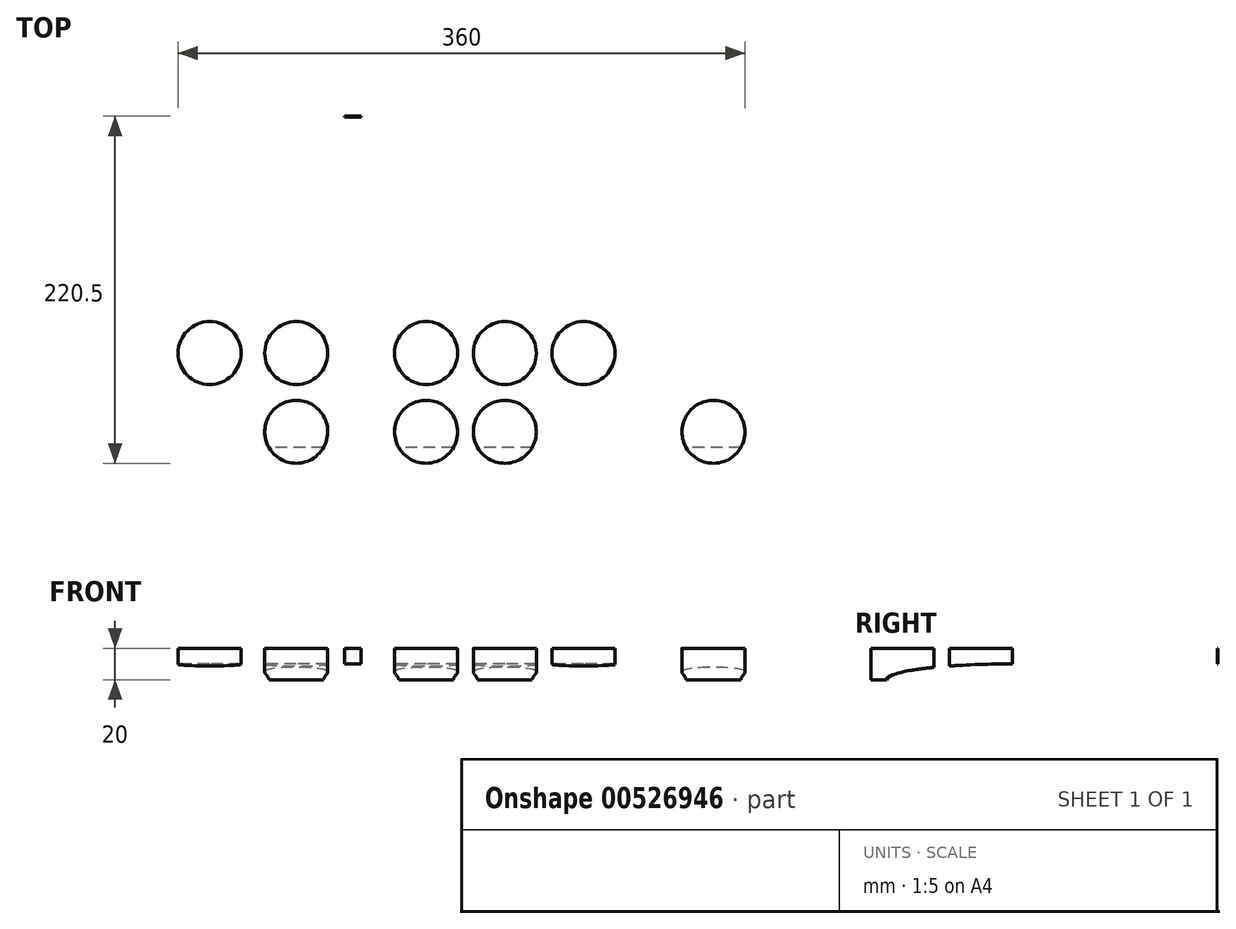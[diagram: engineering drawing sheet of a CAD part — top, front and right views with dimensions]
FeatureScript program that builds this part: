
annotation { "Feature Type Name" : "Feature", "Feature Type Description" : "" }
export const myFeature = defineFeature(function(context is Context, id is Id, definition is map)
    precondition{}
    {
        {
            var Q0;
            Q0=qCreatedBy(makeId("Top.planeOp"),FACE);
            var sketch = newSketch(context, id + "F0", { "sketchPlane" : qUnion([Q0])});
            skLineSegment(sketch, "E0.bottom", {"start": v(-365, 200) * mm, "end": v(365, 200) * mm});
            skLineSegment(sketch, "E0.top", {"start": v(-365, -200) * mm, "end": v(365, -200) * mm});
            skLineSegment(sketch, "E0.left", {"start": v(-365, 200) * mm, "end": v(-365, -200) * mm});
            skLineSegment(sketch, "E0.right", {"start": v(365, 200) * mm, "end": v(365, -200) * mm});
            skPoint(sketch, "E0.middle", {"position": v(0, 0) * mm});
            skEllipticalArc(sketch, "E1", {});
            skEllipticalArc(sketch, "E2.MirrorCS", {});
            skEllipticalArc(sketch, "E3.MirrorCS", {});
            skEllipticalArc(sketch, "E4.MirrorCS", {});
            skLineSegment(sketch, "E5", {"start": v(-365, 200) * mm, "end": v(-105, 200) * mm});
            skLineSegment(sketch, "E6", {"start": v(-365, 200) * mm, "end": v(-365, 50) * mm});
            skLineSegment(sketch, "E7", {"start": v(-365, -200) * mm, "end": v(-365, -50) * mm});
            skLineSegment(sketch, "E8", {"start": v(-365, -200) * mm, "end": v(-182.5, -200) * mm});
            skLineSegment(sketch, "E9", {"start": v(365, 200) * mm, "end": v(105, 200) * mm});
            skLineSegment(sketch, "E10", {"start": v(182.5, -200.11) * mm, "end": v(365, -200) * mm});
            skPoint(sketch, "E11", {"position": v(0, 200) * mm});
            skLineSegment(sketch, "E12", {"start": v(0, 200) * mm, "end": v(-130, 200) * mm});
            skLineSegment(sketch, "E13.MirrorCS", {"start": v(0, -200) * mm, "end": v(-130, -200) * mm});
            skLineSegment(sketch, "E14.MirrorCS", {"start": v(5, 200) * mm, "end": v(130, 200) * mm});
            skLineSegment(sketch, "E15.MirrorCS", {"start": v(-72.5, -200) * mm, "end": v(52.5, -200) * mm});
            skCircle(sketch, "E16", {"center": v(-278.75, 100) * mm, "radius": 20 * mm});
            skCircle(sketch, "E17", {"center": v(-223.75, 150) * mm, "radius": 20 * mm});
            skCircle(sketch, "E18", {"center": v(-223.75, 100) * mm, "radius": 20 * mm});
            skCircle(sketch, "E19", {"center": v(-141.25, 100) * mm, "radius": 20 * mm});
            skCircle(sketch, "E20", {"center": v(-141.25, 150) * mm, "radius": 20 * mm});
            skCircle(sketch, "E21", {"center": v(-91.25, 100) * mm, "radius": 20 * mm});
            skCircle(sketch, "E22", {"center": v(-91.25, 150) * mm, "radius": 20 * mm});
            skCircle(sketch, "E23", {"center": v(-41.25, 100) * mm, "radius": 20 * mm});
            skCircle(sketch, "E24.MirrorC", {"center": v(-41.25, 150) * mm, "radius": 20 * mm});
            skCircle(sketch, "E25.MirrorC", {"center": v(-278.75, -100) * mm, "radius": 20 * mm});
            skCircle(sketch, "E26.MirrorC", {"center": v(-223.75, -150) * mm, "radius": 20 * mm});
            skCircle(sketch, "E27.MirrorC", {"center": v(-223.75, -100) * mm, "radius": 20 * mm});
            skCircle(sketch, "E28.MirrorC", {"center": v(-141.25, -100) * mm, "radius": 20 * mm});
            skCircle(sketch, "E29.MirrorC", {"center": v(-141.25, -150) * mm, "radius": 20 * mm});
            skCircle(sketch, "E30.MirrorC", {"center": v(-91.25, -100) * mm, "radius": 20 * mm});
            skCircle(sketch, "E31.MirrorC", {"center": v(-41.25, -100) * mm, "radius": 20 * mm});
            skCircle(sketch, "E32.MirrorC", {"center": v(-91.25, -150) * mm, "radius": 20 * mm});
            skCircle(sketch, "E33.MirrorC", {"center": v(-41.25, -150) * mm, "radius": 20 * mm});
            skCircle(sketch, "E34.MirrorC", {"center": v(-222.5, -10) * mm, "radius": 20 * mm});
            skLineSegment(sketch, "E35.bottom", {"start": v(210, 15) * mm, "end": v(-210, 15) * mm});
            skLineSegment(sketch, "E35.top", {"start": v(210, -15) * mm, "end": v(-210, -15) * mm});
            skLineSegment(sketch, "E35.left", {"start": v(210, 15) * mm, "end": v(210, -15) * mm});
            skLineSegment(sketch, "E35.right", {"start": v(-210, 15) * mm, "end": v(-210, -15) * mm});
            skLineSegment(sketch, "E36", {"start": v(-365, -50) * mm, "end": v(365, -50) * mm});
            skLineSegment(sketch, "E37", {"start": v(-365, 50) * mm, "end": v(365, 50) * mm});
            skLineSegment(sketch, "E38", {"start": v(-182.5, -200) * mm, "end": v(-182.5, -40.61) * mm});
            skLineSegment(sketch, "E39", {"start": v(0, -200) * mm, "end": v(0, -50) * mm});
            skLineSegment(sketch, "E40", {"start": v(182.5, -200.11) * mm, "end": v(182.4, -40.7) * mm});
            skLineSegment(sketch, "E41.trimOffspring", {"start": v(-182.5, 40.61) * mm, "end": v(-182.5, 200) * mm});
            skLineSegment(sketch, "E42.trimOffspring", {"start": v(-182.5, -15) * mm, "end": v(-182.5, 15) * mm});
            skLineSegment(sketch, "E43.trimOffspring", {"start": v(182.39, -15) * mm, "end": v(182.37, 15) * mm});
            skLineSegment(sketch, "E44.trimOffspring", {"start": v(182.35, 40.73) * mm, "end": v(182.25, 200) * mm});
            skCircle(sketch, "E45", {"center": v(-272.5, 10) * mm, "radius": 20 * mm});
            skCircle(sketch, "E46.MirrorC", {"center": v(-322.5, -8.74) * mm, "radius": 20 * mm});
            skCircle(sketch, "E47.MirrorC", {"center": v(-142.5, -10) * mm, "radius": 20 * mm});
            skCircle(sketch, "E48.MirrorC", {"center": v(-92.5, 10) * mm, "radius": 20 * mm});
            skCircle(sketch, "E49.MirrorC", {"center": v(-42.5, -8.74) * mm, "radius": 20 * mm});
            skCircle(sketch, "E50.MirrorC", {"center": v(42.5, -8.74) * mm, "radius": 20 * mm});
            skCircle(sketch, "E51.MirrorC", {"center": v(142.5, -10) * mm, "radius": 20 * mm});
            skCircle(sketch, "E52.MirrorC", {"center": v(92.5, 10) * mm, "radius": 20 * mm});
            skCircle(sketch, "E53.MirrorC", {"center": v(222.5, -10) * mm, "radius": 20 * mm});
            skCircle(sketch, "E54.MirrorC", {"center": v(272.5, 10) * mm, "radius": 20 * mm});
            skCircle(sketch, "E55.MirrorC", {"center": v(322.5, -8.74) * mm, "radius": 20 * mm});
            skCircle(sketch, "E56.MirrorC", {"center": v(223.75, -100) * mm, "radius": 20 * mm});
            skCircle(sketch, "E57.MirrorC", {"center": v(223.75, -150) * mm, "radius": 20 * mm});
            skCircle(sketch, "E58.MirrorC", {"center": v(278.75, -100) * mm, "radius": 20 * mm});
            skCircle(sketch, "E59.MirrorC", {"center": v(141.25, -100) * mm, "radius": 20 * mm});
            skCircle(sketch, "E60.MirrorC", {"center": v(141.25, -150) * mm, "radius": 20 * mm});
            skCircle(sketch, "E61.MirrorC", {"center": v(91.25, -150) * mm, "radius": 20 * mm});
            skCircle(sketch, "E62.MirrorC", {"center": v(91.25, -100) * mm, "radius": 20 * mm});
            skCircle(sketch, "E63.MirrorC", {"center": v(41.25, -100) * mm, "radius": 20 * mm});
            skCircle(sketch, "E64.MirrorC", {"center": v(41.25, -150) * mm, "radius": 20 * mm});
            skCircle(sketch, "E65.MirrorC", {"center": v(41.25, 100) * mm, "radius": 20 * mm});
            skCircle(sketch, "E66.MirrorC", {"center": v(91.25, 100) * mm, "radius": 20 * mm});
            skCircle(sketch, "E67.MirrorC", {"center": v(141.25, 100) * mm, "radius": 20 * mm});
            skCircle(sketch, "E68.MirrorC", {"center": v(223.75, 100) * mm, "radius": 20 * mm});
            skCircle(sketch, "E69.MirrorC", {"center": v(278.75, 100) * mm, "radius": 20 * mm});
            skCircle(sketch, "E70.MirrorC", {"center": v(223.75, 150) * mm, "radius": 20 * mm});
            skCircle(sketch, "E71.MirrorC", {"center": v(141.25, 150) * mm, "radius": 20 * mm});
            skCircle(sketch, "E72.MirrorC", {"center": v(91.25, 150) * mm, "radius": 20 * mm});
            skCircle(sketch, "E73.MirrorC", {"center": v(41.25, 150) * mm, "radius": 20 * mm});
            const initialGuessF0  = {"E1": [0.215000023161019, -0.00011114199246731203, 0, -1, 0.20000000103052606, 0.15, 6.249845643425636, 1.5707963267948966], "E2.MirrorCS": [-0.215, -0.00011114199246737072, 0, -1, 0.2, 0.15, 4.711833270393751, 0.03333950926130193], "E3.MirrorCS": [-0.215, 0.00011114199246727815, 0, 1, 0.2, 0.15, 6.249845797918284, 1.5707963267948966], "E4.MirrorCS": [0.215, 0.00011114199246735796, 0, 1, 0.2, 0.15, 4.711277560231201, 0.03333950926130226]};
            skSetInitialGuess(sketch, initialGuessF0);
            skSolve(sketch);
        }
        {
            var Q0;
            Q0=qCreatedBy(makeId("Top.planeOp"),FACE);
            cPlane(context, id + "F1", {"entities" : qUnion([Q0]), "cplaneType" : CPlaneType.OFFSET, "offset" : 20 * mm, "width" : 150 * mm, "height" : 150 * mm});
        }
        {
            var Q0;
            Q0=qCreatedBy(id+"F1.planeOp",FACE);
            var sketch = newSketch(context, id + "F2", { "sketchPlane" : qUnion([Q0])});
            skLineSegment(sketch, "E74.bottom", {"start": v(0, 0) * mm, "end": v(365, 0) * mm});
            skLineSegment(sketch, "E74.top", {"start": v(0, -200) * mm, "end": v(210, -200) * mm});
            skLineSegment(sketch, "E74.left", {"start": v(0, 0) * mm, "end": v(0, -200) * mm});
            skLineSegment(sketch, "E75", {"start": v(0, -15) * mm, "end": v(364.58, -15) * mm});
            skLineSegment(sketch, "E76", {"start": v(0, -170) * mm, "end": v(294.02, -170) * mm});
            skLineSegment(sketch, "E77", {"start": v(330, 0) * mm, "end": v(330, -128.4) * mm});
            skLineSegment(sketch, "E78", {"start": v(215, 0) * mm, "end": v(215, -200) * mm});
            skPoint(sketch, "E79", {"position": v(215, -200) * mm});
            skPoint(sketch, "E80", {"position": v(365, 0) * mm});
            skLineSegment(sketch, "E81", {"start": v(275, 0) * mm, "end": v(275, -183.3) * mm});
            skLineSegment(sketch, "E82", {"start": v(275, -140) * mm, "end": v(322.12, -140) * mm});
            skPoint(sketch, "E83", {"position": v(215, -170) * mm});
            skPoint(sketch, "E84", {"position": v(330, 0) * mm});
            skPoint(sketch, "E85", {"position": v(275, -140) * mm});
            skPoint(sketch, "E86", {"position": v(330, -140) * mm});
            skPoint(sketch, "E87", {"position": v(275, -185) * mm});
            skLineSegment(sketch, "E88", {"start": v(315, -149.07) * mm, "end": v(315, 0) * mm});
            skLineSegment(sketch, "E89", {"start": v(210, 0) * mm, "end": v(210, -200) * mm});
            skEllipticalArc(sketch, "E90.trimOffspring", {});
            skEllipticalArc(sketch, "E91", {});
            skPoint(sketch, "E92.orphan", {"position": v(365, -170) * mm});
            skPoint(sketch, "E93.trimOffspring.end.orphan", {"position": v(330, -200) * mm});
            skPoint(sketch, "E94.orphan", {"position": v(365, -200) * mm});
            skPoint(sketch, "E95.orphan", {"position": v(365, -15) * mm});
            skLineSegment(sketch, "E96.MirrorCS", {"start": v(0, 0) * mm, "end": v(-365, 0) * mm});
            skLineSegment(sketch, "E97.MirrorCS", {"start": v(0, -15) * mm, "end": v(-364.58, -15) * mm});
            skLineSegment(sketch, "E98.MirrorCS", {"start": v(0, -170) * mm, "end": v(-294.02, -170) * mm});
            skLineSegment(sketch, "E99.MirrorCS", {"start": v(0, -200) * mm, "end": v(-210, -200) * mm});
            skLineSegment(sketch, "E100.MirrorCS", {"start": v(-210, 0) * mm, "end": v(-210, -200) * mm});
            skLineSegment(sketch, "E101.MirrorCS", {"start": v(-215, 0) * mm, "end": v(-215, -200) * mm});
            skEllipticalArc(sketch, "E102.MirrorCS", {});
            skEllipticalArc(sketch, "E103.MirrorCS", {});
            skLineSegment(sketch, "E104.MirrorCS", {"start": v(-275, 0) * mm, "end": v(-275, -183.3) * mm});
            skLineSegment(sketch, "E105.MirrorCS", {"start": v(-275, -140) * mm, "end": v(-322.12, -140) * mm});
            skLineSegment(sketch, "E106.MirrorCS", {"start": v(-315, -149.07) * mm, "end": v(-315, 0) * mm});
            skLineSegment(sketch, "E107.MirrorCS", {"start": v(-330, 0) * mm, "end": v(-330, -128.4) * mm});
            skLineSegment(sketch, "E108.MirrorCS", {"start": v(0, 15) * mm, "end": v(-364.58, 15) * mm});
            skLineSegment(sketch, "E109.MirrorCS", {"start": v(0, 15) * mm, "end": v(364.58, 15) * mm});
            skEllipticalArc(sketch, "E110.MirrorCS", {});
            skLineSegment(sketch, "E111.MirrorCS", {"start": v(-330, 0) * mm, "end": v(-330, 128.4) * mm});
            skLineSegment(sketch, "E112.MirrorCS", {"start": v(-315, 149.07) * mm, "end": v(-315, 0) * mm});
            skLineSegment(sketch, "E113.MirrorCS", {"start": v(-275, 0) * mm, "end": v(-275, 183.3) * mm});
            skLineSegment(sketch, "E114.MirrorCS", {"start": v(-215, 0) * mm, "end": v(-215, 200) * mm});
            skLineSegment(sketch, "E115.MirrorCS", {"start": v(-210, 0) * mm, "end": v(-210, 200) * mm});
            skLineSegment(sketch, "E116.MirrorCS", {"start": v(0, 0) * mm, "end": v(0, 200) * mm});
            skLineSegment(sketch, "E117.MirrorCS", {"start": v(210, 0) * mm, "end": v(210, 200) * mm});
            skLineSegment(sketch, "E118.MirrorCS", {"start": v(215, 0) * mm, "end": v(215, 200) * mm});
            skLineSegment(sketch, "E119.MirrorCS", {"start": v(275, 0) * mm, "end": v(275, 183.3) * mm});
            skLineSegment(sketch, "E120.MirrorCS", {"start": v(315, 149.07) * mm, "end": v(315, 0) * mm});
            skLineSegment(sketch, "E121.MirrorCS", {"start": v(330, 0) * mm, "end": v(330, 128.4) * mm});
            skEllipticalArc(sketch, "E122.MirrorCS", {});
            skEllipticalArc(sketch, "E123.MirrorCS", {});
            skEllipticalArc(sketch, "E124.MirrorCS", {});
            skLineSegment(sketch, "E125.MirrorCS", {"start": v(-275, 140) * mm, "end": v(-322.12, 140) * mm});
            skLineSegment(sketch, "E126.MirrorCS", {"start": v(0, 170) * mm, "end": v(-294.02, 170) * mm});
            skLineSegment(sketch, "E127.MirrorCS", {"start": v(0, 170) * mm, "end": v(294.02, 170) * mm});
            skLineSegment(sketch, "E128.MirrorCS", {"start": v(0, 200) * mm, "end": v(210, 200) * mm});
            skLineSegment(sketch, "E129.MirrorCS", {"start": v(0, 200) * mm, "end": v(-210, 200) * mm});
            skLineSegment(sketch, "E130.MirrorCS", {"start": v(275, 140) * mm, "end": v(322.12, 140) * mm});
            const initialGuessF2  = {"E90.trimOffspring": [0.215, 0, 1, 0, 0.115, 0.17, 4.71238898038469, 6.283185307179586], "E91": [0.215, 0, 0, -1, 0.2, 0.15, 6.249845797918284, 1.5707963267948966], "E102.MirrorCS": [-0.215, 0, -1, 0, 0.115, 0.17, 6.283185307179586, 1.5707963267948966], "E103.MirrorCS": [-0.215, 0, 0, -1, 0.2, 0.15, 4.71238898038469, 0.03333950926130225], "E110.MirrorCS": [-0.215, 0, 0, 1, 0.2, 0.15, 6.249845797918284, 1.5707963267948966], "E122.MirrorCS": [0.215, 0, 0, 1, 0.2, 0.15, 4.71238898038469, 0.03333950926130225], "E123.MirrorCS": [0.215, 0, 1, 0, 0.115, 0.17, 6.283185307179586, 1.5707963267948966], "E124.MirrorCS": [-0.215, 0, -1, 0, 0.115, 0.17, 4.71238898038469, 6.283185307179586]};
            skSetInitialGuess(sketch, initialGuessF2);
            skSolve(sketch);
        }
        {
            var Q0;
            Q0=qCreatedBy(makeId("Right.planeOp"),FACE);
            var sketch = newSketch(context, id + "F3", { "sketchPlane" : qUnion([Q0])});
            skPoint(sketch, "E131.middle", {"position": v(0, 20) * mm});
            skPoint(sketch, "E132", {"position": v(170, 0) * mm});
            skPoint(sketch, "E133", {"position": v(160, 0) * mm});
            skLineSegment(sketch, "E134.bottom", {"start": v(15, 10.07) * mm, "end": v(80, 10.07) * mm});
            skPoint(sketch, "E135", {"position": v(80, 10.07) * mm});
            skEllipticalArc(sketch, "E136", {});
            skEllipticalArc(sketch, "E137", {});
            skLineSegment(sketch, "E138", {"start": v(0, 20) * mm, "end": v(0, 10.04) * mm});
            skLineSegment(sketch, "E139", {"start": v(0, 20) * mm, "end": v(200, 20) * mm});
            skLineSegment(sketch, "E140", {"start": v(200, 20) * mm, "end": v(0, 20) * mm});
            skLineSegment(sketch, "E141", {"start": v(160, 0) * mm, "end": v(170, 0) * mm});
            skPoint(sketch, "E142.orphan", {"position": v(-200, 20) * mm});
            skLineSegment(sketch, "E143.MirrorCS", {"start": v(-200, 20) * mm, "end": v(0, 20) * mm});
            skLineSegment(sketch, "E144.MirrorCS", {"start": v(-15, 10.07) * mm, "end": v(-80, 10.07) * mm});
            skEllipticalArc(sketch, "E145.MirrorCS", {});
            skLineSegment(sketch, "E146.MirrorCS", {"start": v(-160, 0) * mm, "end": v(-170, 0) * mm});
            skEllipticalArc(sketch, "E147.MirrorCS", {});
            skLineSegment(sketch, "E148.top", {"start": v(-15, 12) * mm, "end": v(15, 12) * mm});
            skLineSegment(sketch, "E148.left", {"start": v(-15, 10.07) * mm, "end": v(-15, 12) * mm});
            skLineSegment(sketch, "E148.right", {"start": v(15, 10.07) * mm, "end": v(15, 12) * mm});
            skLineSegment(sketch, "E149.bottom", {"start": v(15, 18) * mm, "end": v(-15, 18) * mm});
            skLineSegment(sketch, "E149.top", {"start": v(15, 12) * mm, "end": v(-15, 12) * mm});
            skLineSegment(sketch, "E149.left", {"start": v(15, 18) * mm, "end": v(15, 12) * mm});
            skLineSegment(sketch, "E149.right", {"start": v(-15, 18) * mm, "end": v(-15, 12) * mm});
            skLineSegment(sketch, "E150", {"start": v(170, 0) * mm, "end": v(170.12, 20) * mm});
            skLineSegment(sketch, "E151", {"start": v(-170, 0) * mm, "end": v(-170.12, 20) * mm});
            skLineSegment(sketch, "E152", {"start": v(-15, 12) * mm, "end": v(-15, 10.07) * mm});
            skLineSegment(sketch, "E153.bottom", {"start": v(-200, 20) * mm, "end": v(-170, 20) * mm});
            skLineSegment(sketch, "E153.top", {"start": v(-200, 0) * mm, "end": v(-170, 0) * mm});
            skLineSegment(sketch, "E153.left", {"start": v(-200, 20) * mm, "end": v(-200, 0) * mm});
            skLineSegment(sketch, "E153.right", {"start": v(-170, 20) * mm, "end": v(-170, 0) * mm});
            skLineSegment(sketch, "E154.MirrorCS", {"start": v(200, 0) * mm, "end": v(170, 0) * mm});
            skLineSegment(sketch, "E155.MirrorCS", {"start": v(200, 20) * mm, "end": v(200, 0) * mm});
            skLineSegment(sketch, "E156", {"start": v(80, 10.07) * mm, "end": v(80, 20) * mm});
            skLineSegment(sketch, "E157", {"start": v(160, 0) * mm, "end": v(160, 20) * mm});
            skLineSegment(sketch, "E158", {"start": v(149.2, 20) * mm, "end": v(149.2, 5.05) * mm});
            skLineSegment(sketch, "E159", {"start": v(140.08, 20) * mm, "end": v(140.08, 6.65) * mm});
            skLineSegment(sketch, "E160", {"start": v(128.23, 20) * mm, "end": v(128.23, 8.04) * mm});
            skLineSegment(sketch, "E161", {"start": v(102.69, 20) * mm, "end": v(102.69, 9.66) * mm});
            skLineSegment(sketch, "E162.MirrorCS", {"start": v(-80, 10.07) * mm, "end": v(-80, 20) * mm});
            skLineSegment(sketch, "E163.MirrorCS", {"start": v(-102.69, 20) * mm, "end": v(-102.69, 9.66) * mm});
            skLineSegment(sketch, "E164.MirrorCS", {"start": v(-128.23, 20) * mm, "end": v(-128.23, 8.04) * mm});
            skLineSegment(sketch, "E165.MirrorCS", {"start": v(-140.08, 20) * mm, "end": v(-140.08, 6.65) * mm});
            skLineSegment(sketch, "E166.MirrorCS", {"start": v(-149.2, 20) * mm, "end": v(-149.2, 5.05) * mm});
            skLineSegment(sketch, "E167.MirrorCS", {"start": v(-160, 0) * mm, "end": v(-160, 20) * mm});
            skLineSegment(sketch, "E168", {"start": v(45, 20) * mm, "end": v(45, 10.07) * mm});
            skLineSegment(sketch, "E169.MirrorCS", {"start": v(-45, 20) * mm, "end": v(-45, 10.07) * mm});
            const initialGuessF3  = {"E136": [0.17012490332126617, 0.02, -0.006245044279577429, -0.9999804995208388, 0.020000390017188747, 0.02987581400604767, 6.283185307179586, 1.580124845260153], "E137": [0.08, 0, 0, 1, 0.01007139225942586, 0.08, 4.71238898038469, 6.283185307179586], "E145.MirrorCS": [-0.08, 0, 0, 1, 0.01007139225942586, 0.08, 6.283185307179586, 1.5707963267948966], "E147.MirrorCS": [-0.17012490332126617, 0.02, 0.006245044279579518, -0.9999804995208388, 0.020000390017188747, 0.02987581400604767, 4.703060461919433, 6.283185307179586]};
            skSetInitialGuess(sketch, initialGuessF3);
            skSolve(sketch);
        }
        {
            var Q0;
            Q0=qCreatedBy(makeId("Front.planeOp"),FACE);
            var sketch = newSketch(context, id + "F4", { "sketchPlane" : qUnion([Q0])});
            skLineSegment(sketch, "E170", {"start": v(0, 20) * mm, "end": v(365, 20) * mm});
            skPoint(sketch, "E171", {"position": v(210, 20) * mm});
            skLineSegment(sketch, "E172", {"start": v(210, 18) * mm, "end": v(210, 12) * mm});
            skPoint(sketch, "E173", {"position": v(315, 20) * mm});
            skLineSegment(sketch, "E174", {"start": v(315, 18) * mm, "end": v(315, 0) * mm});
            skLineSegment(sketch, "E175", {"start": v(0, 12) * mm, "end": v(0, 20) * mm});
            skLineSegment(sketch, "E176", {"start": v(210, 12) * mm, "end": v(0, 12) * mm});
            skPoint(sketch, "E177", {"position": v(365.07, 0) * mm});
            skPoint(sketch, "E178", {"position": v(365, 20) * mm});
            skEllipticalArc(sketch, "E179", {});
            skLineSegment(sketch, "E180", {"start": v(315, 18) * mm, "end": v(210, 18) * mm});
            skLineSegment(sketch, "E181.MirrorCS", {"start": v(0, 20) * mm, "end": v(-365, 20) * mm});
            skLineSegment(sketch, "E182.MirrorCS", {"start": v(-210, 12) * mm, "end": v(0, 12) * mm});
            skLineSegment(sketch, "E183.MirrorCS", {"start": v(-210, 18) * mm, "end": v(-210, 12) * mm});
            skLineSegment(sketch, "E184.MirrorCS", {"start": v(-315, 18) * mm, "end": v(-210, 18) * mm});
            skLineSegment(sketch, "E185.MirrorCS", {"start": v(-315, 18) * mm, "end": v(-315, 0) * mm});
            skEllipticalArc(sketch, "E186.MirrorCS", {});
            skPoint(sketch, "E187", {"position": v(245, 20) * mm});
            skPoint(sketch, "E188", {"position": v(245, 10.07) * mm});
            skPoint(sketch, "E189", {"position": v(325, 20) * mm});
            skPoint(sketch, "E190", {"position": v(335, 20) * mm});
            skLineSegment(sketch, "E191", {"start": v(335, 20) * mm, "end": v(335, 10.07) * mm});
            skLineSegment(sketch, "E192", {"start": v(335, 10.07) * mm, "end": v(0, 10.07) * mm});
            skLineSegment(sketch, "E193.MirrorCS", {"start": v(-335, 10.07) * mm, "end": v(0, 10.07) * mm});
            skLineSegment(sketch, "E194.MirrorCS", {"start": v(-335, 20) * mm, "end": v(-335, 10.07) * mm});
            skLineSegment(sketch, "E195", {"start": v(365, 20) * mm, "end": v(365.07, 0) * mm});
            skLineSegment(sketch, "E196", {"start": v(315, 0) * mm, "end": v(365.07, 0) * mm});
            skLineSegment(sketch, "E197.MirrorCS", {"start": v(-365, 20) * mm, "end": v(-365.07, 0) * mm});
            skLineSegment(sketch, "E198.MirrorCS", {"start": v(-315, 0) * mm, "end": v(-365.07, 0) * mm});
            skLineSegment(sketch, "E199", {"start": v(335, 10.07) * mm, "end": v(335, 1.67) * mm});
            skLineSegment(sketch, "E200.MirrorCS", {"start": v(-335, 10.07) * mm, "end": v(-335, 1.67) * mm});
            skLineSegment(sketch, "E201", {"start": v(-315, 18) * mm, "end": v(-315, 20) * mm});
            skLineSegment(sketch, "E202", {"start": v(-210, 18) * mm, "end": v(-210, 20) * mm});
            skLineSegment(sketch, "E203.MirrorCS", {"start": v(210, 18) * mm, "end": v(210, 20) * mm});
            skLineSegment(sketch, "E204.MirrorCS", {"start": v(315, 18) * mm, "end": v(315, 20) * mm});
            skPoint(sketch, "E205", {"position": v(275, 20) * mm});
            skPoint(sketch, "E206.MirrorP", {"position": v(-275, 20) * mm});
            skLineSegment(sketch, "E207", {"start": v(275, 20) * mm, "end": v(275, 18) * mm});
            skLineSegment(sketch, "E208.MirrorCS", {"start": v(-275, 20) * mm, "end": v(-275, 18) * mm});
            skPoint(sketch, "E209", {"position": v(-333.25, 14.9) * mm});
            skPoint(sketch, "E210", {"position": v(-218.12, 14.9) * mm});
            skPoint(sketch, "E211", {"position": v(-78.75, 14.9) * mm});
            const initialGuessF4  = {"E179": [0.315, 0.02, 1, 0, 0.05, 0.02, 4.71238898038469, 0], "E186.MirrorCS": [-0.315, 0.02, -1, 0, 0.05, 0.02, 0, 1.5707963267948966]};
            skSetInitialGuess(sketch, initialGuessF4);
            skSolve(sketch);
        }
        {
            var Q0;
            Q0=qSketchRegion(id+"F2",true);
            var Q1;
            {var subQ0=sQuery(id+"F2.wireOp",EDGE,"E125.MirrorCS");var subQ1=sQuery(id+"F2.wireOp",EDGE,"E112.MirrorCS");var subQ2=makeQuery(id+"F2.imprint","INTERSECT",VERTEX,{"derivedFrom":[subQ1,subQ0]});Q1=makeQuery(id+"F2.imprint","IMPRINT",FACE,{"disambiguationData":[TD([[makeQuery(id+"F2.imprint","IMPRINT",EDGE,{"disambiguationData":[TD([[subQ2,-1.0]])],"derivedFrom":subQ1}),1.0]])]});}
            var Q2;
            {var subQ0=sQuery(id+"F2.wireOp",EDGE,"E124.MirrorCS");var subQ1=sQuery(id+"F2.wireOp",EDGE,"E113.MirrorCS");var subQ2=makeQuery(id+"F2.imprint","INTERSECT",VERTEX,{"derivedFrom":[subQ1,subQ0]});Q2=makeQuery(id+"F2.imprint","IMPRINT",FACE,{"disambiguationData":[TD([[makeQuery(id+"F2.imprint","IMPRINT",EDGE,{"disambiguationData":[TD([[subQ2,-1.0]])],"derivedFrom":subQ1}),-1.0]])]});}
            var Q3;
            {var subQ0=sQuery(id+"F2.wireOp",EDGE,"E123.MirrorCS");var subQ1=sQuery(id+"F2.wireOp",EDGE,"E119.MirrorCS");var subQ2=makeQuery(id+"F2.imprint","INTERSECT",VERTEX,{"derivedFrom":[subQ1,subQ0]});Q3=makeQuery(id+"F2.imprint","IMPRINT",FACE,{"disambiguationData":[TD([[makeQuery(id+"F2.imprint","IMPRINT",EDGE,{"disambiguationData":[TD([[subQ2,-1.0]])],"derivedFrom":subQ1}),1.0]])]});}
            var Q4;
            {var subQ0=sQuery(id+"F2.wireOp",EDGE,"E130.MirrorCS");var subQ1=sQuery(id+"F2.wireOp",EDGE,"E120.MirrorCS");var subQ2=makeQuery(id+"F2.imprint","INTERSECT",VERTEX,{"derivedFrom":[subQ1,subQ0]});Q4=makeQuery(id+"F2.imprint","IMPRINT",FACE,{"disambiguationData":[TD([[makeQuery(id+"F2.imprint","IMPRINT",EDGE,{"disambiguationData":[TD([[subQ2,-1.0]])],"derivedFrom":subQ1}),-1.0]])]});}
            var Q5;
            {var subQ0=sQuery(id+"F2.wireOp",EDGE,"E90.trimOffspring");var subQ1=sQuery(id+"F2.wireOp",EDGE,"E82");var subQ2=makeQuery(id+"F2.imprint","INTERSECT",VERTEX,{"derivedFrom":[subQ1,subQ0]});Q5=makeQuery(id+"F2.imprint","IMPRINT",FACE,{"disambiguationData":[TD([[makeQuery(id+"F2.imprint","IMPRINT",EDGE,{"disambiguationData":[TD([[subQ2,-1.0]])],"derivedFrom":subQ1}),1.0]])]});}
            var Q6;
            {var subQ1=sQuery(id+"F2.wireOp",EDGE,"E76");var subQ3=sQuery(id+"F2.wireOp",EDGE,"E81");var subQ4=makeQuery(id+"F2.imprint","INTERSECT",VERTEX,{"derivedFrom":[subQ1,subQ3]});Q6=makeQuery(id+"F2.imprint","IMPRINT",FACE,{"disambiguationData":[TD([[makeQuery(id+"F2.imprint","IMPRINT",EDGE,{"disambiguationData":[TD([[subQ4,1.0]])],"derivedFrom":subQ3}),-1.0]])]});}
            var Q7;
            {var subQ1=sQuery(id+"F2.wireOp",EDGE,"E98.MirrorCS");var subQ3=sQuery(id+"F2.wireOp",EDGE,"E104.MirrorCS");var subQ4=makeQuery(id+"F2.imprint","INTERSECT",VERTEX,{"derivedFrom":[subQ1,subQ3]});Q7=makeQuery(id+"F2.imprint","IMPRINT",FACE,{"disambiguationData":[TD([[makeQuery(id+"F2.imprint","IMPRINT",EDGE,{"disambiguationData":[TD([[subQ4,1.0]])],"derivedFrom":subQ3}),1.0]])]});}
            var Q8;
            {var subQ0=sQuery(id+"F2.wireOp",EDGE,"E106.MirrorCS");var subQ1=sQuery(id+"F2.wireOp",EDGE,"E102.MirrorCS");var subQ2=makeQuery(id+"F2.imprint","INTERSECT",VERTEX,{"derivedFrom":[subQ1,subQ0]});Q8=makeQuery(id+"F2.imprint","IMPRINT",FACE,{"disambiguationData":[TD([[makeQuery(id+"F2.imprint","IMPRINT",EDGE,{"disambiguationData":[TD([[subQ2,-1.0]])],"derivedFrom":subQ1}),-1.0]])]});}
            extrude(context, id + "F5", {"entities" : qUnion([Q0, Q1, Q2, Q3, Q4, Q5, Q6, Q7, Q8]), "oppositeDirection" : true, "depth" : 20 * mm, "offsetDistance" : 25 * mm});
        }
        {
            var Q0;
            {var subQ0=sQuery(id+"F3.wireOp",EDGE,"E149.right");Q0=makeQuery(id+"F3.imprint","IMPRINT",FACE,{"disambiguationData":[TD([[makeQuery(id+"F3.imprint","IMPRINT",EDGE,{"derivedFrom":subQ0}),-1.0]])]});}
            var Q1;
            {var subQ0=sQuery(id+"F3.wireOp",EDGE,"E149.left");Q1=makeQuery(id+"F3.imprint","IMPRINT",FACE,{"disambiguationData":[TD([[makeQuery(id+"F3.imprint","IMPRINT",EDGE,{"derivedFrom":subQ0}),1.0]])]});}
            extrude(context, id + "F6", {"entities" : qUnion([Q0, Q1]), "operationType" : NewBodyOperationType.ADD, "depth" : 420 * mm, "offsetDistance" : 25 * mm, "symmetric" : true});
        }
        {
            var Q0;
            {var subQ0=sQuery(id+"F3.wireOp",EDGE,"E156");Q0=makeQuery(id+"F3.imprint","IMPRINT",FACE,{"disambiguationData":[TD([[makeQuery(id+"F3.imprint","IMPRINT",EDGE,{"derivedFrom":subQ0}),-1.0]])]});}
            var Q1;
            {var subQ0=sQuery(id+"F3.wireOp",EDGE,"E160");Q1=makeQuery(id+"F3.imprint","IMPRINT",FACE,{"disambiguationData":[TD([[makeQuery(id+"F3.imprint","IMPRINT",EDGE,{"derivedFrom":subQ0}),-1.0]])]});}
            var Q2;
            {var subQ0=sQuery(id+"F3.wireOp",EDGE,"E159");Q2=makeQuery(id+"F3.imprint","IMPRINT",FACE,{"disambiguationData":[TD([[makeQuery(id+"F3.imprint","IMPRINT",EDGE,{"derivedFrom":subQ0}),-1.0]])]});}
            var Q3;
            {var subQ0=sQuery(id+"F3.wireOp",EDGE,"E158");Q3=makeQuery(id+"F3.imprint","IMPRINT",FACE,{"disambiguationData":[TD([[makeQuery(id+"F3.imprint","IMPRINT",EDGE,{"derivedFrom":subQ0}),-1.0]])]});}
            var Q4;
            {var subQ0=sQuery(id+"F3.wireOp",EDGE,"E157");Q4=makeQuery(id+"F3.imprint","IMPRINT",FACE,{"disambiguationData":[TD([[makeQuery(id+"F3.imprint","IMPRINT",EDGE,{"derivedFrom":subQ0}),1.0]])]});}
            var Q5;
            Q5=makeQuery(id+"F3.imprint","IMPRINT",FACE,{"disambiguationData":[TD([[makeQuery(id+"F3.imprint","IMPRINT",EDGE,{"derivedFrom":sQuery(id+"F3.wireOp",EDGE,"E141")}),1.0]])]});
            var Q6;
            {var subQ0=sQuery(id+"F3.wireOp",EDGE,"E162.MirrorCS");Q6=makeQuery(id+"F3.imprint","IMPRINT",FACE,{"disambiguationData":[TD([[makeQuery(id+"F3.imprint","IMPRINT",EDGE,{"derivedFrom":subQ0}),1.0]])]});}
            var Q7;
            {var subQ0=sQuery(id+"F3.wireOp",EDGE,"E163.MirrorCS");Q7=makeQuery(id+"F3.imprint","IMPRINT",FACE,{"disambiguationData":[TD([[makeQuery(id+"F3.imprint","IMPRINT",EDGE,{"derivedFrom":subQ0}),-1.0]])]});}
            var Q8;
            {var subQ0=sQuery(id+"F3.wireOp",EDGE,"E164.MirrorCS");Q8=makeQuery(id+"F3.imprint","IMPRINT",FACE,{"disambiguationData":[TD([[makeQuery(id+"F3.imprint","IMPRINT",EDGE,{"derivedFrom":subQ0}),-1.0]])]});}
            var Q9;
            {var subQ0=sQuery(id+"F3.wireOp",EDGE,"E165.MirrorCS");Q9=makeQuery(id+"F3.imprint","IMPRINT",FACE,{"disambiguationData":[TD([[makeQuery(id+"F3.imprint","IMPRINT",EDGE,{"derivedFrom":subQ0}),-1.0]])]});}
            var Q10;
            {var subQ0=sQuery(id+"F3.wireOp",EDGE,"E166.MirrorCS");Q10=makeQuery(id+"F3.imprint","IMPRINT",FACE,{"disambiguationData":[TD([[makeQuery(id+"F3.imprint","IMPRINT",EDGE,{"derivedFrom":subQ0}),-1.0]])]});}
            var Q11;
            Q11=makeQuery(id+"F3.imprint","IMPRINT",FACE,{"disambiguationData":[TD([[makeQuery(id+"F3.imprint","IMPRINT",EDGE,{"derivedFrom":sQuery(id+"F3.wireOp",EDGE,"E146.MirrorCS")}),-1.0]])]});
            var Q12;
            {var subQ0=sQuery(id+"F3.wireOp",EDGE,"E156");Q12=makeQuery(id+"F3.imprint","IMPRINT",FACE,{"disambiguationData":[TD([[makeQuery(id+"F3.imprint","IMPRINT",EDGE,{"derivedFrom":subQ0}),1.0]])]});}
            var Q13;
            {var subQ0=sQuery(id+"F3.wireOp",EDGE,"E162.MirrorCS");Q13=makeQuery(id+"F3.imprint","IMPRINT",FACE,{"disambiguationData":[TD([[makeQuery(id+"F3.imprint","IMPRINT",EDGE,{"derivedFrom":subQ0}),-1.0]])]});}
            extrude(context, id + "F7", {"entities" : qUnion([Q0, Q1, Q2, Q3, Q4, Q5, Q6, Q7, Q8, Q9, Q10, Q11, Q12, Q13]), "operationType" : NewBodyOperationType.ADD, "depth" : 520 * mm, "offsetDistance" : 25 * mm, "symmetric" : true});
        }
        {
            var Q0;
            Q0=makeQuery(id+"F4.imprint","IMPRINT",FACE,{"disambiguationData":[TD([[makeQuery(id+"F4.imprint","IMPRINT",EDGE,{"derivedFrom":sQuery(id+"F4.wireOp",EDGE,"E172")}),-1.0]])]});
            var Q1;
            {var subQ1=sQuery(id+"F4.wireOp",EDGE,"E179");Q1=makeQuery(id+"F4.imprint","IMPRINT",FACE,{"disambiguationData":[TD([[makeQuery(id+"F4.imprint","IMPRINT",EDGE,{"derivedFrom":subQ1}),1.0]])]});}
            var Q2;
            {var subQ2=sQuery(id+"F4.wireOp",EDGE,"E175");Q2=makeQuery(id+"F4.imprint","IMPRINT",FACE,{"disambiguationData":[TD([[makeQuery(id+"F4.imprint","IMPRINT",EDGE,{"derivedFrom":subQ2}),1.0]])]});}
            var Q3;
            {var subQ0=sQuery(id+"F4.wireOp",EDGE,"E186.MirrorCS");Q3=makeQuery(id+"F4.imprint","IMPRINT",FACE,{"disambiguationData":[TD([[makeQuery(id+"F4.imprint","IMPRINT",EDGE,{"derivedFrom":subQ0}),1.0]])]});}
            extrude(context, id + "F8", {"entities" : qUnion([Q0, Q1, Q2, Q3]), "operationType" : NewBodyOperationType.ADD, "depth" : 30 * mm, "offsetDistance" : 25 * mm, "symmetric" : true});
        }
        {
            var Q0;
            {var subQ0=sQuery(id+"F3.wireOp",EDGE,"E153.left");var subQ1=sQuery(id+"F3.wireOp",EDGE,"E147.MirrorCS");var subQ2=makeQuery(id+"F3.imprint","INTERSECT",VERTEX,{"derivedFrom":[subQ1,subQ0]});Q0=makeQuery(id+"F3.imprint","IMPRINT",FACE,{"disambiguationData":[TD([[makeQuery(id+"F3.imprint","IMPRINT",EDGE,{"disambiguationData":[TD([[subQ2,-1.0]])],"derivedFrom":subQ1}),-1.0]])]});}
            var Q1;
            {var subQ0=sQuery(id+"F3.wireOp",EDGE,"E155.MirrorCS");var subQ1=sQuery(id+"F3.wireOp",EDGE,"E136");var subQ2=makeQuery(id+"F3.imprint","INTERSECT",VERTEX,{"derivedFrom":[subQ1,subQ0]});Q1=makeQuery(id+"F3.imprint","IMPRINT",FACE,{"disambiguationData":[TD([[makeQuery(id+"F3.imprint","IMPRINT",EDGE,{"disambiguationData":[TD([[subQ2,1.0]])],"derivedFrom":subQ1}),-1.0]])]});}
            var Q2;
            Q2=sQuery(id+"F3.wireOp",EDGE,"E153.left");
            var Q3;
            Q3=sQuery(id+"F3.wireOp",EDGE,"E153.top");
            var Q4;
            Q4=sQuery(id+"F3.wireOp",EDGE,"E147.MirrorCS");
            extrude(context, id + "F9", {"entities" : qUnion([Q0, Q1]), "operationType" : NewBodyOperationType.REMOVE, "surfaceEntities" : qUnion([Q2, Q3, Q4]), "oppositeDirection" : true, "depth" : 730 * mm, "offsetDistance" : 25 * mm, "symmetric" : true});
        }
        {
            var Q0;
            Q0=makeQuery(id+"F4.imprint","IMPRINT",FACE,{"disambiguationData":[TD([[makeQuery(id+"F4.imprint","IMPRINT",EDGE,{"derivedFrom":sQuery(id+"F4.wireOp",EDGE,"E186.MirrorCS")}),-1.0]])]});
            var Q1;
            Q1=makeQuery(id+"F4.imprint","IMPRINT",FACE,{"disambiguationData":[TD([[makeQuery(id+"F4.imprint","IMPRINT",EDGE,{"derivedFrom":sQuery(id+"F4.wireOp",EDGE,"E179")}),-1.0]])]});
            extrude(context, id + "F10", {"entities" : qUnion([Q0, Q1]), "operationType" : NewBodyOperationType.REMOVE, "oppositeDirection" : true, "depth" : 400 * mm, "offsetDistance" : 25 * mm, "symmetric" : true});
        }
        {
            var Q0;
            Q0=makeQuery(id+"F4.imprint","IMPRINT",FACE,{"disambiguationData":[TD([[makeQuery(id+"F4.imprint","IMPRINT",EDGE,{"derivedFrom":sQuery(id+"F4.wireOp",EDGE,"E172")}),-1.0]])]});
            var Q1;
            {var subQ5=sQuery(id+"F4.wireOp",EDGE,"E199");Q1=makeQuery(id+"F4.imprint","IMPRINT",FACE,{"disambiguationData":[TD([[makeQuery(id+"F4.imprint","IMPRINT",EDGE,{"derivedFrom":subQ5}),-1.0]])]});}
            var Q2;
            {var subQ5=sQuery(id+"F4.wireOp",EDGE,"E200.MirrorCS");Q2=makeQuery(id+"F4.imprint","IMPRINT",FACE,{"disambiguationData":[TD([[makeQuery(id+"F4.imprint","IMPRINT",EDGE,{"derivedFrom":subQ5}),1.0]])]});}
            var Q3;
            {var subQ2=sQuery(id+"F4.wireOp",EDGE,"E175");Q3=makeQuery(id+"F4.imprint","IMPRINT",FACE,{"disambiguationData":[TD([[makeQuery(id+"F4.imprint","IMPRINT",EDGE,{"derivedFrom":subQ2}),1.0]])]});}
            var Q4;
            {var subQ0=sQuery(id+"F4.wireOp",EDGE,"E194.MirrorCS");Q4=makeQuery(id+"F4.imprint","IMPRINT",FACE,{"disambiguationData":[TD([[makeQuery(id+"F4.imprint","IMPRINT",EDGE,{"derivedFrom":subQ0}),1.0]])]});}
            var Q5;
            {var subQ1=sQuery(id+"F4.wireOp",EDGE,"E191");Q5=makeQuery(id+"F4.imprint","IMPRINT",FACE,{"disambiguationData":[TD([[makeQuery(id+"F4.imprint","IMPRINT",EDGE,{"derivedFrom":subQ1}),-1.0]])]});}
            extrude(context, id + "F11", {"entities" : qUnion([Q0, Q1, Q2, Q3, Q4, Q5]), "operationType" : NewBodyOperationType.ADD, "depth" : 169 * mm, "offsetDistance" : 25 * mm, "symmetric" : true});
        }
        {
            var Q0;
            Q0=makeQuery(id+"F4.imprint","IMPRINT",FACE,{"disambiguationData":[TD([[makeQuery(id+"F4.imprint","IMPRINT",EDGE,{"derivedFrom":sQuery(id+"F4.wireOp",EDGE,"E180")}),-1.0]])]});
            var Q1;
            Q1=makeQuery(id+"F4.imprint","IMPRINT",FACE,{"disambiguationData":[TD([[makeQuery(id+"F4.imprint","IMPRINT",EDGE,{"derivedFrom":sQuery(id+"F4.wireOp",EDGE,"E184.MirrorCS")}),1.0]])]});
            extrude(context, id + "F12", {"entities" : qUnion([Q0, Q1]), "operationType" : NewBodyOperationType.ADD, "depth" : 295 * mm, "offsetDistance" : 25 * mm, "symmetric" : true});
        }
        {
            var Q0;
            {var subQ0=sQuery(id+"F4.wireOp",EDGE,"E203.MirrorCS");Q0=makeQuery(id+"F4.imprint","IMPRINT",FACE,{"disambiguationData":[TD([[makeQuery(id+"F4.imprint","IMPRINT",EDGE,{"derivedFrom":subQ0}),-1.0]])]});}
            var Q1;
            {var subQ0=sQuery(id+"F4.wireOp",EDGE,"E202");Q1=makeQuery(id+"F4.imprint","IMPRINT",FACE,{"disambiguationData":[TD([[makeQuery(id+"F4.imprint","IMPRINT",EDGE,{"derivedFrom":subQ0}),1.0]])]});}
            extrude(context, id + "F13", {"entities" : qUnion([Q0, Q1]), "operationType" : NewBodyOperationType.ADD, "depth" : 350 * mm, "offsetDistance" : 25 * mm, "symmetric" : true});
        }
        {
            var Q0;
            {var subQ0=sQuery(id+"F2.wireOp",EDGE,"E122.MirrorCS");var subQ1=sQuery(id+"F2.wireOp",EDGE,"E91");Q0=makeQuery(id+"F10.boolean.opBoolean","SPLIT",EDGE,{"disambiguationData":[TD([makeQuery(id+"F9.boolean.opBoolean","COPY",FACE,{"derivedFrom":makeQuery(id+"F9.opExtrude","SWEPT_FACE",FACE,{"disambiguationData":[OSD([sQuery(id+"F3.wireOp",EDGE,"E136")])]})})])],"derivedFrom":makeQuery(id+"F5.opExtrude","CAP_EDGE",EDGE,{"disambiguationData":[OSD([subQ1,subQ0])],"isStart":false})});}
            var Q1;
            {var subQ0=sQuery(id+"F2.wireOp",EDGE,"E122.MirrorCS");var subQ1=sQuery(id+"F2.wireOp",EDGE,"E91");Q1=makeQuery(id+"F10.boolean.opBoolean","SPLIT",EDGE,{"disambiguationData":[TD([makeQuery(id+"F9.boolean.opBoolean","COPY",FACE,{"derivedFrom":makeQuery(id+"F9.opExtrude","SWEPT_FACE",FACE,{"disambiguationData":[OSD([sQuery(id+"F3.wireOp",EDGE,"E147.MirrorCS")])]})})])],"derivedFrom":makeQuery(id+"F5.opExtrude","CAP_EDGE",EDGE,{"disambiguationData":[OSD([subQ1,subQ0])],"isStart":false})});}
            var Q2;
            {var subQ0=sQuery(id+"F2.wireOp",EDGE,"E110.MirrorCS");var subQ1=sQuery(id+"F2.wireOp",EDGE,"E103.MirrorCS");Q2=makeQuery(id+"F10.boolean.opBoolean","SPLIT",EDGE,{"disambiguationData":[TD([makeQuery(id+"F9.boolean.opBoolean","COPY",FACE,{"derivedFrom":makeQuery(id+"F9.opExtrude","SWEPT_FACE",FACE,{"disambiguationData":[OSD([sQuery(id+"F3.wireOp",EDGE,"E147.MirrorCS")])]})})])],"derivedFrom":makeQuery(id+"F5.opExtrude","CAP_EDGE",EDGE,{"disambiguationData":[OSD([subQ1,subQ0])],"isStart":false})});}
            var Q3;
            {var subQ0=sQuery(id+"F2.wireOp",EDGE,"E110.MirrorCS");var subQ1=sQuery(id+"F2.wireOp",EDGE,"E103.MirrorCS");Q3=makeQuery(id+"F10.boolean.opBoolean","SPLIT",EDGE,{"disambiguationData":[TD([makeQuery(id+"F9.boolean.opBoolean","COPY",FACE,{"derivedFrom":makeQuery(id+"F9.opExtrude","SWEPT_FACE",FACE,{"disambiguationData":[OSD([sQuery(id+"F3.wireOp",EDGE,"E136")])]})})])],"derivedFrom":makeQuery(id+"F5.opExtrude","CAP_EDGE",EDGE,{"disambiguationData":[OSD([subQ1,subQ0])],"isStart":false})});}
            fillet(context, id + "F14", {"entities" : qUnion([Q0, Q1, Q2, Q3]), "radius" : 18 * mm, "tangentPropagation" : true, "allowEdgeOverflow" : false});
        }
        {
            var Q0;
            {var subQ0=sQuery(id+"F3.wireOp",EDGE,"E162.MirrorCS");Q0=makeQuery(id+"F3.imprint","IMPRINT",FACE,{"disambiguationData":[TD([[makeQuery(id+"F3.imprint","IMPRINT",EDGE,{"derivedFrom":subQ0}),-1.0]])]});}
            var Q1;
            {var subQ0=sQuery(id+"F3.wireOp",EDGE,"E156");Q1=makeQuery(id+"F3.imprint","IMPRINT",FACE,{"disambiguationData":[TD([[makeQuery(id+"F3.imprint","IMPRINT",EDGE,{"derivedFrom":subQ0}),1.0]])]});}
            extrude(context, id + "F15", {"entities" : qUnion([Q0, Q1]), "operationType" : NewBodyOperationType.ADD, "depth" : 670 * mm, "offsetDistance" : 25 * mm, "symmetric" : true});
        }
        {
            var Q0;
            {var subQ0=sQuery(id+"F3.wireOp",EDGE,"E156");Q0=makeQuery(id+"F3.imprint","IMPRINT",FACE,{"disambiguationData":[TD([[makeQuery(id+"F3.imprint","IMPRINT",EDGE,{"derivedFrom":subQ0}),-1.0]])]});}
            var Q1;
            {var subQ0=sQuery(id+"F3.wireOp",EDGE,"E162.MirrorCS");Q1=makeQuery(id+"F3.imprint","IMPRINT",FACE,{"disambiguationData":[TD([[makeQuery(id+"F3.imprint","IMPRINT",EDGE,{"derivedFrom":subQ0}),1.0]])]});}
            extrude(context, id + "F16", {"entities" : qUnion([Q0, Q1]), "operationType" : NewBodyOperationType.ADD, "depth" : 630 * mm, "offsetDistance" : 25 * mm, "symmetric" : true});
        }
        {
            var Q0;
            {var subQ0=sQuery(id+"F3.wireOp",EDGE,"E166.MirrorCS");Q0=makeQuery(id+"F3.imprint","IMPRINT",FACE,{"disambiguationData":[TD([[makeQuery(id+"F3.imprint","IMPRINT",EDGE,{"derivedFrom":subQ0}),-1.0]])]});}
            var Q1;
            {var subQ0=sQuery(id+"F3.wireOp",EDGE,"E157");Q1=makeQuery(id+"F3.imprint","IMPRINT",FACE,{"disambiguationData":[TD([[makeQuery(id+"F3.imprint","IMPRINT",EDGE,{"derivedFrom":subQ0}),1.0]])]});}
            extrude(context, id + "F17", {"entities" : qUnion([Q0, Q1]), "operationType" : NewBodyOperationType.ADD, "depth" : 550 * mm, "offsetDistance" : 25 * mm, "symmetric" : true});
        }
        {
            var Q0;
            {var subQ0=sQuery(id+"F3.wireOp",EDGE,"E158");Q0=makeQuery(id+"F3.imprint","IMPRINT",FACE,{"disambiguationData":[TD([[makeQuery(id+"F3.imprint","IMPRINT",EDGE,{"derivedFrom":subQ0}),-1.0]])]});}
            var Q1;
            {var subQ0=sQuery(id+"F3.wireOp",EDGE,"E165.MirrorCS");Q1=makeQuery(id+"F3.imprint","IMPRINT",FACE,{"disambiguationData":[TD([[makeQuery(id+"F3.imprint","IMPRINT",EDGE,{"derivedFrom":subQ0}),-1.0]])]});}
            extrude(context, id + "F18", {"entities" : qUnion([Q0, Q1]), "operationType" : NewBodyOperationType.ADD, "depth" : 600 * mm, "offsetDistance" : 25 * mm, "symmetric" : true});
        }
        {
            var Q0;
            {var subQ0=sQuery(id+"F3.wireOp",EDGE,"E159");Q0=makeQuery(id+"F3.imprint","IMPRINT",FACE,{"disambiguationData":[TD([[makeQuery(id+"F3.imprint","IMPRINT",EDGE,{"derivedFrom":subQ0}),-1.0]])]});}
            var Q1;
            {var subQ0=sQuery(id+"F3.wireOp",EDGE,"E164.MirrorCS");Q1=makeQuery(id+"F3.imprint","IMPRINT",FACE,{"disambiguationData":[TD([[makeQuery(id+"F3.imprint","IMPRINT",EDGE,{"derivedFrom":subQ0}),-1.0]])]});}
            extrude(context, id + "F19", {"entities" : qUnion([Q0, Q1]), "operationType" : NewBodyOperationType.ADD, "depth" : 620 * mm, "offsetDistance" : 25 * mm, "symmetric" : true});
        }
        {
            var Q0;
            {var subQ0=sQuery(id+"F3.wireOp",EDGE,"E163.MirrorCS");Q0=makeQuery(id+"F3.imprint","IMPRINT",FACE,{"disambiguationData":[TD([[makeQuery(id+"F3.imprint","IMPRINT",EDGE,{"derivedFrom":subQ0}),-1.0]])]});}
            var Q1;
            {var subQ0=sQuery(id+"F3.wireOp",EDGE,"E160");Q1=makeQuery(id+"F3.imprint","IMPRINT",FACE,{"disambiguationData":[TD([[makeQuery(id+"F3.imprint","IMPRINT",EDGE,{"derivedFrom":subQ0}),-1.0]])]});}
            extrude(context, id + "F20", {"entities" : qUnion([Q0, Q1]), "operationType" : NewBodyOperationType.ADD, "depth" : 620 * mm, "offsetDistance" : 25 * mm, "symmetric" : true});
        }
        {
            var Q0;
            Q0=makeQuery(id+"F5.opExtrude","CAP_EDGE",EDGE,{"disambiguationData":[OSD([sQuery(id+"F2.wireOp",EDGE,"E124.MirrorCS")])],"isStart":false});
            var Q1;
            Q1=makeQuery(id+"F5.opExtrude","CAP_EDGE",EDGE,{"disambiguationData":[OSD([sQuery(id+"F2.wireOp",EDGE,"E123.MirrorCS")])],"isStart":false});
            var Q2;
            Q2=makeQuery(id+"F5.opExtrude","CAP_EDGE",EDGE,{"disambiguationData":[OSD([sQuery(id+"F2.wireOp",EDGE,"E90.trimOffspring")])],"isStart":false});
            var Q3;
            Q3=makeQuery(id+"F5.opExtrude","CAP_EDGE",EDGE,{"disambiguationData":[OSD([sQuery(id+"F2.wireOp",EDGE,"E102.MirrorCS")])],"isStart":false});
            chamfer(context, id + "F21", {"entities" : qUnion([Q0, Q1, Q2, Q3]), "chamferType" : ChamferType.OFFSET_ANGLE, "width" : 15 * mm, "oppositeDirection" : false, "angle" : 35 * degree, "tangentPropagation" : true});
        }
        {
            var Q0;
            {var subQ0=sQuery(id+"F4.wireOp",EDGE,"E198.MirrorCS");var subQ1=sQuery(id+"F4.wireOp",EDGE,"E186.MirrorCS");var subQ2=sQuery(id+"F4.wireOp",EDGE,"E185.MirrorCS");Q0=makeQuery(id+"F11.boolean.opBoolean","MERGE",EDGE,{"derivedFrom":[makeQuery(id+"F8.opExtrude","SWEPT_EDGE",EDGE,{"disambiguationData":[OSD([subQ2,subQ1,subQ0])]}),makeQuery(id+"F11.opExtrude","SWEPT_EDGE",EDGE,{"disambiguationData":[OSD([subQ2,subQ1,subQ0])]})]});}
            chamfer(context, id + "F22", {"entities" : qUnion([Q0]), "chamferType" : ChamferType.OFFSET_ANGLE, "width" : 10 * mm, "oppositeDirection" : false, "angle" : 42 * degree, "tangentPropagation" : true});
        }
        {
            var Q0;
            {var subQ0=sQuery(id+"F4.wireOp",EDGE,"E196");var subQ1=sQuery(id+"F4.wireOp",EDGE,"E179");var subQ2=sQuery(id+"F4.wireOp",EDGE,"E174");Q0=makeQuery(id+"F11.boolean.opBoolean","MERGE",EDGE,{"derivedFrom":[makeQuery(id+"F8.opExtrude","SWEPT_EDGE",EDGE,{"disambiguationData":[OSD([subQ2,subQ1,subQ0])]}),makeQuery(id+"F11.opExtrude","SWEPT_EDGE",EDGE,{"disambiguationData":[OSD([subQ2,subQ1,subQ0])]})]});}
            chamfer(context, id + "F23", {"entities" : qUnion([Q0]), "chamferType" : ChamferType.OFFSET_ANGLE, "width" : 10 * mm, "oppositeDirection" : false, "angle" : 42 * degree, "tangentPropagation" : true});
        }
        {
            var Q0;
            {var subQ0=sQuery(id+"F0.wireOp",EDGE,"E35.top");var subQ1=sQuery(id+"F0.wireOp",EDGE,"E34.MirrorC");var subQ2=makeQuery(id+"F0.imprint","INTERSECT",VERTEX,{"derivedFrom":[subQ1,subQ0]});Q0=makeQuery(id+"F0.imprint","IMPRINT",FACE,{"disambiguationData":[TD([[makeQuery(id+"F0.imprint","IMPRINT",EDGE,{"disambiguationData":[TD([[subQ2,1.0]])],"derivedFrom":subQ1}),1.0]])]});}
            var Q1;
            {var subQ0=sQuery(id+"F0.wireOp",EDGE,"E10");var subQ3=sQuery(id+"F0.wireOp",EDGE,"E1");var subQ5=makeQuery(id+"F0.imprint","INTERSECT",VERTEX,{"disambiguationData":[OD(0.0)],"derivedFrom":[subQ3,subQ0]});Q1=makeQuery(id+"F0.imprint","IMPRINT",FACE,{"disambiguationData":[TD([[makeQuery(id+"F0.imprint","IMPRINT",EDGE,{"disambiguationData":[TD([[subQ5,-1.0]])],"derivedFrom":subQ3}),-1.0]])]});}
            var Q2;
            {var subQ0=sQuery(id+"F0.wireOp",EDGE,"E36");var subQ1=sQuery(id+"F0.wireOp",EDGE,"E0.right");var subQ2=makeQuery(id+"F0.imprint","INTERSECT",VERTEX,{"derivedFrom":[subQ1,subQ0]});Q2=makeQuery(id+"F0.imprint","IMPRINT",FACE,{"disambiguationData":[TD([[makeQuery(id+"F0.imprint","IMPRINT",EDGE,{"disambiguationData":[TD([[subQ2,1.0]])],"derivedFrom":subQ1}),-1.0]])]});}
            var Q3;
            {var subQ1=sQuery(id+"F0.wireOp",EDGE,"E0.left");var subQ3=sQuery(id+"F0.wireOp",EDGE,"E2.MirrorCS");var subQ4=makeQuery(id+"F0.imprint","INTERSECT",VERTEX,{"disambiguationData":[OD(1.0)],"derivedFrom":[subQ1,subQ3]});Q3=makeQuery(id+"F0.imprint","IMPRINT",FACE,{"disambiguationData":[TD([[makeQuery(id+"F0.imprint","IMPRINT",EDGE,{"disambiguationData":[TD([[subQ4,-1.0]])],"derivedFrom":subQ3}),-1.0]])]});}
            var Q4;
            {var subQ1=sQuery(id+"F0.wireOp",EDGE,"E0.left");var subQ3=sQuery(id+"F0.wireOp",EDGE,"E3.MirrorCS");var subQ4=makeQuery(id+"F0.imprint","INTERSECT",VERTEX,{"derivedFrom":[subQ1,subQ3]});Q4=makeQuery(id+"F0.imprint","IMPRINT",FACE,{"disambiguationData":[TD([[makeQuery(id+"F0.imprint","IMPRINT",EDGE,{"disambiguationData":[TD([[subQ4,1.0]])],"derivedFrom":subQ3}),-1.0]])]});}
            var Q5;
            {var subQ0=sQuery(id+"F0.wireOp",EDGE,"E9");var subQ1=sQuery(id+"F0.wireOp",EDGE,"E0.right");var subQ2=makeQuery(id+"F0.imprint","INTERSECT",VERTEX,{"derivedFrom":[subQ1,subQ0]});Q5=makeQuery(id+"F0.imprint","IMPRINT",FACE,{"disambiguationData":[TD([[makeQuery(id+"F0.imprint","IMPRINT",EDGE,{"disambiguationData":[TD([[subQ2,-1.0]])],"derivedFrom":subQ1}),-1.0]])]});}
            var Q6;
            Q6=makeQuery(id+"F0.imprint","IMPRINT",FACE,{"disambiguationData":[TD([[makeQuery(id+"F0.imprint","IMPRINT",EDGE,{"derivedFrom":sQuery(id+"F0.wireOp",EDGE,"E23")}),1.0]])]});
            var Q7;
            Q7=makeQuery(id+"F0.imprint","IMPRINT",FACE,{"disambiguationData":[TD([[makeQuery(id+"F0.imprint","IMPRINT",EDGE,{"derivedFrom":sQuery(id+"F0.wireOp",EDGE,"E21")}),1.0]])]});
            var Q8;
            Q8=makeQuery(id+"F0.imprint","IMPRINT",FACE,{"disambiguationData":[TD([[makeQuery(id+"F0.imprint","IMPRINT",EDGE,{"derivedFrom":sQuery(id+"F0.wireOp",EDGE,"E22")}),1.0]])]});
            var Q9;
            Q9=makeQuery(id+"F0.imprint","IMPRINT",FACE,{"disambiguationData":[TD([[makeQuery(id+"F0.imprint","IMPRINT",EDGE,{"derivedFrom":sQuery(id+"F0.wireOp",EDGE,"E24.MirrorC")}),-1.0]])]});
            var Q10;
            Q10=makeQuery(id+"F0.imprint","IMPRINT",FACE,{"disambiguationData":[TD([[makeQuery(id+"F0.imprint","IMPRINT",EDGE,{"derivedFrom":sQuery(id+"F0.wireOp",EDGE,"E30.MirrorC")}),-1.0]])]});
            var Q11;
            Q11=makeQuery(id+"F0.imprint","IMPRINT",FACE,{"disambiguationData":[TD([[makeQuery(id+"F0.imprint","IMPRINT",EDGE,{"derivedFrom":sQuery(id+"F0.wireOp",EDGE,"E31.MirrorC")}),-1.0]])]});
            var Q12;
            Q12=makeQuery(id+"F0.imprint","IMPRINT",FACE,{"disambiguationData":[TD([[makeQuery(id+"F0.imprint","IMPRINT",EDGE,{"derivedFrom":sQuery(id+"F0.wireOp",EDGE,"E33.MirrorC")}),1.0]])]});
            var Q13;
            Q13=makeQuery(id+"F0.imprint","IMPRINT",FACE,{"disambiguationData":[TD([[makeQuery(id+"F0.imprint","IMPRINT",EDGE,{"derivedFrom":sQuery(id+"F0.wireOp",EDGE,"E32.MirrorC")}),-1.0]])]});
            var Q14;
            Q14=makeQuery(id+"F0.imprint","IMPRINT",FACE,{"disambiguationData":[TD([[makeQuery(id+"F0.imprint","IMPRINT",EDGE,{"derivedFrom":sQuery(id+"F0.wireOp",EDGE,"E19")}),1.0]])]});
            var Q15;
            Q15=makeQuery(id+"F0.imprint","IMPRINT",FACE,{"disambiguationData":[TD([[makeQuery(id+"F0.imprint","IMPRINT",EDGE,{"derivedFrom":sQuery(id+"F0.wireOp",EDGE,"E20")}),1.0]])]});
            var Q16;
            Q16=makeQuery(id+"F0.imprint","IMPRINT",FACE,{"disambiguationData":[TD([[makeQuery(id+"F0.imprint","IMPRINT",EDGE,{"derivedFrom":sQuery(id+"F0.wireOp",EDGE,"E17")}),1.0]])]});
            var Q17;
            Q17=makeQuery(id+"F0.imprint","IMPRINT",FACE,{"disambiguationData":[TD([[makeQuery(id+"F0.imprint","IMPRINT",EDGE,{"derivedFrom":sQuery(id+"F0.wireOp",EDGE,"E18")}),1.0]])]});
            var Q18;
            Q18=makeQuery(id+"F0.imprint","IMPRINT",FACE,{"disambiguationData":[TD([[makeQuery(id+"F0.imprint","IMPRINT",EDGE,{"derivedFrom":sQuery(id+"F0.wireOp",EDGE,"E16")}),1.0]])]});
            var Q19;
            Q19=makeQuery(id+"F0.imprint","IMPRINT",FACE,{"disambiguationData":[TD([[makeQuery(id+"F0.imprint","IMPRINT",EDGE,{"derivedFrom":sQuery(id+"F0.wireOp",EDGE,"E28.MirrorC")}),-1.0]])]});
            var Q20;
            Q20=makeQuery(id+"F0.imprint","IMPRINT",FACE,{"disambiguationData":[TD([[makeQuery(id+"F0.imprint","IMPRINT",EDGE,{"derivedFrom":sQuery(id+"F0.wireOp",EDGE,"E27.MirrorC")}),-1.0]])]});
            var Q21;
            Q21=makeQuery(id+"F0.imprint","IMPRINT",FACE,{"disambiguationData":[TD([[makeQuery(id+"F0.imprint","IMPRINT",EDGE,{"derivedFrom":sQuery(id+"F0.wireOp",EDGE,"E25.MirrorC")}),-1.0]])]});
            var Q22;
            Q22=makeQuery(id+"F0.imprint","IMPRINT",FACE,{"disambiguationData":[TD([[makeQuery(id+"F0.imprint","IMPRINT",EDGE,{"derivedFrom":sQuery(id+"F0.wireOp",EDGE,"E26.MirrorC")}),-1.0]])]});
            var Q23;
            Q23=makeQuery(id+"F0.imprint","IMPRINT",FACE,{"disambiguationData":[TD([[makeQuery(id+"F0.imprint","IMPRINT",EDGE,{"derivedFrom":sQuery(id+"F0.wireOp",EDGE,"E29.MirrorC")}),-1.0]])]});
            var Q24;
            {var subQ5=sQuery(id+"F0.wireOp",EDGE,"E7");Q24=makeQuery(id+"F0.imprint","IMPRINT",FACE,{"disambiguationData":[TD([[makeQuery(id+"F0.imprint","IMPRINT",EDGE,{"derivedFrom":subQ5}),-1.0]])]});}
            var Q25;
            {var subQ0=sQuery(id+"F0.wireOp",EDGE,"E37");var subQ1=sQuery(id+"F0.wireOp",EDGE,"E0.right");var subQ2=makeQuery(id+"F0.imprint","INTERSECT",VERTEX,{"derivedFrom":[subQ1,subQ0]});Q25=makeQuery(id+"F0.imprint","IMPRINT",FACE,{"disambiguationData":[TD([[makeQuery(id+"F0.imprint","IMPRINT",EDGE,{"disambiguationData":[TD([[subQ2,-1.0]])],"derivedFrom":subQ1}),-1.0]])]});}
            var Q26;
            {var subQ5=sQuery(id+"F0.wireOp",EDGE,"E6");Q26=makeQuery(id+"F0.imprint","IMPRINT",FACE,{"disambiguationData":[TD([[makeQuery(id+"F0.imprint","IMPRINT",EDGE,{"derivedFrom":subQ5}),1.0]])]});}
            var Q27;
            Q27=makeQuery(id+"F0.imprint","IMPRINT",FACE,{"disambiguationData":[TD([[makeQuery(id+"F0.imprint","IMPRINT",EDGE,{"derivedFrom":sQuery(id+"F0.wireOp",EDGE,"E46.MirrorC")}),-1.0]])]});
            var Q28;
            Q28=makeQuery(id+"F0.imprint","IMPRINT",FACE,{"disambiguationData":[TD([[makeQuery(id+"F0.imprint","IMPRINT",EDGE,{"derivedFrom":sQuery(id+"F0.wireOp",EDGE,"E45")}),1.0]])]});
            var Q29;
            {var subQ0=sQuery(id+"F0.wireOp",EDGE,"E47.MirrorC");var subQ1=sQuery(id+"F0.wireOp",EDGE,"E35.top");var subQ2=makeQuery(id+"F0.imprint","INTERSECT",VERTEX,{"disambiguationData":[OD(0.0)],"derivedFrom":[subQ1,subQ0]});Q29=makeQuery(id+"F0.imprint","IMPRINT",FACE,{"disambiguationData":[TD([[makeQuery(id+"F0.imprint","IMPRINT",EDGE,{"disambiguationData":[TD([[subQ2,-1.0]])],"derivedFrom":subQ1}),1.0]])]});}
            var Q30;
            {var subQ0=sQuery(id+"F0.wireOp",EDGE,"E48.MirrorC");var subQ1=sQuery(id+"F0.wireOp",EDGE,"E35.bottom");var subQ2=makeQuery(id+"F0.imprint","INTERSECT",VERTEX,{"disambiguationData":[OD(0.0)],"derivedFrom":[subQ1,subQ0]});Q30=makeQuery(id+"F0.imprint","IMPRINT",FACE,{"disambiguationData":[TD([[makeQuery(id+"F0.imprint","IMPRINT",EDGE,{"disambiguationData":[TD([[subQ2,-1.0]])],"derivedFrom":subQ1}),-1.0]])]});}
            var Q31;
            {var subQ0=sQuery(id+"F0.wireOp",EDGE,"E49.MirrorC");var subQ1=sQuery(id+"F0.wireOp",EDGE,"E35.top");var subQ2=makeQuery(id+"F0.imprint","INTERSECT",VERTEX,{"disambiguationData":[OD(0.0)],"derivedFrom":[subQ1,subQ0]});Q31=makeQuery(id+"F0.imprint","IMPRINT",FACE,{"disambiguationData":[TD([[makeQuery(id+"F0.imprint","IMPRINT",EDGE,{"disambiguationData":[TD([[subQ2,-1.0]])],"derivedFrom":subQ1}),1.0]])]});}
            var Q32;
            {var subQ0=sQuery(id+"F0.wireOp",EDGE,"E50.MirrorC");var subQ1=sQuery(id+"F0.wireOp",EDGE,"E35.top");var subQ2=makeQuery(id+"F0.imprint","INTERSECT",VERTEX,{"disambiguationData":[OD(0.0)],"derivedFrom":[subQ1,subQ0]});Q32=makeQuery(id+"F0.imprint","IMPRINT",FACE,{"disambiguationData":[TD([[makeQuery(id+"F0.imprint","IMPRINT",EDGE,{"disambiguationData":[TD([[subQ2,-1.0]])],"derivedFrom":subQ1}),1.0]])]});}
            var Q33;
            {var subQ0=sQuery(id+"F0.wireOp",EDGE,"E52.MirrorC");var subQ1=sQuery(id+"F0.wireOp",EDGE,"E35.bottom");var subQ2=makeQuery(id+"F0.imprint","INTERSECT",VERTEX,{"disambiguationData":[OD(0.0)],"derivedFrom":[subQ1,subQ0]});Q33=makeQuery(id+"F0.imprint","IMPRINT",FACE,{"disambiguationData":[TD([[makeQuery(id+"F0.imprint","IMPRINT",EDGE,{"disambiguationData":[TD([[subQ2,-1.0]])],"derivedFrom":subQ1}),-1.0]])]});}
            var Q34;
            {var subQ0=sQuery(id+"F0.wireOp",EDGE,"E51.MirrorC");var subQ1=sQuery(id+"F0.wireOp",EDGE,"E35.top");var subQ2=makeQuery(id+"F0.imprint","INTERSECT",VERTEX,{"disambiguationData":[OD(0.0)],"derivedFrom":[subQ1,subQ0]});Q34=makeQuery(id+"F0.imprint","IMPRINT",FACE,{"disambiguationData":[TD([[makeQuery(id+"F0.imprint","IMPRINT",EDGE,{"disambiguationData":[TD([[subQ2,-1.0]])],"derivedFrom":subQ1}),1.0]])]});}
            var Q35;
            {var subQ0=sQuery(id+"F0.wireOp",EDGE,"E35.left");var subQ1=sQuery(id+"F0.wireOp",EDGE,"E35.top");var subQ2=makeQuery(id+"F0.imprint","INTERSECT",VERTEX,{"derivedFrom":[subQ1,subQ0]});Q35=makeQuery(id+"F0.imprint","IMPRINT",FACE,{"disambiguationData":[TD([[makeQuery(id+"F0.imprint","IMPRINT",EDGE,{"disambiguationData":[TD([[subQ2,-1.0]])],"derivedFrom":subQ1}),1.0]])]});}
            var Q36;
            Q36=makeQuery(id+"F0.imprint","IMPRINT",FACE,{"disambiguationData":[TD([[makeQuery(id+"F0.imprint","IMPRINT",EDGE,{"derivedFrom":sQuery(id+"F0.wireOp",EDGE,"E54.MirrorC")}),-1.0]])]});
            var Q37;
            Q37=makeQuery(id+"F0.imprint","IMPRINT",FACE,{"disambiguationData":[TD([[makeQuery(id+"F0.imprint","IMPRINT",EDGE,{"derivedFrom":sQuery(id+"F0.wireOp",EDGE,"E55.MirrorC")}),1.0]])]});
            var Q38;
            Q38=makeQuery(id+"F0.imprint","IMPRINT",FACE,{"disambiguationData":[TD([[makeQuery(id+"F0.imprint","IMPRINT",EDGE,{"derivedFrom":sQuery(id+"F0.wireOp",EDGE,"E64.MirrorC")}),-1.0]])]});
            var Q39;
            Q39=makeQuery(id+"F0.imprint","IMPRINT",FACE,{"disambiguationData":[TD([[makeQuery(id+"F0.imprint","IMPRINT",EDGE,{"derivedFrom":sQuery(id+"F0.wireOp",EDGE,"E63.MirrorC")}),1.0]])]});
            var Q40;
            Q40=makeQuery(id+"F0.imprint","IMPRINT",FACE,{"disambiguationData":[TD([[makeQuery(id+"F0.imprint","IMPRINT",EDGE,{"derivedFrom":sQuery(id+"F0.wireOp",EDGE,"E62.MirrorC")}),1.0]])]});
            var Q41;
            Q41=makeQuery(id+"F0.imprint","IMPRINT",FACE,{"disambiguationData":[TD([[makeQuery(id+"F0.imprint","IMPRINT",EDGE,{"derivedFrom":sQuery(id+"F0.wireOp",EDGE,"E61.MirrorC")}),1.0]])]});
            var Q42;
            Q42=makeQuery(id+"F0.imprint","IMPRINT",FACE,{"disambiguationData":[TD([[makeQuery(id+"F0.imprint","IMPRINT",EDGE,{"derivedFrom":sQuery(id+"F0.wireOp",EDGE,"E60.MirrorC")}),1.0]])]});
            var Q43;
            Q43=makeQuery(id+"F0.imprint","IMPRINT",FACE,{"disambiguationData":[TD([[makeQuery(id+"F0.imprint","IMPRINT",EDGE,{"derivedFrom":sQuery(id+"F0.wireOp",EDGE,"E59.MirrorC")}),1.0]])]});
            var Q44;
            Q44=makeQuery(id+"F0.imprint","IMPRINT",FACE,{"disambiguationData":[TD([[makeQuery(id+"F0.imprint","IMPRINT",EDGE,{"derivedFrom":sQuery(id+"F0.wireOp",EDGE,"E57.MirrorC")}),1.0]])]});
            var Q45;
            Q45=makeQuery(id+"F0.imprint","IMPRINT",FACE,{"disambiguationData":[TD([[makeQuery(id+"F0.imprint","IMPRINT",EDGE,{"derivedFrom":sQuery(id+"F0.wireOp",EDGE,"E56.MirrorC")}),1.0]])]});
            var Q46;
            Q46=makeQuery(id+"F0.imprint","IMPRINT",FACE,{"disambiguationData":[TD([[makeQuery(id+"F0.imprint","IMPRINT",EDGE,{"derivedFrom":sQuery(id+"F0.wireOp",EDGE,"E58.MirrorC")}),1.0]])]});
            var Q47;
            Q47=makeQuery(id+"F0.imprint","IMPRINT",FACE,{"disambiguationData":[TD([[makeQuery(id+"F0.imprint","IMPRINT",EDGE,{"derivedFrom":sQuery(id+"F0.wireOp",EDGE,"E69.MirrorC")}),-1.0]])]});
            var Q48;
            Q48=makeQuery(id+"F0.imprint","IMPRINT",FACE,{"disambiguationData":[TD([[makeQuery(id+"F0.imprint","IMPRINT",EDGE,{"derivedFrom":sQuery(id+"F0.wireOp",EDGE,"E68.MirrorC")}),-1.0]])]});
            var Q49;
            Q49=makeQuery(id+"F0.imprint","IMPRINT",FACE,{"disambiguationData":[TD([[makeQuery(id+"F0.imprint","IMPRINT",EDGE,{"derivedFrom":sQuery(id+"F0.wireOp",EDGE,"E70.MirrorC")}),-1.0]])]});
            var Q50;
            Q50=makeQuery(id+"F0.imprint","IMPRINT",FACE,{"disambiguationData":[TD([[makeQuery(id+"F0.imprint","IMPRINT",EDGE,{"derivedFrom":sQuery(id+"F0.wireOp",EDGE,"E67.MirrorC")}),-1.0]])]});
            var Q51;
            Q51=makeQuery(id+"F0.imprint","IMPRINT",FACE,{"disambiguationData":[TD([[makeQuery(id+"F0.imprint","IMPRINT",EDGE,{"derivedFrom":sQuery(id+"F0.wireOp",EDGE,"E71.MirrorC")}),-1.0]])]});
            var Q52;
            Q52=makeQuery(id+"F0.imprint","IMPRINT",FACE,{"disambiguationData":[TD([[makeQuery(id+"F0.imprint","IMPRINT",EDGE,{"derivedFrom":sQuery(id+"F0.wireOp",EDGE,"E72.MirrorC")}),-1.0]])]});
            var Q53;
            Q53=makeQuery(id+"F0.imprint","IMPRINT",FACE,{"disambiguationData":[TD([[makeQuery(id+"F0.imprint","IMPRINT",EDGE,{"derivedFrom":sQuery(id+"F0.wireOp",EDGE,"E66.MirrorC")}),-1.0]])]});
            var Q54;
            Q54=makeQuery(id+"F0.imprint","IMPRINT",FACE,{"disambiguationData":[TD([[makeQuery(id+"F0.imprint","IMPRINT",EDGE,{"derivedFrom":sQuery(id+"F0.wireOp",EDGE,"E65.MirrorC")}),-1.0]])]});
            var Q55;
            Q55=makeQuery(id+"F0.imprint","IMPRINT",FACE,{"disambiguationData":[TD([[makeQuery(id+"F0.imprint","IMPRINT",EDGE,{"derivedFrom":sQuery(id+"F0.wireOp",EDGE,"E73.MirrorC")}),1.0]])]});
            extrude(context, id + "F24", {"entities" : qUnion([Q0, Q1, Q2, Q3, Q4, Q5, Q6, Q7, Q8, Q9, Q10, Q11, Q12, Q13, Q14, Q15, Q16, Q17, Q18, Q19, Q20, Q21, Q22, Q23, Q24, Q25, Q26, Q27, Q28, Q29, Q30, Q31, Q32, Q33, Q34, Q35, Q36, Q37, Q38, Q39, Q40, Q41, Q42, Q43, Q44, Q45, Q46, Q47, Q48, Q49, Q50, Q51, Q52, Q53, Q54, Q55]), "operationType" : NewBodyOperationType.REMOVE, "depth" : 25 * mm, "offsetDistance" : 25 * mm});
        }
        {
            var Q0;
            Q0=qCreatedBy(makeId("Top.planeOp"),FACE);
            var sketch = newSketch(context, id + "F25", { "sketchPlane" : qUnion([Q0])});
            skLineSegment(sketch, "E212.bottom", {"start": v(-365, -200) * mm, "end": v(365, -200) * mm});
            skLineSegment(sketch, "E212.top", {"start": v(-365, 200) * mm, "end": v(365, 200) * mm});
            skLineSegment(sketch, "E212.left", {"start": v(-365, -200) * mm, "end": v(-365, 200) * mm});
            skLineSegment(sketch, "E212.right", {"start": v(365, -200) * mm, "end": v(365, 200) * mm});
            skPoint(sketch, "E213", {"position": v(0, -200) * mm});
            skPoint(sketch, "E214", {"position": v(-182.5, -200) * mm});
            skPoint(sketch, "E215", {"position": v(182.5, -200) * mm});
            skPoint(sketch, "E216", {"position": v(-365, -50) * mm});
            skPoint(sketch, "E217", {"position": v(-365, 50) * mm});
            skPoint(sketch, "E218", {"position": v(-365, 0) * mm});
            skPoint(sketch, "E219", {"position": v(-365, -125) * mm});
            skPoint(sketch, "E220", {"position": v(-365, -162.5) * mm});
            skPoint(sketch, "E221", {"position": v(-365, -87.5) * mm});
            skLineSegment(sketch, "E222.bottom", {"start": v(-193, 0) * mm, "end": v(-172, 0) * mm});
            skLineSegment(sketch, "E222.right", {"start": v(0, 0) * mm, "end": v(0, -0.5) * mm});
            skLineSegment(sketch, "E223.right", {"start": v(0, -20) * mm, "end": v(0, -20.5) * mm});
            skLineSegment(sketch, "E224.right", {"start": v(0, -20) * mm, "end": v(0, -19.5) * mm});
            skPoint(sketch, "E225", {"position": v(-192.5, -200) * mm});
            skPoint(sketch, "E226", {"position": v(-172.5, -200) * mm});
            skPoint(sketch, "E227", {"position": v(-10, -200) * mm});
            skPoint(sketch, "E228", {"position": v(-365, -60) * mm});
            skPoint(sketch, "E229", {"position": v(-365, -40) * mm});
            skPoint(sketch, "E230", {"position": v(-365, 40) * mm});
            skPoint(sketch, "E231", {"position": v(-365, 60) * mm});
            skLineSegment(sketch, "E232.bottom", {"start": v(-365, -40) * mm, "end": v(-274.25, -40) * mm});
            skLineSegment(sketch, "E232.top", {"start": v(-365, -39.5) * mm, "end": v(-318.88, -39.5) * mm});
            skLineSegment(sketch, "E232.left", {"start": v(-365, -40) * mm, "end": v(-365, -39.5) * mm});
            skLineSegment(sketch, "E232.right", {"start": v(0, -40) * mm, "end": v(0, -39.5) * mm});
            skLineSegment(sketch, "E233.bottom", {"start": v(-193, 0) * mm, "end": v(0, 0) * mm});
            skLineSegment(sketch, "E233.right", {"start": v(0, 0) * mm, "end": v(0, 0.5) * mm});
            skLineSegment(sketch, "E234.bottom", {"start": v(-365, -40) * mm, "end": v(-318.88, -40) * mm});
            skLineSegment(sketch, "E234.top", {"start": v(-365, -40.5) * mm, "end": v(-318.88, -40.5) * mm});
            skLineSegment(sketch, "E234.left", {"start": v(-365, -40) * mm, "end": v(-365, -40.5) * mm});
            skLineSegment(sketch, "E234.right", {"start": v(0, -40) * mm, "end": v(0, -40.5) * mm});
            skLineSegment(sketch, "E235.bottom", {"start": v(-319.87, -60) * mm, "end": v(-273.25, -60) * mm});
            skLineSegment(sketch, "E235.top", {"start": v(-319.87, -59.5) * mm, "end": v(-228.62, -59.5) * mm});
            skLineSegment(sketch, "E235.left", {"start": v(-365, -60) * mm, "end": v(-365, -59.5) * mm});
            skLineSegment(sketch, "E235.right", {"start": v(0, -60) * mm, "end": v(0, -59.5) * mm});
            skLineSegment(sketch, "E236.bottom", {"start": v(-319.87, -60) * mm, "end": v(-228.62, -60) * mm});
            skLineSegment(sketch, "E236.top", {"start": v(-319.87, -60.5) * mm, "end": v(-228.62, -60.5) * mm});
            skLineSegment(sketch, "E236.left", {"start": v(-365, -60) * mm, "end": v(-365, -60.5) * mm});
            skLineSegment(sketch, "E236.right", {"start": v(0, -60) * mm, "end": v(0, -60.5) * mm});
            skLineSegment(sketch, "E237.left", {"start": v(-365, -87.5) * mm, "end": v(-365, -87) * mm});
            skLineSegment(sketch, "E237.right", {"start": v(0, -87.5) * mm, "end": v(0, -87) * mm});
            skLineSegment(sketch, "E238.left", {"start": v(-365, -87.5) * mm, "end": v(-365, -88) * mm});
            skLineSegment(sketch, "E238.right", {"start": v(0, -87.5) * mm, "end": v(0, -88) * mm});
            skLineSegment(sketch, "E239.left", {"start": v(-365, -125) * mm, "end": v(-365, -124.5) * mm});
            skLineSegment(sketch, "E239.right", {"start": v(0, -125) * mm, "end": v(0, -124.5) * mm});
            skLineSegment(sketch, "E240.left", {"start": v(-365, -125) * mm, "end": v(-365, -125.5) * mm});
            skLineSegment(sketch, "E240.right", {"start": v(0, -125) * mm, "end": v(0, -125.5) * mm});
            skLineSegment(sketch, "E241.left", {"start": v(-365, -162.5) * mm, "end": v(-365, -162) * mm});
            skLineSegment(sketch, "E241.right", {"start": v(0, -162.5) * mm, "end": v(0, -162) * mm});
            skLineSegment(sketch, "E242.left", {"start": v(-365, -162.5) * mm, "end": v(-365, -163) * mm});
            skLineSegment(sketch, "E242.right", {"start": v(0, -162.5) * mm, "end": v(0, -163) * mm});
            skLineSegment(sketch, "E243.bottom", {"start": v(-192.5, -200) * mm, "end": v(-193, -200) * mm});
            skLineSegment(sketch, "E243.top", {"start": v(-192.5, 0) * mm, "end": v(-193, 0) * mm});
            skLineSegment(sketch, "E243.left", {"start": v(-192.5, -200) * mm, "end": v(-192.5, -87) * mm});
            skLineSegment(sketch, "E243.right", {"start": v(-193, -200) * mm, "end": v(-193, -87) * mm});
            skLineSegment(sketch, "E244.bottom", {"start": v(-192.5, -200) * mm, "end": v(-192, -200) * mm});
            skLineSegment(sketch, "E244.top", {"start": v(-192.5, 0) * mm, "end": v(-192, 0) * mm});
            skLineSegment(sketch, "E244.right", {"start": v(-192, -200) * mm, "end": v(-192, -87) * mm});
            skLineSegment(sketch, "E245.bottom", {"start": v(-182.5, -200) * mm, "end": v(-183, -200) * mm});
            skLineSegment(sketch, "E245.top", {"start": v(-182.5, 0) * mm, "end": v(-183, 0) * mm});
            skLineSegment(sketch, "E245.left", {"start": v(-182.5, -200) * mm, "end": v(-182.5, -87) * mm});
            skLineSegment(sketch, "E245.right", {"start": v(-183, -200) * mm, "end": v(-183, -87.5) * mm});
            skLineSegment(sketch, "E246.bottom", {"start": v(-182.5, -200) * mm, "end": v(-182, -200) * mm});
            skLineSegment(sketch, "E246.top", {"start": v(-182.5, 0) * mm, "end": v(-182, 0) * mm});
            skLineSegment(sketch, "E246.right", {"start": v(-182, -200) * mm, "end": v(-182, -87) * mm});
            skLineSegment(sketch, "E247.bottom", {"start": v(-172.5, -200) * mm, "end": v(-173, -200) * mm});
            skLineSegment(sketch, "E247.top", {"start": v(-172.5, 0) * mm, "end": v(-173, 0) * mm});
            skLineSegment(sketch, "E247.left", {"start": v(-172.5, -200) * mm, "end": v(-172.5, -59.5) * mm});
            skLineSegment(sketch, "E248.bottom", {"start": v(-172.5, -200) * mm, "end": v(-172, -200) * mm});
            skLineSegment(sketch, "E248.top", {"start": v(-172.5, 0) * mm, "end": v(-172, 0) * mm});
            skLineSegment(sketch, "E248.left", {"start": v(-172.5, -163.05) * mm, "end": v(-172.5, -60) * mm});
            skLineSegment(sketch, "E248.right", {"start": v(-172, -200) * mm, "end": v(-172, -59.5) * mm});
            skLineSegment(sketch, "E249.bottom", {"start": v(0, -200) * mm, "end": v(-0.5, -200) * mm});
            skLineSegment(sketch, "E249.top", {"start": v(0, 0) * mm, "end": v(-0.5, 0) * mm});
            skLineSegment(sketch, "E249.left", {"start": v(0, -200) * mm, "end": v(0, 0) * mm});
            skLineSegment(sketch, "E249.right", {"start": v(-0.5, -200) * mm, "end": v(-0.5, 0) * mm});
            skLineSegment(sketch, "E250.bottom", {"start": v(-10, -200) * mm, "end": v(-9.5, -200) * mm});
            skLineSegment(sketch, "E250.top", {"start": v(-10, 0) * mm, "end": v(-9.5, 0) * mm});
            skLineSegment(sketch, "E250.left", {"start": v(-10, -200) * mm, "end": v(-10, 0) * mm});
            skLineSegment(sketch, "E250.right", {"start": v(-9.5, -200) * mm, "end": v(-9.5, 0) * mm});
            skLineSegment(sketch, "E251.bottom", {"start": v(-10, -200) * mm, "end": v(-10.5, -200) * mm});
            skLineSegment(sketch, "E251.top", {"start": v(-10, 0) * mm, "end": v(-10.5, 0) * mm});
            skLineSegment(sketch, "E251.right", {"start": v(-10.5, -200) * mm, "end": v(-10.5, 0) * mm});
            skLineSegment(sketch, "E252.top", {"start": v(-319.87, -50.5) * mm, "end": v(-318.87, -50.5) * mm});
            skLineSegment(sketch, "E252.left", {"start": v(-365, -50) * mm, "end": v(-365, -50.5) * mm});
            skLineSegment(sketch, "E252.right", {"start": v(0, -50) * mm, "end": v(0, -50.5) * mm});
            skLineSegment(sketch, "E253.bottom", {"start": v(-319.87, -50) * mm, "end": v(-318.87, -50) * mm});
            skLineSegment(sketch, "E253.top", {"start": v(-319.87, -49.5) * mm, "end": v(-318.87, -49.5) * mm});
            skLineSegment(sketch, "E253.left", {"start": v(-365, -50) * mm, "end": v(-365, -49.5) * mm});
            skLineSegment(sketch, "E253.right", {"start": v(0, -50) * mm, "end": v(0, -49.5) * mm});
            skLineSegment(sketch, "E254.trimOffspring", {"start": v(-318.87, -60.5) * mm, "end": v(-318.88, -39.5) * mm});
            skLineSegment(sketch, "E255.trimOffspring", {"start": v(-319.87, -60.5) * mm, "end": v(-319.88, -39.5) * mm});
            skLineSegment(sketch, "E256.trimOffspring", {"start": v(-319.37, -60.5) * mm, "end": v(-319.37, -39.5) * mm});
            skLineSegment(sketch, "E257.trimOffspring", {"start": v(-274.25, -60.5) * mm, "end": v(-274.25, -39.5) * mm});
            skLineSegment(sketch, "E258.trimOffspring", {"start": v(-273.25, -60.5) * mm, "end": v(-273.25, -39.5) * mm});
            skLineSegment(sketch, "E259.trimOffspring", {"start": v(-273.75, -60.5) * mm, "end": v(-273.75, -39.5) * mm});
            skLineSegment(sketch, "E260.trimOffspring", {"start": v(-227.62, -60.5) * mm, "end": v(-227.62, -39.5) * mm});
            skLineSegment(sketch, "E261.trimOffspring", {"start": v(-228.12, -60.5) * mm, "end": v(-228.12, -39.5) * mm});
            skLineSegment(sketch, "E262.trimOffspring", {"start": v(-228.62, -60.5) * mm, "end": v(-228.62, -39.5) * mm});
            skLineSegment(sketch, "E263.trimOffspring", {"start": v(-193, -20.5) * mm, "end": v(-172.5, -20.5) * mm});
            skLineSegment(sketch, "E264.trimOffspring", {"start": v(-193, -19.5) * mm, "end": v(-172, -19.5) * mm});
            skLineSegment(sketch, "E265.trimOffspring", {"start": v(-193, -0.5) * mm, "end": v(-172, -0.5) * mm});
            skLineSegment(sketch, "E266.trimOffspring", {"start": v(-193, -20) * mm, "end": v(-172, -20) * mm});
            skLineSegment(sketch, "E267.trimOffspring", {"start": v(-193, -163) * mm, "end": v(-172, -163) * mm});
            skLineSegment(sketch, "E268.trimOffspring", {"start": v(-193, -162.5) * mm, "end": v(-172, -162.5) * mm});
            skLineSegment(sketch, "E269.trimOffspring", {"start": v(-193, -162) * mm, "end": v(-172, -162) * mm});
            skLineSegment(sketch, "E270.trimOffspring", {"start": v(-193, -125) * mm, "end": v(-172, -125) * mm});
            skLineSegment(sketch, "E271.trimOffspring", {"start": v(-193, -124.5) * mm, "end": v(-172, -124.5) * mm});
            skLineSegment(sketch, "E272.trimOffspring", {"start": v(-193, -88) * mm, "end": v(-172, -88) * mm});
            skLineSegment(sketch, "E273.trimOffspring", {"start": v(-193, -87.5) * mm, "end": v(-172, -87.5) * mm});
            skLineSegment(sketch, "E274.trimOffspring", {"start": v(-193, -125.5) * mm, "end": v(-172, -125.5) * mm});
            skLineSegment(sketch, "E275.trimOffspring", {"start": v(-193, -87) * mm, "end": v(-172, -87) * mm});
            skLineSegment(sketch, "E276.trimOffspring", {"start": v(-137.37, -60.5) * mm, "end": v(-137.37, -39.5) * mm});
            skLineSegment(sketch, "E277.trimOffspring", {"start": v(-136.87, -60.5) * mm, "end": v(-136.87, -39.5) * mm});
            skLineSegment(sketch, "E278.trimOffspring", {"start": v(-91.25, -60.5) * mm, "end": v(-91.25, -40) * mm});
            skLineSegment(sketch, "E279.trimOffspring", {"start": v(-90.75, -60.5) * mm, "end": v(-90.75, -39.5) * mm});
            skLineSegment(sketch, "E280.trimOffspring", {"start": v(-91.75, -60.5) * mm, "end": v(-91.75, -39.5) * mm});
            skLineSegment(sketch, "E281.trimOffspring", {"start": v(-136.38, -60.5) * mm, "end": v(-136.38, -39.5) * mm});
            skLineSegment(sketch, "E282.trimOffspring", {"start": v(-91.25, -60.5) * mm, "end": v(-91.25, -39.5) * mm});
            skLineSegment(sketch, "E283.trimOffspring", {"start": v(-10.5, -19.5) * mm, "end": v(0, -19.5) * mm});
            skLineSegment(sketch, "E284.trimOffspring", {"start": v(-10.5, -0.5) * mm, "end": v(0, -0.5) * mm});
            skLineSegment(sketch, "E285.trimOffspring", {"start": v(-10.5, -20.5) * mm, "end": v(0, -20.5) * mm});
            skLineSegment(sketch, "E286.trimOffspring", {"start": v(-10.5, -20) * mm, "end": v(0, -20) * mm});
            skLineSegment(sketch, "E287.trimOffspring", {"start": v(-46.12, -60.5) * mm, "end": v(-46.12, -39.5) * mm});
            skLineSegment(sketch, "E288.trimOffspring", {"start": v(-10.5, -163) * mm, "end": v(0, -163) * mm});
            skLineSegment(sketch, "E289.trimOffspring", {"start": v(-10.5, -162) * mm, "end": v(0, -162) * mm});
            skLineSegment(sketch, "E290.trimOffspring", {"start": v(-45.62, -60.5) * mm, "end": v(-45.62, -39.5) * mm});
            skLineSegment(sketch, "E291.trimOffspring", {"start": v(-45.13, -60.5) * mm, "end": v(-45.13, -39.5) * mm});
            skLineSegment(sketch, "E292.trimOffspring", {"start": v(-10.5, -162.5) * mm, "end": v(0, -162.5) * mm});
            skLineSegment(sketch, "E293.trimOffspring", {"start": v(-10.5, -125.5) * mm, "end": v(0, -125.5) * mm});
            skLineSegment(sketch, "E294.trimOffspring", {"start": v(-10.5, -124.5) * mm, "end": v(0, -124.5) * mm});
            skLineSegment(sketch, "E295.trimOffspring", {"start": v(-10.5, -88) * mm, "end": v(0, -88) * mm});
            skLineSegment(sketch, "E296.trimOffspring", {"start": v(-10.5, -87.5) * mm, "end": v(0, -87.5) * mm});
            skLineSegment(sketch, "E297.trimOffspring", {"start": v(-10.5, -125) * mm, "end": v(0, -125) * mm});
            skLineSegment(sketch, "E298.trimOffspring", {"start": v(-10.5, -87) * mm, "end": v(0, -87) * mm});
            skLineSegment(sketch, "E299.MirrorCS", {"start": v(172.5, -200) * mm, "end": v(173, -200) * mm});
            skLineSegment(sketch, "E300.MirrorCS", {"start": v(182.5, -200) * mm, "end": v(183, -200) * mm});
            skLineSegment(sketch, "E301.MirrorCS", {"start": v(365, -40) * mm, "end": v(365, -39.5) * mm});
            skLineSegment(sketch, "E302.MirrorCS", {"start": v(182.5, -200) * mm, "end": v(182, -200) * mm});
            skLineSegment(sketch, "E303.MirrorCS", {"start": v(192.5, -200) * mm, "end": v(192, -200) * mm});
            skLineSegment(sketch, "E304.MirrorCS", {"start": v(172.5, -200) * mm, "end": v(172, -200) * mm});
            skLineSegment(sketch, "E305.MirrorCS", {"start": v(192.5, -200) * mm, "end": v(193, -200) * mm});
            skLineSegment(sketch, "E306.MirrorCS", {"start": v(365, -40) * mm, "end": v(365, -40.5) * mm});
            skLineSegment(sketch, "E307.MirrorCS", {"start": v(365, -50) * mm, "end": v(365, -49.5) * mm});
            skLineSegment(sketch, "E308.MirrorCS", {"start": v(365, -50) * mm, "end": v(365, -50.5) * mm});
            skLineSegment(sketch, "E309.MirrorCS", {"start": v(10, -200) * mm, "end": v(10.5, -200) * mm});
            skLineSegment(sketch, "E310.MirrorCS", {"start": v(365, -60) * mm, "end": v(365, -60.5) * mm});
            skLineSegment(sketch, "E311.MirrorCS", {"start": v(0, 0) * mm, "end": v(0.5, 0) * mm});
            skLineSegment(sketch, "E312.MirrorCS", {"start": v(10, -200) * mm, "end": v(9.5, -200) * mm});
            skLineSegment(sketch, "E313.MirrorCS", {"start": v(365, -60) * mm, "end": v(365, -59.5) * mm});
            skLineSegment(sketch, "E314.MirrorCS", {"start": v(10.5, -0.5) * mm, "end": v(0, -0.5) * mm});
            skLineSegment(sketch, "E315.MirrorCS", {"start": v(10, 0) * mm, "end": v(9.5, 0) * mm});
            skLineSegment(sketch, "E316.MirrorCS", {"start": v(10, 0) * mm, "end": v(10.5, 0) * mm});
            skLineSegment(sketch, "E317.MirrorCS", {"start": v(365, -125) * mm, "end": v(365, -125.5) * mm});
            skLineSegment(sketch, "E318.MirrorCS", {"start": v(0, -200) * mm, "end": v(0.5, -200) * mm});
            skLineSegment(sketch, "E319.MirrorCS", {"start": v(365, -87.5) * mm, "end": v(365, -87) * mm});
            skLineSegment(sketch, "E320.MirrorCS", {"start": v(365, -162.5) * mm, "end": v(365, -162) * mm});
            skLineSegment(sketch, "E321.MirrorCS", {"start": v(365, -87.5) * mm, "end": v(365, -88) * mm});
            skLineSegment(sketch, "E322.MirrorCS", {"start": v(365, -125) * mm, "end": v(365, -124.5) * mm});
            skLineSegment(sketch, "E323.MirrorCS", {"start": v(365, -162.5) * mm, "end": v(365, -163) * mm});
            skLineSegment(sketch, "E324.MirrorCS", {"start": v(10.5, -19.5) * mm, "end": v(0, -19.5) * mm});
            skLineSegment(sketch, "E325.MirrorCS", {"start": v(365, -40) * mm, "end": v(0, -40) * mm});
            skLineSegment(sketch, "E326.MirrorCS", {"start": v(318.87, -60.5) * mm, "end": v(318.87, -39.5) * mm});
            skLineSegment(sketch, "E327.MirrorCS", {"start": v(172, -200) * mm, "end": v(172, -39.5) * mm});
            skLineSegment(sketch, "E328.MirrorCS", {"start": v(192, -200) * mm, "end": v(192, -39.5) * mm});
            skLineSegment(sketch, "E329.MirrorCS", {"start": v(193, -88) * mm, "end": v(172, -88) * mm});
            skLineSegment(sketch, "E330.MirrorCS", {"start": v(45.62, -60.5) * mm, "end": v(45.62, -39.5) * mm});
            skLineSegment(sketch, "E331.MirrorCS", {"start": v(193, -125) * mm, "end": v(172, -125) * mm});
            skLineSegment(sketch, "E332.MirrorCS", {"start": v(193, -163) * mm, "end": v(172, -163) * mm});
            skLineSegment(sketch, "E333.MirrorCS", {"start": v(182.5, -200) * mm, "end": v(182.5, -40.5) * mm});
            skLineSegment(sketch, "E334.MirrorCS", {"start": v(10, -200) * mm, "end": v(10, 0) * mm});
            skLineSegment(sketch, "E335.MirrorCS", {"start": v(365, -40.5) * mm, "end": v(0, -40.5) * mm});
            skLineSegment(sketch, "E336.MirrorCS", {"start": v(273.25, -60.5) * mm, "end": v(273.25, -39.5) * mm});
            skLineSegment(sketch, "E337.MirrorCS", {"start": v(192.5, -200) * mm, "end": v(192.5, -40) * mm});
            skLineSegment(sketch, "E338.MirrorCS", {"start": v(172.5, -200) * mm, "end": v(172.5, -40.5) * mm});
            skLineSegment(sketch, "E339.MirrorCS", {"start": v(10.5, -125.5) * mm, "end": v(0, -125.5) * mm});
            skLineSegment(sketch, "E340.MirrorCS", {"start": v(193, -162.5) * mm, "end": v(172, -162.5) * mm});
            skLineSegment(sketch, "E341.MirrorCS", {"start": v(10.5, -163) * mm, "end": v(0, -163) * mm});
            skLineSegment(sketch, "E342.MirrorCS", {"start": v(183, -200) * mm, "end": v(183, -39.5) * mm});
            skLineSegment(sketch, "E343.MirrorCS", {"start": v(136.87, -60.5) * mm, "end": v(136.87, -39.5) * mm});
            skLineSegment(sketch, "E344.MirrorCS", {"start": v(365, -60) * mm, "end": v(0, -60) * mm});
            skLineSegment(sketch, "E345.MirrorCS", {"start": v(193, -87.5) * mm, "end": v(172, -87.5) * mm});
            skLineSegment(sketch, "E346.MirrorCS", {"start": v(45.12, -60.5) * mm, "end": v(45.12, -39.5) * mm});
            skLineSegment(sketch, "E347.MirrorCS", {"start": v(10.5, -88) * mm, "end": v(0, -88) * mm});
            skLineSegment(sketch, "E348.MirrorCS", {"start": v(365, -50) * mm, "end": v(0, -50) * mm});
            skLineSegment(sketch, "E349.MirrorCS", {"start": v(10.5, -20.5) * mm, "end": v(0, -20.5) * mm});
            skLineSegment(sketch, "E350.MirrorCS", {"start": v(228.12, -60.5) * mm, "end": v(228.12, -39.5) * mm});
            skLineSegment(sketch, "E351.MirrorCS", {"start": v(319.87, -60.5) * mm, "end": v(319.87, -39.5) * mm});
            skLineSegment(sketch, "E352.MirrorCS", {"start": v(91.25, -60.5) * mm, "end": v(91.25, -40) * mm});
            skLineSegment(sketch, "E353.MirrorCS", {"start": v(91.75, -60.5) * mm, "end": v(91.75, -39.5) * mm});
            skLineSegment(sketch, "E354.MirrorCS", {"start": v(193, -87) * mm, "end": v(172, -87) * mm});
            skLineSegment(sketch, "E355.MirrorCS", {"start": v(193, -124.5) * mm, "end": v(172, -124.5) * mm});
            skLineSegment(sketch, "E356.MirrorCS", {"start": v(10.5, -162.5) * mm, "end": v(0, -162.5) * mm});
            skLineSegment(sketch, "E357.MirrorCS", {"start": v(319.37, -60.5) * mm, "end": v(319.37, -39.5) * mm});
            skLineSegment(sketch, "E358.MirrorCS", {"start": v(193, -200) * mm, "end": v(193, -39.5) * mm});
            skLineSegment(sketch, "E359.MirrorCS", {"start": v(182.5, -200) * mm, "end": v(182.5, -39.5) * mm});
            skLineSegment(sketch, "E360.MirrorCS", {"start": v(273.75, -60.5) * mm, "end": v(273.75, -39.5) * mm});
            skLineSegment(sketch, "E361.MirrorCS", {"start": v(10.5, -125) * mm, "end": v(0, -125) * mm});
            skLineSegment(sketch, "E362.MirrorCS", {"start": v(10.5, -20) * mm, "end": v(0, -20) * mm});
            skLineSegment(sketch, "E363.MirrorCS", {"start": v(193, -125.5) * mm, "end": v(172, -125.5) * mm});
            skLineSegment(sketch, "E364.MirrorCS", {"start": v(173, -200) * mm, "end": v(173, -39.5) * mm});
            skLineSegment(sketch, "E365.MirrorCS", {"start": v(9.5, -200) * mm, "end": v(9.5, 0) * mm});
            skLineSegment(sketch, "E366.MirrorCS", {"start": v(10.5, -87.5) * mm, "end": v(0, -87.5) * mm});
            skLineSegment(sketch, "E367.MirrorCS", {"start": v(193, -162) * mm, "end": v(172, -162) * mm});
            skLineSegment(sketch, "E368.MirrorCS", {"start": v(365, -39.5) * mm, "end": v(0, -39.5) * mm});
            skLineSegment(sketch, "E369.MirrorCS", {"start": v(365, -49.5) * mm, "end": v(0, -49.5) * mm});
            skLineSegment(sketch, "E370.MirrorCS", {"start": v(90.75, -60.5) * mm, "end": v(90.75, -39.5) * mm});
            skPoint(sketch, "E371.MirrorP", {"position": v(365, 0) * mm});
            skLineSegment(sketch, "E372.MirrorCS", {"start": v(10.5, -124.5) * mm, "end": v(0, -124.5) * mm});
            skLineSegment(sketch, "E373.MirrorCS", {"start": v(365, -59.5) * mm, "end": v(0, -59.5) * mm});
            skLineSegment(sketch, "E374.MirrorCS", {"start": v(10.5, -162) * mm, "end": v(0, -162) * mm});
            skPoint(sketch, "E375.MirrorP", {"position": v(365, -60) * mm});
            skPoint(sketch, "E376.MirrorP", {"position": v(172.5, -200) * mm});
            skPoint(sketch, "E377.MirrorP", {"position": v(365, -50) * mm});
            skLineSegment(sketch, "E378.MirrorCS", {"start": v(365, -50.5) * mm, "end": v(0, -50.5) * mm});
            skPoint(sketch, "E379.MirrorP", {"position": v(365, -40) * mm});
            skLineSegment(sketch, "E380.MirrorCS", {"start": v(137.37, -60.5) * mm, "end": v(137.37, -39.5) * mm});
            skPoint(sketch, "E381.MirrorP", {"position": v(192.5, -200) * mm});
            skPoint(sketch, "E382.MirrorP", {"position": v(365, -87.5) * mm});
            skLineSegment(sketch, "E383.MirrorCS", {"start": v(228.62, -60.5) * mm, "end": v(228.62, -39.5) * mm});
            skLineSegment(sketch, "E384.MirrorCS", {"start": v(365, -60.5) * mm, "end": v(0, -60.5) * mm});
            skLineSegment(sketch, "E385.MirrorCS", {"start": v(46.12, -60.5) * mm, "end": v(46.12, -39.5) * mm});
            skLineSegment(sketch, "E386.MirrorCS", {"start": v(10.5, -200) * mm, "end": v(10.5, 0) * mm});
            skLineSegment(sketch, "E387.MirrorCS", {"start": v(0.5, -200) * mm, "end": v(0.5, 0) * mm});
            skLineSegment(sketch, "E388.MirrorCS", {"start": v(182, -200) * mm, "end": v(182, -39.5) * mm});
            skLineSegment(sketch, "E389.MirrorCS", {"start": v(91.25, -60.5) * mm, "end": v(91.25, -39.5) * mm});
            skLineSegment(sketch, "E390.MirrorCS", {"start": v(136.38, -60.5) * mm, "end": v(136.38, -39.5) * mm});
            skLineSegment(sketch, "E391.MirrorCS", {"start": v(192.5, -200) * mm, "end": v(192.5, -39.5) * mm});
            skLineSegment(sketch, "E392.MirrorCS", {"start": v(172.5, -200) * mm, "end": v(172.5, -39.5) * mm});
            skLineSegment(sketch, "E393.MirrorCS", {"start": v(227.62, -60.5) * mm, "end": v(227.62, -39.5) * mm});
            skLineSegment(sketch, "E394.MirrorCS", {"start": v(274.25, -60.5) * mm, "end": v(274.25, -39.5) * mm});
            skPoint(sketch, "E395.MirrorP", {"position": v(365, -162.5) * mm});
            skPoint(sketch, "E396.MirrorP", {"position": v(365, -125) * mm});
            skPoint(sketch, "E397.MirrorP", {"position": v(10, -200) * mm});
            skLineSegment(sketch, "E398.MirrorCS", {"start": v(10.5, -87) * mm, "end": v(0, -87) * mm});
            skLineSegment(sketch, "E399.MirrorCS", {"start": v(0, 50) * mm, "end": v(0, 50.5) * mm});
            skLineSegment(sketch, "E400.MirrorCS", {"start": v(0, 50) * mm, "end": v(0, 49.5) * mm});
            skLineSegment(sketch, "E401.MirrorCS", {"start": v(0, 40) * mm, "end": v(0, 40.5) * mm});
            skLineSegment(sketch, "E402.MirrorCS", {"start": v(0, 60) * mm, "end": v(0, 59.5) * mm});
            skLineSegment(sketch, "E403.MirrorCS", {"start": v(0, 20) * mm, "end": v(0, 20.5) * mm});
            skLineSegment(sketch, "E404.MirrorCS", {"start": v(0, 20) * mm, "end": v(0, 19.5) * mm});
            skLineSegment(sketch, "E405.MirrorCS", {"start": v(0, 40) * mm, "end": v(0, 39.5) * mm});
            skLineSegment(sketch, "E406.MirrorCS", {"start": v(0, 60) * mm, "end": v(0, 60.5) * mm});
            skLineSegment(sketch, "E407.MirrorCS", {"start": v(-365, 40) * mm, "end": v(-365, 40.5) * mm});
            skLineSegment(sketch, "E408.MirrorCS", {"start": v(-365, 50) * mm, "end": v(-365, 49.5) * mm});
            skLineSegment(sketch, "E409.MirrorCS", {"start": v(10.5, 0.5) * mm, "end": v(0, 0.5) * mm});
            skLineSegment(sketch, "E410.MirrorCS", {"start": v(-365, 60) * mm, "end": v(-365, 59.5) * mm});
            skLineSegment(sketch, "E411.MirrorCS", {"start": v(-365, 50) * mm, "end": v(-365, 50.5) * mm});
            skLineSegment(sketch, "E412.MirrorCS", {"start": v(-365, 60) * mm, "end": v(-365, 60.5) * mm});
            skLineSegment(sketch, "E413.MirrorCS", {"start": v(-365, 40) * mm, "end": v(-365, 39.5) * mm});
            skLineSegment(sketch, "E414.MirrorCS", {"start": v(-193, 0.5) * mm, "end": v(-172, 0.5) * mm});
            skLineSegment(sketch, "E415.MirrorCS", {"start": v(-10.5, 0.5) * mm, "end": v(0, 0.5) * mm});
            skLineSegment(sketch, "E416.MirrorCS", {"start": v(-10.5, 20.5) * mm, "end": v(0, 20.5) * mm});
            skLineSegment(sketch, "E417.MirrorCS", {"start": v(10.5, 20) * mm, "end": v(0, 20) * mm});
            skLineSegment(sketch, "E418.MirrorCS", {"start": v(-10.5, 20) * mm, "end": v(0, 20) * mm});
            skLineSegment(sketch, "E419.MirrorCS", {"start": v(10.5, 20.5) * mm, "end": v(0, 20.5) * mm});
            skLineSegment(sketch, "E420.MirrorCS", {"start": v(10.5, 19.5) * mm, "end": v(0, 19.5) * mm});
            skLineSegment(sketch, "E421.MirrorCS", {"start": v(-10.5, 19.5) * mm, "end": v(0, 19.5) * mm});
            skLineSegment(sketch, "E422.MirrorCS", {"start": v(-91.25, 60.5) * mm, "end": v(-91.25, 40) * mm});
            skLineSegment(sketch, "E423.MirrorCS", {"start": v(-137.37, 60.5) * mm, "end": v(-137.37, 39.5) * mm});
            skLineSegment(sketch, "E424.MirrorCS", {"start": v(-274.25, 60.5) * mm, "end": v(-274.25, 39.5) * mm});
            skLineSegment(sketch, "E425.MirrorCS", {"start": v(-318.87, 60.5) * mm, "end": v(-318.88, 39.5) * mm});
            skLineSegment(sketch, "E426.MirrorCS", {"start": v(-319.88, 40) * mm, "end": v(-228.62, 40) * mm});
            skLineSegment(sketch, "E427.MirrorCS", {"start": v(-136.87, 60.5) * mm, "end": v(-136.87, 39.5) * mm});
            skLineSegment(sketch, "E428.MirrorCS", {"start": v(-319.87, 60.5) * mm, "end": v(-319.88, 39.5) * mm});
            skLineSegment(sketch, "E429.MirrorCS", {"start": v(-273.25, 60.5) * mm, "end": v(-273.25, 39.5) * mm});
            skLineSegment(sketch, "E430.MirrorCS", {"start": v(-319.87, 50) * mm, "end": v(-318.87, 50) * mm});
            skLineSegment(sketch, "E431.MirrorCS", {"start": v(-90.75, 60.5) * mm, "end": v(-90.75, 39.5) * mm});
            skLineSegment(sketch, "E432.MirrorCS", {"start": v(-365, 60) * mm, "end": v(-318.87, 60) * mm});
            skLineSegment(sketch, "E433.MirrorCS", {"start": v(-193, 20.5) * mm, "end": v(-172, 20.5) * mm});
            skLineSegment(sketch, "E434.MirrorCS", {"start": v(-228.12, 60.5) * mm, "end": v(-228.12, 39.5) * mm});
            skLineSegment(sketch, "E435.MirrorCS", {"start": v(-45.62, 60.5) * mm, "end": v(-45.62, 39.5) * mm});
            skLineSegment(sketch, "E436.MirrorCS", {"start": v(-319.37, 40.5) * mm, "end": v(-228.62, 40.5) * mm});
            skLineSegment(sketch, "E437.MirrorCS", {"start": v(-319.37, 60.5) * mm, "end": v(-319.37, 39.5) * mm});
            skLineSegment(sketch, "E438.MirrorCS", {"start": v(-365, 59.5) * mm, "end": v(-318.87, 59.5) * mm});
            skLineSegment(sketch, "E439.MirrorCS", {"start": v(-273.75, 60.5) * mm, "end": v(-273.75, 39.5) * mm});
            skLineSegment(sketch, "E440.MirrorCS", {"start": v(-91.75, 60.5) * mm, "end": v(-91.75, 39.5) * mm});
            skLineSegment(sketch, "E441.MirrorCS", {"start": v(-193, 20) * mm, "end": v(-172, 20) * mm});
            skLineSegment(sketch, "E442.MirrorCS", {"start": v(-319.87, 49.5) * mm, "end": v(-318.87, 49.5) * mm});
            skLineSegment(sketch, "E443.MirrorCS", {"start": v(-227.62, 60.5) * mm, "end": v(-227.62, 39.5) * mm});
            skLineSegment(sketch, "E444.MirrorCS", {"start": v(-45.13, 60.5) * mm, "end": v(-45.13, 39.5) * mm});
            skLineSegment(sketch, "E445.MirrorCS", {"start": v(-228.62, 60.5) * mm, "end": v(-228.62, 39.5) * mm});
            skLineSegment(sketch, "E446.MirrorCS", {"start": v(-46.12, 60.5) * mm, "end": v(-46.12, 39.5) * mm});
            skLineSegment(sketch, "E447.MirrorCS", {"start": v(-365, 60.5) * mm, "end": v(-318.87, 60.5) * mm});
            skLineSegment(sketch, "E448.MirrorCS", {"start": v(-91.25, 60.5) * mm, "end": v(-91.25, 39.5) * mm});
            skLineSegment(sketch, "E449.MirrorCS", {"start": v(-319.88, 39.5) * mm, "end": v(-273.25, 39.5) * mm});
            skLineSegment(sketch, "E450.MirrorCS", {"start": v(-319.37, 40) * mm, "end": v(-273.25, 40) * mm});
            skLineSegment(sketch, "E451.MirrorCS", {"start": v(-136.38, 60.5) * mm, "end": v(-136.38, 39.5) * mm});
            skLineSegment(sketch, "E452.MirrorCS", {"start": v(-319.87, 50.5) * mm, "end": v(-318.87, 50.5) * mm});
            skLineSegment(sketch, "E453.MirrorCS", {"start": v(-365, 60) * mm, "end": v(-274.25, 60) * mm});
            skLineSegment(sketch, "E454.MirrorCS", {"start": v(-193, 19.5) * mm, "end": v(-172, 19.5) * mm});
            skLineSegment(sketch, "E455.MirrorCS", {"start": v(0, 60.5) * mm, "end": v(0, 0) * mm});
            skLineSegment(sketch, "E456.MirrorCS", {"start": v(-193, 20.5) * mm, "end": v(-172.5, 20.5) * mm});
            skLineSegment(sketch, "E457.MirrorCS", {"start": v(-319.88, 40) * mm, "end": v(-273.25, 40) * mm});
            skLineSegment(sketch, "E458.MirrorCS", {"start": v(10.5, 40) * mm, "end": v(0, 40) * mm});
            skLineSegment(sketch, "E459.MirrorCS", {"start": v(10.5, 60) * mm, "end": v(0, 60) * mm});
            skLineSegment(sketch, "E460.MirrorCS", {"start": v(-319.88, 40.5) * mm, "end": v(-273.25, 40.5) * mm});
            skLineSegment(sketch, "E461.MirrorCS", {"start": v(10.5, 50) * mm, "end": v(0, 50) * mm});
            skLineSegment(sketch, "E462.MirrorCS", {"start": v(-365, 59.5) * mm, "end": v(-274.25, 59.5) * mm});
            skLineSegment(sketch, "E463.MirrorCS", {"start": v(-365, 60.5) * mm, "end": v(-274.25, 60.5) * mm});
            skLineSegment(sketch, "E464.MirrorCS", {"start": v(-319.88, 39.5) * mm, "end": v(-228.62, 39.5) * mm});
            skLineSegment(sketch, "E465.MirrorCS", {"start": v(10.5, 49.5) * mm, "end": v(0, 49.5) * mm});
            skLineSegment(sketch, "E466.MirrorCS", {"start": v(10.5, 50.5) * mm, "end": v(0, 50.5) * mm});
            skLineSegment(sketch, "E467.MirrorCS", {"start": v(10.5, 59.5) * mm, "end": v(0, 59.5) * mm});
            skLineSegment(sketch, "E468.MirrorCS", {"start": v(10.5, 39.5) * mm, "end": v(0, 39.5) * mm});
            skLineSegment(sketch, "E469.MirrorCS", {"start": v(10.5, 60.5) * mm, "end": v(0, 60.5) * mm});
            skLineSegment(sketch, "E470.MirrorCS", {"start": v(-365, 60) * mm, "end": v(-319.37, 60) * mm});
            skLineSegment(sketch, "E471.MirrorCS", {"start": v(-319.87, 50) * mm, "end": v(-319.37, 50) * mm});
            skLineSegment(sketch, "E472.MirrorCS", {"start": v(10.5, 40.5) * mm, "end": v(0, 40.5) * mm});
            skLineSegment(sketch, "E473.trimOffspring", {"start": v(-10.5, 60.5) * mm, "end": v(-10.5, 0) * mm});
            skLineSegment(sketch, "E474.trimOffspring", {"start": v(-10, 60.5) * mm, "end": v(-10, 0) * mm});
            skLineSegment(sketch, "E475.trimOffspring", {"start": v(-0.5, 60.5) * mm, "end": v(-0.5, 0) * mm});
            skLineSegment(sketch, "E476.trimOffspring", {"start": v(-9.5, 60.5) * mm, "end": v(-9.5, 0) * mm});
            skLineSegment(sketch, "E477.trimOffspring", {"start": v(0.5, 60.5) * mm, "end": v(0.5, 0) * mm});
            skLineSegment(sketch, "E478.trimOffspring", {"start": v(10.5, 60.5) * mm, "end": v(10.5, 49.5) * mm});
            skLineSegment(sketch, "E479.trimOffspring", {"start": v(10, 60.5) * mm, "end": v(10, 49.5) * mm});
            skLineSegment(sketch, "E480.trimOffspring", {"start": v(9.5, 60.5) * mm, "end": v(9.5, 49.5) * mm});
            skLineSegment(sketch, "E481.trimOffspring", {"start": v(-173, 60.5) * mm, "end": v(-173, 49.5) * mm});
            skLineSegment(sketch, "E482.trimOffspring", {"start": v(-172.5, 60.5) * mm, "end": v(-172.5, 50) * mm});
            skLineSegment(sketch, "E483.trimOffspring", {"start": v(-172, 60.5) * mm, "end": v(-172, 49.5) * mm});
            skLineSegment(sketch, "E484.trimOffspring", {"start": v(-172.5, 60.5) * mm, "end": v(-172.5, 49.5) * mm});
            skPoint(sketch, "E485.orphan", {"position": v(365, 60.5) * mm});
            skPoint(sketch, "E486.orphan", {"position": v(365, 59.5) * mm});
            skPoint(sketch, "E487.orphan", {"position": v(365, 60) * mm});
            skPoint(sketch, "E488.orphan", {"position": v(365, 40) * mm});
            skPoint(sketch, "E489.orphan", {"position": v(365, 39.5) * mm});
            skPoint(sketch, "E490.orphan", {"position": v(365, 49.5) * mm});
            skPoint(sketch, "E491.orphan", {"position": v(365, 50) * mm});
            skPoint(sketch, "E492.orphan", {"position": v(365, 50.5) * mm});
            skPoint(sketch, "E493.orphan", {"position": v(365, 40.5) * mm});
            skPoint(sketch, "E494.orphan", {"position": v(0, 200) * mm});
            skLineSegment(sketch, "E495.trimOffspring", {"start": v(-10.5, 0) * mm, "end": v(0, 0) * mm});
            skLineSegment(sketch, "E496.trimOffspring", {"start": v(-318.88, -39.5) * mm, "end": v(-227.62, -39.5) * mm});
            skLineSegment(sketch, "E497.trimOffspring", {"start": v(-318.88, -40.5) * mm, "end": v(-227.62, -40.5) * mm});
            skLineSegment(sketch, "E498.trimOffspring", {"start": v(-274.25, -40) * mm, "end": v(-227.62, -40) * mm});
            skLineSegment(sketch, "E499.trimOffspring", {"start": v(-274.25, -49.5) * mm, "end": v(-273.25, -49.5) * mm});
            skLineSegment(sketch, "E500.trimOffspring", {"start": v(-274.25, -50) * mm, "end": v(-273.25, -50) * mm});
            skLineSegment(sketch, "E501.trimOffspring", {"start": v(-228.62, -60.5) * mm, "end": v(-192, -60.5) * mm});
            skLineSegment(sketch, "E502.trimOffspring", {"start": v(-228.62, -60) * mm, "end": v(-192, -60) * mm});
            skLineSegment(sketch, "E503.trimOffspring", {"start": v(-228.62, -59.5) * mm, "end": v(-192, -59.5) * mm});
            skLineSegment(sketch, "E504.trimOffspring", {"start": v(-228.62, -60) * mm, "end": v(-192.5, -60) * mm});
            skLineSegment(sketch, "E505.trimOffspring", {"start": v(-228.62, -50.5) * mm, "end": v(-227.62, -50.5) * mm});
            skLineSegment(sketch, "E506.trimOffspring", {"start": v(-228.62, -50) * mm, "end": v(-227.62, -50) * mm});
            skLineSegment(sketch, "E507.trimOffspring", {"start": v(-193, -50.5) * mm, "end": v(0, -50.5) * mm});
            skLineSegment(sketch, "E508.trimOffspring", {"start": v(-193, -39.5) * mm, "end": v(-182, -39.5) * mm});
            skLineSegment(sketch, "E509.trimOffspring", {"start": v(-193, -40) * mm, "end": v(-182, -40) * mm});
            skLineSegment(sketch, "E510.trimOffspring", {"start": v(-193, -49.5) * mm, "end": v(0, -49.5) * mm});
            skLineSegment(sketch, "E511.trimOffspring", {"start": v(-228.62, -49.5) * mm, "end": v(-227.62, -49.5) * mm});
            skLineSegment(sketch, "E512.trimOffspring", {"start": v(-193, -50) * mm, "end": v(0, -50) * mm});
            skLineSegment(sketch, "E513.trimOffspring", {"start": v(-193, -40.5) * mm, "end": v(-182, -40.5) * mm});
            skLineSegment(sketch, "E514.trimOffspring", {"start": v(-193, -40.5) * mm, "end": v(-193, 0) * mm});
            skLineSegment(sketch, "E515.trimOffspring", {"start": v(-192.5, -40.5) * mm, "end": v(-192.5, 0) * mm});
            skLineSegment(sketch, "E516.trimOffspring", {"start": v(-192, -40.5) * mm, "end": v(-192, 0) * mm});
            skLineSegment(sketch, "E517.trimOffspring", {"start": v(-183, -60.5) * mm, "end": v(0, -60.5) * mm});
            skLineSegment(sketch, "E518.trimOffspring", {"start": v(-183, -59.5) * mm, "end": v(0, -59.5) * mm});
            skLineSegment(sketch, "E519.trimOffspring", {"start": v(-183, -60) * mm, "end": v(0, -60) * mm});
            skLineSegment(sketch, "E520.trimOffspring", {"start": v(-172.5, -50.5) * mm, "end": v(-172.5, -39.5) * mm});
            skLineSegment(sketch, "E521.trimOffspring", {"start": v(-172.5, -40) * mm, "end": v(0, -40) * mm});
            skLineSegment(sketch, "E522.trimOffspring", {"start": v(-173, -40.5) * mm, "end": v(0, -40.5) * mm});
            skLineSegment(sketch, "E523.trimOffspring", {"start": v(-172, -50.5) * mm, "end": v(-172, -39.5) * mm});
            skLineSegment(sketch, "E524.trimOffspring", {"start": v(-173, -40) * mm, "end": v(0, -40) * mm});
            skLineSegment(sketch, "E525.trimOffspring", {"start": v(-172.5, -39.5) * mm, "end": v(0, -39.5) * mm});
            skLineSegment(sketch, "E526.trimOffspring", {"start": v(-192.5, -60.5) * mm, "end": v(-192.5, -50) * mm});
            skLineSegment(sketch, "E527.trimOffspring", {"start": v(-182.5, -60.5) * mm, "end": v(-182.5, 0) * mm});
            skLineSegment(sketch, "E528.trimOffspring", {"start": v(-172.5, -20.5) * mm, "end": v(-172.5, 0) * mm});
            skLineSegment(sketch, "E529.trimOffspring", {"start": v(-193, -60.5) * mm, "end": v(-193, -49.5) * mm});
            skLineSegment(sketch, "E530.trimOffspring", {"start": v(-192.5, -60.5) * mm, "end": v(-192.5, -49.5) * mm});
            skLineSegment(sketch, "E531.trimOffspring", {"start": v(-192, -60.5) * mm, "end": v(-192, -49.5) * mm});
            skLineSegment(sketch, "E532.trimOffspring", {"start": v(-183, -60.5) * mm, "end": v(-183, 0) * mm});
            skLineSegment(sketch, "E533.trimOffspring", {"start": v(-182, -60.5) * mm, "end": v(-182, 0) * mm});
            skLineSegment(sketch, "E534.MirrorCS", {"start": v(-173, -200) * mm, "end": v(-173, -59.5) * mm});
            skLineSegment(sketch, "E535.trimOffspring", {"start": v(-173, -50.5) * mm, "end": v(-173, -39.5) * mm});
            skLineSegment(sketch, "E536.trimOffspring", {"start": v(-172, -20) * mm, "end": v(-172, 0) * mm});
            skLineSegment(sketch, "E537.MirrorCS", {"start": v(-172, -39.5) * mm, "end": v(-173, -39.5) * mm});
            skLineSegment(sketch, "E538.trimOffspring", {"start": v(-173, -20.5) * mm, "end": v(-173, 0) * mm});
            skLineSegment(sketch, "E539.MirrorCS", {"start": v(-172, -40.5) * mm, "end": v(-172, -39.5) * mm});
            skLineSegment(sketch, "E540.MirrorCS", {"start": v(-172, -20.5) * mm, "end": v(-192.5, -20.5) * mm});
            skLineSegment(sketch, "E541.trimOffspring", {"start": v(-182, -39.5) * mm, "end": v(-183, -39.5) * mm});
            skLineSegment(sketch, "E542.trimOffspring", {"start": v(-172, -20.5) * mm, "end": v(-172, 0) * mm});
            skPoint(sketch, "E543.orphan", {"position": v(-365, 39.5) * mm});
            skLineSegment(sketch, "E544.trimOffspring", {"start": v(-274.25, 60) * mm, "end": v(-228.12, 60) * mm});
            skLineSegment(sketch, "E545.trimOffspring", {"start": v(-274.25, 50) * mm, "end": v(-273.25, 50) * mm});
            skPoint(sketch, "E546.orphan", {"position": v(-365, 40.5) * mm});
            skLineSegment(sketch, "E547.trimOffspring", {"start": v(-228.62, 50) * mm, "end": v(-227.62, 50) * mm});
            skLineSegment(sketch, "E548.trimOffspring", {"start": v(-228.62, 40) * mm, "end": v(-193, 40) * mm});
            skLineSegment(sketch, "E549.trimOffspring", {"start": v(-228.62, 50) * mm, "end": v(-228.12, 50) * mm});
            skPoint(sketch, "E550.orphan", {"position": v(-365, 49.5) * mm});
            skPoint(sketch, "E551.orphan", {"position": v(-365, 50.5) * mm});
            skLineSegment(sketch, "E552.trimOffspring", {"start": v(-274.25, 59.5) * mm, "end": v(-227.62, 59.5) * mm});
            skLineSegment(sketch, "E553.trimOffspring", {"start": v(-274.25, 49.5) * mm, "end": v(-273.25, 49.5) * mm});
            skLineSegment(sketch, "E554.trimOffspring", {"start": v(-274.25, 50.5) * mm, "end": v(-273.25, 50.5) * mm});
            skLineSegment(sketch, "E555.trimOffspring", {"start": v(-274.25, 60) * mm, "end": v(-227.62, 60) * mm});
            skLineSegment(sketch, "E556.trimOffspring", {"start": v(-274.25, 60.5) * mm, "end": v(-228.12, 60.5) * mm});
            skLineSegment(sketch, "E557.trimOffspring", {"start": v(-228.62, 49.5) * mm, "end": v(-227.62, 49.5) * mm});
            skLineSegment(sketch, "E558.trimOffspring", {"start": v(-228.62, 40) * mm, "end": v(-192, 40) * mm});
            skLineSegment(sketch, "E559.trimOffspring", {"start": v(-228.62, 39.5) * mm, "end": v(-192, 39.5) * mm});
            skLineSegment(sketch, "E560.trimOffspring", {"start": v(-228.62, 40.5) * mm, "end": v(-192, 40.5) * mm});
            skLineSegment(sketch, "E561.trimOffspring", {"start": v(-228.62, 50.5) * mm, "end": v(-228.12, 50.5) * mm});
            skLineSegment(sketch, "E562.trimOffspring", {"start": v(-274.25, 60.5) * mm, "end": v(-227.62, 60.5) * mm});
            skLineSegment(sketch, "E563.trimOffspring", {"start": v(-228.62, 49.5) * mm, "end": v(-228.12, 49.5) * mm});
            skLineSegment(sketch, "E564.trimOffspring", {"start": v(-228.62, 50.5) * mm, "end": v(-227.62, 50.5) * mm});
            skLineSegment(sketch, "E565.trimOffspring", {"start": v(-193, 49.5) * mm, "end": v(0, 49.5) * mm});
            skLineSegment(sketch, "E566.trimOffspring", {"start": v(-193, 50.5) * mm, "end": v(0, 50.5) * mm});
            skLineSegment(sketch, "E567.trimOffspring", {"start": v(-193, 50) * mm, "end": v(0, 50) * mm});
            skLineSegment(sketch, "E568.trimOffspring", {"start": v(-193, 49.5) * mm, "end": v(-173, 49.5) * mm});
            skLineSegment(sketch, "E569.trimOffspring", {"start": v(-193, 50) * mm, "end": v(-172, 50) * mm});
            skLineSegment(sketch, "E570.trimOffspring", {"start": v(-193, 50.5) * mm, "end": v(-172, 50.5) * mm});
            skLineSegment(sketch, "E571.trimOffspring", {"start": v(-193, 50.5) * mm, "end": v(-193, 39.5) * mm});
            skLineSegment(sketch, "E572.trimOffspring", {"start": v(-192.5, 50.5) * mm, "end": v(-192.5, 39.5) * mm});
            skLineSegment(sketch, "E573.trimOffspring", {"start": v(-183, 39.5) * mm, "end": v(-172.5, 39.5) * mm});
            skLineSegment(sketch, "E574.trimOffspring", {"start": v(-192, 20.5) * mm, "end": v(-192, 0) * mm});
            skLineSegment(sketch, "E575.trimOffspring", {"start": v(-183, 40) * mm, "end": v(-172, 40) * mm});
            skLineSegment(sketch, "E576.trimOffspring", {"start": v(-183, 39.5) * mm, "end": v(-172, 39.5) * mm});
            skLineSegment(sketch, "E577.trimOffspring", {"start": v(-193, 20.5) * mm, "end": v(-193, 0) * mm});
            skLineSegment(sketch, "E578.trimOffspring", {"start": v(-192.5, 20.5) * mm, "end": v(-192.5, 0) * mm});
            skLineSegment(sketch, "E579.trimOffspring", {"start": v(-182.5, 20.5) * mm, "end": v(-182.5, 0) * mm});
            skLineSegment(sketch, "E580.trimOffspring", {"start": v(-183, 20.5) * mm, "end": v(-183, 0) * mm});
            skLineSegment(sketch, "E581.trimOffspring", {"start": v(-182, 20.5) * mm, "end": v(-182, 0) * mm});
            skLineSegment(sketch, "E582.trimOffspring", {"start": v(-183, 40.5) * mm, "end": v(-172, 40.5) * mm});
            skLineSegment(sketch, "E583.trimOffspring", {"start": v(-192, 50.5) * mm, "end": v(-192, 39.5) * mm});
            skLineSegment(sketch, "E584.trimOffspring", {"start": v(-173, 59.5) * mm, "end": v(-9.5, 59.5) * mm});
            skLineSegment(sketch, "E585.trimOffspring", {"start": v(-173, 40.5) * mm, "end": v(-173, 0) * mm});
            skLineSegment(sketch, "E586.trimOffspring", {"start": v(-172.5, 40.5) * mm, "end": v(-172.5, 0) * mm});
            skLineSegment(sketch, "E587.trimOffspring", {"start": v(-173, 60) * mm, "end": v(-10, 60) * mm});
            skLineSegment(sketch, "E588.trimOffspring", {"start": v(-183, 40) * mm, "end": v(0, 40) * mm});
            skLineSegment(sketch, "E589.trimOffspring", {"start": v(-172, 40.5) * mm, "end": v(-172, 0.5) * mm});
            skLineSegment(sketch, "E590.trimOffspring", {"start": v(-137.37, 49.5) * mm, "end": v(0, 49.5) * mm});
            skLineSegment(sketch, "E591.trimOffspring", {"start": v(-137.37, 39.5) * mm, "end": v(0, 39.5) * mm});
            skLineSegment(sketch, "E592.trimOffspring", {"start": v(-183, 40) * mm, "end": v(-172.5, 40) * mm});
            skLineSegment(sketch, "E593.trimOffspring", {"start": v(-137.37, 40.5) * mm, "end": v(0, 40.5) * mm});
            skLineSegment(sketch, "E594.trimOffspring", {"start": v(-137.37, 50.5) * mm, "end": v(-136.38, 50.5) * mm});
            skLineSegment(sketch, "E595.trimOffspring", {"start": v(-137.37, 40) * mm, "end": v(0, 40) * mm});
            skLineSegment(sketch, "E596.trimOffspring", {"start": v(-183, 50.5) * mm, "end": v(-183, 39.5) * mm});
            skLineSegment(sketch, "E597.trimOffspring", {"start": v(-182, 50.5) * mm, "end": v(-182, 39.5) * mm});
            skLineSegment(sketch, "E598.trimOffspring", {"start": v(-182.5, 50.5) * mm, "end": v(-182.5, 39.5) * mm});
            skLineSegment(sketch, "E599.trimOffspring", {"start": v(-173, 59.5) * mm, "end": v(-136.38, 59.5) * mm});
            skLineSegment(sketch, "E600.trimOffspring", {"start": v(-173, 60.5) * mm, "end": v(-9.5, 60.5) * mm});
            skLineSegment(sketch, "E601.trimOffspring", {"start": v(-91.75, 50) * mm, "end": v(0, 50) * mm});
            skLineSegment(sketch, "E602.trimOffspring", {"start": v(-91.75, 50.5) * mm, "end": v(0, 50.5) * mm});
            skLineSegment(sketch, "E603.trimOffspring", {"start": v(-91.75, 59.5) * mm, "end": v(-9.5, 59.5) * mm});
            skLineSegment(sketch, "E604.trimOffspring", {"start": v(-91.75, 60) * mm, "end": v(-9.5, 60) * mm});
            skLineSegment(sketch, "E605.trimOffspring", {"start": v(-91.75, 60.5) * mm, "end": v(-9.5, 60.5) * mm});
            skLineSegment(sketch, "E606.trimOffspring", {"start": v(-173, 60) * mm, "end": v(-136.38, 60) * mm});
            skLineSegment(sketch, "E607.trimOffspring", {"start": v(-173, 60.5) * mm, "end": v(-136.38, 60.5) * mm});
            skLineSegment(sketch, "E608.trimOffspring", {"start": v(-173, 60) * mm, "end": v(-9.5, 60) * mm});
            skPoint(sketch, "E609.orphan", {"position": v(-172.5, -163) * mm});
            skPoint(sketch, "E610.orphan", {"position": v(-172.5, -125.5) * mm});
            skPoint(sketch, "E611.orphan", {"position": v(-172.5, -124.5) * mm});
            skPoint(sketch, "E612.orphan", {"position": v(-172.5, 20.5) * mm});
            skPoint(sketch, "E613.orphan", {"position": v(172.5, -125.5) * mm});
            skPoint(sketch, "E614.orphan", {"position": v(172.5, -124.5) * mm});
            skPoint(sketch, "E615.orphan", {"position": v(172.5, -163) * mm});
            skLineSegment(sketch, "E616.trimOffspring", {"start": v(9.5, 40.5) * mm, "end": v(9.5, 0) * mm});
            skLineSegment(sketch, "E617.trimOffspring", {"start": v(10, 40.5) * mm, "end": v(10, 0) * mm});
            skLineSegment(sketch, "E618.trimOffspring", {"start": v(10.5, 40.5) * mm, "end": v(10.5, 0) * mm});
            skLineSegment(sketch, "E619.trimOffspring", {"start": v(-0.5, 59.5) * mm, "end": v(0, 59.5) * mm});
            skLineSegment(sketch, "E620.trimOffspring", {"start": v(-0.5, 60) * mm, "end": v(0, 60) * mm});
            skLineSegment(sketch, "E621.trimOffspring", {"start": v(-0.5, 60.5) * mm, "end": v(0, 60.5) * mm});
            skLineSegment(sketch, "E622", {"start": v(-172, 0.5) * mm, "end": v(-172, 0) * mm});
            skSolve(sketch);
        }
        {
            var Q0;
            Q0=qCreatedBy(makeId("Right.planeOp"),FACE);
            cPlane(context, id + "F26", {"entities" : qUnion([Q0]), "cplaneType" : CPlaneType.OFFSET, "offset" : 182.5 * mm, "width" : 150 * mm, "height" : 150 * mm});
        }
        {
            var Q0;
            Q0=qCreatedBy(makeId("Front.planeOp"),FACE);
            cPlane(context, id + "F27", {"entities" : qUnion([Q0]), "cplaneType" : CPlaneType.OFFSET, "offset" : 50 * mm, "width" : 150 * mm, "height" : 150 * mm});
        }
        {
            var Q0;
            Q0=qCreatedBy(makeId("Right.planeOp"),FACE);
            cPlane(context, id + "F28", {"entities" : qUnion([Q0]), "cplaneType" : CPlaneType.OFFSET, "offset" : 172.5 * mm, "oppositeDirection" : true, "width" : 150 * mm, "height" : 150 * mm});
        }
        {
            var Q0;
            Q0=qCreatedBy(makeId("Front.planeOp"),FACE);
            cPlane(context, id + "F29", {"entities" : qUnion([Q0]), "cplaneType" : CPlaneType.OFFSET, "offset" : 50 * mm, "oppositeDirection" : true, "width" : 150 * mm, "height" : 150 * mm});
        }
        {
            var Q0;
            Q0=qCreatedBy(makeId("Right.planeOp"),FACE);
            var sketch = newSketch(context, id + "F30", { "sketchPlane" : qUnion([Q0])});
            skLineSegment(sketch, "E623", {"start": v(0, 20) * mm, "end": v(-200, 20) * mm});
            skPoint(sketch, "E624", {"position": v(-20, 20) * mm});
            skPoint(sketch, "E625", {"position": v(-40, 20) * mm});
            skPoint(sketch, "E626", {"position": v(-165, 20) * mm});
            skPoint(sketch, "E627", {"position": v(-60, 20) * mm});
            skPoint(sketch, "E628", {"position": v(-95, 20) * mm});
            skPoint(sketch, "E629", {"position": v(-130, 20) * mm});
            skPoint(sketch, "E630", {"position": v(-100, 20) * mm});
            skPoint(sketch, "E631.MirrorP", {"position": v(20, 20) * mm});
            skPoint(sketch, "E632.MirrorP", {"position": v(40, 20) * mm});
            skLineSegment(sketch, "E633", {"start": v(40, 20) * mm, "end": v(0, 20) * mm});
            skLineSegment(sketch, "E634.bottom", {"start": v(40, 20) * mm, "end": v(-200, 20) * mm});
            skLineSegment(sketch, "E634.top", {"start": v(40, 10) * mm, "end": v(-200, 10) * mm});
            skLineSegment(sketch, "E634.left", {"start": v(40, 20) * mm, "end": v(40, 10) * mm});
            skLineSegment(sketch, "E634.right", {"start": v(-200, 20) * mm, "end": v(-200, 10) * mm});
            skLineSegment(sketch, "E635", {"start": v(20, 20) * mm, "end": v(20, 10) * mm});
            skLineSegment(sketch, "E636", {"start": v(40, 15) * mm, "end": v(-200, 15) * mm});
            skLineSegment(sketch, "E637", {"start": v(-20, 20) * mm, "end": v(-20, 10) * mm});
            skLineSegment(sketch, "E638", {"start": v(0, 20) * mm, "end": v(0, 10) * mm});
            skLineSegment(sketch, "E639", {"start": v(-40, 20) * mm, "end": v(-40, 10) * mm});
            skLineSegment(sketch, "E640", {"start": v(-60, 20) * mm, "end": v(-60, 10) * mm});
            skLineSegment(sketch, "E641", {"start": v(-95, 20) * mm, "end": v(-95, 10) * mm});
            skLineSegment(sketch, "E642", {"start": v(-130, 20) * mm, "end": v(-130, 10) * mm});
            skLineSegment(sketch, "E643", {"start": v(-165, 20) * mm, "end": v(-165, 10) * mm});
            skLineSegment(sketch, "E644.bottom", {"start": v(-200, 10) * mm, "end": v(40, 10) * mm});
            skLineSegment(sketch, "E644.top", {"start": v(-200, 0) * mm, "end": v(40, 0) * mm});
            skLineSegment(sketch, "E644.left", {"start": v(-200, 10) * mm, "end": v(-200, 0) * mm});
            skLineSegment(sketch, "E644.right", {"start": v(40, 10) * mm, "end": v(40, 0) * mm});
            skLineSegment(sketch, "E645.bottom", {"start": v(200, 10.5) * mm, "end": v(-200, 10.5) * mm});
            skLineSegment(sketch, "E645.top", {"start": v(200, 9.5) * mm, "end": v(-200, 9.5) * mm});
            skLineSegment(sketch, "E645.left", {"start": v(200, 10.5) * mm, "end": v(200, 9.5) * mm});
            skLineSegment(sketch, "E645.right", {"start": v(-200, 10.5) * mm, "end": v(-200, 9.5) * mm});
            skPoint(sketch, "E645.middle", {"position": v(0, 10) * mm});
            skLineSegment(sketch, "E646.bottom", {"start": v(200, 14.5) * mm, "end": v(-200, 14.5) * mm});
            skLineSegment(sketch, "E646.top", {"start": v(200, 15.5) * mm, "end": v(-200, 15.5) * mm});
            skLineSegment(sketch, "E646.left", {"start": v(200, 14.5) * mm, "end": v(200, 15.5) * mm});
            skLineSegment(sketch, "E646.right", {"start": v(-200, 14.5) * mm, "end": v(-200, 15.5) * mm});
            skPoint(sketch, "E646.middle", {"position": v(0, 15) * mm});
            skLineSegment(sketch, "E647.bottom", {"start": v(-200, 19.5) * mm, "end": v(200, 19.5) * mm});
            skLineSegment(sketch, "E647.top", {"start": v(-200, 20.5) * mm, "end": v(200, 20.5) * mm});
            skLineSegment(sketch, "E647.left", {"start": v(-200, 19.5) * mm, "end": v(-200, 20.5) * mm});
            skLineSegment(sketch, "E647.right", {"start": v(200, 19.5) * mm, "end": v(200, 20.5) * mm});
            skPoint(sketch, "E647.middle", {"position": v(0, 20) * mm});
            skLineSegment(sketch, "E648.bottom", {"start": v(40.5, 20) * mm, "end": v(39.5, 20) * mm});
            skLineSegment(sketch, "E648.top", {"start": v(40.5, 10) * mm, "end": v(39.5, 10) * mm});
            skLineSegment(sketch, "E648.left", {"start": v(40.5, 20) * mm, "end": v(40.5, 10) * mm});
            skLineSegment(sketch, "E648.right", {"start": v(39.5, 20) * mm, "end": v(39.5, 10) * mm});
            skPoint(sketch, "E648.middle", {"position": v(40, 15) * mm});
            skLineSegment(sketch, "E649.bottom", {"start": v(20.5, 20) * mm, "end": v(19.5, 20) * mm});
            skLineSegment(sketch, "E649.top", {"start": v(20.5, 10) * mm, "end": v(19.5, 10) * mm});
            skLineSegment(sketch, "E649.left", {"start": v(20.5, 20) * mm, "end": v(20.5, 10) * mm});
            skLineSegment(sketch, "E649.right", {"start": v(19.5, 20) * mm, "end": v(19.5, 10) * mm});
            skPoint(sketch, "E649.middle", {"position": v(20, 15) * mm});
            skLineSegment(sketch, "E650.bottom", {"start": v(0.5, 20) * mm, "end": v(-0.5, 20) * mm});
            skLineSegment(sketch, "E650.top", {"start": v(0.5, 10) * mm, "end": v(-0.5, 10) * mm});
            skLineSegment(sketch, "E650.left", {"start": v(0.5, 20) * mm, "end": v(0.5, 10) * mm});
            skLineSegment(sketch, "E650.right", {"start": v(-0.5, 20) * mm, "end": v(-0.5, 10) * mm});
            skLineSegment(sketch, "E651.bottom", {"start": v(-19.5, 20) * mm, "end": v(-20.5, 20) * mm});
            skLineSegment(sketch, "E651.top", {"start": v(-19.5, 10) * mm, "end": v(-20.5, 10) * mm});
            skLineSegment(sketch, "E651.left", {"start": v(-19.5, 20) * mm, "end": v(-19.5, 10) * mm});
            skLineSegment(sketch, "E651.right", {"start": v(-20.5, 20) * mm, "end": v(-20.5, 10) * mm});
            skPoint(sketch, "E651.middle", {"position": v(-20, 15) * mm});
            skLineSegment(sketch, "E652.bottom", {"start": v(-39.5, 20) * mm, "end": v(-40.5, 20) * mm});
            skLineSegment(sketch, "E652.top", {"start": v(-39.5, 10) * mm, "end": v(-40.5, 10) * mm});
            skLineSegment(sketch, "E652.left", {"start": v(-39.5, 20) * mm, "end": v(-39.5, 10) * mm});
            skLineSegment(sketch, "E652.right", {"start": v(-40.5, 20) * mm, "end": v(-40.5, 10) * mm});
            skPoint(sketch, "E652.middle", {"position": v(-40, 15) * mm});
            skLineSegment(sketch, "E653.bottom", {"start": v(-59.5, 20) * mm, "end": v(-60.5, 20) * mm});
            skLineSegment(sketch, "E653.top", {"start": v(-59.5, 10) * mm, "end": v(-60.5, 10) * mm});
            skLineSegment(sketch, "E653.left", {"start": v(-59.5, 20) * mm, "end": v(-59.5, 10) * mm});
            skLineSegment(sketch, "E653.right", {"start": v(-60.5, 20) * mm, "end": v(-60.5, 10) * mm});
            skPoint(sketch, "E653.middle", {"position": v(-60, 15) * mm});
            skLineSegment(sketch, "E654.bottom", {"start": v(-95.5, 20) * mm, "end": v(-94.5, 20) * mm});
            skLineSegment(sketch, "E654.top", {"start": v(-95.5, 10) * mm, "end": v(-94.5, 10) * mm});
            skLineSegment(sketch, "E654.left", {"start": v(-95.5, 20) * mm, "end": v(-95.5, 10) * mm});
            skLineSegment(sketch, "E654.right", {"start": v(-94.5, 20) * mm, "end": v(-94.5, 10) * mm});
            skPoint(sketch, "E654.middle", {"position": v(-95, 15) * mm});
            skLineSegment(sketch, "E655.bottom", {"start": v(-129.5, 20) * mm, "end": v(-130.5, 20) * mm});
            skLineSegment(sketch, "E655.top", {"start": v(-129.5, 10) * mm, "end": v(-130.5, 10) * mm});
            skLineSegment(sketch, "E655.left", {"start": v(-129.5, 20) * mm, "end": v(-129.5, 10) * mm});
            skLineSegment(sketch, "E655.right", {"start": v(-130.5, 20) * mm, "end": v(-130.5, 10) * mm});
            skPoint(sketch, "E655.middle", {"position": v(-130, 15) * mm});
            skLineSegment(sketch, "E656.bottom", {"start": v(-164.5, 20) * mm, "end": v(-165.5, 20) * mm});
            skLineSegment(sketch, "E656.top", {"start": v(-164.5, 10) * mm, "end": v(-165.5, 10) * mm});
            skLineSegment(sketch, "E656.left", {"start": v(-164.5, 20) * mm, "end": v(-164.5, 10) * mm});
            skLineSegment(sketch, "E656.right", {"start": v(-165.5, 20) * mm, "end": v(-165.5, 10) * mm});
            skPoint(sketch, "E656.middle", {"position": v(-165, 15) * mm});
            skSolve(sketch);
        }
        {
            var Q0;
            Q0=qCreatedBy(id+"F27.planeOp",FACE);
            var sketch = newSketch(context, id + "F31", { "sketchPlane" : qUnion([Q0])});
            skLineSegment(sketch, "E657.bottom", {"start": v(-365, 20) * mm, "end": v(365, 20) * mm});
            skLineSegment(sketch, "E657.top", {"start": v(-365, 0) * mm, "end": v(365, 0) * mm});
            skLineSegment(sketch, "E657.left", {"start": v(-365, 20) * mm, "end": v(-365, 0) * mm});
            skLineSegment(sketch, "E657.right", {"start": v(365, 20) * mm, "end": v(365, 0) * mm});
            skLineSegment(sketch, "E658", {"start": v(-365, 10) * mm, "end": v(365, 10) * mm});
            skLineSegment(sketch, "E659", {"start": v(-365, 15) * mm, "end": v(365, 15) * mm});
            skPoint(sketch, "E660", {"position": v(10, 20) * mm});
            skPoint(sketch, "E661", {"position": v(50.63, 20) * mm});
            skPoint(sketch, "E662", {"position": v(91.25, 20) * mm});
            skPoint(sketch, "E663", {"position": v(131.88, 20) * mm});
            skPoint(sketch, "E664", {"position": v(172.5, 20) * mm});
            skPoint(sketch, "E665", {"position": v(321.88, 20) * mm});
            skPoint(sketch, "E666", {"position": v(192.5, 20) * mm});
            skPoint(sketch, "E667", {"position": v(235.63, 20) * mm});
            skPoint(sketch, "E668", {"position": v(278.75, 20) * mm});
            skLineSegment(sketch, "E669", {"start": v(10, 20) * mm, "end": v(10, 10) * mm});
            skLineSegment(sketch, "E670", {"start": v(50.63, 20) * mm, "end": v(50.63, 10) * mm});
            skLineSegment(sketch, "E671", {"start": v(91.25, 20) * mm, "end": v(91.25, 10) * mm});
            skLineSegment(sketch, "E672", {"start": v(131.88, 20) * mm, "end": v(131.88, 10) * mm});
            skLineSegment(sketch, "E673", {"start": v(172.5, 20) * mm, "end": v(172.5, 10) * mm});
            skLineSegment(sketch, "E674", {"start": v(192.5, 20) * mm, "end": v(192.5, 10) * mm});
            skLineSegment(sketch, "E675", {"start": v(235.63, 20) * mm, "end": v(235.63, 10) * mm});
            skLineSegment(sketch, "E676", {"start": v(278.75, 20) * mm, "end": v(278.75, 10) * mm});
            skLineSegment(sketch, "E677", {"start": v(321.88, 20) * mm, "end": v(321.88, 10) * mm});
            skLineSegment(sketch, "E678.MirrorCS", {"start": v(-10, 20) * mm, "end": v(-10, 10) * mm});
            skLineSegment(sketch, "E679.MirrorCS", {"start": v(-50.63, 20) * mm, "end": v(-50.63, 10) * mm});
            skLineSegment(sketch, "E680.MirrorCS", {"start": v(-91.25, 20) * mm, "end": v(-91.25, 10) * mm});
            skLineSegment(sketch, "E681.MirrorCS", {"start": v(-131.88, 20) * mm, "end": v(-131.88, 10) * mm});
            skLineSegment(sketch, "E682.MirrorCS", {"start": v(-172.5, 20) * mm, "end": v(-172.5, 10) * mm});
            skLineSegment(sketch, "E683.MirrorCS", {"start": v(-192.5, 20) * mm, "end": v(-192.5, 10) * mm});
            skLineSegment(sketch, "E684.MirrorCS", {"start": v(-235.63, 20) * mm, "end": v(-235.63, 10) * mm});
            skLineSegment(sketch, "E685.MirrorCS", {"start": v(-278.75, 20) * mm, "end": v(-278.75, 10) * mm});
            skLineSegment(sketch, "E686.MirrorCS", {"start": v(-321.88, 20) * mm, "end": v(-321.88, 10) * mm});
            skLineSegment(sketch, "E687.bottom", {"start": v(-365, 10.5) * mm, "end": v(365, 10.5) * mm});
            skLineSegment(sketch, "E687.top", {"start": v(-365, 9.5) * mm, "end": v(365, 9.5) * mm});
            skLineSegment(sketch, "E687.left", {"start": v(-365, 10.5) * mm, "end": v(-365, 9.5) * mm});
            skLineSegment(sketch, "E687.right", {"start": v(365, 10.5) * mm, "end": v(365, 9.5) * mm});
            skPoint(sketch, "E687.middle", {"position": v(0, 10) * mm});
            skLineSegment(sketch, "E688.bottom", {"start": v(-365, 15.5) * mm, "end": v(365, 15.5) * mm});
            skLineSegment(sketch, "E688.top", {"start": v(-365, 14.5) * mm, "end": v(365, 14.5) * mm});
            skLineSegment(sketch, "E688.left", {"start": v(-365, 15.5) * mm, "end": v(-365, 14.5) * mm});
            skLineSegment(sketch, "E688.right", {"start": v(365, 15.5) * mm, "end": v(365, 14.5) * mm});
            skPoint(sketch, "E688.middle", {"position": v(0, 15) * mm});
            skLineSegment(sketch, "E689.bottom", {"start": v(-365, 20.5) * mm, "end": v(365, 20.5) * mm});
            skLineSegment(sketch, "E689.top", {"start": v(-365, 19.5) * mm, "end": v(365, 19.5) * mm});
            skLineSegment(sketch, "E689.left", {"start": v(-365, 20.5) * mm, "end": v(-365, 19.5) * mm});
            skLineSegment(sketch, "E689.right", {"start": v(365, 20.5) * mm, "end": v(365, 19.5) * mm});
            skPoint(sketch, "E689.middle", {"position": v(0, 20) * mm});
            skLineSegment(sketch, "E690.bottom", {"start": v(-10.5, 20) * mm, "end": v(-9.5, 20) * mm});
            skLineSegment(sketch, "E690.top", {"start": v(-10.5, 10) * mm, "end": v(-9.5, 10) * mm});
            skLineSegment(sketch, "E690.left", {"start": v(-10.5, 20) * mm, "end": v(-10.5, 10) * mm});
            skLineSegment(sketch, "E690.right", {"start": v(-9.5, 20) * mm, "end": v(-9.5, 10) * mm});
            skPoint(sketch, "E690.middle", {"position": v(-10, 15) * mm});
            skLineSegment(sketch, "E691.bottom", {"start": v(-0.5, 20) * mm, "end": v(0.5, 20) * mm});
            skLineSegment(sketch, "E691.top", {"start": v(-0.5, 10) * mm, "end": v(0.5, 10) * mm});
            skLineSegment(sketch, "E691.left", {"start": v(-0.5, 20) * mm, "end": v(-0.5, 10) * mm});
            skLineSegment(sketch, "E691.right", {"start": v(0.5, 20) * mm, "end": v(0.5, 10) * mm});
            skLineSegment(sketch, "E692.bottom", {"start": v(-51.13, 20) * mm, "end": v(-50.13, 20) * mm});
            skLineSegment(sketch, "E692.top", {"start": v(-51.13, 10) * mm, "end": v(-50.13, 10) * mm});
            skLineSegment(sketch, "E692.left", {"start": v(-51.13, 20) * mm, "end": v(-51.13, 10) * mm});
            skLineSegment(sketch, "E692.right", {"start": v(-50.13, 20) * mm, "end": v(-50.13, 10) * mm});
            skPoint(sketch, "E692.middle", {"position": v(-50.63, 15) * mm});
            skLineSegment(sketch, "E693.bottom", {"start": v(-91.75, 20) * mm, "end": v(-90.75, 20) * mm});
            skLineSegment(sketch, "E693.top", {"start": v(-91.75, 10) * mm, "end": v(-90.75, 10) * mm});
            skLineSegment(sketch, "E693.left", {"start": v(-91.75, 20) * mm, "end": v(-91.75, 10) * mm});
            skLineSegment(sketch, "E693.right", {"start": v(-90.75, 20) * mm, "end": v(-90.75, 10) * mm});
            skPoint(sketch, "E693.middle", {"position": v(-91.25, 15) * mm});
            skLineSegment(sketch, "E694.bottom", {"start": v(-131.38, 20) * mm, "end": v(-132.38, 20) * mm});
            skLineSegment(sketch, "E694.top", {"start": v(-131.38, 10) * mm, "end": v(-132.38, 10) * mm});
            skLineSegment(sketch, "E694.left", {"start": v(-131.38, 20) * mm, "end": v(-131.38, 10) * mm});
            skLineSegment(sketch, "E694.right", {"start": v(-132.38, 20) * mm, "end": v(-132.38, 10) * mm});
            skPoint(sketch, "E694.middle", {"position": v(-131.88, 15) * mm});
            skLineSegment(sketch, "E695.bottom", {"start": v(-173, 20) * mm, "end": v(-172, 20) * mm});
            skLineSegment(sketch, "E695.top", {"start": v(-173, 10) * mm, "end": v(-172, 10) * mm});
            skLineSegment(sketch, "E695.left", {"start": v(-173, 20) * mm, "end": v(-173, 10) * mm});
            skLineSegment(sketch, "E695.right", {"start": v(-172, 20) * mm, "end": v(-172, 10) * mm});
            skPoint(sketch, "E695.middle", {"position": v(-172.5, 15) * mm});
            skLineSegment(sketch, "E696.bottom", {"start": v(-192, 20) * mm, "end": v(-193, 20) * mm});
            skLineSegment(sketch, "E696.top", {"start": v(-192, 10) * mm, "end": v(-193, 10) * mm});
            skLineSegment(sketch, "E696.left", {"start": v(-192, 20) * mm, "end": v(-192, 10) * mm});
            skLineSegment(sketch, "E696.right", {"start": v(-193, 20) * mm, "end": v(-193, 10) * mm});
            skPoint(sketch, "E696.middle", {"position": v(-192.5, 15) * mm});
            skLineSegment(sketch, "E697.bottom", {"start": v(-235.13, 20) * mm, "end": v(-236.13, 20) * mm});
            skLineSegment(sketch, "E697.top", {"start": v(-235.13, 10) * mm, "end": v(-236.13, 10) * mm});
            skLineSegment(sketch, "E697.left", {"start": v(-235.13, 20) * mm, "end": v(-235.13, 10) * mm});
            skLineSegment(sketch, "E697.right", {"start": v(-236.13, 20) * mm, "end": v(-236.13, 10) * mm});
            skPoint(sketch, "E697.middle", {"position": v(-235.63, 15) * mm});
            skLineSegment(sketch, "E698.bottom", {"start": v(-278.25, 20) * mm, "end": v(-279.25, 20) * mm});
            skLineSegment(sketch, "E698.top", {"start": v(-278.25, 10) * mm, "end": v(-279.25, 10) * mm});
            skLineSegment(sketch, "E698.left", {"start": v(-278.25, 20) * mm, "end": v(-278.25, 10) * mm});
            skLineSegment(sketch, "E698.right", {"start": v(-279.25, 20) * mm, "end": v(-279.25, 10) * mm});
            skPoint(sketch, "E698.middle", {"position": v(-278.75, 15) * mm});
            skLineSegment(sketch, "E699.bottom", {"start": v(-321.38, 20) * mm, "end": v(-322.38, 20) * mm});
            skLineSegment(sketch, "E699.top", {"start": v(-321.38, 10) * mm, "end": v(-322.38, 10) * mm});
            skLineSegment(sketch, "E699.left", {"start": v(-321.38, 20) * mm, "end": v(-321.38, 10) * mm});
            skLineSegment(sketch, "E699.right", {"start": v(-322.38, 20) * mm, "end": v(-322.38, 10) * mm});
            skPoint(sketch, "E699.middle", {"position": v(-321.88, 15) * mm});
            skLineSegment(sketch, "E700.MirrorCS", {"start": v(9.5, 20) * mm, "end": v(9.5, 10) * mm});
            skLineSegment(sketch, "E701.MirrorCS", {"start": v(10.5, 20) * mm, "end": v(10.5, 10) * mm});
            skLineSegment(sketch, "E702.MirrorCS", {"start": v(50.13, 20) * mm, "end": v(50.13, 10) * mm});
            skLineSegment(sketch, "E703.MirrorCS", {"start": v(51.13, 20) * mm, "end": v(51.13, 10) * mm});
            skLineSegment(sketch, "E704.MirrorCS", {"start": v(90.75, 20) * mm, "end": v(90.75, 10) * mm});
            skLineSegment(sketch, "E705.MirrorCS", {"start": v(91.75, 20) * mm, "end": v(91.75, 10) * mm});
            skLineSegment(sketch, "E706.MirrorCS", {"start": v(132.38, 20) * mm, "end": v(132.38, 10) * mm});
            skLineSegment(sketch, "E707.MirrorCS", {"start": v(131.38, 20) * mm, "end": v(131.38, 10) * mm});
            skLineSegment(sketch, "E708.MirrorCS", {"start": v(172, 20) * mm, "end": v(172, 10) * mm});
            skLineSegment(sketch, "E709.MirrorCS", {"start": v(173, 20) * mm, "end": v(173, 10) * mm});
            skLineSegment(sketch, "E710.MirrorCS", {"start": v(192, 20) * mm, "end": v(192, 10) * mm});
            skLineSegment(sketch, "E711.MirrorCS", {"start": v(193, 20) * mm, "end": v(193, 10) * mm});
            skLineSegment(sketch, "E712.MirrorCS", {"start": v(235.13, 20) * mm, "end": v(235.13, 10) * mm});
            skLineSegment(sketch, "E713.MirrorCS", {"start": v(236.13, 20) * mm, "end": v(236.13, 10) * mm});
            skLineSegment(sketch, "E714.MirrorCS", {"start": v(321.38, 20) * mm, "end": v(321.38, 10) * mm});
            skLineSegment(sketch, "E715.MirrorCS", {"start": v(322.38, 20) * mm, "end": v(322.38, 10) * mm});
            skSolve(sketch);
        }
        {
            var Q0;
            {var subQ76=sQuery(id+"F25.wireOp",EDGE,"E212.top");Q0=makeQuery(id+"F25.imprint","IMPRINT",FACE,{"disambiguationData":[TD([[makeQuery(id+"F25.imprint","IMPRINT",EDGE,{"derivedFrom":subQ76}),-1.0]])]});}
            extrude(context, id + "F32", {"entities" : qUnion([Q0]), "operationType" : NewBodyOperationType.REMOVE, "depth" : 25 * mm, "offsetDistance" : 25 * mm});
        }
        {
            var Q0;
            {var subQ0=sQuery(id+"F25.wireOp",EDGE,"E533.trimOffspring");var subQ1=sQuery(id+"F25.wireOp",EDGE,"E517.trimOffspring");var subQ2=makeQuery(id+"F25.imprint","INTERSECT",VERTEX,{"derivedFrom":[subQ1,subQ0]});Q0=makeQuery(id+"F25.imprint","IMPRINT",FACE,{"disambiguationData":[TD([[makeQuery(id+"F25.imprint","IMPRINT",EDGE,{"disambiguationData":[TD([[subQ2,-1.0]])],"derivedFrom":subQ1}),1.0]])]});}
            var Q1;
            {var subQ1=sQuery(id+"F25.wireOp",EDGE,"E248.left");var subQ3=sQuery(id+"F25.wireOp",EDGE,"E517.trimOffspring");var subQ4=makeQuery(id+"F25.imprint","INTERSECT",VERTEX,{"derivedFrom":[subQ1,subQ3]});Q1=makeQuery(id+"F25.imprint","IMPRINT",FACE,{"disambiguationData":[TD([[makeQuery(id+"F25.imprint","IMPRINT",EDGE,{"disambiguationData":[TD([[subQ4,1.0]])],"derivedFrom":subQ3}),1.0]])]});}
            var Q2;
            {var subQ0=sQuery(id+"F25.wireOp",EDGE,"E275.trimOffspring");var subQ1=sQuery(id+"F25.wireOp",EDGE,"E248.left");var subQ2=makeQuery(id+"F25.imprint","INTERSECT",VERTEX,{"derivedFrom":[subQ1,subQ0]});Q2=makeQuery(id+"F25.imprint","IMPRINT",FACE,{"disambiguationData":[TD([[makeQuery(id+"F25.imprint","IMPRINT",EDGE,{"disambiguationData":[TD([[subQ2,-1.0]])],"derivedFrom":subQ1}),1.0]])]});}
            var Q3;
            {var subQ0=sQuery(id+"F25.wireOp",EDGE,"E273.trimOffspring");var subQ1=sQuery(id+"F25.wireOp",EDGE,"E248.left");var subQ2=makeQuery(id+"F25.imprint","INTERSECT",VERTEX,{"derivedFrom":[subQ1,subQ0]});Q3=makeQuery(id+"F25.imprint","IMPRINT",FACE,{"disambiguationData":[TD([[makeQuery(id+"F25.imprint","IMPRINT",EDGE,{"disambiguationData":[TD([[subQ2,-1.0]])],"derivedFrom":subQ1}),1.0]])]});}
            var Q4;
            {var subQ0=sQuery(id+"F25.wireOp",EDGE,"E272.trimOffspring");var subQ1=sQuery(id+"F25.wireOp",EDGE,"E248.left");var subQ2=makeQuery(id+"F25.imprint","INTERSECT",VERTEX,{"derivedFrom":[subQ1,subQ0]});Q4=makeQuery(id+"F25.imprint","IMPRINT",FACE,{"disambiguationData":[TD([[makeQuery(id+"F25.imprint","IMPRINT",EDGE,{"disambiguationData":[TD([[subQ2,-1.0]])],"derivedFrom":subQ1}),1.0]])]});}
            var Q5;
            {var subQ0=sQuery(id+"F25.wireOp",EDGE,"E274.trimOffspring");var subQ1=sQuery(id+"F25.wireOp",EDGE,"E248.left");var subQ2=makeQuery(id+"F25.imprint","INTERSECT",VERTEX,{"derivedFrom":[subQ1,subQ0]});Q5=makeQuery(id+"F25.imprint","IMPRINT",FACE,{"disambiguationData":[TD([[makeQuery(id+"F25.imprint","IMPRINT",EDGE,{"disambiguationData":[TD([[subQ2,-1.0]])],"derivedFrom":subQ1}),1.0]])]});}
            var Q6;
            {var subQ0=sQuery(id+"F25.wireOp",EDGE,"E270.trimOffspring");var subQ1=sQuery(id+"F25.wireOp",EDGE,"E248.left");var subQ2=makeQuery(id+"F25.imprint","INTERSECT",VERTEX,{"derivedFrom":[subQ1,subQ0]});Q6=makeQuery(id+"F25.imprint","IMPRINT",FACE,{"disambiguationData":[TD([[makeQuery(id+"F25.imprint","IMPRINT",EDGE,{"disambiguationData":[TD([[subQ2,-1.0]])],"derivedFrom":subQ1}),1.0]])]});}
            var Q7;
            {var subQ0=sQuery(id+"F25.wireOp",EDGE,"E268.trimOffspring");var subQ1=sQuery(id+"F25.wireOp",EDGE,"E248.left");var subQ2=makeQuery(id+"F25.imprint","INTERSECT",VERTEX,{"derivedFrom":[subQ1,subQ0]});Q7=makeQuery(id+"F25.imprint","IMPRINT",FACE,{"disambiguationData":[TD([[makeQuery(id+"F25.imprint","IMPRINT",EDGE,{"disambiguationData":[TD([[subQ2,-1.0]])],"derivedFrom":subQ1}),1.0]])]});}
            var Q8;
            {var subQ0=sQuery(id+"F25.wireOp",EDGE,"E268.trimOffspring");var subQ1=sQuery(id+"F25.wireOp",EDGE,"E246.right");var subQ2=makeQuery(id+"F25.imprint","INTERSECT",VERTEX,{"derivedFrom":[subQ1,subQ0]});Q8=makeQuery(id+"F25.imprint","IMPRINT",FACE,{"disambiguationData":[TD([[makeQuery(id+"F25.imprint","IMPRINT",EDGE,{"disambiguationData":[TD([[subQ2,-1.0]])],"derivedFrom":subQ1}),-1.0]])]});}
            var Q9;
            {var subQ0=sQuery(id+"F25.wireOp",EDGE,"E268.trimOffspring");var subQ1=sQuery(id+"F25.wireOp",EDGE,"E245.right");var subQ2=makeQuery(id+"F25.imprint","INTERSECT",VERTEX,{"derivedFrom":[subQ1,subQ0]});Q9=makeQuery(id+"F25.imprint","IMPRINT",FACE,{"disambiguationData":[TD([[makeQuery(id+"F25.imprint","IMPRINT",EDGE,{"disambiguationData":[TD([[subQ2,-1.0]])],"derivedFrom":subQ1}),-1.0]])]});}
            var Q10;
            {var subQ0=sQuery(id+"F25.wireOp",EDGE,"E268.trimOffspring");var subQ1=sQuery(id+"F25.wireOp",EDGE,"E245.left");var subQ2=makeQuery(id+"F25.imprint","INTERSECT",VERTEX,{"derivedFrom":[subQ1,subQ0]});Q10=makeQuery(id+"F25.imprint","IMPRINT",FACE,{"disambiguationData":[TD([[makeQuery(id+"F25.imprint","IMPRINT",EDGE,{"disambiguationData":[TD([[subQ2,-1.0]])],"derivedFrom":subQ1}),-1.0]])]});}
            var Q11;
            {var subQ0=sQuery(id+"F25.wireOp",EDGE,"E268.trimOffspring");var subQ1=sQuery(id+"F25.wireOp",EDGE,"E244.right");var subQ2=makeQuery(id+"F25.imprint","INTERSECT",VERTEX,{"derivedFrom":[subQ1,subQ0]});Q11=makeQuery(id+"F25.imprint","IMPRINT",FACE,{"disambiguationData":[TD([[makeQuery(id+"F25.imprint","IMPRINT",EDGE,{"disambiguationData":[TD([[subQ2,-1.0]])],"derivedFrom":subQ1}),-1.0]])]});}
            var Q12;
            {var subQ0=sQuery(id+"F25.wireOp",EDGE,"E268.trimOffspring");var subQ1=sQuery(id+"F25.wireOp",EDGE,"E243.left");var subQ2=makeQuery(id+"F25.imprint","INTERSECT",VERTEX,{"derivedFrom":[subQ1,subQ0]});Q12=makeQuery(id+"F25.imprint","IMPRINT",FACE,{"disambiguationData":[TD([[makeQuery(id+"F25.imprint","IMPRINT",EDGE,{"disambiguationData":[TD([[subQ2,-1.0]])],"derivedFrom":subQ1}),-1.0]])]});}
            var Q13;
            {var subQ0=sQuery(id+"F25.wireOp",EDGE,"E269.trimOffspring");var subQ1=sQuery(id+"F25.wireOp",EDGE,"E243.right");var subQ2=makeQuery(id+"F25.imprint","INTERSECT",VERTEX,{"derivedFrom":[subQ1,subQ0]});Q13=makeQuery(id+"F25.imprint","IMPRINT",FACE,{"disambiguationData":[TD([[makeQuery(id+"F25.imprint","IMPRINT",EDGE,{"disambiguationData":[TD([[subQ2,1.0]])],"derivedFrom":subQ1}),-1.0]])]});}
            var Q14;
            {var subQ0=sQuery(id+"F25.wireOp",EDGE,"E267.trimOffspring");var subQ1=sQuery(id+"F25.wireOp",EDGE,"E243.right");var subQ2=makeQuery(id+"F25.imprint","INTERSECT",VERTEX,{"derivedFrom":[subQ1,subQ0]});Q14=makeQuery(id+"F25.imprint","IMPRINT",FACE,{"disambiguationData":[TD([[makeQuery(id+"F25.imprint","IMPRINT",EDGE,{"disambiguationData":[TD([[subQ2,-1.0]])],"derivedFrom":subQ1}),-1.0]])]});}
            var Q15;
            {var subQ0=sQuery(id+"F25.wireOp",EDGE,"E243.bottom");Q15=makeQuery(id+"F25.imprint","IMPRINT",FACE,{"disambiguationData":[TD([[makeQuery(id+"F25.imprint","IMPRINT",EDGE,{"derivedFrom":subQ0}),-1.0]])]});}
            var Q16;
            {var subQ0=sQuery(id+"F25.wireOp",EDGE,"E533.trimOffspring");var subQ1=sQuery(id+"F25.wireOp",EDGE,"E517.trimOffspring");var subQ2=makeQuery(id+"F25.imprint","INTERSECT",VERTEX,{"derivedFrom":[subQ1,subQ0]});Q16=makeQuery(id+"F25.imprint","IMPRINT",FACE,{"disambiguationData":[TD([[makeQuery(id+"F25.imprint","IMPRINT",EDGE,{"disambiguationData":[TD([[subQ2,1.0]])],"derivedFrom":subQ1}),1.0]])]});}
            var Q17;
            {var subQ0=sQuery(id+"F25.wireOp",EDGE,"E532.trimOffspring");var subQ1=sQuery(id+"F25.wireOp",EDGE,"E517.trimOffspring");var subQ2=makeQuery(id+"F25.imprint","INTERSECT",VERTEX,{"derivedFrom":[subQ1,subQ0]});Q17=makeQuery(id+"F25.imprint","IMPRINT",FACE,{"disambiguationData":[TD([[makeQuery(id+"F25.imprint","IMPRINT",EDGE,{"disambiguationData":[TD([[subQ2,-1.0]])],"derivedFrom":subQ1}),1.0]])]});}
            var Q18;
            {var subQ0=sQuery(id+"F25.wireOp",EDGE,"E532.trimOffspring");var subQ1=sQuery(id+"F25.wireOp",EDGE,"E518.trimOffspring");var subQ2=makeQuery(id+"F25.imprint","INTERSECT",VERTEX,{"derivedFrom":[subQ1,subQ0]});Q18=makeQuery(id+"F25.imprint","IMPRINT",FACE,{"disambiguationData":[TD([[makeQuery(id+"F25.imprint","IMPRINT",EDGE,{"disambiguationData":[TD([[subQ2,-1.0]])],"derivedFrom":subQ1}),-1.0]])]});}
            var Q19;
            {var subQ0=sQuery(id+"F25.wireOp",EDGE,"E532.trimOffspring");var subQ1=sQuery(id+"F25.wireOp",EDGE,"E507.trimOffspring");var subQ2=makeQuery(id+"F25.imprint","INTERSECT",VERTEX,{"derivedFrom":[subQ1,subQ0]});Q19=makeQuery(id+"F25.imprint","IMPRINT",FACE,{"disambiguationData":[TD([[makeQuery(id+"F25.imprint","IMPRINT",EDGE,{"disambiguationData":[TD([[subQ2,-1.0]])],"derivedFrom":subQ1}),-1.0]])]});}
            var Q20;
            {var subQ0=sQuery(id+"F25.wireOp",EDGE,"E532.trimOffspring");var subQ1=sQuery(id+"F25.wireOp",EDGE,"E517.trimOffspring");var subQ2=makeQuery(id+"F25.imprint","INTERSECT",VERTEX,{"derivedFrom":[subQ1,subQ0]});Q20=makeQuery(id+"F25.imprint","IMPRINT",FACE,{"disambiguationData":[TD([[makeQuery(id+"F25.imprint","IMPRINT",EDGE,{"disambiguationData":[TD([[subQ2,-1.0]])],"derivedFrom":subQ1}),1.0]])]});}
            var Q21;
            {var subQ0=sQuery(id+"F25.wireOp",EDGE,"E518.trimOffspring");var subQ1=sQuery(id+"F25.wireOp",EDGE,"E247.left");var subQ2=makeQuery(id+"F25.imprint","INTERSECT",VERTEX,{"derivedFrom":[subQ1,subQ0]});Q21=makeQuery(id+"F25.imprint","IMPRINT",FACE,{"disambiguationData":[TD([[makeQuery(id+"F25.imprint","IMPRINT",EDGE,{"disambiguationData":[TD([[subQ2,1.0]])],"derivedFrom":subQ0}),-1.0]])]});}
            var Q22;
            {var subQ0=sQuery(id+"F25.wireOp",EDGE,"E534.MirrorCS");var subQ1=sQuery(id+"F25.wireOp",EDGE,"E518.trimOffspring");var subQ2=makeQuery(id+"F25.imprint","INTERSECT",VERTEX,{"derivedFrom":[subQ1,subQ0]});Q22=makeQuery(id+"F25.imprint","IMPRINT",FACE,{"disambiguationData":[TD([[makeQuery(id+"F25.imprint","IMPRINT",EDGE,{"disambiguationData":[TD([[subQ2,1.0]])],"derivedFrom":subQ1}),-1.0]])]});}
            var Q23;
            {var subQ0=sQuery(id+"F25.wireOp",EDGE,"E527.trimOffspring");var subQ1=sQuery(id+"F25.wireOp",EDGE,"E518.trimOffspring");var subQ2=makeQuery(id+"F25.imprint","INTERSECT",VERTEX,{"derivedFrom":[subQ1,subQ0]});Q23=makeQuery(id+"F25.imprint","IMPRINT",FACE,{"disambiguationData":[TD([[makeQuery(id+"F25.imprint","IMPRINT",EDGE,{"disambiguationData":[TD([[subQ2,-1.0]])],"derivedFrom":subQ1}),-1.0]])]});}
            var Q24;
            {var subQ0=sQuery(id+"F25.wireOp",EDGE,"E532.trimOffspring");var subQ1=sQuery(id+"F25.wireOp",EDGE,"E507.trimOffspring");var subQ2=makeQuery(id+"F25.imprint","INTERSECT",VERTEX,{"derivedFrom":[subQ1,subQ0]});Q24=makeQuery(id+"F25.imprint","IMPRINT",FACE,{"disambiguationData":[TD([[makeQuery(id+"F25.imprint","IMPRINT",EDGE,{"disambiguationData":[TD([[subQ2,-1.0]])],"derivedFrom":subQ1}),1.0]])]});}
            var Q25;
            {var subQ0=sQuery(id+"F25.wireOp",EDGE,"E527.trimOffspring");var subQ1=sQuery(id+"F25.wireOp",EDGE,"E507.trimOffspring");var subQ2=makeQuery(id+"F25.imprint","INTERSECT",VERTEX,{"derivedFrom":[subQ1,subQ0]});Q25=makeQuery(id+"F25.imprint","IMPRINT",FACE,{"disambiguationData":[TD([[makeQuery(id+"F25.imprint","IMPRINT",EDGE,{"disambiguationData":[TD([[subQ2,-1.0]])],"derivedFrom":subQ1}),1.0]])]});}
            var Q26;
            {var subQ0=sQuery(id+"F25.wireOp",EDGE,"E535.trimOffspring");var subQ1=sQuery(id+"F25.wireOp",EDGE,"E507.trimOffspring");var subQ2=makeQuery(id+"F25.imprint","INTERSECT",VERTEX,{"derivedFrom":[subQ1,subQ0]});Q26=makeQuery(id+"F25.imprint","IMPRINT",FACE,{"disambiguationData":[TD([[makeQuery(id+"F25.imprint","IMPRINT",EDGE,{"disambiguationData":[TD([[subQ2,1.0]])],"derivedFrom":subQ1}),1.0]])]});}
            var Q27;
            {var subQ0=sQuery(id+"F25.wireOp",EDGE,"E527.trimOffspring");var subQ1=sQuery(id+"F25.wireOp",EDGE,"E507.trimOffspring");var subQ2=makeQuery(id+"F25.imprint","INTERSECT",VERTEX,{"derivedFrom":[subQ1,subQ0]});Q27=makeQuery(id+"F25.imprint","IMPRINT",FACE,{"disambiguationData":[TD([[makeQuery(id+"F25.imprint","IMPRINT",EDGE,{"disambiguationData":[TD([[subQ2,-1.0]])],"derivedFrom":subQ1}),-1.0]])]});}
            var Q28;
            {var subQ0=sQuery(id+"F25.wireOp",EDGE,"E520.trimOffspring");var subQ1=sQuery(id+"F25.wireOp",EDGE,"E507.trimOffspring");var subQ2=makeQuery(id+"F25.imprint","INTERSECT",VERTEX,{"derivedFrom":[subQ1,subQ0]});Q28=makeQuery(id+"F25.imprint","IMPRINT",FACE,{"disambiguationData":[TD([[makeQuery(id+"F25.imprint","IMPRINT",EDGE,{"disambiguationData":[TD([[subQ2,1.0]])],"derivedFrom":subQ1}),1.0]])]});}
            var Q29;
            {var subQ0=sQuery(id+"F25.wireOp",EDGE,"E523.trimOffspring");var subQ1=sQuery(id+"F25.wireOp",EDGE,"E507.trimOffspring");var subQ2=makeQuery(id+"F25.imprint","INTERSECT",VERTEX,{"derivedFrom":[subQ1,subQ0]});Q29=makeQuery(id+"F25.imprint","IMPRINT",FACE,{"disambiguationData":[TD([[makeQuery(id+"F25.imprint","IMPRINT",EDGE,{"disambiguationData":[TD([[subQ2,1.0]])],"derivedFrom":subQ1}),1.0]])]});}
            var Q30;
            {var subQ0=sQuery(id+"F25.wireOp",EDGE,"E532.trimOffspring");var subQ1=sQuery(id+"F25.wireOp",EDGE,"E510.trimOffspring");var subQ2=makeQuery(id+"F25.imprint","INTERSECT",VERTEX,{"derivedFrom":[subQ1,subQ0]});Q30=makeQuery(id+"F25.imprint","IMPRINT",FACE,{"disambiguationData":[TD([[makeQuery(id+"F25.imprint","IMPRINT",EDGE,{"disambiguationData":[TD([[subQ2,-1.0]])],"derivedFrom":subQ1}),-1.0]])]});}
            var Q31;
            {var subQ0=sQuery(id+"F25.wireOp",EDGE,"E527.trimOffspring");var subQ1=sQuery(id+"F25.wireOp",EDGE,"E510.trimOffspring");var subQ2=makeQuery(id+"F25.imprint","INTERSECT",VERTEX,{"derivedFrom":[subQ1,subQ0]});Q31=makeQuery(id+"F25.imprint","IMPRINT",FACE,{"disambiguationData":[TD([[makeQuery(id+"F25.imprint","IMPRINT",EDGE,{"disambiguationData":[TD([[subQ2,-1.0]])],"derivedFrom":subQ1}),-1.0]])]});}
            var Q32;
            {var subQ0=sQuery(id+"F25.wireOp",EDGE,"E533.trimOffspring");var subQ1=sQuery(id+"F25.wireOp",EDGE,"E510.trimOffspring");var subQ2=makeQuery(id+"F25.imprint","INTERSECT",VERTEX,{"derivedFrom":[subQ1,subQ0]});Q32=makeQuery(id+"F25.imprint","IMPRINT",FACE,{"disambiguationData":[TD([[makeQuery(id+"F25.imprint","IMPRINT",EDGE,{"disambiguationData":[TD([[subQ2,-1.0]])],"derivedFrom":subQ1}),-1.0]])]});}
            var Q33;
            {var subQ0=sQuery(id+"F25.wireOp",EDGE,"E532.trimOffspring");var subQ1=sQuery(id+"F25.wireOp",EDGE,"E510.trimOffspring");var subQ2=makeQuery(id+"F25.imprint","INTERSECT",VERTEX,{"derivedFrom":[subQ1,subQ0]});Q33=makeQuery(id+"F25.imprint","IMPRINT",FACE,{"disambiguationData":[TD([[makeQuery(id+"F25.imprint","IMPRINT",EDGE,{"disambiguationData":[TD([[subQ2,-1.0]])],"derivedFrom":subQ1}),-1.0]])]});}
            var Q34;
            {var subQ0=sQuery(id+"F25.wireOp",EDGE,"E535.trimOffspring");var subQ1=sQuery(id+"F25.wireOp",EDGE,"E510.trimOffspring");var subQ2=makeQuery(id+"F25.imprint","INTERSECT",VERTEX,{"derivedFrom":[subQ1,subQ0]});Q34=makeQuery(id+"F25.imprint","IMPRINT",FACE,{"disambiguationData":[TD([[makeQuery(id+"F25.imprint","IMPRINT",EDGE,{"disambiguationData":[TD([[subQ2,-1.0]])],"derivedFrom":subQ1}),-1.0]])]});}
            var Q35;
            {var subQ0=sQuery(id+"F25.wireOp",EDGE,"E520.trimOffspring");var subQ1=sQuery(id+"F25.wireOp",EDGE,"E510.trimOffspring");var subQ2=makeQuery(id+"F25.imprint","INTERSECT",VERTEX,{"derivedFrom":[subQ1,subQ0]});Q35=makeQuery(id+"F25.imprint","IMPRINT",FACE,{"disambiguationData":[TD([[makeQuery(id+"F25.imprint","IMPRINT",EDGE,{"disambiguationData":[TD([[subQ2,-1.0]])],"derivedFrom":subQ1}),-1.0]])]});}
            var Q36;
            {var subQ0=sQuery(id+"F25.wireOp",EDGE,"E518.trimOffspring");var subQ5=sQuery(id+"F25.wireOp",EDGE,"E248.right");var subQ7=makeQuery(id+"F25.imprint","INTERSECT",VERTEX,{"derivedFrom":[subQ5,subQ0]});Q36=makeQuery(id+"F25.imprint","IMPRINT",FACE,{"disambiguationData":[TD([[makeQuery(id+"F25.imprint","IMPRINT",EDGE,{"disambiguationData":[TD([[subQ7,1.0]])],"derivedFrom":subQ5}),1.0]])]});}
            var Q37;
            {var subQ3=sQuery(id+"F25.wireOp",EDGE,"E517.trimOffspring");var subQ5=sQuery(id+"F25.wireOp",EDGE,"E248.right");var subQ6=makeQuery(id+"F25.imprint","INTERSECT",VERTEX,{"derivedFrom":[subQ5,subQ3]});Q37=makeQuery(id+"F25.imprint","IMPRINT",FACE,{"disambiguationData":[TD([[makeQuery(id+"F25.imprint","IMPRINT",EDGE,{"disambiguationData":[TD([[subQ6,-1.0]])],"derivedFrom":subQ5}),1.0]])]});}
            var Q38;
            {var subQ0=sQuery(id+"F25.wireOp",EDGE,"E275.trimOffspring");var subQ1=sQuery(id+"F25.wireOp",EDGE,"E248.left");var subQ2=makeQuery(id+"F25.imprint","INTERSECT",VERTEX,{"derivedFrom":[subQ1,subQ0]});Q38=makeQuery(id+"F25.imprint","IMPRINT",FACE,{"disambiguationData":[TD([[makeQuery(id+"F25.imprint","IMPRINT",EDGE,{"disambiguationData":[TD([[subQ2,-1.0]])],"derivedFrom":subQ1}),-1.0]])]});}
            var Q39;
            {var subQ0=sQuery(id+"F25.wireOp",EDGE,"E273.trimOffspring");var subQ1=sQuery(id+"F25.wireOp",EDGE,"E248.left");var subQ2=makeQuery(id+"F25.imprint","INTERSECT",VERTEX,{"derivedFrom":[subQ1,subQ0]});Q39=makeQuery(id+"F25.imprint","IMPRINT",FACE,{"disambiguationData":[TD([[makeQuery(id+"F25.imprint","IMPRINT",EDGE,{"disambiguationData":[TD([[subQ2,-1.0]])],"derivedFrom":subQ1}),-1.0]])]});}
            var Q40;
            {var subQ0=sQuery(id+"F25.wireOp",EDGE,"E272.trimOffspring");var subQ1=sQuery(id+"F25.wireOp",EDGE,"E248.left");var subQ2=makeQuery(id+"F25.imprint","INTERSECT",VERTEX,{"derivedFrom":[subQ1,subQ0]});Q40=makeQuery(id+"F25.imprint","IMPRINT",FACE,{"disambiguationData":[TD([[makeQuery(id+"F25.imprint","IMPRINT",EDGE,{"disambiguationData":[TD([[subQ2,-1.0]])],"derivedFrom":subQ1}),-1.0]])]});}
            var Q41;
            {var subQ0=sQuery(id+"F25.wireOp",EDGE,"E272.trimOffspring");var subQ1=sQuery(id+"F25.wireOp",EDGE,"E246.right");var subQ2=makeQuery(id+"F25.imprint","INTERSECT",VERTEX,{"derivedFrom":[subQ1,subQ0]});Q41=makeQuery(id+"F25.imprint","IMPRINT",FACE,{"disambiguationData":[TD([[makeQuery(id+"F25.imprint","IMPRINT",EDGE,{"disambiguationData":[TD([[subQ2,-1.0]])],"derivedFrom":subQ1}),-1.0]])]});}
            var Q42;
            {var subQ0=sQuery(id+"F25.wireOp",EDGE,"E272.trimOffspring");var subQ1=sQuery(id+"F25.wireOp",EDGE,"E245.left");var subQ2=makeQuery(id+"F25.imprint","INTERSECT",VERTEX,{"derivedFrom":[subQ1,subQ0]});Q42=makeQuery(id+"F25.imprint","IMPRINT",FACE,{"disambiguationData":[TD([[makeQuery(id+"F25.imprint","IMPRINT",EDGE,{"disambiguationData":[TD([[subQ2,-1.0]])],"derivedFrom":subQ1}),-1.0]])]});}
            var Q43;
            {var subQ0=sQuery(id+"F25.wireOp",EDGE,"E273.trimOffspring");var subQ1=sQuery(id+"F25.wireOp",EDGE,"E245.right");var subQ2=makeQuery(id+"F25.imprint","INTERSECT",VERTEX,{"derivedFrom":[subQ1,subQ0]});Q43=makeQuery(id+"F25.imprint","IMPRINT",FACE,{"disambiguationData":[TD([[makeQuery(id+"F25.imprint","IMPRINT",EDGE,{"disambiguationData":[TD([[subQ2,1.0]])],"derivedFrom":subQ1}),-1.0]])]});}
            var Q44;
            {var subQ0=sQuery(id+"F25.wireOp",EDGE,"E272.trimOffspring");var subQ1=sQuery(id+"F25.wireOp",EDGE,"E244.right");var subQ2=makeQuery(id+"F25.imprint","INTERSECT",VERTEX,{"derivedFrom":[subQ1,subQ0]});Q44=makeQuery(id+"F25.imprint","IMPRINT",FACE,{"disambiguationData":[TD([[makeQuery(id+"F25.imprint","IMPRINT",EDGE,{"disambiguationData":[TD([[subQ2,-1.0]])],"derivedFrom":subQ1}),-1.0]])]});}
            var Q45;
            {var subQ0=sQuery(id+"F25.wireOp",EDGE,"E272.trimOffspring");var subQ1=sQuery(id+"F25.wireOp",EDGE,"E243.left");var subQ2=makeQuery(id+"F25.imprint","INTERSECT",VERTEX,{"derivedFrom":[subQ1,subQ0]});Q45=makeQuery(id+"F25.imprint","IMPRINT",FACE,{"disambiguationData":[TD([[makeQuery(id+"F25.imprint","IMPRINT",EDGE,{"disambiguationData":[TD([[subQ2,-1.0]])],"derivedFrom":subQ1}),-1.0]])]});}
            var Q46;
            {var subQ0=sQuery(id+"F25.wireOp",EDGE,"E271.trimOffspring");var subQ1=sQuery(id+"F25.wireOp",EDGE,"E243.left");var subQ2=makeQuery(id+"F25.imprint","INTERSECT",VERTEX,{"derivedFrom":[subQ1,subQ0]});Q46=makeQuery(id+"F25.imprint","IMPRINT",FACE,{"disambiguationData":[TD([[makeQuery(id+"F25.imprint","IMPRINT",EDGE,{"disambiguationData":[TD([[subQ2,-1.0]])],"derivedFrom":subQ1}),-1.0]])]});}
            var Q47;
            {var subQ0=sQuery(id+"F25.wireOp",EDGE,"E270.trimOffspring");var subQ1=sQuery(id+"F25.wireOp",EDGE,"E243.left");var subQ2=makeQuery(id+"F25.imprint","INTERSECT",VERTEX,{"derivedFrom":[subQ1,subQ0]});Q47=makeQuery(id+"F25.imprint","IMPRINT",FACE,{"disambiguationData":[TD([[makeQuery(id+"F25.imprint","IMPRINT",EDGE,{"disambiguationData":[TD([[subQ2,-1.0]])],"derivedFrom":subQ1}),-1.0]])]});}
            var Q48;
            {var subQ0=sQuery(id+"F25.wireOp",EDGE,"E274.trimOffspring");var subQ1=sQuery(id+"F25.wireOp",EDGE,"E243.left");var subQ2=makeQuery(id+"F25.imprint","INTERSECT",VERTEX,{"derivedFrom":[subQ1,subQ0]});Q48=makeQuery(id+"F25.imprint","IMPRINT",FACE,{"disambiguationData":[TD([[makeQuery(id+"F25.imprint","IMPRINT",EDGE,{"disambiguationData":[TD([[subQ2,-1.0]])],"derivedFrom":subQ1}),-1.0]])]});}
            var Q49;
            {var subQ0=sQuery(id+"F25.wireOp",EDGE,"E269.trimOffspring");var subQ1=sQuery(id+"F25.wireOp",EDGE,"E243.left");var subQ2=makeQuery(id+"F25.imprint","INTERSECT",VERTEX,{"derivedFrom":[subQ1,subQ0]});Q49=makeQuery(id+"F25.imprint","IMPRINT",FACE,{"disambiguationData":[TD([[makeQuery(id+"F25.imprint","IMPRINT",EDGE,{"disambiguationData":[TD([[subQ2,-1.0]])],"derivedFrom":subQ1}),-1.0]])]});}
            var Q50;
            {var subQ0=sQuery(id+"F25.wireOp",EDGE,"E274.trimOffspring");var subQ1=sQuery(id+"F25.wireOp",EDGE,"E244.right");var subQ2=makeQuery(id+"F25.imprint","INTERSECT",VERTEX,{"derivedFrom":[subQ1,subQ0]});Q50=makeQuery(id+"F25.imprint","IMPRINT",FACE,{"disambiguationData":[TD([[makeQuery(id+"F25.imprint","IMPRINT",EDGE,{"disambiguationData":[TD([[subQ2,-1.0]])],"derivedFrom":subQ1}),-1.0]])]});}
            var Q51;
            {var subQ0=sQuery(id+"F25.wireOp",EDGE,"E270.trimOffspring");var subQ1=sQuery(id+"F25.wireOp",EDGE,"E244.right");var subQ2=makeQuery(id+"F25.imprint","INTERSECT",VERTEX,{"derivedFrom":[subQ1,subQ0]});Q51=makeQuery(id+"F25.imprint","IMPRINT",FACE,{"disambiguationData":[TD([[makeQuery(id+"F25.imprint","IMPRINT",EDGE,{"disambiguationData":[TD([[subQ2,-1.0]])],"derivedFrom":subQ1}),-1.0]])]});}
            var Q52;
            {var subQ0=sQuery(id+"F25.wireOp",EDGE,"E274.trimOffspring");var subQ1=sQuery(id+"F25.wireOp",EDGE,"E245.right");var subQ2=makeQuery(id+"F25.imprint","INTERSECT",VERTEX,{"derivedFrom":[subQ1,subQ0]});Q52=makeQuery(id+"F25.imprint","IMPRINT",FACE,{"disambiguationData":[TD([[makeQuery(id+"F25.imprint","IMPRINT",EDGE,{"disambiguationData":[TD([[subQ2,-1.0]])],"derivedFrom":subQ1}),-1.0]])]});}
            var Q53;
            {var subQ0=sQuery(id+"F25.wireOp",EDGE,"E270.trimOffspring");var subQ1=sQuery(id+"F25.wireOp",EDGE,"E245.right");var subQ2=makeQuery(id+"F25.imprint","INTERSECT",VERTEX,{"derivedFrom":[subQ1,subQ0]});Q53=makeQuery(id+"F25.imprint","IMPRINT",FACE,{"disambiguationData":[TD([[makeQuery(id+"F25.imprint","IMPRINT",EDGE,{"disambiguationData":[TD([[subQ2,-1.0]])],"derivedFrom":subQ1}),-1.0]])]});}
            var Q54;
            {var subQ0=sQuery(id+"F25.wireOp",EDGE,"E274.trimOffspring");var subQ1=sQuery(id+"F25.wireOp",EDGE,"E245.left");var subQ2=makeQuery(id+"F25.imprint","INTERSECT",VERTEX,{"derivedFrom":[subQ1,subQ0]});Q54=makeQuery(id+"F25.imprint","IMPRINT",FACE,{"disambiguationData":[TD([[makeQuery(id+"F25.imprint","IMPRINT",EDGE,{"disambiguationData":[TD([[subQ2,-1.0]])],"derivedFrom":subQ1}),-1.0]])]});}
            var Q55;
            {var subQ0=sQuery(id+"F25.wireOp",EDGE,"E270.trimOffspring");var subQ1=sQuery(id+"F25.wireOp",EDGE,"E245.left");var subQ2=makeQuery(id+"F25.imprint","INTERSECT",VERTEX,{"derivedFrom":[subQ1,subQ0]});Q55=makeQuery(id+"F25.imprint","IMPRINT",FACE,{"disambiguationData":[TD([[makeQuery(id+"F25.imprint","IMPRINT",EDGE,{"disambiguationData":[TD([[subQ2,-1.0]])],"derivedFrom":subQ1}),-1.0]])]});}
            var Q56;
            {var subQ0=sQuery(id+"F25.wireOp",EDGE,"E274.trimOffspring");var subQ1=sQuery(id+"F25.wireOp",EDGE,"E246.right");var subQ2=makeQuery(id+"F25.imprint","INTERSECT",VERTEX,{"derivedFrom":[subQ1,subQ0]});Q56=makeQuery(id+"F25.imprint","IMPRINT",FACE,{"disambiguationData":[TD([[makeQuery(id+"F25.imprint","IMPRINT",EDGE,{"disambiguationData":[TD([[subQ2,-1.0]])],"derivedFrom":subQ1}),-1.0]])]});}
            var Q57;
            {var subQ0=sQuery(id+"F25.wireOp",EDGE,"E270.trimOffspring");var subQ1=sQuery(id+"F25.wireOp",EDGE,"E246.right");var subQ2=makeQuery(id+"F25.imprint","INTERSECT",VERTEX,{"derivedFrom":[subQ1,subQ0]});Q57=makeQuery(id+"F25.imprint","IMPRINT",FACE,{"disambiguationData":[TD([[makeQuery(id+"F25.imprint","IMPRINT",EDGE,{"disambiguationData":[TD([[subQ2,-1.0]])],"derivedFrom":subQ1}),-1.0]])]});}
            var Q58;
            {var subQ0=sQuery(id+"F25.wireOp",EDGE,"E270.trimOffspring");var subQ1=sQuery(id+"F25.wireOp",EDGE,"E248.left");var subQ2=makeQuery(id+"F25.imprint","INTERSECT",VERTEX,{"derivedFrom":[subQ1,subQ0]});Q58=makeQuery(id+"F25.imprint","IMPRINT",FACE,{"disambiguationData":[TD([[makeQuery(id+"F25.imprint","IMPRINT",EDGE,{"disambiguationData":[TD([[subQ2,-1.0]])],"derivedFrom":subQ1}),-1.0]])]});}
            var Q59;
            {var subQ0=sQuery(id+"F25.wireOp",EDGE,"E274.trimOffspring");var subQ1=sQuery(id+"F25.wireOp",EDGE,"E248.left");var subQ2=makeQuery(id+"F25.imprint","INTERSECT",VERTEX,{"derivedFrom":[subQ1,subQ0]});Q59=makeQuery(id+"F25.imprint","IMPRINT",FACE,{"disambiguationData":[TD([[makeQuery(id+"F25.imprint","IMPRINT",EDGE,{"disambiguationData":[TD([[subQ2,-1.0]])],"derivedFrom":subQ1}),-1.0]])]});}
            var Q60;
            {var subQ0=sQuery(id+"F25.wireOp",EDGE,"E244.bottom");Q60=makeQuery(id+"F25.imprint","IMPRINT",FACE,{"disambiguationData":[TD([[makeQuery(id+"F25.imprint","IMPRINT",EDGE,{"derivedFrom":subQ0}),1.0]])]});}
            var Q61;
            {var subQ0=sQuery(id+"F25.wireOp",EDGE,"E267.trimOffspring");var subQ1=sQuery(id+"F25.wireOp",EDGE,"E243.left");var subQ2=makeQuery(id+"F25.imprint","INTERSECT",VERTEX,{"derivedFrom":[subQ1,subQ0]});Q61=makeQuery(id+"F25.imprint","IMPRINT",FACE,{"disambiguationData":[TD([[makeQuery(id+"F25.imprint","IMPRINT",EDGE,{"disambiguationData":[TD([[subQ2,-1.0]])],"derivedFrom":subQ1}),-1.0]])]});}
            var Q62;
            {var subQ0=sQuery(id+"F25.wireOp",EDGE,"E267.trimOffspring");var subQ1=sQuery(id+"F25.wireOp",EDGE,"E244.right");var subQ2=makeQuery(id+"F25.imprint","INTERSECT",VERTEX,{"derivedFrom":[subQ1,subQ0]});Q62=makeQuery(id+"F25.imprint","IMPRINT",FACE,{"disambiguationData":[TD([[makeQuery(id+"F25.imprint","IMPRINT",EDGE,{"disambiguationData":[TD([[subQ2,-1.0]])],"derivedFrom":subQ1}),-1.0]])]});}
            var Q63;
            {var subQ0=sQuery(id+"F25.wireOp",EDGE,"E267.trimOffspring");var subQ1=sQuery(id+"F25.wireOp",EDGE,"E245.right");var subQ2=makeQuery(id+"F25.imprint","INTERSECT",VERTEX,{"derivedFrom":[subQ1,subQ0]});Q63=makeQuery(id+"F25.imprint","IMPRINT",FACE,{"disambiguationData":[TD([[makeQuery(id+"F25.imprint","IMPRINT",EDGE,{"disambiguationData":[TD([[subQ2,-1.0]])],"derivedFrom":subQ1}),-1.0]])]});}
            var Q64;
            {var subQ0=sQuery(id+"F25.wireOp",EDGE,"E267.trimOffspring");var subQ1=sQuery(id+"F25.wireOp",EDGE,"E245.left");var subQ2=makeQuery(id+"F25.imprint","INTERSECT",VERTEX,{"derivedFrom":[subQ1,subQ0]});Q64=makeQuery(id+"F25.imprint","IMPRINT",FACE,{"disambiguationData":[TD([[makeQuery(id+"F25.imprint","IMPRINT",EDGE,{"disambiguationData":[TD([[subQ2,-1.0]])],"derivedFrom":subQ1}),-1.0]])]});}
            var Q65;
            {var subQ0=sQuery(id+"F25.wireOp",EDGE,"E267.trimOffspring");var subQ1=sQuery(id+"F25.wireOp",EDGE,"E246.right");var subQ2=makeQuery(id+"F25.imprint","INTERSECT",VERTEX,{"derivedFrom":[subQ1,subQ0]});Q65=makeQuery(id+"F25.imprint","IMPRINT",FACE,{"disambiguationData":[TD([[makeQuery(id+"F25.imprint","IMPRINT",EDGE,{"disambiguationData":[TD([[subQ2,-1.0]])],"derivedFrom":subQ1}),-1.0]])]});}
            var Q66;
            {var subQ0=sQuery(id+"F25.wireOp",EDGE,"E267.trimOffspring");var subQ1=sQuery(id+"F25.wireOp",EDGE,"E248.left");var subQ2=makeQuery(id+"F25.imprint","INTERSECT",VERTEX,{"derivedFrom":[subQ1,subQ0]});Q66=makeQuery(id+"F25.imprint","IMPRINT",FACE,{"disambiguationData":[TD([[makeQuery(id+"F25.imprint","IMPRINT",EDGE,{"disambiguationData":[TD([[subQ2,-1.0]])],"derivedFrom":subQ1}),1.0]])]});}
            var Q67;
            {var subQ0=sQuery(id+"F25.wireOp",EDGE,"E267.trimOffspring");var subQ1=sQuery(id+"F25.wireOp",EDGE,"E248.left");var subQ2=makeQuery(id+"F25.imprint","INTERSECT",VERTEX,{"derivedFrom":[subQ1,subQ0]});Q67=makeQuery(id+"F25.imprint","IMPRINT",FACE,{"disambiguationData":[TD([[makeQuery(id+"F25.imprint","IMPRINT",EDGE,{"disambiguationData":[TD([[subQ2,-1.0]])],"derivedFrom":subQ1}),-1.0]])]});}
            var Q68;
            {var subQ0=sQuery(id+"F25.wireOp",EDGE,"E268.trimOffspring");var subQ1=sQuery(id+"F25.wireOp",EDGE,"E248.left");var subQ2=makeQuery(id+"F25.imprint","INTERSECT",VERTEX,{"derivedFrom":[subQ1,subQ0]});Q68=makeQuery(id+"F25.imprint","IMPRINT",FACE,{"disambiguationData":[TD([[makeQuery(id+"F25.imprint","IMPRINT",EDGE,{"disambiguationData":[TD([[subQ2,-1.0]])],"derivedFrom":subQ1}),-1.0]])]});}
            var Q69;
            {var subQ0=sQuery(id+"F25.wireOp",EDGE,"E535.trimOffspring");var subQ1=sQuery(id+"F25.wireOp",EDGE,"E510.trimOffspring");var subQ2=makeQuery(id+"F25.imprint","INTERSECT",VERTEX,{"derivedFrom":[subQ1,subQ0]});Q69=makeQuery(id+"F25.imprint","IMPRINT",FACE,{"disambiguationData":[TD([[makeQuery(id+"F25.imprint","IMPRINT",EDGE,{"disambiguationData":[TD([[subQ2,-1.0]])],"derivedFrom":subQ1}),1.0]])]});}
            var Q70;
            {var subQ0=sQuery(id+"F25.wireOp",EDGE,"E520.trimOffspring");var subQ1=sQuery(id+"F25.wireOp",EDGE,"E510.trimOffspring");var subQ2=makeQuery(id+"F25.imprint","INTERSECT",VERTEX,{"derivedFrom":[subQ1,subQ0]});Q70=makeQuery(id+"F25.imprint","IMPRINT",FACE,{"disambiguationData":[TD([[makeQuery(id+"F25.imprint","IMPRINT",EDGE,{"disambiguationData":[TD([[subQ2,-1.0]])],"derivedFrom":subQ1}),1.0]])]});}
            var Q71;
            {var subQ0=sQuery(id+"F25.wireOp",EDGE,"E535.trimOffspring");var subQ1=sQuery(id+"F25.wireOp",EDGE,"E522.trimOffspring");var subQ2=makeQuery(id+"F25.imprint","INTERSECT",VERTEX,{"derivedFrom":[subQ1,subQ0]});Q71=makeQuery(id+"F25.imprint","IMPRINT",FACE,{"disambiguationData":[TD([[makeQuery(id+"F25.imprint","IMPRINT",EDGE,{"disambiguationData":[TD([[subQ2,-1.0]])],"derivedFrom":subQ1}),1.0]])]});}
            var Q72;
            {var subQ1=sQuery(id+"F25.wireOp",EDGE,"E522.trimOffspring");var subQ3=sQuery(id+"F25.wireOp",EDGE,"E520.trimOffspring");var subQ4=makeQuery(id+"F25.imprint","INTERSECT",VERTEX,{"derivedFrom":[subQ1,subQ3]});Q72=makeQuery(id+"F25.imprint","IMPRINT",FACE,{"disambiguationData":[TD([[makeQuery(id+"F25.imprint","IMPRINT",EDGE,{"disambiguationData":[TD([[subQ4,-1.0]])],"derivedFrom":subQ3}),-1.0]])]});}
            var Q73;
            {var subQ0=sQuery(id+"F25.wireOp",EDGE,"E537.MirrorCS");var subQ1=sQuery(id+"F25.wireOp",EDGE,"E520.trimOffspring");var subQ2=makeQuery(id+"F25.imprint","INTERSECT",VERTEX,{"derivedFrom":[subQ1,subQ0]});Q73=makeQuery(id+"F25.imprint","IMPRINT",FACE,{"disambiguationData":[TD([[makeQuery(id+"F25.imprint","IMPRINT",EDGE,{"disambiguationData":[TD([[subQ2,1.0]])],"derivedFrom":subQ1}),1.0]])]});}
            var Q74;
            {var subQ0=sQuery(id+"F25.wireOp",EDGE,"E537.MirrorCS");var subQ1=sQuery(id+"F25.wireOp",EDGE,"E520.trimOffspring");var subQ2=makeQuery(id+"F25.imprint","INTERSECT",VERTEX,{"derivedFrom":[subQ1,subQ0]});Q74=makeQuery(id+"F25.imprint","IMPRINT",FACE,{"disambiguationData":[TD([[makeQuery(id+"F25.imprint","IMPRINT",EDGE,{"disambiguationData":[TD([[subQ2,1.0]])],"derivedFrom":subQ1}),-1.0]])]});}
            var Q75;
            {var subQ0=sQuery(id+"F25.wireOp",EDGE,"E522.trimOffspring");var subQ1=sQuery(id+"F25.wireOp",EDGE,"E276.trimOffspring");var subQ2=makeQuery(id+"F25.imprint","INTERSECT",VERTEX,{"derivedFrom":[subQ1,subQ0]});Q75=makeQuery(id+"F25.imprint","IMPRINT",FACE,{"disambiguationData":[TD([[makeQuery(id+"F25.imprint","IMPRINT",EDGE,{"disambiguationData":[TD([[subQ2,-1.0]])],"derivedFrom":subQ1}),1.0]])]});}
            var Q76;
            {var subQ0=sQuery(id+"F25.wireOp",EDGE,"E525.trimOffspring");var subQ1=sQuery(id+"F25.wireOp",EDGE,"E276.trimOffspring");var subQ2=makeQuery(id+"F25.imprint","INTERSECT",VERTEX,{"derivedFrom":[subQ1,subQ0]});Q76=makeQuery(id+"F25.imprint","IMPRINT",FACE,{"disambiguationData":[TD([[makeQuery(id+"F25.imprint","IMPRINT",EDGE,{"disambiguationData":[TD([[subQ2,1.0]])],"derivedFrom":subQ1}),1.0]])]});}
            var Q77;
            {var subQ0=sQuery(id+"F25.wireOp",EDGE,"E517.trimOffspring");var subQ1=sQuery(id+"F25.wireOp",EDGE,"E276.trimOffspring");var subQ2=makeQuery(id+"F25.imprint","INTERSECT",VERTEX,{"derivedFrom":[subQ1,subQ0]});Q77=makeQuery(id+"F25.imprint","IMPRINT",FACE,{"disambiguationData":[TD([[makeQuery(id+"F25.imprint","IMPRINT",EDGE,{"disambiguationData":[TD([[subQ2,-1.0]])],"derivedFrom":subQ1}),-1.0]])]});}
            var Q78;
            {var subQ0=sQuery(id+"F25.wireOp",EDGE,"E517.trimOffspring");var subQ1=sQuery(id+"F25.wireOp",EDGE,"E277.trimOffspring");var subQ2=makeQuery(id+"F25.imprint","INTERSECT",VERTEX,{"derivedFrom":[subQ1,subQ0]});Q78=makeQuery(id+"F25.imprint","IMPRINT",FACE,{"disambiguationData":[TD([[makeQuery(id+"F25.imprint","IMPRINT",EDGE,{"disambiguationData":[TD([[subQ2,-1.0]])],"derivedFrom":subQ1}),-1.0]])]});}
            var Q79;
            {var subQ0=sQuery(id+"F25.wireOp",EDGE,"E519.trimOffspring");var subQ1=sQuery(id+"F25.wireOp",EDGE,"E277.trimOffspring");var subQ2=makeQuery(id+"F25.imprint","INTERSECT",VERTEX,{"derivedFrom":[subQ1,subQ0]});Q79=makeQuery(id+"F25.imprint","IMPRINT",FACE,{"disambiguationData":[TD([[makeQuery(id+"F25.imprint","IMPRINT",EDGE,{"disambiguationData":[TD([[subQ2,-1.0]])],"derivedFrom":subQ1}),-1.0]])]});}
            var Q80;
            {var subQ0=sQuery(id+"F25.wireOp",EDGE,"E519.trimOffspring");var subQ1=sQuery(id+"F25.wireOp",EDGE,"E276.trimOffspring");var subQ2=makeQuery(id+"F25.imprint","INTERSECT",VERTEX,{"derivedFrom":[subQ1,subQ0]});Q80=makeQuery(id+"F25.imprint","IMPRINT",FACE,{"disambiguationData":[TD([[makeQuery(id+"F25.imprint","IMPRINT",EDGE,{"disambiguationData":[TD([[subQ2,-1.0]])],"derivedFrom":subQ1}),-1.0]])]});}
            var Q81;
            {var subQ0=sQuery(id+"F25.wireOp",EDGE,"E518.trimOffspring");var subQ1=sQuery(id+"F25.wireOp",EDGE,"E276.trimOffspring");var subQ2=makeQuery(id+"F25.imprint","INTERSECT",VERTEX,{"derivedFrom":[subQ1,subQ0]});Q81=makeQuery(id+"F25.imprint","IMPRINT",FACE,{"disambiguationData":[TD([[makeQuery(id+"F25.imprint","IMPRINT",EDGE,{"disambiguationData":[TD([[subQ2,-1.0]])],"derivedFrom":subQ1}),-1.0]])]});}
            var Q82;
            {var subQ0=sQuery(id+"F25.wireOp",EDGE,"E518.trimOffspring");var subQ1=sQuery(id+"F25.wireOp",EDGE,"E277.trimOffspring");var subQ2=makeQuery(id+"F25.imprint","INTERSECT",VERTEX,{"derivedFrom":[subQ1,subQ0]});Q82=makeQuery(id+"F25.imprint","IMPRINT",FACE,{"disambiguationData":[TD([[makeQuery(id+"F25.imprint","IMPRINT",EDGE,{"disambiguationData":[TD([[subQ2,-1.0]])],"derivedFrom":subQ1}),-1.0]])]});}
            var Q83;
            {var subQ0=sQuery(id+"F25.wireOp",EDGE,"E507.trimOffspring");var subQ1=sQuery(id+"F25.wireOp",EDGE,"E276.trimOffspring");var subQ2=makeQuery(id+"F25.imprint","INTERSECT",VERTEX,{"derivedFrom":[subQ1,subQ0]});Q83=makeQuery(id+"F25.imprint","IMPRINT",FACE,{"disambiguationData":[TD([[makeQuery(id+"F25.imprint","IMPRINT",EDGE,{"disambiguationData":[TD([[subQ2,-1.0]])],"derivedFrom":subQ1}),-1.0]])]});}
            var Q84;
            {var subQ0=sQuery(id+"F25.wireOp",EDGE,"E507.trimOffspring");var subQ1=sQuery(id+"F25.wireOp",EDGE,"E277.trimOffspring");var subQ2=makeQuery(id+"F25.imprint","INTERSECT",VERTEX,{"derivedFrom":[subQ1,subQ0]});Q84=makeQuery(id+"F25.imprint","IMPRINT",FACE,{"disambiguationData":[TD([[makeQuery(id+"F25.imprint","IMPRINT",EDGE,{"disambiguationData":[TD([[subQ2,-1.0]])],"derivedFrom":subQ1}),-1.0]])]});}
            var Q85;
            {var subQ0=sQuery(id+"F25.wireOp",EDGE,"E512.trimOffspring");var subQ1=sQuery(id+"F25.wireOp",EDGE,"E276.trimOffspring");var subQ2=makeQuery(id+"F25.imprint","INTERSECT",VERTEX,{"derivedFrom":[subQ1,subQ0]});Q85=makeQuery(id+"F25.imprint","IMPRINT",FACE,{"disambiguationData":[TD([[makeQuery(id+"F25.imprint","IMPRINT",EDGE,{"disambiguationData":[TD([[subQ2,-1.0]])],"derivedFrom":subQ1}),-1.0]])]});}
            var Q86;
            {var subQ0=sQuery(id+"F25.wireOp",EDGE,"E512.trimOffspring");var subQ1=sQuery(id+"F25.wireOp",EDGE,"E277.trimOffspring");var subQ2=makeQuery(id+"F25.imprint","INTERSECT",VERTEX,{"derivedFrom":[subQ1,subQ0]});Q86=makeQuery(id+"F25.imprint","IMPRINT",FACE,{"disambiguationData":[TD([[makeQuery(id+"F25.imprint","IMPRINT",EDGE,{"disambiguationData":[TD([[subQ2,-1.0]])],"derivedFrom":subQ1}),-1.0]])]});}
            var Q87;
            {var subQ0=sQuery(id+"F25.wireOp",EDGE,"E510.trimOffspring");var subQ1=sQuery(id+"F25.wireOp",EDGE,"E277.trimOffspring");var subQ2=makeQuery(id+"F25.imprint","INTERSECT",VERTEX,{"derivedFrom":[subQ1,subQ0]});Q87=makeQuery(id+"F25.imprint","IMPRINT",FACE,{"disambiguationData":[TD([[makeQuery(id+"F25.imprint","IMPRINT",EDGE,{"disambiguationData":[TD([[subQ2,-1.0]])],"derivedFrom":subQ1}),-1.0]])]});}
            var Q88;
            {var subQ0=sQuery(id+"F25.wireOp",EDGE,"E510.trimOffspring");var subQ1=sQuery(id+"F25.wireOp",EDGE,"E276.trimOffspring");var subQ2=makeQuery(id+"F25.imprint","INTERSECT",VERTEX,{"derivedFrom":[subQ1,subQ0]});Q88=makeQuery(id+"F25.imprint","IMPRINT",FACE,{"disambiguationData":[TD([[makeQuery(id+"F25.imprint","IMPRINT",EDGE,{"disambiguationData":[TD([[subQ2,-1.0]])],"derivedFrom":subQ1}),-1.0]])]});}
            var Q89;
            {var subQ0=sQuery(id+"F25.wireOp",EDGE,"E522.trimOffspring");var subQ1=sQuery(id+"F25.wireOp",EDGE,"E276.trimOffspring");var subQ2=makeQuery(id+"F25.imprint","INTERSECT",VERTEX,{"derivedFrom":[subQ1,subQ0]});Q89=makeQuery(id+"F25.imprint","IMPRINT",FACE,{"disambiguationData":[TD([[makeQuery(id+"F25.imprint","IMPRINT",EDGE,{"disambiguationData":[TD([[subQ2,-1.0]])],"derivedFrom":subQ1}),-1.0]])]});}
            var Q90;
            {var subQ0=sQuery(id+"F25.wireOp",EDGE,"E522.trimOffspring");var subQ1=sQuery(id+"F25.wireOp",EDGE,"E277.trimOffspring");var subQ2=makeQuery(id+"F25.imprint","INTERSECT",VERTEX,{"derivedFrom":[subQ1,subQ0]});Q90=makeQuery(id+"F25.imprint","IMPRINT",FACE,{"disambiguationData":[TD([[makeQuery(id+"F25.imprint","IMPRINT",EDGE,{"disambiguationData":[TD([[subQ2,-1.0]])],"derivedFrom":subQ1}),-1.0]])]});}
            var Q91;
            {var subQ0=sQuery(id+"F25.wireOp",EDGE,"E525.trimOffspring");var subQ1=sQuery(id+"F25.wireOp",EDGE,"E277.trimOffspring");var subQ2=makeQuery(id+"F25.imprint","INTERSECT",VERTEX,{"derivedFrom":[subQ1,subQ0]});Q91=makeQuery(id+"F25.imprint","IMPRINT",FACE,{"disambiguationData":[TD([[makeQuery(id+"F25.imprint","IMPRINT",EDGE,{"disambiguationData":[TD([[subQ2,1.0]])],"derivedFrom":subQ1}),-1.0]])]});}
            var Q92;
            {var subQ0=sQuery(id+"F25.wireOp",EDGE,"E525.trimOffspring");var subQ1=sQuery(id+"F25.wireOp",EDGE,"E276.trimOffspring");var subQ2=makeQuery(id+"F25.imprint","INTERSECT",VERTEX,{"derivedFrom":[subQ1,subQ0]});Q92=makeQuery(id+"F25.imprint","IMPRINT",FACE,{"disambiguationData":[TD([[makeQuery(id+"F25.imprint","IMPRINT",EDGE,{"disambiguationData":[TD([[subQ2,1.0]])],"derivedFrom":subQ1}),-1.0]])]});}
            var Q93;
            {var subQ0=sQuery(id+"F25.wireOp",EDGE,"E522.trimOffspring");var subQ1=sQuery(id+"F25.wireOp",EDGE,"E280.trimOffspring");var subQ2=makeQuery(id+"F25.imprint","INTERSECT",VERTEX,{"derivedFrom":[subQ1,subQ0]});Q93=makeQuery(id+"F25.imprint","IMPRINT",FACE,{"disambiguationData":[TD([[makeQuery(id+"F25.imprint","IMPRINT",EDGE,{"disambiguationData":[TD([[subQ2,-1.0]])],"derivedFrom":subQ1}),1.0]])]});}
            var Q94;
            {var subQ0=sQuery(id+"F25.wireOp",EDGE,"E525.trimOffspring");var subQ1=sQuery(id+"F25.wireOp",EDGE,"E280.trimOffspring");var subQ2=makeQuery(id+"F25.imprint","INTERSECT",VERTEX,{"derivedFrom":[subQ1,subQ0]});Q94=makeQuery(id+"F25.imprint","IMPRINT",FACE,{"disambiguationData":[TD([[makeQuery(id+"F25.imprint","IMPRINT",EDGE,{"disambiguationData":[TD([[subQ2,1.0]])],"derivedFrom":subQ1}),1.0]])]});}
            var Q95;
            {var subQ0=sQuery(id+"F25.wireOp",EDGE,"E525.trimOffspring");var subQ1=sQuery(id+"F25.wireOp",EDGE,"E280.trimOffspring");var subQ2=makeQuery(id+"F25.imprint","INTERSECT",VERTEX,{"derivedFrom":[subQ1,subQ0]});Q95=makeQuery(id+"F25.imprint","IMPRINT",FACE,{"disambiguationData":[TD([[makeQuery(id+"F25.imprint","IMPRINT",EDGE,{"disambiguationData":[TD([[subQ2,1.0]])],"derivedFrom":subQ1}),-1.0]])]});}
            var Q96;
            {var subQ0=sQuery(id+"F25.wireOp",EDGE,"E525.trimOffspring");var subQ1=sQuery(id+"F25.wireOp",EDGE,"E279.trimOffspring");var subQ2=makeQuery(id+"F25.imprint","INTERSECT",VERTEX,{"derivedFrom":[subQ1,subQ0]});Q96=makeQuery(id+"F25.imprint","IMPRINT",FACE,{"disambiguationData":[TD([[makeQuery(id+"F25.imprint","IMPRINT",EDGE,{"disambiguationData":[TD([[subQ2,1.0]])],"derivedFrom":subQ1}),1.0]])]});}
            var Q97;
            {var subQ0=sQuery(id+"F25.wireOp",EDGE,"E522.trimOffspring");var subQ1=sQuery(id+"F25.wireOp",EDGE,"E280.trimOffspring");var subQ2=makeQuery(id+"F25.imprint","INTERSECT",VERTEX,{"derivedFrom":[subQ1,subQ0]});Q97=makeQuery(id+"F25.imprint","IMPRINT",FACE,{"disambiguationData":[TD([[makeQuery(id+"F25.imprint","IMPRINT",EDGE,{"disambiguationData":[TD([[subQ2,-1.0]])],"derivedFrom":subQ1}),-1.0]])]});}
            var Q98;
            {var subQ0=sQuery(id+"F25.wireOp",EDGE,"E510.trimOffspring");var subQ1=sQuery(id+"F25.wireOp",EDGE,"E280.trimOffspring");var subQ2=makeQuery(id+"F25.imprint","INTERSECT",VERTEX,{"derivedFrom":[subQ1,subQ0]});Q98=makeQuery(id+"F25.imprint","IMPRINT",FACE,{"disambiguationData":[TD([[makeQuery(id+"F25.imprint","IMPRINT",EDGE,{"disambiguationData":[TD([[subQ2,-1.0]])],"derivedFrom":subQ1}),-1.0]])]});}
            var Q99;
            {var subQ0=sQuery(id+"F25.wireOp",EDGE,"E510.trimOffspring");var subQ1=sQuery(id+"F25.wireOp",EDGE,"E279.trimOffspring");var subQ2=makeQuery(id+"F25.imprint","INTERSECT",VERTEX,{"derivedFrom":[subQ1,subQ0]});Q99=makeQuery(id+"F25.imprint","IMPRINT",FACE,{"disambiguationData":[TD([[makeQuery(id+"F25.imprint","IMPRINT",EDGE,{"disambiguationData":[TD([[subQ2,-1.0]])],"derivedFrom":subQ1}),1.0]])]});}
            var Q100;
            {var subQ0=sQuery(id+"F25.wireOp",EDGE,"E517.trimOffspring");var subQ1=sQuery(id+"F25.wireOp",EDGE,"E280.trimOffspring");var subQ2=makeQuery(id+"F25.imprint","INTERSECT",VERTEX,{"derivedFrom":[subQ1,subQ0]});Q100=makeQuery(id+"F25.imprint","IMPRINT",FACE,{"disambiguationData":[TD([[makeQuery(id+"F25.imprint","IMPRINT",EDGE,{"disambiguationData":[TD([[subQ2,-1.0]])],"derivedFrom":subQ1}),-1.0]])]});}
            var Q101;
            {var subQ0=sQuery(id+"F25.wireOp",EDGE,"E517.trimOffspring");var subQ1=sQuery(id+"F25.wireOp",EDGE,"E279.trimOffspring");var subQ2=makeQuery(id+"F25.imprint","INTERSECT",VERTEX,{"derivedFrom":[subQ1,subQ0]});Q101=makeQuery(id+"F25.imprint","IMPRINT",FACE,{"disambiguationData":[TD([[makeQuery(id+"F25.imprint","IMPRINT",EDGE,{"disambiguationData":[TD([[subQ2,-1.0]])],"derivedFrom":subQ1}),1.0]])]});}
            var Q102;
            {var subQ0=sQuery(id+"F25.wireOp",EDGE,"E519.trimOffspring");var subQ1=sQuery(id+"F25.wireOp",EDGE,"E279.trimOffspring");var subQ2=makeQuery(id+"F25.imprint","INTERSECT",VERTEX,{"derivedFrom":[subQ1,subQ0]});Q102=makeQuery(id+"F25.imprint","IMPRINT",FACE,{"disambiguationData":[TD([[makeQuery(id+"F25.imprint","IMPRINT",EDGE,{"disambiguationData":[TD([[subQ2,-1.0]])],"derivedFrom":subQ1}),1.0]])]});}
            var Q103;
            {var subQ0=sQuery(id+"F25.wireOp",EDGE,"E519.trimOffspring");var subQ1=sQuery(id+"F25.wireOp",EDGE,"E280.trimOffspring");var subQ2=makeQuery(id+"F25.imprint","INTERSECT",VERTEX,{"derivedFrom":[subQ1,subQ0]});Q103=makeQuery(id+"F25.imprint","IMPRINT",FACE,{"disambiguationData":[TD([[makeQuery(id+"F25.imprint","IMPRINT",EDGE,{"disambiguationData":[TD([[subQ2,-1.0]])],"derivedFrom":subQ1}),-1.0]])]});}
            var Q104;
            {var subQ0=sQuery(id+"F25.wireOp",EDGE,"E518.trimOffspring");var subQ1=sQuery(id+"F25.wireOp",EDGE,"E280.trimOffspring");var subQ2=makeQuery(id+"F25.imprint","INTERSECT",VERTEX,{"derivedFrom":[subQ1,subQ0]});Q104=makeQuery(id+"F25.imprint","IMPRINT",FACE,{"disambiguationData":[TD([[makeQuery(id+"F25.imprint","IMPRINT",EDGE,{"disambiguationData":[TD([[subQ2,-1.0]])],"derivedFrom":subQ1}),-1.0]])]});}
            var Q105;
            {var subQ0=sQuery(id+"F25.wireOp",EDGE,"E518.trimOffspring");var subQ1=sQuery(id+"F25.wireOp",EDGE,"E279.trimOffspring");var subQ2=makeQuery(id+"F25.imprint","INTERSECT",VERTEX,{"derivedFrom":[subQ1,subQ0]});Q105=makeQuery(id+"F25.imprint","IMPRINT",FACE,{"disambiguationData":[TD([[makeQuery(id+"F25.imprint","IMPRINT",EDGE,{"disambiguationData":[TD([[subQ2,-1.0]])],"derivedFrom":subQ1}),1.0]])]});}
            var Q106;
            {var subQ0=sQuery(id+"F25.wireOp",EDGE,"E507.trimOffspring");var subQ1=sQuery(id+"F25.wireOp",EDGE,"E280.trimOffspring");var subQ2=makeQuery(id+"F25.imprint","INTERSECT",VERTEX,{"derivedFrom":[subQ1,subQ0]});Q106=makeQuery(id+"F25.imprint","IMPRINT",FACE,{"disambiguationData":[TD([[makeQuery(id+"F25.imprint","IMPRINT",EDGE,{"disambiguationData":[TD([[subQ2,-1.0]])],"derivedFrom":subQ1}),-1.0]])]});}
            var Q107;
            {var subQ0=sQuery(id+"F25.wireOp",EDGE,"E507.trimOffspring");var subQ1=sQuery(id+"F25.wireOp",EDGE,"E279.trimOffspring");var subQ2=makeQuery(id+"F25.imprint","INTERSECT",VERTEX,{"derivedFrom":[subQ1,subQ0]});Q107=makeQuery(id+"F25.imprint","IMPRINT",FACE,{"disambiguationData":[TD([[makeQuery(id+"F25.imprint","IMPRINT",EDGE,{"disambiguationData":[TD([[subQ2,-1.0]])],"derivedFrom":subQ1}),1.0]])]});}
            var Q108;
            {var subQ0=sQuery(id+"F25.wireOp",EDGE,"E512.trimOffspring");var subQ1=sQuery(id+"F25.wireOp",EDGE,"E280.trimOffspring");var subQ2=makeQuery(id+"F25.imprint","INTERSECT",VERTEX,{"derivedFrom":[subQ1,subQ0]});Q108=makeQuery(id+"F25.imprint","IMPRINT",FACE,{"disambiguationData":[TD([[makeQuery(id+"F25.imprint","IMPRINT",EDGE,{"disambiguationData":[TD([[subQ2,-1.0]])],"derivedFrom":subQ1}),-1.0]])]});}
            var Q109;
            {var subQ0=sQuery(id+"F25.wireOp",EDGE,"E512.trimOffspring");var subQ1=sQuery(id+"F25.wireOp",EDGE,"E279.trimOffspring");var subQ2=makeQuery(id+"F25.imprint","INTERSECT",VERTEX,{"derivedFrom":[subQ1,subQ0]});Q109=makeQuery(id+"F25.imprint","IMPRINT",FACE,{"disambiguationData":[TD([[makeQuery(id+"F25.imprint","IMPRINT",EDGE,{"disambiguationData":[TD([[subQ2,-1.0]])],"derivedFrom":subQ1}),1.0]])]});}
            var Q110;
            {var subQ0=sQuery(id+"F25.wireOp",EDGE,"E522.trimOffspring");var subQ1=sQuery(id+"F25.wireOp",EDGE,"E279.trimOffspring");var subQ2=makeQuery(id+"F25.imprint","INTERSECT",VERTEX,{"derivedFrom":[subQ1,subQ0]});Q110=makeQuery(id+"F25.imprint","IMPRINT",FACE,{"disambiguationData":[TD([[makeQuery(id+"F25.imprint","IMPRINT",EDGE,{"disambiguationData":[TD([[subQ2,-1.0]])],"derivedFrom":subQ1}),1.0]])]});}
            var Q111;
            {var subQ0=sQuery(id+"F25.wireOp",EDGE,"E522.trimOffspring");var subQ1=sQuery(id+"F25.wireOp",EDGE,"E279.trimOffspring");var subQ2=makeQuery(id+"F25.imprint","INTERSECT",VERTEX,{"derivedFrom":[subQ1,subQ0]});Q111=makeQuery(id+"F25.imprint","IMPRINT",FACE,{"disambiguationData":[TD([[makeQuery(id+"F25.imprint","IMPRINT",EDGE,{"disambiguationData":[TD([[subQ2,-1.0]])],"derivedFrom":subQ1}),-1.0]])]});}
            var Q112;
            {var subQ0=sQuery(id+"F25.wireOp",EDGE,"E525.trimOffspring");var subQ1=sQuery(id+"F25.wireOp",EDGE,"E279.trimOffspring");var subQ2=makeQuery(id+"F25.imprint","INTERSECT",VERTEX,{"derivedFrom":[subQ1,subQ0]});Q112=makeQuery(id+"F25.imprint","IMPRINT",FACE,{"disambiguationData":[TD([[makeQuery(id+"F25.imprint","IMPRINT",EDGE,{"disambiguationData":[TD([[subQ2,1.0]])],"derivedFrom":subQ1}),-1.0]])]});}
            var Q113;
            {var subQ0=sQuery(id+"F25.wireOp",EDGE,"E525.trimOffspring");var subQ1=sQuery(id+"F25.wireOp",EDGE,"E287.trimOffspring");var subQ2=makeQuery(id+"F25.imprint","INTERSECT",VERTEX,{"derivedFrom":[subQ1,subQ0]});Q113=makeQuery(id+"F25.imprint","IMPRINT",FACE,{"disambiguationData":[TD([[makeQuery(id+"F25.imprint","IMPRINT",EDGE,{"disambiguationData":[TD([[subQ2,1.0]])],"derivedFrom":subQ1}),-1.0]])]});}
            var Q114;
            {var subQ0=sQuery(id+"F25.wireOp",EDGE,"E525.trimOffspring");var subQ1=sQuery(id+"F25.wireOp",EDGE,"E291.trimOffspring");var subQ2=makeQuery(id+"F25.imprint","INTERSECT",VERTEX,{"derivedFrom":[subQ1,subQ0]});Q114=makeQuery(id+"F25.imprint","IMPRINT",FACE,{"disambiguationData":[TD([[makeQuery(id+"F25.imprint","IMPRINT",EDGE,{"disambiguationData":[TD([[subQ2,1.0]])],"derivedFrom":subQ1}),1.0]])]});}
            var Q115;
            {var subQ0=sQuery(id+"F25.wireOp",EDGE,"E522.trimOffspring");var subQ1=sQuery(id+"F25.wireOp",EDGE,"E287.trimOffspring");var subQ2=makeQuery(id+"F25.imprint","INTERSECT",VERTEX,{"derivedFrom":[subQ1,subQ0]});Q115=makeQuery(id+"F25.imprint","IMPRINT",FACE,{"disambiguationData":[TD([[makeQuery(id+"F25.imprint","IMPRINT",EDGE,{"disambiguationData":[TD([[subQ2,-1.0]])],"derivedFrom":subQ1}),-1.0]])]});}
            var Q116;
            {var subQ0=sQuery(id+"F25.wireOp",EDGE,"E522.trimOffspring");var subQ1=sQuery(id+"F25.wireOp",EDGE,"E291.trimOffspring");var subQ2=makeQuery(id+"F25.imprint","INTERSECT",VERTEX,{"derivedFrom":[subQ1,subQ0]});Q116=makeQuery(id+"F25.imprint","IMPRINT",FACE,{"disambiguationData":[TD([[makeQuery(id+"F25.imprint","IMPRINT",EDGE,{"disambiguationData":[TD([[subQ2,-1.0]])],"derivedFrom":subQ1}),1.0]])]});}
            var Q117;
            {var subQ0=sQuery(id+"F25.wireOp",EDGE,"E510.trimOffspring");var subQ1=sQuery(id+"F25.wireOp",EDGE,"E287.trimOffspring");var subQ2=makeQuery(id+"F25.imprint","INTERSECT",VERTEX,{"derivedFrom":[subQ1,subQ0]});Q117=makeQuery(id+"F25.imprint","IMPRINT",FACE,{"disambiguationData":[TD([[makeQuery(id+"F25.imprint","IMPRINT",EDGE,{"disambiguationData":[TD([[subQ2,-1.0]])],"derivedFrom":subQ1}),-1.0]])]});}
            var Q118;
            {var subQ0=sQuery(id+"F25.wireOp",EDGE,"E510.trimOffspring");var subQ1=sQuery(id+"F25.wireOp",EDGE,"E291.trimOffspring");var subQ2=makeQuery(id+"F25.imprint","INTERSECT",VERTEX,{"derivedFrom":[subQ1,subQ0]});Q118=makeQuery(id+"F25.imprint","IMPRINT",FACE,{"disambiguationData":[TD([[makeQuery(id+"F25.imprint","IMPRINT",EDGE,{"disambiguationData":[TD([[subQ2,-1.0]])],"derivedFrom":subQ1}),1.0]])]});}
            var Q119;
            {var subQ0=sQuery(id+"F25.wireOp",EDGE,"E512.trimOffspring");var subQ1=sQuery(id+"F25.wireOp",EDGE,"E287.trimOffspring");var subQ2=makeQuery(id+"F25.imprint","INTERSECT",VERTEX,{"derivedFrom":[subQ1,subQ0]});Q119=makeQuery(id+"F25.imprint","IMPRINT",FACE,{"disambiguationData":[TD([[makeQuery(id+"F25.imprint","IMPRINT",EDGE,{"disambiguationData":[TD([[subQ2,-1.0]])],"derivedFrom":subQ1}),-1.0]])]});}
            var Q120;
            {var subQ0=sQuery(id+"F25.wireOp",EDGE,"E512.trimOffspring");var subQ1=sQuery(id+"F25.wireOp",EDGE,"E291.trimOffspring");var subQ2=makeQuery(id+"F25.imprint","INTERSECT",VERTEX,{"derivedFrom":[subQ1,subQ0]});Q120=makeQuery(id+"F25.imprint","IMPRINT",FACE,{"disambiguationData":[TD([[makeQuery(id+"F25.imprint","IMPRINT",EDGE,{"disambiguationData":[TD([[subQ2,-1.0]])],"derivedFrom":subQ1}),1.0]])]});}
            var Q121;
            {var subQ0=sQuery(id+"F25.wireOp",EDGE,"E507.trimOffspring");var subQ1=sQuery(id+"F25.wireOp",EDGE,"E291.trimOffspring");var subQ2=makeQuery(id+"F25.imprint","INTERSECT",VERTEX,{"derivedFrom":[subQ1,subQ0]});Q121=makeQuery(id+"F25.imprint","IMPRINT",FACE,{"disambiguationData":[TD([[makeQuery(id+"F25.imprint","IMPRINT",EDGE,{"disambiguationData":[TD([[subQ2,-1.0]])],"derivedFrom":subQ1}),1.0]])]});}
            var Q122;
            {var subQ0=sQuery(id+"F25.wireOp",EDGE,"E507.trimOffspring");var subQ1=sQuery(id+"F25.wireOp",EDGE,"E287.trimOffspring");var subQ2=makeQuery(id+"F25.imprint","INTERSECT",VERTEX,{"derivedFrom":[subQ1,subQ0]});Q122=makeQuery(id+"F25.imprint","IMPRINT",FACE,{"disambiguationData":[TD([[makeQuery(id+"F25.imprint","IMPRINT",EDGE,{"disambiguationData":[TD([[subQ2,-1.0]])],"derivedFrom":subQ1}),-1.0]])]});}
            var Q123;
            {var subQ0=sQuery(id+"F25.wireOp",EDGE,"E518.trimOffspring");var subQ1=sQuery(id+"F25.wireOp",EDGE,"E287.trimOffspring");var subQ2=makeQuery(id+"F25.imprint","INTERSECT",VERTEX,{"derivedFrom":[subQ1,subQ0]});Q123=makeQuery(id+"F25.imprint","IMPRINT",FACE,{"disambiguationData":[TD([[makeQuery(id+"F25.imprint","IMPRINT",EDGE,{"disambiguationData":[TD([[subQ2,-1.0]])],"derivedFrom":subQ1}),-1.0]])]});}
            var Q124;
            {var subQ0=sQuery(id+"F25.wireOp",EDGE,"E518.trimOffspring");var subQ1=sQuery(id+"F25.wireOp",EDGE,"E291.trimOffspring");var subQ2=makeQuery(id+"F25.imprint","INTERSECT",VERTEX,{"derivedFrom":[subQ1,subQ0]});Q124=makeQuery(id+"F25.imprint","IMPRINT",FACE,{"disambiguationData":[TD([[makeQuery(id+"F25.imprint","IMPRINT",EDGE,{"disambiguationData":[TD([[subQ2,-1.0]])],"derivedFrom":subQ1}),1.0]])]});}
            var Q125;
            {var subQ0=sQuery(id+"F25.wireOp",EDGE,"E519.trimOffspring");var subQ1=sQuery(id+"F25.wireOp",EDGE,"E287.trimOffspring");var subQ2=makeQuery(id+"F25.imprint","INTERSECT",VERTEX,{"derivedFrom":[subQ1,subQ0]});Q125=makeQuery(id+"F25.imprint","IMPRINT",FACE,{"disambiguationData":[TD([[makeQuery(id+"F25.imprint","IMPRINT",EDGE,{"disambiguationData":[TD([[subQ2,-1.0]])],"derivedFrom":subQ1}),-1.0]])]});}
            var Q126;
            {var subQ0=sQuery(id+"F25.wireOp",EDGE,"E517.trimOffspring");var subQ1=sQuery(id+"F25.wireOp",EDGE,"E287.trimOffspring");var subQ2=makeQuery(id+"F25.imprint","INTERSECT",VERTEX,{"derivedFrom":[subQ1,subQ0]});Q126=makeQuery(id+"F25.imprint","IMPRINT",FACE,{"disambiguationData":[TD([[makeQuery(id+"F25.imprint","IMPRINT",EDGE,{"disambiguationData":[TD([[subQ2,-1.0]])],"derivedFrom":subQ1}),-1.0]])]});}
            var Q127;
            {var subQ0=sQuery(id+"F25.wireOp",EDGE,"E517.trimOffspring");var subQ1=sQuery(id+"F25.wireOp",EDGE,"E291.trimOffspring");var subQ2=makeQuery(id+"F25.imprint","INTERSECT",VERTEX,{"derivedFrom":[subQ1,subQ0]});Q127=makeQuery(id+"F25.imprint","IMPRINT",FACE,{"disambiguationData":[TD([[makeQuery(id+"F25.imprint","IMPRINT",EDGE,{"disambiguationData":[TD([[subQ2,-1.0]])],"derivedFrom":subQ1}),1.0]])]});}
            var Q128;
            {var subQ0=sQuery(id+"F25.wireOp",EDGE,"E519.trimOffspring");var subQ1=sQuery(id+"F25.wireOp",EDGE,"E291.trimOffspring");var subQ2=makeQuery(id+"F25.imprint","INTERSECT",VERTEX,{"derivedFrom":[subQ1,subQ0]});Q128=makeQuery(id+"F25.imprint","IMPRINT",FACE,{"disambiguationData":[TD([[makeQuery(id+"F25.imprint","IMPRINT",EDGE,{"disambiguationData":[TD([[subQ2,-1.0]])],"derivedFrom":subQ1}),1.0]])]});}
            var Q129;
            {var subQ0=sQuery(id+"F25.wireOp",EDGE,"E517.trimOffspring");var subQ1=sQuery(id+"F25.wireOp",EDGE,"E251.right");var subQ2=makeQuery(id+"F25.imprint","INTERSECT",VERTEX,{"derivedFrom":[subQ1,subQ0]});Q129=makeQuery(id+"F25.imprint","IMPRINT",FACE,{"disambiguationData":[TD([[makeQuery(id+"F25.imprint","IMPRINT",EDGE,{"disambiguationData":[TD([[subQ2,-1.0]])],"derivedFrom":subQ1}),1.0]])]});}
            var Q130;
            {var subQ0=sQuery(id+"F25.wireOp",EDGE,"E519.trimOffspring");var subQ1=sQuery(id+"F25.wireOp",EDGE,"E251.right");var subQ2=makeQuery(id+"F25.imprint","INTERSECT",VERTEX,{"derivedFrom":[subQ1,subQ0]});Q130=makeQuery(id+"F25.imprint","IMPRINT",FACE,{"disambiguationData":[TD([[makeQuery(id+"F25.imprint","IMPRINT",EDGE,{"disambiguationData":[TD([[subQ2,-1.0]])],"derivedFrom":subQ1}),1.0]])]});}
            var Q131;
            {var subQ0=sQuery(id+"F25.wireOp",EDGE,"E519.trimOffspring");var subQ1=sQuery(id+"F25.wireOp",EDGE,"E250.left");var subQ2=makeQuery(id+"F25.imprint","INTERSECT",VERTEX,{"derivedFrom":[subQ1,subQ0]});Q131=makeQuery(id+"F25.imprint","IMPRINT",FACE,{"disambiguationData":[TD([[makeQuery(id+"F25.imprint","IMPRINT",EDGE,{"disambiguationData":[TD([[subQ2,-1.0]])],"derivedFrom":subQ1}),1.0]])]});}
            var Q132;
            {var subQ0=sQuery(id+"F25.wireOp",EDGE,"E517.trimOffspring");var subQ1=sQuery(id+"F25.wireOp",EDGE,"E250.left");var subQ2=makeQuery(id+"F25.imprint","INTERSECT",VERTEX,{"derivedFrom":[subQ1,subQ0]});Q132=makeQuery(id+"F25.imprint","IMPRINT",FACE,{"disambiguationData":[TD([[makeQuery(id+"F25.imprint","IMPRINT",EDGE,{"disambiguationData":[TD([[subQ2,-1.0]])],"derivedFrom":subQ1}),1.0]])]});}
            var Q133;
            {var subQ0=sQuery(id+"F25.wireOp",EDGE,"E517.trimOffspring");var subQ1=sQuery(id+"F25.wireOp",EDGE,"E250.right");var subQ2=makeQuery(id+"F25.imprint","INTERSECT",VERTEX,{"derivedFrom":[subQ1,subQ0]});Q133=makeQuery(id+"F25.imprint","IMPRINT",FACE,{"disambiguationData":[TD([[makeQuery(id+"F25.imprint","IMPRINT",EDGE,{"disambiguationData":[TD([[subQ2,-1.0]])],"derivedFrom":subQ1}),1.0]])]});}
            var Q134;
            {var subQ0=sQuery(id+"F25.wireOp",EDGE,"E519.trimOffspring");var subQ1=sQuery(id+"F25.wireOp",EDGE,"E250.right");var subQ2=makeQuery(id+"F25.imprint","INTERSECT",VERTEX,{"derivedFrom":[subQ1,subQ0]});Q134=makeQuery(id+"F25.imprint","IMPRINT",FACE,{"disambiguationData":[TD([[makeQuery(id+"F25.imprint","IMPRINT",EDGE,{"disambiguationData":[TD([[subQ2,-1.0]])],"derivedFrom":subQ1}),1.0]])]});}
            var Q135;
            {var subQ0=sQuery(id+"F25.wireOp",EDGE,"E518.trimOffspring");var subQ1=sQuery(id+"F25.wireOp",EDGE,"E250.right");var subQ2=makeQuery(id+"F25.imprint","INTERSECT",VERTEX,{"derivedFrom":[subQ1,subQ0]});Q135=makeQuery(id+"F25.imprint","IMPRINT",FACE,{"disambiguationData":[TD([[makeQuery(id+"F25.imprint","IMPRINT",EDGE,{"disambiguationData":[TD([[subQ2,-1.0]])],"derivedFrom":subQ1}),1.0]])]});}
            var Q136;
            {var subQ0=sQuery(id+"F25.wireOp",EDGE,"E518.trimOffspring");var subQ1=sQuery(id+"F25.wireOp",EDGE,"E250.left");var subQ2=makeQuery(id+"F25.imprint","INTERSECT",VERTEX,{"derivedFrom":[subQ1,subQ0]});Q136=makeQuery(id+"F25.imprint","IMPRINT",FACE,{"disambiguationData":[TD([[makeQuery(id+"F25.imprint","IMPRINT",EDGE,{"disambiguationData":[TD([[subQ2,-1.0]])],"derivedFrom":subQ1}),1.0]])]});}
            var Q137;
            {var subQ0=sQuery(id+"F25.wireOp",EDGE,"E507.trimOffspring");var subQ1=sQuery(id+"F25.wireOp",EDGE,"E250.left");var subQ2=makeQuery(id+"F25.imprint","INTERSECT",VERTEX,{"derivedFrom":[subQ1,subQ0]});Q137=makeQuery(id+"F25.imprint","IMPRINT",FACE,{"disambiguationData":[TD([[makeQuery(id+"F25.imprint","IMPRINT",EDGE,{"disambiguationData":[TD([[subQ2,-1.0]])],"derivedFrom":subQ1}),1.0]])]});}
            var Q138;
            {var subQ0=sQuery(id+"F25.wireOp",EDGE,"E507.trimOffspring");var subQ1=sQuery(id+"F25.wireOp",EDGE,"E250.right");var subQ2=makeQuery(id+"F25.imprint","INTERSECT",VERTEX,{"derivedFrom":[subQ1,subQ0]});Q138=makeQuery(id+"F25.imprint","IMPRINT",FACE,{"disambiguationData":[TD([[makeQuery(id+"F25.imprint","IMPRINT",EDGE,{"disambiguationData":[TD([[subQ2,-1.0]])],"derivedFrom":subQ1}),1.0]])]});}
            var Q139;
            {var subQ0=sQuery(id+"F25.wireOp",EDGE,"E512.trimOffspring");var subQ1=sQuery(id+"F25.wireOp",EDGE,"E250.left");var subQ2=makeQuery(id+"F25.imprint","INTERSECT",VERTEX,{"derivedFrom":[subQ1,subQ0]});Q139=makeQuery(id+"F25.imprint","IMPRINT",FACE,{"disambiguationData":[TD([[makeQuery(id+"F25.imprint","IMPRINT",EDGE,{"disambiguationData":[TD([[subQ2,-1.0]])],"derivedFrom":subQ1}),1.0]])]});}
            var Q140;
            {var subQ0=sQuery(id+"F25.wireOp",EDGE,"E512.trimOffspring");var subQ1=sQuery(id+"F25.wireOp",EDGE,"E250.right");var subQ2=makeQuery(id+"F25.imprint","INTERSECT",VERTEX,{"derivedFrom":[subQ1,subQ0]});Q140=makeQuery(id+"F25.imprint","IMPRINT",FACE,{"disambiguationData":[TD([[makeQuery(id+"F25.imprint","IMPRINT",EDGE,{"disambiguationData":[TD([[subQ2,-1.0]])],"derivedFrom":subQ1}),1.0]])]});}
            var Q141;
            {var subQ0=sQuery(id+"F25.wireOp",EDGE,"E512.trimOffspring");var subQ1=sQuery(id+"F25.wireOp",EDGE,"E249.right");var subQ2=makeQuery(id+"F25.imprint","INTERSECT",VERTEX,{"derivedFrom":[subQ1,subQ0]});Q141=makeQuery(id+"F25.imprint","IMPRINT",FACE,{"disambiguationData":[TD([[makeQuery(id+"F25.imprint","IMPRINT",EDGE,{"disambiguationData":[TD([[subQ2,-1.0]])],"derivedFrom":subQ1}),1.0]])]});}
            var Q142;
            {var subQ0=sQuery(id+"F25.wireOp",EDGE,"E507.trimOffspring");var subQ1=sQuery(id+"F25.wireOp",EDGE,"E249.right");var subQ2=makeQuery(id+"F25.imprint","INTERSECT",VERTEX,{"derivedFrom":[subQ1,subQ0]});Q142=makeQuery(id+"F25.imprint","IMPRINT",FACE,{"disambiguationData":[TD([[makeQuery(id+"F25.imprint","IMPRINT",EDGE,{"disambiguationData":[TD([[subQ2,-1.0]])],"derivedFrom":subQ1}),1.0]])]});}
            var Q143;
            {var subQ5=sQuery(id+"F25.wireOp",EDGE,"E253.right");Q143=makeQuery(id+"F25.imprint","IMPRINT",FACE,{"disambiguationData":[TD([[makeQuery(id+"F25.imprint","IMPRINT",EDGE,{"derivedFrom":subQ5}),1.0]])]});}
            var Q144;
            {var subQ5=sQuery(id+"F25.wireOp",EDGE,"E252.right");Q144=makeQuery(id+"F25.imprint","IMPRINT",FACE,{"disambiguationData":[TD([[makeQuery(id+"F25.imprint","IMPRINT",EDGE,{"derivedFrom":subQ5}),-1.0]])]});}
            var Q145;
            {var subQ0=sQuery(id+"F25.wireOp",EDGE,"E253.right");Q145=makeQuery(id+"F25.imprint","IMPRINT",FACE,{"disambiguationData":[TD([[makeQuery(id+"F25.imprint","IMPRINT",EDGE,{"derivedFrom":subQ0}),-1.0]])]});}
            var Q146;
            {var subQ0=sQuery(id+"F25.wireOp",EDGE,"E252.right");Q146=makeQuery(id+"F25.imprint","IMPRINT",FACE,{"disambiguationData":[TD([[makeQuery(id+"F25.imprint","IMPRINT",EDGE,{"derivedFrom":subQ0}),1.0]])]});}
            var Q147;
            {var subQ0=sQuery(id+"F25.wireOp",EDGE,"E518.trimOffspring");var subQ5=sQuery(id+"F25.wireOp",EDGE,"E249.right");var subQ7=makeQuery(id+"F25.imprint","INTERSECT",VERTEX,{"derivedFrom":[subQ5,subQ0]});Q147=makeQuery(id+"F25.imprint","IMPRINT",FACE,{"disambiguationData":[TD([[makeQuery(id+"F25.imprint","IMPRINT",EDGE,{"disambiguationData":[TD([[subQ7,-1.0]])],"derivedFrom":subQ5}),-1.0]])]});}
            var Q148;
            {var subQ0=sQuery(id+"F25.wireOp",EDGE,"E373.MirrorCS");var subQ5=sQuery(id+"F25.wireOp",EDGE,"E387.MirrorCS");var subQ6=makeQuery(id+"F25.imprint","INTERSECT",VERTEX,{"derivedFrom":[subQ0,subQ5]});Q148=makeQuery(id+"F25.imprint","IMPRINT",FACE,{"disambiguationData":[TD([[makeQuery(id+"F25.imprint","IMPRINT",EDGE,{"disambiguationData":[TD([[subQ6,-1.0]])],"derivedFrom":subQ5}),1.0]])]});}
            var Q149;
            {var subQ5=sQuery(id+"F25.wireOp",EDGE,"E236.right");Q149=makeQuery(id+"F25.imprint","IMPRINT",FACE,{"disambiguationData":[TD([[makeQuery(id+"F25.imprint","IMPRINT",EDGE,{"derivedFrom":subQ5}),-1.0]])]});}
            var Q150;
            {var subQ5=sQuery(id+"F25.wireOp",EDGE,"E235.right");Q150=makeQuery(id+"F25.imprint","IMPRINT",FACE,{"disambiguationData":[TD([[makeQuery(id+"F25.imprint","IMPRINT",EDGE,{"derivedFrom":subQ5}),1.0]])]});}
            var Q151;
            {var subQ0=sQuery(id+"F25.wireOp",EDGE,"E365.MirrorCS");var subQ1=sQuery(id+"F25.wireOp",EDGE,"E344.MirrorCS");var subQ2=makeQuery(id+"F25.imprint","INTERSECT",VERTEX,{"derivedFrom":[subQ1,subQ0]});Q151=makeQuery(id+"F25.imprint","IMPRINT",FACE,{"disambiguationData":[TD([[makeQuery(id+"F25.imprint","IMPRINT",EDGE,{"disambiguationData":[TD([[subQ2,-1.0]])],"derivedFrom":subQ1}),-1.0]])]});}
            var Q152;
            {var subQ0=sQuery(id+"F25.wireOp",EDGE,"E334.MirrorCS");var subQ1=sQuery(id+"F25.wireOp",EDGE,"E344.MirrorCS");var subQ2=makeQuery(id+"F25.imprint","INTERSECT",VERTEX,{"derivedFrom":[subQ1,subQ0]});Q152=makeQuery(id+"F25.imprint","IMPRINT",FACE,{"disambiguationData":[TD([[makeQuery(id+"F25.imprint","IMPRINT",EDGE,{"disambiguationData":[TD([[subQ2,-1.0]])],"derivedFrom":subQ1}),1.0]])]});}
            var Q153;
            {var subQ0=sQuery(id+"F25.wireOp",EDGE,"E334.MirrorCS");var subQ1=sQuery(id+"F25.wireOp",EDGE,"E344.MirrorCS");var subQ2=makeQuery(id+"F25.imprint","INTERSECT",VERTEX,{"derivedFrom":[subQ1,subQ0]});Q153=makeQuery(id+"F25.imprint","IMPRINT",FACE,{"disambiguationData":[TD([[makeQuery(id+"F25.imprint","IMPRINT",EDGE,{"disambiguationData":[TD([[subQ2,-1.0]])],"derivedFrom":subQ1}),-1.0]])]});}
            var Q154;
            {var subQ0=sQuery(id+"F25.wireOp",EDGE,"E386.MirrorCS");var subQ1=sQuery(id+"F25.wireOp",EDGE,"E344.MirrorCS");var subQ2=makeQuery(id+"F25.imprint","INTERSECT",VERTEX,{"derivedFrom":[subQ1,subQ0]});Q154=makeQuery(id+"F25.imprint","IMPRINT",FACE,{"disambiguationData":[TD([[makeQuery(id+"F25.imprint","IMPRINT",EDGE,{"disambiguationData":[TD([[subQ2,-1.0]])],"derivedFrom":subQ1}),-1.0]])]});}
            var Q155;
            {var subQ0=sQuery(id+"F25.wireOp",EDGE,"E386.MirrorCS");var subQ1=sQuery(id+"F25.wireOp",EDGE,"E344.MirrorCS");var subQ2=makeQuery(id+"F25.imprint","INTERSECT",VERTEX,{"derivedFrom":[subQ1,subQ0]});Q155=makeQuery(id+"F25.imprint","IMPRINT",FACE,{"disambiguationData":[TD([[makeQuery(id+"F25.imprint","IMPRINT",EDGE,{"disambiguationData":[TD([[subQ2,-1.0]])],"derivedFrom":subQ1}),1.0]])]});}
            var Q156;
            {var subQ0=sQuery(id+"F25.wireOp",EDGE,"E398.MirrorCS");var subQ1=sQuery(id+"F25.wireOp",EDGE,"E334.MirrorCS");var subQ2=makeQuery(id+"F25.imprint","INTERSECT",VERTEX,{"derivedFrom":[subQ1,subQ0]});Q156=makeQuery(id+"F25.imprint","IMPRINT",FACE,{"disambiguationData":[TD([[makeQuery(id+"F25.imprint","IMPRINT",EDGE,{"disambiguationData":[TD([[subQ2,-1.0]])],"derivedFrom":subQ1}),-1.0]])]});}
            var Q157;
            {var subQ0=sQuery(id+"F25.wireOp",EDGE,"E398.MirrorCS");var subQ1=sQuery(id+"F25.wireOp",EDGE,"E365.MirrorCS");var subQ2=makeQuery(id+"F25.imprint","INTERSECT",VERTEX,{"derivedFrom":[subQ1,subQ0]});Q157=makeQuery(id+"F25.imprint","IMPRINT",FACE,{"disambiguationData":[TD([[makeQuery(id+"F25.imprint","IMPRINT",EDGE,{"disambiguationData":[TD([[subQ2,-1.0]])],"derivedFrom":subQ1}),-1.0]])]});}
            var Q158;
            {var subQ0=sQuery(id+"F25.wireOp",EDGE,"E366.MirrorCS");var subQ1=sQuery(id+"F25.wireOp",EDGE,"E334.MirrorCS");var subQ2=makeQuery(id+"F25.imprint","INTERSECT",VERTEX,{"derivedFrom":[subQ1,subQ0]});Q158=makeQuery(id+"F25.imprint","IMPRINT",FACE,{"disambiguationData":[TD([[makeQuery(id+"F25.imprint","IMPRINT",EDGE,{"disambiguationData":[TD([[subQ2,-1.0]])],"derivedFrom":subQ1}),-1.0]])]});}
            var Q159;
            {var subQ0=sQuery(id+"F25.wireOp",EDGE,"E366.MirrorCS");var subQ1=sQuery(id+"F25.wireOp",EDGE,"E365.MirrorCS");var subQ2=makeQuery(id+"F25.imprint","INTERSECT",VERTEX,{"derivedFrom":[subQ1,subQ0]});Q159=makeQuery(id+"F25.imprint","IMPRINT",FACE,{"disambiguationData":[TD([[makeQuery(id+"F25.imprint","IMPRINT",EDGE,{"disambiguationData":[TD([[subQ2,-1.0]])],"derivedFrom":subQ1}),-1.0]])]});}
            var Q160;
            {var subQ0=sQuery(id+"F25.wireOp",EDGE,"E366.MirrorCS");var subQ1=sQuery(id+"F25.wireOp",EDGE,"E365.MirrorCS");var subQ2=makeQuery(id+"F25.imprint","INTERSECT",VERTEX,{"derivedFrom":[subQ1,subQ0]});Q160=makeQuery(id+"F25.imprint","IMPRINT",FACE,{"disambiguationData":[TD([[makeQuery(id+"F25.imprint","IMPRINT",EDGE,{"disambiguationData":[TD([[subQ2,-1.0]])],"derivedFrom":subQ1}),1.0]])]});}
            var Q161;
            {var subQ0=sQuery(id+"F25.wireOp",EDGE,"E365.MirrorCS");var subQ1=sQuery(id+"F25.wireOp",EDGE,"E347.MirrorCS");var subQ2=makeQuery(id+"F25.imprint","INTERSECT",VERTEX,{"derivedFrom":[subQ1,subQ0]});Q161=makeQuery(id+"F25.imprint","IMPRINT",FACE,{"disambiguationData":[TD([[makeQuery(id+"F25.imprint","IMPRINT",EDGE,{"disambiguationData":[TD([[subQ2,-1.0]])],"derivedFrom":subQ1}),-1.0]])]});}
            var Q162;
            {var subQ0=sQuery(id+"F25.wireOp",EDGE,"E334.MirrorCS");var subQ1=sQuery(id+"F25.wireOp",EDGE,"E347.MirrorCS");var subQ2=makeQuery(id+"F25.imprint","INTERSECT",VERTEX,{"derivedFrom":[subQ1,subQ0]});Q162=makeQuery(id+"F25.imprint","IMPRINT",FACE,{"disambiguationData":[TD([[makeQuery(id+"F25.imprint","IMPRINT",EDGE,{"disambiguationData":[TD([[subQ2,-1.0]])],"derivedFrom":subQ1}),-1.0]])]});}
            var Q163;
            {var subQ0=sQuery(id+"F25.wireOp",EDGE,"E386.MirrorCS");var subQ1=sQuery(id+"F25.wireOp",EDGE,"E347.MirrorCS");var subQ2=makeQuery(id+"F25.imprint","INTERSECT",VERTEX,{"derivedFrom":[subQ1,subQ0]});Q163=makeQuery(id+"F25.imprint","IMPRINT",FACE,{"disambiguationData":[TD([[makeQuery(id+"F25.imprint","IMPRINT",EDGE,{"disambiguationData":[TD([[subQ2,-1.0]])],"derivedFrom":subQ1}),-1.0]])]});}
            var Q164;
            {var subQ0=sQuery(id+"F25.wireOp",EDGE,"E386.MirrorCS");var subQ1=sQuery(id+"F25.wireOp",EDGE,"E347.MirrorCS");var subQ2=makeQuery(id+"F25.imprint","INTERSECT",VERTEX,{"derivedFrom":[subQ1,subQ0]});Q164=makeQuery(id+"F25.imprint","IMPRINT",FACE,{"disambiguationData":[TD([[makeQuery(id+"F25.imprint","IMPRINT",EDGE,{"disambiguationData":[TD([[subQ2,-1.0]])],"derivedFrom":subQ1}),1.0]])]});}
            var Q165;
            {var subQ0=sQuery(id+"F25.wireOp",EDGE,"E334.MirrorCS");var subQ1=sQuery(id+"F25.wireOp",EDGE,"E347.MirrorCS");var subQ2=makeQuery(id+"F25.imprint","INTERSECT",VERTEX,{"derivedFrom":[subQ1,subQ0]});Q165=makeQuery(id+"F25.imprint","IMPRINT",FACE,{"disambiguationData":[TD([[makeQuery(id+"F25.imprint","IMPRINT",EDGE,{"disambiguationData":[TD([[subQ2,-1.0]])],"derivedFrom":subQ1}),1.0]])]});}
            var Q166;
            {var subQ0=sQuery(id+"F25.wireOp",EDGE,"E237.right");Q166=makeQuery(id+"F25.imprint","IMPRINT",FACE,{"disambiguationData":[TD([[makeQuery(id+"F25.imprint","IMPRINT",EDGE,{"derivedFrom":subQ0}),-1.0]])]});}
            var Q167;
            {var subQ0=sQuery(id+"F25.wireOp",EDGE,"E238.right");Q167=makeQuery(id+"F25.imprint","IMPRINT",FACE,{"disambiguationData":[TD([[makeQuery(id+"F25.imprint","IMPRINT",EDGE,{"derivedFrom":subQ0}),1.0]])]});}
            var Q168;
            {var subQ0=sQuery(id+"F25.wireOp",EDGE,"E236.right");Q168=makeQuery(id+"F25.imprint","IMPRINT",FACE,{"disambiguationData":[TD([[makeQuery(id+"F25.imprint","IMPRINT",EDGE,{"derivedFrom":subQ0}),1.0]])]});}
            var Q169;
            {var subQ0=sQuery(id+"F25.wireOp",EDGE,"E365.MirrorCS");var subQ1=sQuery(id+"F25.wireOp",EDGE,"E344.MirrorCS");var subQ2=makeQuery(id+"F25.imprint","INTERSECT",VERTEX,{"derivedFrom":[subQ1,subQ0]});Q169=makeQuery(id+"F25.imprint","IMPRINT",FACE,{"disambiguationData":[TD([[makeQuery(id+"F25.imprint","IMPRINT",EDGE,{"disambiguationData":[TD([[subQ2,-1.0]])],"derivedFrom":subQ1}),1.0]])]});}
            var Q170;
            {var subQ5=sQuery(id+"F25.wireOp",EDGE,"E237.right");Q170=makeQuery(id+"F25.imprint","IMPRINT",FACE,{"disambiguationData":[TD([[makeQuery(id+"F25.imprint","IMPRINT",EDGE,{"derivedFrom":subQ5}),1.0]])]});}
            var Q171;
            {var subQ5=sQuery(id+"F25.wireOp",EDGE,"E238.right");Q171=makeQuery(id+"F25.imprint","IMPRINT",FACE,{"disambiguationData":[TD([[makeQuery(id+"F25.imprint","IMPRINT",EDGE,{"derivedFrom":subQ5}),-1.0]])]});}
            var Q172;
            {var subQ0=sQuery(id+"F25.wireOp",EDGE,"E295.trimOffspring");var subQ1=sQuery(id+"F25.wireOp",EDGE,"E249.right");var subQ2=makeQuery(id+"F25.imprint","INTERSECT",VERTEX,{"derivedFrom":[subQ1,subQ0]});Q172=makeQuery(id+"F25.imprint","IMPRINT",FACE,{"disambiguationData":[TD([[makeQuery(id+"F25.imprint","IMPRINT",EDGE,{"disambiguationData":[TD([[subQ2,-1.0]])],"derivedFrom":subQ1}),1.0]])]});}
            var Q173;
            {var subQ0=sQuery(id+"F25.wireOp",EDGE,"E296.trimOffspring");var subQ1=sQuery(id+"F25.wireOp",EDGE,"E249.right");var subQ2=makeQuery(id+"F25.imprint","INTERSECT",VERTEX,{"derivedFrom":[subQ1,subQ0]});Q173=makeQuery(id+"F25.imprint","IMPRINT",FACE,{"disambiguationData":[TD([[makeQuery(id+"F25.imprint","IMPRINT",EDGE,{"disambiguationData":[TD([[subQ2,-1.0]])],"derivedFrom":subQ1}),1.0]])]});}
            var Q174;
            {var subQ0=sQuery(id+"F25.wireOp",EDGE,"E296.trimOffspring");var subQ1=sQuery(id+"F25.wireOp",EDGE,"E250.right");var subQ2=makeQuery(id+"F25.imprint","INTERSECT",VERTEX,{"derivedFrom":[subQ1,subQ0]});Q174=makeQuery(id+"F25.imprint","IMPRINT",FACE,{"disambiguationData":[TD([[makeQuery(id+"F25.imprint","IMPRINT",EDGE,{"disambiguationData":[TD([[subQ2,-1.0]])],"derivedFrom":subQ1}),1.0]])]});}
            var Q175;
            {var subQ0=sQuery(id+"F25.wireOp",EDGE,"E296.trimOffspring");var subQ1=sQuery(id+"F25.wireOp",EDGE,"E250.left");var subQ2=makeQuery(id+"F25.imprint","INTERSECT",VERTEX,{"derivedFrom":[subQ1,subQ0]});Q175=makeQuery(id+"F25.imprint","IMPRINT",FACE,{"disambiguationData":[TD([[makeQuery(id+"F25.imprint","IMPRINT",EDGE,{"disambiguationData":[TD([[subQ2,-1.0]])],"derivedFrom":subQ1}),1.0]])]});}
            var Q176;
            {var subQ0=sQuery(id+"F25.wireOp",EDGE,"E295.trimOffspring");var subQ1=sQuery(id+"F25.wireOp",EDGE,"E250.left");var subQ2=makeQuery(id+"F25.imprint","INTERSECT",VERTEX,{"derivedFrom":[subQ1,subQ0]});Q176=makeQuery(id+"F25.imprint","IMPRINT",FACE,{"disambiguationData":[TD([[makeQuery(id+"F25.imprint","IMPRINT",EDGE,{"disambiguationData":[TD([[subQ2,-1.0]])],"derivedFrom":subQ1}),1.0]])]});}
            var Q177;
            {var subQ0=sQuery(id+"F25.wireOp",EDGE,"E295.trimOffspring");var subQ1=sQuery(id+"F25.wireOp",EDGE,"E250.right");var subQ2=makeQuery(id+"F25.imprint","INTERSECT",VERTEX,{"derivedFrom":[subQ1,subQ0]});Q177=makeQuery(id+"F25.imprint","IMPRINT",FACE,{"disambiguationData":[TD([[makeQuery(id+"F25.imprint","IMPRINT",EDGE,{"disambiguationData":[TD([[subQ2,-1.0]])],"derivedFrom":subQ1}),1.0]])]});}
            var Q178;
            {var subQ0=sQuery(id+"F25.wireOp",EDGE,"E251.bottom");Q178=makeQuery(id+"F25.imprint","IMPRINT",FACE,{"disambiguationData":[TD([[makeQuery(id+"F25.imprint","IMPRINT",EDGE,{"derivedFrom":subQ0}),-1.0]])]});}
            var Q179;
            {var subQ0=sQuery(id+"F25.wireOp",EDGE,"E250.bottom");Q179=makeQuery(id+"F25.imprint","IMPRINT",FACE,{"disambiguationData":[TD([[makeQuery(id+"F25.imprint","IMPRINT",EDGE,{"derivedFrom":subQ0}),1.0]])]});}
            var Q180;
            {var subQ0=sQuery(id+"F25.wireOp",EDGE,"E288.trimOffspring");var subQ1=sQuery(id+"F25.wireOp",EDGE,"E250.left");var subQ2=makeQuery(id+"F25.imprint","INTERSECT",VERTEX,{"derivedFrom":[subQ1,subQ0]});Q180=makeQuery(id+"F25.imprint","IMPRINT",FACE,{"disambiguationData":[TD([[makeQuery(id+"F25.imprint","IMPRINT",EDGE,{"disambiguationData":[TD([[subQ2,-1.0]])],"derivedFrom":subQ1}),1.0]])]});}
            var Q181;
            {var subQ0=sQuery(id+"F25.wireOp",EDGE,"E292.trimOffspring");var subQ1=sQuery(id+"F25.wireOp",EDGE,"E250.left");var subQ2=makeQuery(id+"F25.imprint","INTERSECT",VERTEX,{"derivedFrom":[subQ1,subQ0]});Q181=makeQuery(id+"F25.imprint","IMPRINT",FACE,{"disambiguationData":[TD([[makeQuery(id+"F25.imprint","IMPRINT",EDGE,{"disambiguationData":[TD([[subQ2,-1.0]])],"derivedFrom":subQ1}),1.0]])]});}
            var Q182;
            {var subQ0=sQuery(id+"F25.wireOp",EDGE,"E288.trimOffspring");var subQ1=sQuery(id+"F25.wireOp",EDGE,"E250.right");var subQ2=makeQuery(id+"F25.imprint","INTERSECT",VERTEX,{"derivedFrom":[subQ1,subQ0]});Q182=makeQuery(id+"F25.imprint","IMPRINT",FACE,{"disambiguationData":[TD([[makeQuery(id+"F25.imprint","IMPRINT",EDGE,{"disambiguationData":[TD([[subQ2,-1.0]])],"derivedFrom":subQ1}),1.0]])]});}
            var Q183;
            {var subQ0=sQuery(id+"F25.wireOp",EDGE,"E292.trimOffspring");var subQ1=sQuery(id+"F25.wireOp",EDGE,"E250.right");var subQ2=makeQuery(id+"F25.imprint","INTERSECT",VERTEX,{"derivedFrom":[subQ1,subQ0]});Q183=makeQuery(id+"F25.imprint","IMPRINT",FACE,{"disambiguationData":[TD([[makeQuery(id+"F25.imprint","IMPRINT",EDGE,{"disambiguationData":[TD([[subQ2,-1.0]])],"derivedFrom":subQ1}),1.0]])]});}
            var Q184;
            {var subQ0=sQuery(id+"F25.wireOp",EDGE,"E288.trimOffspring");var subQ1=sQuery(id+"F25.wireOp",EDGE,"E249.right");var subQ2=makeQuery(id+"F25.imprint","INTERSECT",VERTEX,{"derivedFrom":[subQ1,subQ0]});Q184=makeQuery(id+"F25.imprint","IMPRINT",FACE,{"disambiguationData":[TD([[makeQuery(id+"F25.imprint","IMPRINT",EDGE,{"disambiguationData":[TD([[subQ2,-1.0]])],"derivedFrom":subQ1}),1.0]])]});}
            var Q185;
            {var subQ0=sQuery(id+"F25.wireOp",EDGE,"E292.trimOffspring");var subQ1=sQuery(id+"F25.wireOp",EDGE,"E249.right");var subQ2=makeQuery(id+"F25.imprint","INTERSECT",VERTEX,{"derivedFrom":[subQ1,subQ0]});Q185=makeQuery(id+"F25.imprint","IMPRINT",FACE,{"disambiguationData":[TD([[makeQuery(id+"F25.imprint","IMPRINT",EDGE,{"disambiguationData":[TD([[subQ2,-1.0]])],"derivedFrom":subQ1}),1.0]])]});}
            var Q186;
            {var subQ5=sQuery(id+"F25.wireOp",EDGE,"E242.right");Q186=makeQuery(id+"F25.imprint","IMPRINT",FACE,{"disambiguationData":[TD([[makeQuery(id+"F25.imprint","IMPRINT",EDGE,{"derivedFrom":subQ5}),-1.0]])]});}
            var Q187;
            {var subQ0=sQuery(id+"F25.wireOp",EDGE,"E242.right");Q187=makeQuery(id+"F25.imprint","IMPRINT",FACE,{"disambiguationData":[TD([[makeQuery(id+"F25.imprint","IMPRINT",EDGE,{"derivedFrom":subQ0}),1.0]])]});}
            var Q188;
            {var subQ5=sQuery(id+"F25.wireOp",EDGE,"E241.right");Q188=makeQuery(id+"F25.imprint","IMPRINT",FACE,{"disambiguationData":[TD([[makeQuery(id+"F25.imprint","IMPRINT",EDGE,{"derivedFrom":subQ5}),1.0]])]});}
            var Q189;
            {var subQ0=sQuery(id+"F25.wireOp",EDGE,"E241.right");Q189=makeQuery(id+"F25.imprint","IMPRINT",FACE,{"disambiguationData":[TD([[makeQuery(id+"F25.imprint","IMPRINT",EDGE,{"derivedFrom":subQ0}),-1.0]])]});}
            var Q190;
            {var subQ0=sQuery(id+"F25.wireOp",EDGE,"E365.MirrorCS");var subQ1=sQuery(id+"F25.wireOp",EDGE,"E341.MirrorCS");var subQ2=makeQuery(id+"F25.imprint","INTERSECT",VERTEX,{"derivedFrom":[subQ1,subQ0]});Q190=makeQuery(id+"F25.imprint","IMPRINT",FACE,{"disambiguationData":[TD([[makeQuery(id+"F25.imprint","IMPRINT",EDGE,{"disambiguationData":[TD([[subQ2,-1.0]])],"derivedFrom":subQ1}),-1.0]])]});}
            var Q191;
            {var subQ0=sQuery(id+"F25.wireOp",EDGE,"E356.MirrorCS");var subQ1=sQuery(id+"F25.wireOp",EDGE,"E365.MirrorCS");var subQ2=makeQuery(id+"F25.imprint","INTERSECT",VERTEX,{"derivedFrom":[subQ1,subQ0]});Q191=makeQuery(id+"F25.imprint","IMPRINT",FACE,{"disambiguationData":[TD([[makeQuery(id+"F25.imprint","IMPRINT",EDGE,{"disambiguationData":[TD([[subQ2,-1.0]])],"derivedFrom":subQ1}),1.0]])]});}
            var Q192;
            {var subQ0=sQuery(id+"F25.wireOp",EDGE,"E334.MirrorCS");var subQ1=sQuery(id+"F25.wireOp",EDGE,"E341.MirrorCS");var subQ2=makeQuery(id+"F25.imprint","INTERSECT",VERTEX,{"derivedFrom":[subQ1,subQ0]});Q192=makeQuery(id+"F25.imprint","IMPRINT",FACE,{"disambiguationData":[TD([[makeQuery(id+"F25.imprint","IMPRINT",EDGE,{"disambiguationData":[TD([[subQ2,-1.0]])],"derivedFrom":subQ1}),-1.0]])]});}
            var Q193;
            {var subQ0=sQuery(id+"F25.wireOp",EDGE,"E356.MirrorCS");var subQ1=sQuery(id+"F25.wireOp",EDGE,"E365.MirrorCS");var subQ2=makeQuery(id+"F25.imprint","INTERSECT",VERTEX,{"derivedFrom":[subQ1,subQ0]});Q193=makeQuery(id+"F25.imprint","IMPRINT",FACE,{"disambiguationData":[TD([[makeQuery(id+"F25.imprint","IMPRINT",EDGE,{"disambiguationData":[TD([[subQ2,-1.0]])],"derivedFrom":subQ1}),-1.0]])]});}
            var Q194;
            {var subQ0=sQuery(id+"F25.wireOp",EDGE,"E386.MirrorCS");var subQ1=sQuery(id+"F25.wireOp",EDGE,"E341.MirrorCS");var subQ2=makeQuery(id+"F25.imprint","INTERSECT",VERTEX,{"derivedFrom":[subQ1,subQ0]});Q194=makeQuery(id+"F25.imprint","IMPRINT",FACE,{"disambiguationData":[TD([[makeQuery(id+"F25.imprint","IMPRINT",EDGE,{"disambiguationData":[TD([[subQ2,-1.0]])],"derivedFrom":subQ1}),-1.0]])]});}
            var Q195;
            {var subQ0=sQuery(id+"F25.wireOp",EDGE,"E356.MirrorCS");var subQ1=sQuery(id+"F25.wireOp",EDGE,"E334.MirrorCS");var subQ2=makeQuery(id+"F25.imprint","INTERSECT",VERTEX,{"derivedFrom":[subQ1,subQ0]});Q195=makeQuery(id+"F25.imprint","IMPRINT",FACE,{"disambiguationData":[TD([[makeQuery(id+"F25.imprint","IMPRINT",EDGE,{"disambiguationData":[TD([[subQ2,-1.0]])],"derivedFrom":subQ1}),-1.0]])]});}
            var Q196;
            {var subQ0=sQuery(id+"F25.wireOp",EDGE,"E386.MirrorCS");var subQ1=sQuery(id+"F25.wireOp",EDGE,"E339.MirrorCS");var subQ2=makeQuery(id+"F25.imprint","INTERSECT",VERTEX,{"derivedFrom":[subQ1,subQ0]});Q196=makeQuery(id+"F25.imprint","IMPRINT",FACE,{"disambiguationData":[TD([[makeQuery(id+"F25.imprint","IMPRINT",EDGE,{"disambiguationData":[TD([[subQ2,-1.0]])],"derivedFrom":subQ1}),1.0]])]});}
            var Q197;
            {var subQ0=sQuery(id+"F25.wireOp",EDGE,"E334.MirrorCS");var subQ1=sQuery(id+"F25.wireOp",EDGE,"E339.MirrorCS");var subQ2=makeQuery(id+"F25.imprint","INTERSECT",VERTEX,{"derivedFrom":[subQ1,subQ0]});Q197=makeQuery(id+"F25.imprint","IMPRINT",FACE,{"disambiguationData":[TD([[makeQuery(id+"F25.imprint","IMPRINT",EDGE,{"disambiguationData":[TD([[subQ2,-1.0]])],"derivedFrom":subQ1}),1.0]])]});}
            var Q198;
            {var subQ0=sQuery(id+"F25.wireOp",EDGE,"E334.MirrorCS");var subQ1=sQuery(id+"F25.wireOp",EDGE,"E339.MirrorCS");var subQ2=makeQuery(id+"F25.imprint","INTERSECT",VERTEX,{"derivedFrom":[subQ1,subQ0]});Q198=makeQuery(id+"F25.imprint","IMPRINT",FACE,{"disambiguationData":[TD([[makeQuery(id+"F25.imprint","IMPRINT",EDGE,{"disambiguationData":[TD([[subQ2,-1.0]])],"derivedFrom":subQ1}),-1.0]])]});}
            var Q199;
            {var subQ0=sQuery(id+"F25.wireOp",EDGE,"E361.MirrorCS");var subQ1=sQuery(id+"F25.wireOp",EDGE,"E365.MirrorCS");var subQ2=makeQuery(id+"F25.imprint","INTERSECT",VERTEX,{"derivedFrom":[subQ1,subQ0]});Q199=makeQuery(id+"F25.imprint","IMPRINT",FACE,{"disambiguationData":[TD([[makeQuery(id+"F25.imprint","IMPRINT",EDGE,{"disambiguationData":[TD([[subQ2,-1.0]])],"derivedFrom":subQ1}),-1.0]])]});}
            var Q200;
            {var subQ0=sQuery(id+"F25.wireOp",EDGE,"E361.MirrorCS");var subQ1=sQuery(id+"F25.wireOp",EDGE,"E334.MirrorCS");var subQ2=makeQuery(id+"F25.imprint","INTERSECT",VERTEX,{"derivedFrom":[subQ1,subQ0]});Q200=makeQuery(id+"F25.imprint","IMPRINT",FACE,{"disambiguationData":[TD([[makeQuery(id+"F25.imprint","IMPRINT",EDGE,{"disambiguationData":[TD([[subQ2,-1.0]])],"derivedFrom":subQ1}),-1.0]])]});}
            var Q201;
            {var subQ0=sQuery(id+"F25.wireOp",EDGE,"E386.MirrorCS");var subQ1=sQuery(id+"F25.wireOp",EDGE,"E339.MirrorCS");var subQ2=makeQuery(id+"F25.imprint","INTERSECT",VERTEX,{"derivedFrom":[subQ1,subQ0]});Q201=makeQuery(id+"F25.imprint","IMPRINT",FACE,{"disambiguationData":[TD([[makeQuery(id+"F25.imprint","IMPRINT",EDGE,{"disambiguationData":[TD([[subQ2,-1.0]])],"derivedFrom":subQ1}),-1.0]])]});}
            var Q202;
            {var subQ0=sQuery(id+"F25.wireOp",EDGE,"E361.MirrorCS");var subQ1=sQuery(id+"F25.wireOp",EDGE,"E365.MirrorCS");var subQ2=makeQuery(id+"F25.imprint","INTERSECT",VERTEX,{"derivedFrom":[subQ1,subQ0]});Q202=makeQuery(id+"F25.imprint","IMPRINT",FACE,{"disambiguationData":[TD([[makeQuery(id+"F25.imprint","IMPRINT",EDGE,{"disambiguationData":[TD([[subQ2,-1.0]])],"derivedFrom":subQ1}),1.0]])]});}
            var Q203;
            {var subQ0=sQuery(id+"F25.wireOp",EDGE,"E365.MirrorCS");var subQ1=sQuery(id+"F25.wireOp",EDGE,"E339.MirrorCS");var subQ2=makeQuery(id+"F25.imprint","INTERSECT",VERTEX,{"derivedFrom":[subQ1,subQ0]});Q203=makeQuery(id+"F25.imprint","IMPRINT",FACE,{"disambiguationData":[TD([[makeQuery(id+"F25.imprint","IMPRINT",EDGE,{"disambiguationData":[TD([[subQ2,-1.0]])],"derivedFrom":subQ1}),-1.0]])]});}
            var Q204;
            {var subQ0=sQuery(id+"F25.wireOp",EDGE,"E386.MirrorCS");var subQ1=sQuery(id+"F25.wireOp",EDGE,"E339.MirrorCS");var subQ2=makeQuery(id+"F25.imprint","INTERSECT",VERTEX,{"derivedFrom":[subQ1,subQ0]});Q204=makeQuery(id+"F25.imprint","IMPRINT",FACE,{"disambiguationData":[TD([[makeQuery(id+"F25.imprint","IMPRINT",EDGE,{"disambiguationData":[TD([[subQ2,-1.0]])],"derivedFrom":subQ1}),-1.0]])]});}
            var Q205;
            {var subQ0=sQuery(id+"F25.wireOp",EDGE,"E240.right");Q205=makeQuery(id+"F25.imprint","IMPRINT",FACE,{"disambiguationData":[TD([[makeQuery(id+"F25.imprint","IMPRINT",EDGE,{"derivedFrom":subQ0}),1.0]])]});}
            var Q206;
            {var subQ0=sQuery(id+"F25.wireOp",EDGE,"E239.right");Q206=makeQuery(id+"F25.imprint","IMPRINT",FACE,{"disambiguationData":[TD([[makeQuery(id+"F25.imprint","IMPRINT",EDGE,{"derivedFrom":subQ0}),-1.0]])]});}
            var Q207;
            {var subQ5=sQuery(id+"F25.wireOp",EDGE,"E239.right");Q207=makeQuery(id+"F25.imprint","IMPRINT",FACE,{"disambiguationData":[TD([[makeQuery(id+"F25.imprint","IMPRINT",EDGE,{"derivedFrom":subQ5}),1.0]])]});}
            var Q208;
            {var subQ5=sQuery(id+"F25.wireOp",EDGE,"E240.right");Q208=makeQuery(id+"F25.imprint","IMPRINT",FACE,{"disambiguationData":[TD([[makeQuery(id+"F25.imprint","IMPRINT",EDGE,{"derivedFrom":subQ5}),-1.0]])]});}
            var Q209;
            {var subQ0=sQuery(id+"F25.wireOp",EDGE,"E293.trimOffspring");var subQ1=sQuery(id+"F25.wireOp",EDGE,"E249.right");var subQ2=makeQuery(id+"F25.imprint","INTERSECT",VERTEX,{"derivedFrom":[subQ1,subQ0]});Q209=makeQuery(id+"F25.imprint","IMPRINT",FACE,{"disambiguationData":[TD([[makeQuery(id+"F25.imprint","IMPRINT",EDGE,{"disambiguationData":[TD([[subQ2,-1.0]])],"derivedFrom":subQ1}),1.0]])]});}
            var Q210;
            {var subQ0=sQuery(id+"F25.wireOp",EDGE,"E297.trimOffspring");var subQ1=sQuery(id+"F25.wireOp",EDGE,"E249.right");var subQ2=makeQuery(id+"F25.imprint","INTERSECT",VERTEX,{"derivedFrom":[subQ1,subQ0]});Q210=makeQuery(id+"F25.imprint","IMPRINT",FACE,{"disambiguationData":[TD([[makeQuery(id+"F25.imprint","IMPRINT",EDGE,{"disambiguationData":[TD([[subQ2,-1.0]])],"derivedFrom":subQ1}),1.0]])]});}
            var Q211;
            {var subQ0=sQuery(id+"F25.wireOp",EDGE,"E297.trimOffspring");var subQ1=sQuery(id+"F25.wireOp",EDGE,"E250.right");var subQ2=makeQuery(id+"F25.imprint","INTERSECT",VERTEX,{"derivedFrom":[subQ1,subQ0]});Q211=makeQuery(id+"F25.imprint","IMPRINT",FACE,{"disambiguationData":[TD([[makeQuery(id+"F25.imprint","IMPRINT",EDGE,{"disambiguationData":[TD([[subQ2,-1.0]])],"derivedFrom":subQ1}),1.0]])]});}
            var Q212;
            {var subQ0=sQuery(id+"F25.wireOp",EDGE,"E297.trimOffspring");var subQ1=sQuery(id+"F25.wireOp",EDGE,"E250.left");var subQ2=makeQuery(id+"F25.imprint","INTERSECT",VERTEX,{"derivedFrom":[subQ1,subQ0]});Q212=makeQuery(id+"F25.imprint","IMPRINT",FACE,{"disambiguationData":[TD([[makeQuery(id+"F25.imprint","IMPRINT",EDGE,{"disambiguationData":[TD([[subQ2,-1.0]])],"derivedFrom":subQ1}),1.0]])]});}
            var Q213;
            {var subQ0=sQuery(id+"F25.wireOp",EDGE,"E293.trimOffspring");var subQ1=sQuery(id+"F25.wireOp",EDGE,"E250.left");var subQ2=makeQuery(id+"F25.imprint","INTERSECT",VERTEX,{"derivedFrom":[subQ1,subQ0]});Q213=makeQuery(id+"F25.imprint","IMPRINT",FACE,{"disambiguationData":[TD([[makeQuery(id+"F25.imprint","IMPRINT",EDGE,{"disambiguationData":[TD([[subQ2,-1.0]])],"derivedFrom":subQ1}),1.0]])]});}
            var Q214;
            {var subQ0=sQuery(id+"F25.wireOp",EDGE,"E293.trimOffspring");var subQ1=sQuery(id+"F25.wireOp",EDGE,"E250.right");var subQ2=makeQuery(id+"F25.imprint","INTERSECT",VERTEX,{"derivedFrom":[subQ1,subQ0]});Q214=makeQuery(id+"F25.imprint","IMPRINT",FACE,{"disambiguationData":[TD([[makeQuery(id+"F25.imprint","IMPRINT",EDGE,{"disambiguationData":[TD([[subQ2,-1.0]])],"derivedFrom":subQ1}),1.0]])]});}
            var Q215;
            {var subQ0=sQuery(id+"F25.wireOp",EDGE,"E232.left");Q215=makeQuery(id+"F25.imprint","IMPRINT",FACE,{"disambiguationData":[TD([[makeQuery(id+"F25.imprint","IMPRINT",EDGE,{"derivedFrom":subQ0}),-1.0]])]});}
            var Q216;
            {var subQ0=sQuery(id+"F25.wireOp",EDGE,"E255.trimOffspring");var subQ1=sQuery(id+"F25.wireOp",EDGE,"E232.top");var subQ2=makeQuery(id+"F25.imprint","INTERSECT",VERTEX,{"derivedFrom":[subQ1,subQ0]});Q216=makeQuery(id+"F25.imprint","IMPRINT",FACE,{"disambiguationData":[TD([[makeQuery(id+"F25.imprint","IMPRINT",EDGE,{"disambiguationData":[TD([[subQ2,-1.0]])],"derivedFrom":subQ1}),-1.0]])]});}
            var Q217;
            {var subQ1=sQuery(id+"F25.wireOp",EDGE,"E232.top");var subQ3=sQuery(id+"F25.wireOp",EDGE,"E256.trimOffspring");var subQ4=makeQuery(id+"F25.imprint","INTERSECT",VERTEX,{"derivedFrom":[subQ1,subQ3]});Q217=makeQuery(id+"F25.imprint","IMPRINT",FACE,{"disambiguationData":[TD([[makeQuery(id+"F25.imprint","IMPRINT",EDGE,{"disambiguationData":[TD([[subQ4,1.0]])],"derivedFrom":subQ3}),-1.0]])]});}
            var Q218;
            {var subQ1=sQuery(id+"F25.wireOp",EDGE,"E234.bottom");var subQ3=sQuery(id+"F25.wireOp",EDGE,"E256.trimOffspring");var subQ4=makeQuery(id+"F25.imprint","INTERSECT",VERTEX,{"derivedFrom":[subQ1,subQ3]});Q218=makeQuery(id+"F25.imprint","IMPRINT",FACE,{"disambiguationData":[TD([[makeQuery(id+"F25.imprint","IMPRINT",EDGE,{"disambiguationData":[TD([[subQ4,1.0]])],"derivedFrom":subQ3}),-1.0]])]});}
            var Q219;
            {var subQ0=sQuery(id+"F25.wireOp",EDGE,"E254.trimOffspring");var subQ5=sQuery(id+"F25.wireOp",EDGE,"E253.top");var subQ6=makeQuery(id+"F25.imprint","INTERSECT",VERTEX,{"derivedFrom":[subQ5,subQ0]});Q219=makeQuery(id+"F25.imprint","IMPRINT",FACE,{"disambiguationData":[TD([[makeQuery(id+"F25.imprint","IMPRINT",EDGE,{"disambiguationData":[TD([[subQ6,1.0]])],"derivedFrom":subQ5}),1.0]])]});}
            var Q220;
            {var subQ0=sQuery(id+"F25.wireOp",EDGE,"E254.trimOffspring");var subQ1=sQuery(id+"F25.wireOp",EDGE,"E253.bottom");var subQ2=makeQuery(id+"F25.imprint","INTERSECT",VERTEX,{"derivedFrom":[subQ1,subQ0]});Q220=makeQuery(id+"F25.imprint","IMPRINT",FACE,{"disambiguationData":[TD([[makeQuery(id+"F25.imprint","IMPRINT",EDGE,{"disambiguationData":[TD([[subQ2,1.0]])],"derivedFrom":subQ1}),1.0]])]});}
            var Q221;
            {var subQ0=sQuery(id+"F25.wireOp",EDGE,"E254.trimOffspring");var subQ1=sQuery(id+"F25.wireOp",EDGE,"E252.top");var subQ2=makeQuery(id+"F25.imprint","INTERSECT",VERTEX,{"derivedFrom":[subQ1,subQ0]});Q221=makeQuery(id+"F25.imprint","IMPRINT",FACE,{"disambiguationData":[TD([[makeQuery(id+"F25.imprint","IMPRINT",EDGE,{"disambiguationData":[TD([[subQ2,1.0]])],"derivedFrom":subQ1}),1.0]])]});}
            var Q222;
            {var subQ0=sQuery(id+"F25.wireOp",EDGE,"E256.trimOffspring");var subQ1=sQuery(id+"F25.wireOp",EDGE,"E235.top");var subQ2=makeQuery(id+"F25.imprint","INTERSECT",VERTEX,{"derivedFrom":[subQ1,subQ0]});Q222=makeQuery(id+"F25.imprint","IMPRINT",FACE,{"disambiguationData":[TD([[makeQuery(id+"F25.imprint","IMPRINT",EDGE,{"disambiguationData":[TD([[subQ2,-1.0]])],"derivedFrom":subQ1}),1.0]])]});}
            var Q223;
            {var subQ0=sQuery(id+"F25.wireOp",EDGE,"E256.trimOffspring");var subQ1=sQuery(id+"F25.wireOp",EDGE,"E235.top");var subQ2=makeQuery(id+"F25.imprint","INTERSECT",VERTEX,{"derivedFrom":[subQ1,subQ0]});Q223=makeQuery(id+"F25.imprint","IMPRINT",FACE,{"disambiguationData":[TD([[makeQuery(id+"F25.imprint","IMPRINT",EDGE,{"disambiguationData":[TD([[subQ2,-1.0]])],"derivedFrom":subQ1}),-1.0]])]});}
            var Q224;
            {var subQ0=sQuery(id+"F25.wireOp",EDGE,"E254.trimOffspring");var subQ1=sQuery(id+"F25.wireOp",EDGE,"E235.top");var subQ2=makeQuery(id+"F25.imprint","INTERSECT",VERTEX,{"derivedFrom":[subQ1,subQ0]});Q224=makeQuery(id+"F25.imprint","IMPRINT",FACE,{"disambiguationData":[TD([[makeQuery(id+"F25.imprint","IMPRINT",EDGE,{"disambiguationData":[TD([[subQ2,-1.0]])],"derivedFrom":subQ1}),-1.0]])]});}
            var Q225;
            {var subQ0=sQuery(id+"F25.wireOp",EDGE,"E257.trimOffspring");var subQ1=sQuery(id+"F25.wireOp",EDGE,"E235.top");var subQ2=makeQuery(id+"F25.imprint","INTERSECT",VERTEX,{"derivedFrom":[subQ1,subQ0]});Q225=makeQuery(id+"F25.imprint","IMPRINT",FACE,{"disambiguationData":[TD([[makeQuery(id+"F25.imprint","IMPRINT",EDGE,{"disambiguationData":[TD([[subQ2,-1.0]])],"derivedFrom":subQ1}),-1.0]])]});}
            var Q226;
            {var subQ0=sQuery(id+"F25.wireOp",EDGE,"E259.trimOffspring");var subQ1=sQuery(id+"F25.wireOp",EDGE,"E235.top");var subQ2=makeQuery(id+"F25.imprint","INTERSECT",VERTEX,{"derivedFrom":[subQ1,subQ0]});Q226=makeQuery(id+"F25.imprint","IMPRINT",FACE,{"disambiguationData":[TD([[makeQuery(id+"F25.imprint","IMPRINT",EDGE,{"disambiguationData":[TD([[subQ2,-1.0]])],"derivedFrom":subQ1}),-1.0]])]});}
            var Q227;
            {var subQ1=sQuery(id+"F25.wireOp",EDGE,"E235.top");var subQ3=sQuery(id+"F25.wireOp",EDGE,"E258.trimOffspring");var subQ4=makeQuery(id+"F25.imprint","INTERSECT",VERTEX,{"derivedFrom":[subQ1,subQ3]});Q227=makeQuery(id+"F25.imprint","IMPRINT",FACE,{"disambiguationData":[TD([[makeQuery(id+"F25.imprint","IMPRINT",EDGE,{"disambiguationData":[TD([[subQ4,1.0]])],"derivedFrom":subQ3}),-1.0]])]});}
            var Q228;
            {var subQ0=sQuery(id+"F25.wireOp",EDGE,"E257.trimOffspring");var subQ1=sQuery(id+"F25.wireOp",EDGE,"E235.top");var subQ2=makeQuery(id+"F25.imprint","INTERSECT",VERTEX,{"derivedFrom":[subQ1,subQ0]});Q228=makeQuery(id+"F25.imprint","IMPRINT",FACE,{"disambiguationData":[TD([[makeQuery(id+"F25.imprint","IMPRINT",EDGE,{"disambiguationData":[TD([[subQ2,-1.0]])],"derivedFrom":subQ1}),1.0]])]});}
            var Q229;
            {var subQ0=sQuery(id+"F25.wireOp",EDGE,"E259.trimOffspring");var subQ1=sQuery(id+"F25.wireOp",EDGE,"E235.top");var subQ2=makeQuery(id+"F25.imprint","INTERSECT",VERTEX,{"derivedFrom":[subQ1,subQ0]});Q229=makeQuery(id+"F25.imprint","IMPRINT",FACE,{"disambiguationData":[TD([[makeQuery(id+"F25.imprint","IMPRINT",EDGE,{"disambiguationData":[TD([[subQ2,-1.0]])],"derivedFrom":subQ1}),1.0]])]});}
            var Q230;
            {var subQ0=sQuery(id+"F25.wireOp",EDGE,"E499.trimOffspring");var subQ1=sQuery(id+"F25.wireOp",EDGE,"E257.trimOffspring");var subQ2=makeQuery(id+"F25.imprint","INTERSECT",VERTEX,{"derivedFrom":[subQ1,subQ0]});Q230=makeQuery(id+"F25.imprint","IMPRINT",FACE,{"disambiguationData":[TD([[makeQuery(id+"F25.imprint","IMPRINT",EDGE,{"disambiguationData":[TD([[subQ2,1.0]])],"derivedFrom":subQ1}),-1.0]])]});}
            var Q231;
            {var subQ0=sQuery(id+"F25.wireOp",EDGE,"E499.trimOffspring");var subQ1=sQuery(id+"F25.wireOp",EDGE,"E258.trimOffspring");var subQ2=makeQuery(id+"F25.imprint","INTERSECT",VERTEX,{"derivedFrom":[subQ1,subQ0]});Q231=makeQuery(id+"F25.imprint","IMPRINT",FACE,{"disambiguationData":[TD([[makeQuery(id+"F25.imprint","IMPRINT",EDGE,{"disambiguationData":[TD([[subQ2,1.0]])],"derivedFrom":subQ1}),1.0]])]});}
            var Q232;
            {var subQ0=sQuery(id+"F25.wireOp",EDGE,"E499.trimOffspring");var subQ1=sQuery(id+"F25.wireOp",EDGE,"E257.trimOffspring");var subQ2=makeQuery(id+"F25.imprint","INTERSECT",VERTEX,{"derivedFrom":[subQ1,subQ0]});Q232=makeQuery(id+"F25.imprint","IMPRINT",FACE,{"disambiguationData":[TD([[makeQuery(id+"F25.imprint","IMPRINT",EDGE,{"disambiguationData":[TD([[subQ2,-1.0]])],"derivedFrom":subQ1}),-1.0]])]});}
            var Q233;
            {var subQ0=sQuery(id+"F25.wireOp",EDGE,"E499.trimOffspring");var subQ1=sQuery(id+"F25.wireOp",EDGE,"E258.trimOffspring");var subQ2=makeQuery(id+"F25.imprint","INTERSECT",VERTEX,{"derivedFrom":[subQ1,subQ0]});Q233=makeQuery(id+"F25.imprint","IMPRINT",FACE,{"disambiguationData":[TD([[makeQuery(id+"F25.imprint","IMPRINT",EDGE,{"disambiguationData":[TD([[subQ2,-1.0]])],"derivedFrom":subQ1}),1.0]])]});}
            var Q234;
            {var subQ3=sQuery(id+"F25.wireOp",EDGE,"E497.trimOffspring");var subQ5=sQuery(id+"F25.wireOp",EDGE,"E259.trimOffspring");var subQ6=makeQuery(id+"F25.imprint","INTERSECT",VERTEX,{"derivedFrom":[subQ5,subQ3]});Q234=makeQuery(id+"F25.imprint","IMPRINT",FACE,{"disambiguationData":[TD([[makeQuery(id+"F25.imprint","IMPRINT",EDGE,{"disambiguationData":[TD([[subQ6,-1.0]])],"derivedFrom":subQ5}),1.0]])]});}
            var Q235;
            {var subQ0=sQuery(id+"F25.wireOp",EDGE,"E497.trimOffspring");var subQ1=sQuery(id+"F25.wireOp",EDGE,"E258.trimOffspring");var subQ2=makeQuery(id+"F25.imprint","INTERSECT",VERTEX,{"derivedFrom":[subQ1,subQ0]});Q235=makeQuery(id+"F25.imprint","IMPRINT",FACE,{"disambiguationData":[TD([[makeQuery(id+"F25.imprint","IMPRINT",EDGE,{"disambiguationData":[TD([[subQ2,-1.0]])],"derivedFrom":subQ1}),1.0]])]});}
            var Q236;
            {var subQ3=sQuery(id+"F25.wireOp",EDGE,"E496.trimOffspring");var subQ5=sQuery(id+"F25.wireOp",EDGE,"E259.trimOffspring");var subQ6=makeQuery(id+"F25.imprint","INTERSECT",VERTEX,{"derivedFrom":[subQ5,subQ3]});Q236=makeQuery(id+"F25.imprint","IMPRINT",FACE,{"disambiguationData":[TD([[makeQuery(id+"F25.imprint","IMPRINT",EDGE,{"disambiguationData":[TD([[subQ6,1.0]])],"derivedFrom":subQ5}),1.0]])]});}
            var Q237;
            {var subQ0=sQuery(id+"F25.wireOp",EDGE,"E496.trimOffspring");var subQ1=sQuery(id+"F25.wireOp",EDGE,"E258.trimOffspring");var subQ2=makeQuery(id+"F25.imprint","INTERSECT",VERTEX,{"derivedFrom":[subQ1,subQ0]});Q237=makeQuery(id+"F25.imprint","IMPRINT",FACE,{"disambiguationData":[TD([[makeQuery(id+"F25.imprint","IMPRINT",EDGE,{"disambiguationData":[TD([[subQ2,1.0]])],"derivedFrom":subQ1}),1.0]])]});}
            var Q238;
            {var subQ3=sQuery(id+"F25.wireOp",EDGE,"E504.trimOffspring");var subQ5=sQuery(id+"F25.wireOp",EDGE,"E261.trimOffspring");var subQ6=makeQuery(id+"F25.imprint","INTERSECT",VERTEX,{"derivedFrom":[subQ5,subQ3]});Q238=makeQuery(id+"F25.imprint","IMPRINT",FACE,{"disambiguationData":[TD([[makeQuery(id+"F25.imprint","IMPRINT",EDGE,{"disambiguationData":[TD([[subQ6,-1.0]])],"derivedFrom":subQ5}),1.0]])]});}
            var Q239;
            {var subQ0=sQuery(id+"F25.wireOp",EDGE,"E504.trimOffspring");var subQ1=sQuery(id+"F25.wireOp",EDGE,"E260.trimOffspring");var subQ2=makeQuery(id+"F25.imprint","INTERSECT",VERTEX,{"derivedFrom":[subQ1,subQ0]});Q239=makeQuery(id+"F25.imprint","IMPRINT",FACE,{"disambiguationData":[TD([[makeQuery(id+"F25.imprint","IMPRINT",EDGE,{"disambiguationData":[TD([[subQ2,-1.0]])],"derivedFrom":subQ1}),1.0]])]});}
            var Q240;
            {var subQ0=sQuery(id+"F25.wireOp",EDGE,"E504.trimOffspring");var subQ1=sQuery(id+"F25.wireOp",EDGE,"E260.trimOffspring");var subQ2=makeQuery(id+"F25.imprint","INTERSECT",VERTEX,{"derivedFrom":[subQ1,subQ0]});Q240=makeQuery(id+"F25.imprint","IMPRINT",FACE,{"disambiguationData":[TD([[makeQuery(id+"F25.imprint","IMPRINT",EDGE,{"disambiguationData":[TD([[subQ2,-1.0]])],"derivedFrom":subQ1}),-1.0]])]});}
            var Q241;
            {var subQ0=sQuery(id+"F25.wireOp",EDGE,"E503.trimOffspring");var subQ5=sQuery(id+"F25.wireOp",EDGE,"E261.trimOffspring");var subQ6=makeQuery(id+"F25.imprint","INTERSECT",VERTEX,{"derivedFrom":[subQ5,subQ0]});Q241=makeQuery(id+"F25.imprint","IMPRINT",FACE,{"disambiguationData":[TD([[makeQuery(id+"F25.imprint","IMPRINT",EDGE,{"disambiguationData":[TD([[subQ6,-1.0]])],"derivedFrom":subQ5}),1.0]])]});}
            var Q242;
            {var subQ0=sQuery(id+"F25.wireOp",EDGE,"E505.trimOffspring");var subQ1=sQuery(id+"F25.wireOp",EDGE,"E260.trimOffspring");var subQ2=makeQuery(id+"F25.imprint","INTERSECT",VERTEX,{"derivedFrom":[subQ1,subQ0]});Q242=makeQuery(id+"F25.imprint","IMPRINT",FACE,{"disambiguationData":[TD([[makeQuery(id+"F25.imprint","IMPRINT",EDGE,{"disambiguationData":[TD([[subQ2,1.0]])],"derivedFrom":subQ1}),1.0]])]});}
            var Q243;
            {var subQ0=sQuery(id+"F25.wireOp",EDGE,"E505.trimOffspring");var subQ1=sQuery(id+"F25.wireOp",EDGE,"E262.trimOffspring");var subQ2=makeQuery(id+"F25.imprint","INTERSECT",VERTEX,{"derivedFrom":[subQ1,subQ0]});Q243=makeQuery(id+"F25.imprint","IMPRINT",FACE,{"disambiguationData":[TD([[makeQuery(id+"F25.imprint","IMPRINT",EDGE,{"disambiguationData":[TD([[subQ2,-1.0]])],"derivedFrom":subQ1}),-1.0]])]});}
            var Q244;
            {var subQ0=sQuery(id+"F25.wireOp",EDGE,"E505.trimOffspring");var subQ1=sQuery(id+"F25.wireOp",EDGE,"E260.trimOffspring");var subQ2=makeQuery(id+"F25.imprint","INTERSECT",VERTEX,{"derivedFrom":[subQ1,subQ0]});Q244=makeQuery(id+"F25.imprint","IMPRINT",FACE,{"disambiguationData":[TD([[makeQuery(id+"F25.imprint","IMPRINT",EDGE,{"disambiguationData":[TD([[subQ2,-1.0]])],"derivedFrom":subQ1}),1.0]])]});}
            var Q245;
            {var subQ0=sQuery(id+"F25.wireOp",EDGE,"E511.trimOffspring");var subQ1=sQuery(id+"F25.wireOp",EDGE,"E262.trimOffspring");var subQ2=makeQuery(id+"F25.imprint","INTERSECT",VERTEX,{"derivedFrom":[subQ1,subQ0]});Q245=makeQuery(id+"F25.imprint","IMPRINT",FACE,{"disambiguationData":[TD([[makeQuery(id+"F25.imprint","IMPRINT",EDGE,{"disambiguationData":[TD([[subQ2,1.0]])],"derivedFrom":subQ1}),-1.0]])]});}
            var Q246;
            {var subQ0=sQuery(id+"F25.wireOp",EDGE,"E511.trimOffspring");var subQ1=sQuery(id+"F25.wireOp",EDGE,"E260.trimOffspring");var subQ2=makeQuery(id+"F25.imprint","INTERSECT",VERTEX,{"derivedFrom":[subQ1,subQ0]});Q246=makeQuery(id+"F25.imprint","IMPRINT",FACE,{"disambiguationData":[TD([[makeQuery(id+"F25.imprint","IMPRINT",EDGE,{"disambiguationData":[TD([[subQ2,1.0]])],"derivedFrom":subQ1}),1.0]])]});}
            var Q247;
            {var subQ0=sQuery(id+"F25.wireOp",EDGE,"E511.trimOffspring");var subQ1=sQuery(id+"F25.wireOp",EDGE,"E262.trimOffspring");var subQ2=makeQuery(id+"F25.imprint","INTERSECT",VERTEX,{"derivedFrom":[subQ1,subQ0]});Q247=makeQuery(id+"F25.imprint","IMPRINT",FACE,{"disambiguationData":[TD([[makeQuery(id+"F25.imprint","IMPRINT",EDGE,{"disambiguationData":[TD([[subQ2,-1.0]])],"derivedFrom":subQ1}),-1.0]])]});}
            var Q248;
            {var subQ0=sQuery(id+"F25.wireOp",EDGE,"E497.trimOffspring");var subQ1=sQuery(id+"F25.wireOp",EDGE,"E260.trimOffspring");var subQ2=makeQuery(id+"F25.imprint","INTERSECT",VERTEX,{"derivedFrom":[subQ1,subQ0]});Q248=makeQuery(id+"F25.imprint","IMPRINT",FACE,{"disambiguationData":[TD([[makeQuery(id+"F25.imprint","IMPRINT",EDGE,{"disambiguationData":[TD([[subQ2,1.0]])],"derivedFrom":subQ1}),1.0]])]});}
            var Q249;
            {var subQ0=sQuery(id+"F25.wireOp",EDGE,"E497.trimOffspring");var subQ1=sQuery(id+"F25.wireOp",EDGE,"E262.trimOffspring");var subQ2=makeQuery(id+"F25.imprint","INTERSECT",VERTEX,{"derivedFrom":[subQ1,subQ0]});Q249=makeQuery(id+"F25.imprint","IMPRINT",FACE,{"disambiguationData":[TD([[makeQuery(id+"F25.imprint","IMPRINT",EDGE,{"disambiguationData":[TD([[subQ2,-1.0]])],"derivedFrom":subQ1}),-1.0]])]});}
            var Q250;
            {var subQ0=sQuery(id+"F25.wireOp",EDGE,"E497.trimOffspring");var subQ1=sQuery(id+"F25.wireOp",EDGE,"E260.trimOffspring");var subQ2=makeQuery(id+"F25.imprint","INTERSECT",VERTEX,{"derivedFrom":[subQ1,subQ0]});Q250=makeQuery(id+"F25.imprint","IMPRINT",FACE,{"disambiguationData":[TD([[makeQuery(id+"F25.imprint","IMPRINT",EDGE,{"disambiguationData":[TD([[subQ2,-1.0]])],"derivedFrom":subQ1}),1.0]])]});}
            var Q251;
            {var subQ0=sQuery(id+"F25.wireOp",EDGE,"E496.trimOffspring");var subQ1=sQuery(id+"F25.wireOp",EDGE,"E262.trimOffspring");var subQ2=makeQuery(id+"F25.imprint","INTERSECT",VERTEX,{"derivedFrom":[subQ1,subQ0]});Q251=makeQuery(id+"F25.imprint","IMPRINT",FACE,{"disambiguationData":[TD([[makeQuery(id+"F25.imprint","IMPRINT",EDGE,{"disambiguationData":[TD([[subQ2,1.0]])],"derivedFrom":subQ1}),-1.0]])]});}
            var Q252;
            {var subQ0=sQuery(id+"F25.wireOp",EDGE,"E496.trimOffspring");var subQ1=sQuery(id+"F25.wireOp",EDGE,"E260.trimOffspring");var subQ2=makeQuery(id+"F25.imprint","INTERSECT",VERTEX,{"derivedFrom":[subQ1,subQ0]});Q252=makeQuery(id+"F25.imprint","IMPRINT",FACE,{"disambiguationData":[TD([[makeQuery(id+"F25.imprint","IMPRINT",EDGE,{"disambiguationData":[TD([[subQ2,1.0]])],"derivedFrom":subQ1}),1.0]])]});}
            var Q253;
            {var subQ0=sQuery(id+"F25.wireOp",EDGE,"E529.trimOffspring");var subQ1=sQuery(id+"F25.wireOp",EDGE,"E503.trimOffspring");var subQ2=makeQuery(id+"F25.imprint","INTERSECT",VERTEX,{"derivedFrom":[subQ1,subQ0]});Q253=makeQuery(id+"F25.imprint","IMPRINT",FACE,{"disambiguationData":[TD([[makeQuery(id+"F25.imprint","IMPRINT",EDGE,{"disambiguationData":[TD([[subQ2,-1.0]])],"derivedFrom":subQ1}),-1.0]])]});}
            var Q254;
            {var subQ0=sQuery(id+"F25.wireOp",EDGE,"E529.trimOffspring");var subQ1=sQuery(id+"F25.wireOp",EDGE,"E503.trimOffspring");var subQ2=makeQuery(id+"F25.imprint","INTERSECT",VERTEX,{"derivedFrom":[subQ1,subQ0]});Q254=makeQuery(id+"F25.imprint","IMPRINT",FACE,{"disambiguationData":[TD([[makeQuery(id+"F25.imprint","IMPRINT",EDGE,{"disambiguationData":[TD([[subQ2,-1.0]])],"derivedFrom":subQ1}),1.0]])]});}
            var Q255;
            {var subQ0=sQuery(id+"F25.wireOp",EDGE,"E529.trimOffspring");var subQ1=sQuery(id+"F25.wireOp",EDGE,"E507.trimOffspring");var subQ2=makeQuery(id+"F25.imprint","INTERSECT",VERTEX,{"derivedFrom":[subQ1,subQ0]});Q255=makeQuery(id+"F25.imprint","IMPRINT",FACE,{"disambiguationData":[TD([[makeQuery(id+"F25.imprint","IMPRINT",EDGE,{"disambiguationData":[TD([[subQ2,-1.0]])],"derivedFrom":subQ1}),1.0]])]});}
            var Q256;
            {var subQ0=sQuery(id+"F25.wireOp",EDGE,"E529.trimOffspring");var subQ1=sQuery(id+"F25.wireOp",EDGE,"E510.trimOffspring");var subQ2=makeQuery(id+"F25.imprint","INTERSECT",VERTEX,{"derivedFrom":[subQ1,subQ0]});Q256=makeQuery(id+"F25.imprint","IMPRINT",FACE,{"disambiguationData":[TD([[makeQuery(id+"F25.imprint","IMPRINT",EDGE,{"disambiguationData":[TD([[subQ2,-1.0]])],"derivedFrom":subQ1}),-1.0]])]});}
            var Q257;
            {var subQ0=sQuery(id+"F25.wireOp",EDGE,"E530.trimOffspring");var subQ1=sQuery(id+"F25.wireOp",EDGE,"E510.trimOffspring");var subQ2=makeQuery(id+"F25.imprint","INTERSECT",VERTEX,{"derivedFrom":[subQ1,subQ0]});Q257=makeQuery(id+"F25.imprint","IMPRINT",FACE,{"disambiguationData":[TD([[makeQuery(id+"F25.imprint","IMPRINT",EDGE,{"disambiguationData":[TD([[subQ2,-1.0]])],"derivedFrom":subQ1}),-1.0]])]});}
            var Q258;
            {var subQ0=sQuery(id+"F25.wireOp",EDGE,"E531.trimOffspring");var subQ1=sQuery(id+"F25.wireOp",EDGE,"E510.trimOffspring");var subQ2=makeQuery(id+"F25.imprint","INTERSECT",VERTEX,{"derivedFrom":[subQ1,subQ0]});Q258=makeQuery(id+"F25.imprint","IMPRINT",FACE,{"disambiguationData":[TD([[makeQuery(id+"F25.imprint","IMPRINT",EDGE,{"disambiguationData":[TD([[subQ2,-1.0]])],"derivedFrom":subQ1}),-1.0]])]});}
            var Q259;
            {var subQ0=sQuery(id+"F25.wireOp",EDGE,"E532.trimOffspring");var subQ1=sQuery(id+"F25.wireOp",EDGE,"E510.trimOffspring");var subQ2=makeQuery(id+"F25.imprint","INTERSECT",VERTEX,{"derivedFrom":[subQ1,subQ0]});Q259=makeQuery(id+"F25.imprint","IMPRINT",FACE,{"disambiguationData":[TD([[makeQuery(id+"F25.imprint","IMPRINT",EDGE,{"disambiguationData":[TD([[subQ2,-1.0]])],"derivedFrom":subQ1}),1.0]])]});}
            var Q260;
            {var subQ0=sQuery(id+"F25.wireOp",EDGE,"E527.trimOffspring");var subQ1=sQuery(id+"F25.wireOp",EDGE,"E510.trimOffspring");var subQ2=makeQuery(id+"F25.imprint","INTERSECT",VERTEX,{"derivedFrom":[subQ1,subQ0]});Q260=makeQuery(id+"F25.imprint","IMPRINT",FACE,{"disambiguationData":[TD([[makeQuery(id+"F25.imprint","IMPRINT",EDGE,{"disambiguationData":[TD([[subQ2,-1.0]])],"derivedFrom":subQ1}),1.0]])]});}
            var Q261;
            {var subQ0=sQuery(id+"F25.wireOp",EDGE,"E532.trimOffspring");var subQ1=sQuery(id+"F25.wireOp",EDGE,"E509.trimOffspring");var subQ2=makeQuery(id+"F25.imprint","INTERSECT",VERTEX,{"derivedFrom":[subQ1,subQ0]});Q261=makeQuery(id+"F25.imprint","IMPRINT",FACE,{"disambiguationData":[TD([[makeQuery(id+"F25.imprint","IMPRINT",EDGE,{"disambiguationData":[TD([[subQ2,-1.0]])],"derivedFrom":subQ1}),-1.0]])]});}
            var Q262;
            {var subQ0=sQuery(id+"F25.wireOp",EDGE,"E533.trimOffspring");var subQ1=sQuery(id+"F25.wireOp",EDGE,"E509.trimOffspring");var subQ2=makeQuery(id+"F25.imprint","INTERSECT",VERTEX,{"derivedFrom":[subQ1,subQ0]});Q262=makeQuery(id+"F25.imprint","IMPRINT",FACE,{"disambiguationData":[TD([[makeQuery(id+"F25.imprint","IMPRINT",EDGE,{"disambiguationData":[TD([[subQ2,1.0]])],"derivedFrom":subQ1}),-1.0]])]});}
            var Q263;
            {var subQ0=sQuery(id+"F25.wireOp",EDGE,"E533.trimOffspring");var subQ1=sQuery(id+"F25.wireOp",EDGE,"E509.trimOffspring");var subQ2=makeQuery(id+"F25.imprint","INTERSECT",VERTEX,{"derivedFrom":[subQ1,subQ0]});Q263=makeQuery(id+"F25.imprint","IMPRINT",FACE,{"disambiguationData":[TD([[makeQuery(id+"F25.imprint","IMPRINT",EDGE,{"disambiguationData":[TD([[subQ2,1.0]])],"derivedFrom":subQ1}),1.0]])]});}
            var Q264;
            {var subQ0=sQuery(id+"F25.wireOp",EDGE,"E532.trimOffspring");var subQ1=sQuery(id+"F25.wireOp",EDGE,"E509.trimOffspring");var subQ2=makeQuery(id+"F25.imprint","INTERSECT",VERTEX,{"derivedFrom":[subQ1,subQ0]});Q264=makeQuery(id+"F25.imprint","IMPRINT",FACE,{"disambiguationData":[TD([[makeQuery(id+"F25.imprint","IMPRINT",EDGE,{"disambiguationData":[TD([[subQ2,-1.0]])],"derivedFrom":subQ1}),1.0]])]});}
            var Q265;
            {var subQ0=sQuery(id+"F25.wireOp",EDGE,"E516.trimOffspring");var subQ1=sQuery(id+"F25.wireOp",EDGE,"E509.trimOffspring");var subQ2=makeQuery(id+"F25.imprint","INTERSECT",VERTEX,{"derivedFrom":[subQ1,subQ0]});Q265=makeQuery(id+"F25.imprint","IMPRINT",FACE,{"disambiguationData":[TD([[makeQuery(id+"F25.imprint","IMPRINT",EDGE,{"disambiguationData":[TD([[subQ2,-1.0]])],"derivedFrom":subQ1}),-1.0]])]});}
            var Q266;
            {var subQ3=sQuery(id+"F25.wireOp",EDGE,"E516.trimOffspring");var subQ5=sQuery(id+"F25.wireOp",EDGE,"E509.trimOffspring");var subQ6=makeQuery(id+"F25.imprint","INTERSECT",VERTEX,{"derivedFrom":[subQ5,subQ3]});Q266=makeQuery(id+"F25.imprint","IMPRINT",FACE,{"disambiguationData":[TD([[makeQuery(id+"F25.imprint","IMPRINT",EDGE,{"disambiguationData":[TD([[subQ6,-1.0]])],"derivedFrom":subQ5}),1.0]])]});}
            var Q267;
            {var subQ0=sQuery(id+"F25.wireOp",EDGE,"E514.trimOffspring");var subQ1=sQuery(id+"F25.wireOp",EDGE,"E508.trimOffspring");var subQ2=makeQuery(id+"F25.imprint","INTERSECT",VERTEX,{"derivedFrom":[subQ1,subQ0]});Q267=makeQuery(id+"F25.imprint","IMPRINT",FACE,{"disambiguationData":[TD([[makeQuery(id+"F25.imprint","IMPRINT",EDGE,{"disambiguationData":[TD([[subQ2,-1.0]])],"derivedFrom":subQ1}),-1.0]])]});}
            var Q268;
            {var subQ0=sQuery(id+"F25.wireOp",EDGE,"E514.trimOffspring");var subQ1=sQuery(id+"F25.wireOp",EDGE,"E509.trimOffspring");var subQ2=makeQuery(id+"F25.imprint","INTERSECT",VERTEX,{"derivedFrom":[subQ1,subQ0]});Q268=makeQuery(id+"F25.imprint","IMPRINT",FACE,{"disambiguationData":[TD([[makeQuery(id+"F25.imprint","IMPRINT",EDGE,{"disambiguationData":[TD([[subQ2,-1.0]])],"derivedFrom":subQ1}),-1.0]])]});}
            var Q269;
            {var subQ0=sQuery(id+"F25.wireOp",EDGE,"E515.trimOffspring");var subQ1=sQuery(id+"F25.wireOp",EDGE,"E509.trimOffspring");var subQ2=makeQuery(id+"F25.imprint","INTERSECT",VERTEX,{"derivedFrom":[subQ1,subQ0]});Q269=makeQuery(id+"F25.imprint","IMPRINT",FACE,{"disambiguationData":[TD([[makeQuery(id+"F25.imprint","IMPRINT",EDGE,{"disambiguationData":[TD([[subQ2,-1.0]])],"derivedFrom":subQ1}),-1.0]])]});}
            var Q270;
            {var subQ0=sQuery(id+"F25.wireOp",EDGE,"E515.trimOffspring");var subQ1=sQuery(id+"F25.wireOp",EDGE,"E508.trimOffspring");var subQ2=makeQuery(id+"F25.imprint","INTERSECT",VERTEX,{"derivedFrom":[subQ1,subQ0]});Q270=makeQuery(id+"F25.imprint","IMPRINT",FACE,{"disambiguationData":[TD([[makeQuery(id+"F25.imprint","IMPRINT",EDGE,{"disambiguationData":[TD([[subQ2,-1.0]])],"derivedFrom":subQ1}),-1.0]])]});}
            var Q271;
            {var subQ0=sQuery(id+"F25.wireOp",EDGE,"E263.trimOffspring");Q271=makeQuery(id+"F25.imprint","IMPRINT",FACE,{"disambiguationData":[TD([[makeQuery(id+"F25.imprint","IMPRINT",EDGE,{"derivedFrom":subQ0}),-1.0]])]});}
            var Q272;
            {var subQ0=sQuery(id+"F25.wireOp",EDGE,"E515.trimOffspring");var subQ1=sQuery(id+"F25.wireOp",EDGE,"E508.trimOffspring");var subQ2=makeQuery(id+"F25.imprint","INTERSECT",VERTEX,{"derivedFrom":[subQ1,subQ0]});Q272=makeQuery(id+"F25.imprint","IMPRINT",FACE,{"disambiguationData":[TD([[makeQuery(id+"F25.imprint","IMPRINT",EDGE,{"disambiguationData":[TD([[subQ2,-1.0]])],"derivedFrom":subQ1}),1.0]])]});}
            var Q273;
            {var subQ0=sQuery(id+"F25.wireOp",EDGE,"E263.trimOffspring");Q273=makeQuery(id+"F25.imprint","IMPRINT",FACE,{"disambiguationData":[TD([[makeQuery(id+"F25.imprint","IMPRINT",EDGE,{"derivedFrom":subQ0}),1.0]])]});}
            var Q274;
            {var subQ0=sQuery(id+"F25.wireOp",EDGE,"E514.trimOffspring");var subQ1=sQuery(id+"F25.wireOp",EDGE,"E264.trimOffspring");var subQ2=makeQuery(id+"F25.imprint","INTERSECT",VERTEX,{"derivedFrom":[subQ1,subQ0]});Q274=makeQuery(id+"F25.imprint","IMPRINT",FACE,{"disambiguationData":[TD([[makeQuery(id+"F25.imprint","IMPRINT",EDGE,{"disambiguationData":[TD([[subQ2,-1.0]])],"derivedFrom":subQ1}),-1.0]])]});}
            var Q275;
            {var subQ0=sQuery(id+"F25.wireOp",EDGE,"E515.trimOffspring");var subQ1=sQuery(id+"F25.wireOp",EDGE,"E266.trimOffspring");var subQ2=makeQuery(id+"F25.imprint","INTERSECT",VERTEX,{"derivedFrom":[subQ1,subQ0]});Q275=makeQuery(id+"F25.imprint","IMPRINT",FACE,{"disambiguationData":[TD([[makeQuery(id+"F25.imprint","IMPRINT",EDGE,{"disambiguationData":[TD([[subQ2,-1.0]])],"derivedFrom":subQ1}),-1.0]])]});}
            var Q276;
            {var subQ0=sQuery(id+"F25.wireOp",EDGE,"E515.trimOffspring");var subQ1=sQuery(id+"F25.wireOp",EDGE,"E264.trimOffspring");var subQ2=makeQuery(id+"F25.imprint","INTERSECT",VERTEX,{"derivedFrom":[subQ1,subQ0]});Q276=makeQuery(id+"F25.imprint","IMPRINT",FACE,{"disambiguationData":[TD([[makeQuery(id+"F25.imprint","IMPRINT",EDGE,{"disambiguationData":[TD([[subQ2,-1.0]])],"derivedFrom":subQ1}),-1.0]])]});}
            var Q277;
            {var subQ0=sQuery(id+"F25.wireOp",EDGE,"E516.trimOffspring");var subQ1=sQuery(id+"F25.wireOp",EDGE,"E266.trimOffspring");var subQ2=makeQuery(id+"F25.imprint","INTERSECT",VERTEX,{"derivedFrom":[subQ1,subQ0]});Q277=makeQuery(id+"F25.imprint","IMPRINT",FACE,{"disambiguationData":[TD([[makeQuery(id+"F25.imprint","IMPRINT",EDGE,{"disambiguationData":[TD([[subQ2,-1.0]])],"derivedFrom":subQ1}),-1.0]])]});}
            var Q278;
            {var subQ0=sQuery(id+"F25.wireOp",EDGE,"E516.trimOffspring");var subQ1=sQuery(id+"F25.wireOp",EDGE,"E264.trimOffspring");var subQ2=makeQuery(id+"F25.imprint","INTERSECT",VERTEX,{"derivedFrom":[subQ1,subQ0]});Q278=makeQuery(id+"F25.imprint","IMPRINT",FACE,{"disambiguationData":[TD([[makeQuery(id+"F25.imprint","IMPRINT",EDGE,{"disambiguationData":[TD([[subQ2,-1.0]])],"derivedFrom":subQ1}),-1.0]])]});}
            var Q279;
            {var subQ0=sQuery(id+"F25.wireOp",EDGE,"E532.trimOffspring");var subQ1=sQuery(id+"F25.wireOp",EDGE,"E266.trimOffspring");var subQ2=makeQuery(id+"F25.imprint","INTERSECT",VERTEX,{"derivedFrom":[subQ1,subQ0]});Q279=makeQuery(id+"F25.imprint","IMPRINT",FACE,{"disambiguationData":[TD([[makeQuery(id+"F25.imprint","IMPRINT",EDGE,{"disambiguationData":[TD([[subQ2,-1.0]])],"derivedFrom":subQ1}),-1.0]])]});}
            var Q280;
            {var subQ0=sQuery(id+"F25.wireOp",EDGE,"E532.trimOffspring");var subQ1=sQuery(id+"F25.wireOp",EDGE,"E264.trimOffspring");var subQ2=makeQuery(id+"F25.imprint","INTERSECT",VERTEX,{"derivedFrom":[subQ1,subQ0]});Q280=makeQuery(id+"F25.imprint","IMPRINT",FACE,{"disambiguationData":[TD([[makeQuery(id+"F25.imprint","IMPRINT",EDGE,{"disambiguationData":[TD([[subQ2,-1.0]])],"derivedFrom":subQ1}),-1.0]])]});}
            var Q281;
            {var subQ0=sQuery(id+"F25.wireOp",EDGE,"E527.trimOffspring");var subQ1=sQuery(id+"F25.wireOp",EDGE,"E266.trimOffspring");var subQ2=makeQuery(id+"F25.imprint","INTERSECT",VERTEX,{"derivedFrom":[subQ1,subQ0]});Q281=makeQuery(id+"F25.imprint","IMPRINT",FACE,{"disambiguationData":[TD([[makeQuery(id+"F25.imprint","IMPRINT",EDGE,{"disambiguationData":[TD([[subQ2,-1.0]])],"derivedFrom":subQ1}),-1.0]])]});}
            var Q282;
            {var subQ0=sQuery(id+"F25.wireOp",EDGE,"E527.trimOffspring");var subQ1=sQuery(id+"F25.wireOp",EDGE,"E264.trimOffspring");var subQ2=makeQuery(id+"F25.imprint","INTERSECT",VERTEX,{"derivedFrom":[subQ1,subQ0]});Q282=makeQuery(id+"F25.imprint","IMPRINT",FACE,{"disambiguationData":[TD([[makeQuery(id+"F25.imprint","IMPRINT",EDGE,{"disambiguationData":[TD([[subQ2,-1.0]])],"derivedFrom":subQ1}),-1.0]])]});}
            var Q283;
            {var subQ0=sQuery(id+"F25.wireOp",EDGE,"E533.trimOffspring");var subQ1=sQuery(id+"F25.wireOp",EDGE,"E266.trimOffspring");var subQ2=makeQuery(id+"F25.imprint","INTERSECT",VERTEX,{"derivedFrom":[subQ1,subQ0]});Q283=makeQuery(id+"F25.imprint","IMPRINT",FACE,{"disambiguationData":[TD([[makeQuery(id+"F25.imprint","IMPRINT",EDGE,{"disambiguationData":[TD([[subQ2,-1.0]])],"derivedFrom":subQ1}),-1.0]])]});}
            var Q284;
            {var subQ0=sQuery(id+"F25.wireOp",EDGE,"E533.trimOffspring");var subQ1=sQuery(id+"F25.wireOp",EDGE,"E264.trimOffspring");var subQ2=makeQuery(id+"F25.imprint","INTERSECT",VERTEX,{"derivedFrom":[subQ1,subQ0]});Q284=makeQuery(id+"F25.imprint","IMPRINT",FACE,{"disambiguationData":[TD([[makeQuery(id+"F25.imprint","IMPRINT",EDGE,{"disambiguationData":[TD([[subQ2,-1.0]])],"derivedFrom":subQ1}),-1.0]])]});}
            var Q285;
            {var subQ0=sQuery(id+"F25.wireOp",EDGE,"E538.trimOffspring");var subQ1=sQuery(id+"F25.wireOp",EDGE,"E266.trimOffspring");var subQ2=makeQuery(id+"F25.imprint","INTERSECT",VERTEX,{"derivedFrom":[subQ1,subQ0]});Q285=makeQuery(id+"F25.imprint","IMPRINT",FACE,{"disambiguationData":[TD([[makeQuery(id+"F25.imprint","IMPRINT",EDGE,{"disambiguationData":[TD([[subQ2,-1.0]])],"derivedFrom":subQ1}),-1.0]])]});}
            var Q286;
            {var subQ0=sQuery(id+"F25.wireOp",EDGE,"E542.trimOffspring");var subQ1=sQuery(id+"F25.wireOp",EDGE,"E266.trimOffspring");var subQ2=makeQuery(id+"F25.imprint","INTERSECT",VERTEX,{"derivedFrom":[subQ1,subQ0]});Q286=makeQuery(id+"F25.imprint","IMPRINT",FACE,{"disambiguationData":[TD([[makeQuery(id+"F25.imprint","IMPRINT",EDGE,{"disambiguationData":[TD([[subQ2,1.0]])],"derivedFrom":subQ1}),-1.0]])]});}
            var Q287;
            {var subQ0=sQuery(id+"F25.wireOp",EDGE,"E538.trimOffspring");var subQ1=sQuery(id+"F25.wireOp",EDGE,"E264.trimOffspring");var subQ2=makeQuery(id+"F25.imprint","INTERSECT",VERTEX,{"derivedFrom":[subQ1,subQ0]});Q287=makeQuery(id+"F25.imprint","IMPRINT",FACE,{"disambiguationData":[TD([[makeQuery(id+"F25.imprint","IMPRINT",EDGE,{"disambiguationData":[TD([[subQ2,-1.0]])],"derivedFrom":subQ1}),-1.0]])]});}
            var Q288;
            {var subQ0=sQuery(id+"F25.wireOp",EDGE,"E542.trimOffspring");var subQ1=sQuery(id+"F25.wireOp",EDGE,"E264.trimOffspring");var subQ2=makeQuery(id+"F25.imprint","INTERSECT",VERTEX,{"derivedFrom":[subQ1,subQ0]});Q288=makeQuery(id+"F25.imprint","IMPRINT",FACE,{"disambiguationData":[TD([[makeQuery(id+"F25.imprint","IMPRINT",EDGE,{"disambiguationData":[TD([[subQ2,1.0]])],"derivedFrom":subQ1}),-1.0]])]});}
            var Q289;
            {var subQ0=sQuery(id+"F25.wireOp",EDGE,"E243.top");Q289=makeQuery(id+"F25.imprint","IMPRINT",FACE,{"disambiguationData":[TD([[makeQuery(id+"F25.imprint","IMPRINT",EDGE,{"derivedFrom":subQ0}),1.0]])]});}
            var Q290;
            {var subQ0=sQuery(id+"F25.wireOp",EDGE,"E244.top");Q290=makeQuery(id+"F25.imprint","IMPRINT",FACE,{"disambiguationData":[TD([[makeQuery(id+"F25.imprint","IMPRINT",EDGE,{"derivedFrom":subQ0}),-1.0]])]});}
            var Q291;
            {var subQ0=sQuery(id+"F25.wireOp",EDGE,"E516.trimOffspring");var subQ5=sQuery(id+"F25.wireOp",EDGE,"E265.trimOffspring");var subQ6=makeQuery(id+"F25.imprint","INTERSECT",VERTEX,{"derivedFrom":[subQ5,subQ0]});Q291=makeQuery(id+"F25.imprint","IMPRINT",FACE,{"disambiguationData":[TD([[makeQuery(id+"F25.imprint","IMPRINT",EDGE,{"disambiguationData":[TD([[subQ6,-1.0]])],"derivedFrom":subQ5}),1.0]])]});}
            var Q292;
            {var subQ0=sQuery(id+"F25.wireOp",EDGE,"E243.top");Q292=makeQuery(id+"F25.imprint","IMPRINT",FACE,{"disambiguationData":[TD([[makeQuery(id+"F25.imprint","IMPRINT",EDGE,{"derivedFrom":subQ0}),-1.0]])]});}
            var Q293;
            {var subQ0=sQuery(id+"F25.wireOp",EDGE,"E244.top");Q293=makeQuery(id+"F25.imprint","IMPRINT",FACE,{"disambiguationData":[TD([[makeQuery(id+"F25.imprint","IMPRINT",EDGE,{"derivedFrom":subQ0}),1.0]])]});}
            var Q294;
            {var subQ0=sQuery(id+"F25.wireOp",EDGE,"E574.trimOffspring");var subQ5=sQuery(id+"F25.wireOp",EDGE,"E414.MirrorCS");var subQ6=makeQuery(id+"F25.imprint","INTERSECT",VERTEX,{"derivedFrom":[subQ5,subQ0]});Q294=makeQuery(id+"F25.imprint","IMPRINT",FACE,{"disambiguationData":[TD([[makeQuery(id+"F25.imprint","IMPRINT",EDGE,{"disambiguationData":[TD([[subQ6,-1.0]])],"derivedFrom":subQ5}),-1.0]])]});}
            var Q295;
            {var subQ0=sQuery(id+"F25.wireOp",EDGE,"E245.top");Q295=makeQuery(id+"F25.imprint","IMPRINT",FACE,{"disambiguationData":[TD([[makeQuery(id+"F25.imprint","IMPRINT",EDGE,{"derivedFrom":subQ0}),1.0]])]});}
            var Q296;
            {var subQ0=sQuery(id+"F25.wireOp",EDGE,"E245.top");Q296=makeQuery(id+"F25.imprint","IMPRINT",FACE,{"disambiguationData":[TD([[makeQuery(id+"F25.imprint","IMPRINT",EDGE,{"derivedFrom":subQ0}),-1.0]])]});}
            var Q297;
            {var subQ0=sQuery(id+"F25.wireOp",EDGE,"E246.top");Q297=makeQuery(id+"F25.imprint","IMPRINT",FACE,{"disambiguationData":[TD([[makeQuery(id+"F25.imprint","IMPRINT",EDGE,{"derivedFrom":subQ0}),-1.0]])]});}
            var Q298;
            {var subQ0=sQuery(id+"F25.wireOp",EDGE,"E246.top");Q298=makeQuery(id+"F25.imprint","IMPRINT",FACE,{"disambiguationData":[TD([[makeQuery(id+"F25.imprint","IMPRINT",EDGE,{"derivedFrom":subQ0}),1.0]])]});}
            var Q299;
            {var subQ0=sQuery(id+"F25.wireOp",EDGE,"E533.trimOffspring");var subQ5=sQuery(id+"F25.wireOp",EDGE,"E265.trimOffspring");var subQ6=makeQuery(id+"F25.imprint","INTERSECT",VERTEX,{"derivedFrom":[subQ5,subQ0]});Q299=makeQuery(id+"F25.imprint","IMPRINT",FACE,{"disambiguationData":[TD([[makeQuery(id+"F25.imprint","IMPRINT",EDGE,{"disambiguationData":[TD([[subQ6,-1.0]])],"derivedFrom":subQ5}),1.0]])]});}
            var Q300;
            {var subQ0=sQuery(id+"F25.wireOp",EDGE,"E581.trimOffspring");var subQ5=sQuery(id+"F25.wireOp",EDGE,"E414.MirrorCS");var subQ6=makeQuery(id+"F25.imprint","INTERSECT",VERTEX,{"derivedFrom":[subQ5,subQ0]});Q300=makeQuery(id+"F25.imprint","IMPRINT",FACE,{"disambiguationData":[TD([[makeQuery(id+"F25.imprint","IMPRINT",EDGE,{"disambiguationData":[TD([[subQ6,-1.0]])],"derivedFrom":subQ5}),-1.0]])]});}
            var Q301;
            {var subQ0=sQuery(id+"F25.wireOp",EDGE,"E247.top");Q301=makeQuery(id+"F25.imprint","IMPRINT",FACE,{"disambiguationData":[TD([[makeQuery(id+"F25.imprint","IMPRINT",EDGE,{"derivedFrom":subQ0}),-1.0]])]});}
            var Q302;
            {var subQ0=sQuery(id+"F25.wireOp",EDGE,"E247.top");Q302=makeQuery(id+"F25.imprint","IMPRINT",FACE,{"disambiguationData":[TD([[makeQuery(id+"F25.imprint","IMPRINT",EDGE,{"derivedFrom":subQ0}),1.0]])]});}
            var Q303;
            {var subQ5=sQuery(id+"F25.wireOp",EDGE,"E248.top");Q303=makeQuery(id+"F25.imprint","IMPRINT",FACE,{"disambiguationData":[TD([[makeQuery(id+"F25.imprint","IMPRINT",EDGE,{"derivedFrom":subQ5}),-1.0]])]});}
            var Q304;
            {var subQ0=sQuery(id+"F25.wireOp",EDGE,"E410.MirrorCS");Q304=makeQuery(id+"F25.imprint","IMPRINT",FACE,{"disambiguationData":[TD([[makeQuery(id+"F25.imprint","IMPRINT",EDGE,{"derivedFrom":subQ0}),1.0]])]});}
            var Q305;
            {var subQ0=sQuery(id+"F25.wireOp",EDGE,"E470.MirrorCS");var subQ1=sQuery(id+"F25.wireOp",EDGE,"E428.MirrorCS");var subQ2=makeQuery(id+"F25.imprint","INTERSECT",VERTEX,{"derivedFrom":[subQ1,subQ0]});Q305=makeQuery(id+"F25.imprint","IMPRINT",FACE,{"disambiguationData":[TD([[makeQuery(id+"F25.imprint","IMPRINT",EDGE,{"disambiguationData":[TD([[subQ2,-1.0]])],"derivedFrom":subQ1}),1.0]])]});}
            var Q306;
            {var subQ0=sQuery(id+"F25.wireOp",EDGE,"E452.MirrorCS");var subQ1=sQuery(id+"F25.wireOp",EDGE,"E428.MirrorCS");var subQ2=makeQuery(id+"F25.imprint","INTERSECT",VERTEX,{"derivedFrom":[subQ1,subQ0]});Q306=makeQuery(id+"F25.imprint","IMPRINT",FACE,{"disambiguationData":[TD([[makeQuery(id+"F25.imprint","IMPRINT",EDGE,{"disambiguationData":[TD([[subQ2,1.0]])],"derivedFrom":subQ1}),1.0]])]});}
            var Q307;
            {var subQ3=sQuery(id+"F25.wireOp",EDGE,"E471.MirrorCS");Q307=makeQuery(id+"F25.imprint","IMPRINT",FACE,{"disambiguationData":[TD([[makeQuery(id+"F25.imprint","IMPRINT",EDGE,{"derivedFrom":subQ3}),1.0]])]});}
            var Q308;
            {var subQ3=sQuery(id+"F25.wireOp",EDGE,"E471.MirrorCS");Q308=makeQuery(id+"F25.imprint","IMPRINT",FACE,{"disambiguationData":[TD([[makeQuery(id+"F25.imprint","IMPRINT",EDGE,{"derivedFrom":subQ3}),-1.0]])]});}
            var Q309;
            {var subQ0=sQuery(id+"F25.wireOp",EDGE,"E460.MirrorCS");var subQ1=sQuery(id+"F25.wireOp",EDGE,"E428.MirrorCS");var subQ2=makeQuery(id+"F25.imprint","INTERSECT",VERTEX,{"derivedFrom":[subQ1,subQ0]});Q309=makeQuery(id+"F25.imprint","IMPRINT",FACE,{"disambiguationData":[TD([[makeQuery(id+"F25.imprint","IMPRINT",EDGE,{"disambiguationData":[TD([[subQ2,1.0]])],"derivedFrom":subQ1}),1.0]])]});}
            var Q310;
            {var subQ0=sQuery(id+"F25.wireOp",EDGE,"E432.MirrorCS");Q310=makeQuery(id+"F25.imprint","IMPRINT",FACE,{"disambiguationData":[TD([[makeQuery(id+"F25.imprint","IMPRINT",EDGE,{"derivedFrom":subQ0}),-1.0]])]});}
            var Q311;
            {var subQ0=sQuery(id+"F25.wireOp",EDGE,"E453.MirrorCS");Q311=makeQuery(id+"F25.imprint","IMPRINT",FACE,{"disambiguationData":[TD([[makeQuery(id+"F25.imprint","IMPRINT",EDGE,{"derivedFrom":subQ0}),-1.0]])]});}
            var Q312;
            {var subQ0=sQuery(id+"F25.wireOp",EDGE,"E452.MirrorCS");var subQ1=sQuery(id+"F25.wireOp",EDGE,"E425.MirrorCS");var subQ2=makeQuery(id+"F25.imprint","INTERSECT",VERTEX,{"derivedFrom":[subQ1,subQ0]});Q312=makeQuery(id+"F25.imprint","IMPRINT",FACE,{"disambiguationData":[TD([[makeQuery(id+"F25.imprint","IMPRINT",EDGE,{"disambiguationData":[TD([[subQ2,1.0]])],"derivedFrom":subQ1}),-1.0]])]});}
            var Q313;
            {var subQ0=sQuery(id+"F25.wireOp",EDGE,"E430.MirrorCS");Q313=makeQuery(id+"F25.imprint","IMPRINT",FACE,{"disambiguationData":[TD([[makeQuery(id+"F25.imprint","IMPRINT",EDGE,{"derivedFrom":subQ0}),1.0]])]});}
            var Q314;
            {var subQ0=sQuery(id+"F25.wireOp",EDGE,"E430.MirrorCS");Q314=makeQuery(id+"F25.imprint","IMPRINT",FACE,{"disambiguationData":[TD([[makeQuery(id+"F25.imprint","IMPRINT",EDGE,{"derivedFrom":subQ0}),-1.0]])]});}
            var Q315;
            {var subQ0=sQuery(id+"F25.wireOp",EDGE,"E442.MirrorCS");var subQ1=sQuery(id+"F25.wireOp",EDGE,"E425.MirrorCS");var subQ2=makeQuery(id+"F25.imprint","INTERSECT",VERTEX,{"derivedFrom":[subQ1,subQ0]});Q315=makeQuery(id+"F25.imprint","IMPRINT",FACE,{"disambiguationData":[TD([[makeQuery(id+"F25.imprint","IMPRINT",EDGE,{"disambiguationData":[TD([[subQ2,-1.0]])],"derivedFrom":subQ1}),-1.0]])]});}
            var Q316;
            {var subQ0=sQuery(id+"F25.wireOp",EDGE,"E464.MirrorCS");var subQ1=sQuery(id+"F25.wireOp",EDGE,"E428.MirrorCS");var subQ2=makeQuery(id+"F25.imprint","INTERSECT",VERTEX,{"derivedFrom":[subQ1,subQ0]});Q316=makeQuery(id+"F25.imprint","IMPRINT",FACE,{"disambiguationData":[TD([[makeQuery(id+"F25.imprint","IMPRINT",EDGE,{"disambiguationData":[TD([[subQ2,1.0]])],"derivedFrom":subQ1}),1.0]])]});}
            var Q317;
            {var subQ0=sQuery(id+"F25.wireOp",EDGE,"E460.MirrorCS");var subQ1=sQuery(id+"F25.wireOp",EDGE,"E428.MirrorCS");var subQ2=makeQuery(id+"F25.imprint","INTERSECT",VERTEX,{"derivedFrom":[subQ1,subQ0]});Q317=makeQuery(id+"F25.imprint","IMPRINT",FACE,{"disambiguationData":[TD([[makeQuery(id+"F25.imprint","IMPRINT",EDGE,{"disambiguationData":[TD([[subQ2,-1.0]])],"derivedFrom":subQ1}),1.0]])]});}
            var Q318;
            {var subQ0=sQuery(id+"F25.wireOp",EDGE,"E460.MirrorCS");var subQ1=sQuery(id+"F25.wireOp",EDGE,"E425.MirrorCS");var subQ2=makeQuery(id+"F25.imprint","INTERSECT",VERTEX,{"derivedFrom":[subQ1,subQ0]});Q318=makeQuery(id+"F25.imprint","IMPRINT",FACE,{"disambiguationData":[TD([[makeQuery(id+"F25.imprint","IMPRINT",EDGE,{"disambiguationData":[TD([[subQ2,-1.0]])],"derivedFrom":subQ1}),-1.0]])]});}
            var Q319;
            {var subQ0=sQuery(id+"F25.wireOp",EDGE,"E464.MirrorCS");var subQ1=sQuery(id+"F25.wireOp",EDGE,"E425.MirrorCS");var subQ2=makeQuery(id+"F25.imprint","INTERSECT",VERTEX,{"derivedFrom":[subQ1,subQ0]});Q319=makeQuery(id+"F25.imprint","IMPRINT",FACE,{"disambiguationData":[TD([[makeQuery(id+"F25.imprint","IMPRINT",EDGE,{"disambiguationData":[TD([[subQ2,1.0]])],"derivedFrom":subQ1}),-1.0]])]});}
            var Q320;
            {var subQ0=sQuery(id+"F25.wireOp",EDGE,"E555.trimOffspring");var subQ5=sQuery(id+"F25.wireOp",EDGE,"E439.MirrorCS");var subQ6=makeQuery(id+"F25.imprint","INTERSECT",VERTEX,{"derivedFrom":[subQ5,subQ0]});Q320=makeQuery(id+"F25.imprint","IMPRINT",FACE,{"disambiguationData":[TD([[makeQuery(id+"F25.imprint","IMPRINT",EDGE,{"disambiguationData":[TD([[subQ6,-1.0]])],"derivedFrom":subQ5}),-1.0]])]});}
            var Q321;
            {var subQ0=sQuery(id+"F25.wireOp",EDGE,"E555.trimOffspring");var subQ1=sQuery(id+"F25.wireOp",EDGE,"E429.MirrorCS");var subQ2=makeQuery(id+"F25.imprint","INTERSECT",VERTEX,{"derivedFrom":[subQ1,subQ0]});Q321=makeQuery(id+"F25.imprint","IMPRINT",FACE,{"disambiguationData":[TD([[makeQuery(id+"F25.imprint","IMPRINT",EDGE,{"disambiguationData":[TD([[subQ2,-1.0]])],"derivedFrom":subQ1}),-1.0]])]});}
            var Q322;
            {var subQ0=sQuery(id+"F25.wireOp",EDGE,"E555.trimOffspring");var subQ1=sQuery(id+"F25.wireOp",EDGE,"E429.MirrorCS");var subQ2=makeQuery(id+"F25.imprint","INTERSECT",VERTEX,{"derivedFrom":[subQ1,subQ0]});Q322=makeQuery(id+"F25.imprint","IMPRINT",FACE,{"disambiguationData":[TD([[makeQuery(id+"F25.imprint","IMPRINT",EDGE,{"disambiguationData":[TD([[subQ2,-1.0]])],"derivedFrom":subQ1}),1.0]])]});}
            var Q323;
            {var subQ0=sQuery(id+"F25.wireOp",EDGE,"E552.trimOffspring");var subQ5=sQuery(id+"F25.wireOp",EDGE,"E439.MirrorCS");var subQ6=makeQuery(id+"F25.imprint","INTERSECT",VERTEX,{"derivedFrom":[subQ5,subQ0]});Q323=makeQuery(id+"F25.imprint","IMPRINT",FACE,{"disambiguationData":[TD([[makeQuery(id+"F25.imprint","IMPRINT",EDGE,{"disambiguationData":[TD([[subQ6,-1.0]])],"derivedFrom":subQ5}),-1.0]])]});}
            var Q324;
            {var subQ0=sQuery(id+"F25.wireOp",EDGE,"E554.trimOffspring");var subQ1=sQuery(id+"F25.wireOp",EDGE,"E429.MirrorCS");var subQ2=makeQuery(id+"F25.imprint","INTERSECT",VERTEX,{"derivedFrom":[subQ1,subQ0]});Q324=makeQuery(id+"F25.imprint","IMPRINT",FACE,{"disambiguationData":[TD([[makeQuery(id+"F25.imprint","IMPRINT",EDGE,{"disambiguationData":[TD([[subQ2,1.0]])],"derivedFrom":subQ1}),-1.0]])]});}
            var Q325;
            {var subQ0=sQuery(id+"F25.wireOp",EDGE,"E545.trimOffspring");var subQ1=sQuery(id+"F25.wireOp",EDGE,"E424.MirrorCS");var subQ2=makeQuery(id+"F25.imprint","INTERSECT",VERTEX,{"derivedFrom":[subQ1,subQ0]});Q325=makeQuery(id+"F25.imprint","IMPRINT",FACE,{"disambiguationData":[TD([[makeQuery(id+"F25.imprint","IMPRINT",EDGE,{"disambiguationData":[TD([[subQ2,1.0]])],"derivedFrom":subQ1}),1.0]])]});}
            var Q326;
            {var subQ0=sQuery(id+"F25.wireOp",EDGE,"E545.trimOffspring");var subQ1=sQuery(id+"F25.wireOp",EDGE,"E429.MirrorCS");var subQ2=makeQuery(id+"F25.imprint","INTERSECT",VERTEX,{"derivedFrom":[subQ1,subQ0]});Q326=makeQuery(id+"F25.imprint","IMPRINT",FACE,{"disambiguationData":[TD([[makeQuery(id+"F25.imprint","IMPRINT",EDGE,{"disambiguationData":[TD([[subQ2,1.0]])],"derivedFrom":subQ1}),-1.0]])]});}
            var Q327;
            {var subQ0=sQuery(id+"F25.wireOp",EDGE,"E545.trimOffspring");var subQ1=sQuery(id+"F25.wireOp",EDGE,"E424.MirrorCS");var subQ2=makeQuery(id+"F25.imprint","INTERSECT",VERTEX,{"derivedFrom":[subQ1,subQ0]});Q327=makeQuery(id+"F25.imprint","IMPRINT",FACE,{"disambiguationData":[TD([[makeQuery(id+"F25.imprint","IMPRINT",EDGE,{"disambiguationData":[TD([[subQ2,-1.0]])],"derivedFrom":subQ1}),1.0]])]});}
            var Q328;
            {var subQ0=sQuery(id+"F25.wireOp",EDGE,"E545.trimOffspring");var subQ1=sQuery(id+"F25.wireOp",EDGE,"E429.MirrorCS");var subQ2=makeQuery(id+"F25.imprint","INTERSECT",VERTEX,{"derivedFrom":[subQ1,subQ0]});Q328=makeQuery(id+"F25.imprint","IMPRINT",FACE,{"disambiguationData":[TD([[makeQuery(id+"F25.imprint","IMPRINT",EDGE,{"disambiguationData":[TD([[subQ2,-1.0]])],"derivedFrom":subQ1}),-1.0]])]});}
            var Q329;
            {var subQ0=sQuery(id+"F25.wireOp",EDGE,"E553.trimOffspring");var subQ1=sQuery(id+"F25.wireOp",EDGE,"E424.MirrorCS");var subQ2=makeQuery(id+"F25.imprint","INTERSECT",VERTEX,{"derivedFrom":[subQ1,subQ0]});Q329=makeQuery(id+"F25.imprint","IMPRINT",FACE,{"disambiguationData":[TD([[makeQuery(id+"F25.imprint","IMPRINT",EDGE,{"disambiguationData":[TD([[subQ2,-1.0]])],"derivedFrom":subQ1}),1.0]])]});}
            var Q330;
            {var subQ3=sQuery(id+"F25.wireOp",EDGE,"E553.trimOffspring");var subQ5=sQuery(id+"F25.wireOp",EDGE,"E439.MirrorCS");var subQ6=makeQuery(id+"F25.imprint","INTERSECT",VERTEX,{"derivedFrom":[subQ5,subQ3]});Q330=makeQuery(id+"F25.imprint","IMPRINT",FACE,{"disambiguationData":[TD([[makeQuery(id+"F25.imprint","IMPRINT",EDGE,{"disambiguationData":[TD([[subQ6,-1.0]])],"derivedFrom":subQ5}),1.0]])]});}
            var Q331;
            {var subQ0=sQuery(id+"F25.wireOp",EDGE,"E460.MirrorCS");var subQ1=sQuery(id+"F25.wireOp",EDGE,"E424.MirrorCS");var subQ2=makeQuery(id+"F25.imprint","INTERSECT",VERTEX,{"derivedFrom":[subQ1,subQ0]});Q331=makeQuery(id+"F25.imprint","IMPRINT",FACE,{"disambiguationData":[TD([[makeQuery(id+"F25.imprint","IMPRINT",EDGE,{"disambiguationData":[TD([[subQ2,-1.0]])],"derivedFrom":subQ1}),1.0]])]});}
            var Q332;
            {var subQ3=sQuery(id+"F25.wireOp",EDGE,"E460.MirrorCS");var subQ5=sQuery(id+"F25.wireOp",EDGE,"E439.MirrorCS");var subQ6=makeQuery(id+"F25.imprint","INTERSECT",VERTEX,{"derivedFrom":[subQ5,subQ3]});Q332=makeQuery(id+"F25.imprint","IMPRINT",FACE,{"disambiguationData":[TD([[makeQuery(id+"F25.imprint","IMPRINT",EDGE,{"disambiguationData":[TD([[subQ6,-1.0]])],"derivedFrom":subQ5}),1.0]])]});}
            var Q333;
            {var subQ0=sQuery(id+"F25.wireOp",EDGE,"E464.MirrorCS");var subQ1=sQuery(id+"F25.wireOp",EDGE,"E424.MirrorCS");var subQ2=makeQuery(id+"F25.imprint","INTERSECT",VERTEX,{"derivedFrom":[subQ1,subQ0]});Q333=makeQuery(id+"F25.imprint","IMPRINT",FACE,{"disambiguationData":[TD([[makeQuery(id+"F25.imprint","IMPRINT",EDGE,{"disambiguationData":[TD([[subQ2,1.0]])],"derivedFrom":subQ1}),1.0]])]});}
            var Q334;
            {var subQ3=sQuery(id+"F25.wireOp",EDGE,"E464.MirrorCS");var subQ5=sQuery(id+"F25.wireOp",EDGE,"E439.MirrorCS");var subQ6=makeQuery(id+"F25.imprint","INTERSECT",VERTEX,{"derivedFrom":[subQ5,subQ3]});Q334=makeQuery(id+"F25.imprint","IMPRINT",FACE,{"disambiguationData":[TD([[makeQuery(id+"F25.imprint","IMPRINT",EDGE,{"disambiguationData":[TD([[subQ6,1.0]])],"derivedFrom":subQ5}),1.0]])]});}
            var Q335;
            {var subQ0=sQuery(id+"F25.wireOp",EDGE,"E555.trimOffspring");var subQ1=sQuery(id+"F25.wireOp",EDGE,"E445.MirrorCS");var subQ2=makeQuery(id+"F25.imprint","INTERSECT",VERTEX,{"derivedFrom":[subQ1,subQ0]});Q335=makeQuery(id+"F25.imprint","IMPRINT",FACE,{"disambiguationData":[TD([[makeQuery(id+"F25.imprint","IMPRINT",EDGE,{"disambiguationData":[TD([[subQ2,-1.0]])],"derivedFrom":subQ1}),1.0]])]});}
            var Q336;
            {var subQ0=sQuery(id+"F25.wireOp",EDGE,"E564.trimOffspring");var subQ1=sQuery(id+"F25.wireOp",EDGE,"E445.MirrorCS");var subQ2=makeQuery(id+"F25.imprint","INTERSECT",VERTEX,{"derivedFrom":[subQ1,subQ0]});Q336=makeQuery(id+"F25.imprint","IMPRINT",FACE,{"disambiguationData":[TD([[makeQuery(id+"F25.imprint","IMPRINT",EDGE,{"disambiguationData":[TD([[subQ2,1.0]])],"derivedFrom":subQ1}),1.0]])]});}
            var Q337;
            {var subQ0=sQuery(id+"F25.wireOp",EDGE,"E547.trimOffspring");var subQ1=sQuery(id+"F25.wireOp",EDGE,"E445.MirrorCS");var subQ2=makeQuery(id+"F25.imprint","INTERSECT",VERTEX,{"derivedFrom":[subQ1,subQ0]});Q337=makeQuery(id+"F25.imprint","IMPRINT",FACE,{"disambiguationData":[TD([[makeQuery(id+"F25.imprint","IMPRINT",EDGE,{"disambiguationData":[TD([[subQ2,1.0]])],"derivedFrom":subQ1}),1.0]])]});}
            var Q338;
            {var subQ3=sQuery(id+"F25.wireOp",EDGE,"E563.trimOffspring");Q338=makeQuery(id+"F25.imprint","IMPRINT",FACE,{"disambiguationData":[TD([[makeQuery(id+"F25.imprint","IMPRINT",EDGE,{"derivedFrom":subQ3}),1.0]])]});}
            var Q339;
            {var subQ3=sQuery(id+"F25.wireOp",EDGE,"E563.trimOffspring");Q339=makeQuery(id+"F25.imprint","IMPRINT",FACE,{"disambiguationData":[TD([[makeQuery(id+"F25.imprint","IMPRINT",EDGE,{"derivedFrom":subQ3}),-1.0]])]});}
            var Q340;
            {var subQ3=sQuery(id+"F25.wireOp",EDGE,"E560.trimOffspring");var subQ5=sQuery(id+"F25.wireOp",EDGE,"E434.MirrorCS");var subQ6=makeQuery(id+"F25.imprint","INTERSECT",VERTEX,{"derivedFrom":[subQ5,subQ3]});Q340=makeQuery(id+"F25.imprint","IMPRINT",FACE,{"disambiguationData":[TD([[makeQuery(id+"F25.imprint","IMPRINT",EDGE,{"disambiguationData":[TD([[subQ6,-1.0]])],"derivedFrom":subQ5}),-1.0]])]});}
            var Q341;
            {var subQ3=sQuery(id+"F25.wireOp",EDGE,"E559.trimOffspring");var subQ5=sQuery(id+"F25.wireOp",EDGE,"E434.MirrorCS");var subQ6=makeQuery(id+"F25.imprint","INTERSECT",VERTEX,{"derivedFrom":[subQ5,subQ3]});Q341=makeQuery(id+"F25.imprint","IMPRINT",FACE,{"disambiguationData":[TD([[makeQuery(id+"F25.imprint","IMPRINT",EDGE,{"disambiguationData":[TD([[subQ6,1.0]])],"derivedFrom":subQ5}),-1.0]])]});}
            var Q342;
            {var subQ0=sQuery(id+"F25.wireOp",EDGE,"E559.trimOffspring");var subQ1=sQuery(id+"F25.wireOp",EDGE,"E443.MirrorCS");var subQ2=makeQuery(id+"F25.imprint","INTERSECT",VERTEX,{"derivedFrom":[subQ1,subQ0]});Q342=makeQuery(id+"F25.imprint","IMPRINT",FACE,{"disambiguationData":[TD([[makeQuery(id+"F25.imprint","IMPRINT",EDGE,{"disambiguationData":[TD([[subQ2,1.0]])],"derivedFrom":subQ1}),-1.0]])]});}
            var Q343;
            {var subQ0=sQuery(id+"F25.wireOp",EDGE,"E559.trimOffspring");var subQ1=sQuery(id+"F25.wireOp",EDGE,"E443.MirrorCS");var subQ2=makeQuery(id+"F25.imprint","INTERSECT",VERTEX,{"derivedFrom":[subQ1,subQ0]});Q343=makeQuery(id+"F25.imprint","IMPRINT",FACE,{"disambiguationData":[TD([[makeQuery(id+"F25.imprint","IMPRINT",EDGE,{"disambiguationData":[TD([[subQ2,1.0]])],"derivedFrom":subQ1}),1.0]])]});}
            var Q344;
            {var subQ0=sQuery(id+"F25.wireOp",EDGE,"E571.trimOffspring");var subQ1=sQuery(id+"F25.wireOp",EDGE,"E559.trimOffspring");var subQ2=makeQuery(id+"F25.imprint","INTERSECT",VERTEX,{"derivedFrom":[subQ1,subQ0]});Q344=makeQuery(id+"F25.imprint","IMPRINT",FACE,{"disambiguationData":[TD([[makeQuery(id+"F25.imprint","IMPRINT",EDGE,{"disambiguationData":[TD([[subQ2,-1.0]])],"derivedFrom":subQ1}),1.0]])]});}
            var Q345;
            {var subQ0=sQuery(id+"F25.wireOp",EDGE,"E583.trimOffspring");var subQ1=sQuery(id+"F25.wireOp",EDGE,"E559.trimOffspring");var subQ2=makeQuery(id+"F25.imprint","INTERSECT",VERTEX,{"derivedFrom":[subQ1,subQ0]});Q345=makeQuery(id+"F25.imprint","IMPRINT",FACE,{"disambiguationData":[TD([[makeQuery(id+"F25.imprint","IMPRINT",EDGE,{"disambiguationData":[TD([[subQ2,1.0]])],"derivedFrom":subQ1}),1.0]])]});}
            var Q346;
            {var subQ0=sQuery(id+"F25.wireOp",EDGE,"E583.trimOffspring");var subQ1=sQuery(id+"F25.wireOp",EDGE,"E560.trimOffspring");var subQ2=makeQuery(id+"F25.imprint","INTERSECT",VERTEX,{"derivedFrom":[subQ1,subQ0]});Q346=makeQuery(id+"F25.imprint","IMPRINT",FACE,{"disambiguationData":[TD([[makeQuery(id+"F25.imprint","IMPRINT",EDGE,{"disambiguationData":[TD([[subQ2,1.0]])],"derivedFrom":subQ1}),-1.0]])]});}
            var Q347;
            {var subQ0=sQuery(id+"F25.wireOp",EDGE,"E583.trimOffspring");var subQ1=sQuery(id+"F25.wireOp",EDGE,"E560.trimOffspring");var subQ2=makeQuery(id+"F25.imprint","INTERSECT",VERTEX,{"derivedFrom":[subQ1,subQ0]});Q347=makeQuery(id+"F25.imprint","IMPRINT",FACE,{"disambiguationData":[TD([[makeQuery(id+"F25.imprint","IMPRINT",EDGE,{"disambiguationData":[TD([[subQ2,1.0]])],"derivedFrom":subQ1}),1.0]])]});}
            var Q348;
            {var subQ0=sQuery(id+"F25.wireOp",EDGE,"E572.trimOffspring");var subQ1=sQuery(id+"F25.wireOp",EDGE,"E568.trimOffspring");var subQ2=makeQuery(id+"F25.imprint","INTERSECT",VERTEX,{"derivedFrom":[subQ1,subQ0]});Q348=makeQuery(id+"F25.imprint","IMPRINT",FACE,{"disambiguationData":[TD([[makeQuery(id+"F25.imprint","IMPRINT",EDGE,{"disambiguationData":[TD([[subQ2,-1.0]])],"derivedFrom":subQ1}),1.0]])]});}
            var Q349;
            {var subQ0=sQuery(id+"F25.wireOp",EDGE,"E583.trimOffspring");var subQ1=sQuery(id+"F25.wireOp",EDGE,"E568.trimOffspring");var subQ2=makeQuery(id+"F25.imprint","INTERSECT",VERTEX,{"derivedFrom":[subQ1,subQ0]});Q349=makeQuery(id+"F25.imprint","IMPRINT",FACE,{"disambiguationData":[TD([[makeQuery(id+"F25.imprint","IMPRINT",EDGE,{"disambiguationData":[TD([[subQ2,-1.0]])],"derivedFrom":subQ1}),1.0]])]});}
            var Q350;
            {var subQ0=sQuery(id+"F25.wireOp",EDGE,"E596.trimOffspring");var subQ1=sQuery(id+"F25.wireOp",EDGE,"E568.trimOffspring");var subQ2=makeQuery(id+"F25.imprint","INTERSECT",VERTEX,{"derivedFrom":[subQ1,subQ0]});Q350=makeQuery(id+"F25.imprint","IMPRINT",FACE,{"disambiguationData":[TD([[makeQuery(id+"F25.imprint","IMPRINT",EDGE,{"disambiguationData":[TD([[subQ2,-1.0]])],"derivedFrom":subQ1}),1.0]])]});}
            var Q351;
            {var subQ0=sQuery(id+"F25.wireOp",EDGE,"E598.trimOffspring");var subQ1=sQuery(id+"F25.wireOp",EDGE,"E568.trimOffspring");var subQ2=makeQuery(id+"F25.imprint","INTERSECT",VERTEX,{"derivedFrom":[subQ1,subQ0]});Q351=makeQuery(id+"F25.imprint","IMPRINT",FACE,{"disambiguationData":[TD([[makeQuery(id+"F25.imprint","IMPRINT",EDGE,{"disambiguationData":[TD([[subQ2,-1.0]])],"derivedFrom":subQ1}),1.0]])]});}
            var Q352;
            {var subQ1=sQuery(id+"F25.wireOp",EDGE,"E481.trimOffspring");var subQ3=sQuery(id+"F25.wireOp",EDGE,"E567.trimOffspring");var subQ4=makeQuery(id+"F25.imprint","INTERSECT",VERTEX,{"derivedFrom":[subQ1,subQ3]});Q352=makeQuery(id+"F25.imprint","IMPRINT",FACE,{"disambiguationData":[TD([[makeQuery(id+"F25.imprint","IMPRINT",EDGE,{"disambiguationData":[TD([[subQ4,1.0]])],"derivedFrom":subQ3}),-1.0]])]});}
            var Q353;
            {var subQ0=sQuery(id+"F25.wireOp",EDGE,"E608.trimOffspring");var subQ1=sQuery(id+"F25.wireOp",EDGE,"E423.MirrorCS");var subQ2=makeQuery(id+"F25.imprint","INTERSECT",VERTEX,{"derivedFrom":[subQ1,subQ0]});Q353=makeQuery(id+"F25.imprint","IMPRINT",FACE,{"disambiguationData":[TD([[makeQuery(id+"F25.imprint","IMPRINT",EDGE,{"disambiguationData":[TD([[subQ2,-1.0]])],"derivedFrom":subQ1}),-1.0]])]});}
            var Q354;
            {var subQ0=sQuery(id+"F25.wireOp",EDGE,"E608.trimOffspring");var subQ1=sQuery(id+"F25.wireOp",EDGE,"E483.trimOffspring");var subQ2=makeQuery(id+"F25.imprint","INTERSECT",VERTEX,{"derivedFrom":[subQ1,subQ0]});Q354=makeQuery(id+"F25.imprint","IMPRINT",FACE,{"disambiguationData":[TD([[makeQuery(id+"F25.imprint","IMPRINT",EDGE,{"disambiguationData":[TD([[subQ2,-1.0]])],"derivedFrom":subQ1}),-1.0]])]});}
            var Q355;
            {var subQ3=sQuery(id+"F25.wireOp",EDGE,"E599.trimOffspring");var subQ5=sQuery(id+"F25.wireOp",EDGE,"E484.trimOffspring");var subQ6=makeQuery(id+"F25.imprint","INTERSECT",VERTEX,{"derivedFrom":[subQ5,subQ3]});Q355=makeQuery(id+"F25.imprint","IMPRINT",FACE,{"disambiguationData":[TD([[makeQuery(id+"F25.imprint","IMPRINT",EDGE,{"disambiguationData":[TD([[subQ6,-1.0]])],"derivedFrom":subQ5}),1.0]])]});}
            var Q356;
            {var subQ0=sQuery(id+"F25.wireOp",EDGE,"E570.trimOffspring");var subQ5=sQuery(id+"F25.wireOp",EDGE,"E484.trimOffspring");var subQ6=makeQuery(id+"F25.imprint","INTERSECT",VERTEX,{"derivedFrom":[subQ5,subQ0]});Q356=makeQuery(id+"F25.imprint","IMPRINT",FACE,{"disambiguationData":[TD([[makeQuery(id+"F25.imprint","IMPRINT",EDGE,{"disambiguationData":[TD([[subQ6,-1.0]])],"derivedFrom":subQ5}),1.0]])]});}
            var Q357;
            {var subQ0=sQuery(id+"F25.wireOp",EDGE,"E565.trimOffspring");var subQ1=sQuery(id+"F25.wireOp",EDGE,"E483.trimOffspring");var subQ2=makeQuery(id+"F25.imprint","INTERSECT",VERTEX,{"derivedFrom":[subQ1,subQ0]});Q357=makeQuery(id+"F25.imprint","IMPRINT",FACE,{"disambiguationData":[TD([[makeQuery(id+"F25.imprint","IMPRINT",EDGE,{"disambiguationData":[TD([[subQ2,1.0]])],"derivedFrom":subQ1}),-1.0]])]});}
            var Q358;
            {var subQ0=sQuery(id+"F25.wireOp",EDGE,"E565.trimOffspring");var subQ5=sQuery(id+"F25.wireOp",EDGE,"E484.trimOffspring");var subQ6=makeQuery(id+"F25.imprint","INTERSECT",VERTEX,{"derivedFrom":[subQ5,subQ0]});Q358=makeQuery(id+"F25.imprint","IMPRINT",FACE,{"disambiguationData":[TD([[makeQuery(id+"F25.imprint","IMPRINT",EDGE,{"disambiguationData":[TD([[subQ6,1.0]])],"derivedFrom":subQ5}),-1.0]])]});}
            var Q359;
            {var subQ0=sQuery(id+"F25.wireOp",EDGE,"E570.trimOffspring");var subQ5=sQuery(id+"F25.wireOp",EDGE,"E484.trimOffspring");var subQ6=makeQuery(id+"F25.imprint","INTERSECT",VERTEX,{"derivedFrom":[subQ5,subQ0]});Q359=makeQuery(id+"F25.imprint","IMPRINT",FACE,{"disambiguationData":[TD([[makeQuery(id+"F25.imprint","IMPRINT",EDGE,{"disambiguationData":[TD([[subQ6,-1.0]])],"derivedFrom":subQ5}),1.0]])]});}
            var Q360;
            {var subQ0=sQuery(id+"F25.wireOp",EDGE,"E565.trimOffspring");var subQ1=sQuery(id+"F25.wireOp",EDGE,"E483.trimOffspring");var subQ2=makeQuery(id+"F25.imprint","INTERSECT",VERTEX,{"derivedFrom":[subQ1,subQ0]});Q360=makeQuery(id+"F25.imprint","IMPRINT",FACE,{"disambiguationData":[TD([[makeQuery(id+"F25.imprint","IMPRINT",EDGE,{"disambiguationData":[TD([[subQ2,1.0]])],"derivedFrom":subQ1}),-1.0]])]});}
            var Q361;
            {var subQ0=sQuery(id+"F25.wireOp",EDGE,"E598.trimOffspring");var subQ1=sQuery(id+"F25.wireOp",EDGE,"E568.trimOffspring");var subQ2=makeQuery(id+"F25.imprint","INTERSECT",VERTEX,{"derivedFrom":[subQ1,subQ0]});Q361=makeQuery(id+"F25.imprint","IMPRINT",FACE,{"disambiguationData":[TD([[makeQuery(id+"F25.imprint","IMPRINT",EDGE,{"disambiguationData":[TD([[subQ2,-1.0]])],"derivedFrom":subQ1}),-1.0]])]});}
            var Q362;
            {var subQ0=sQuery(id+"F25.wireOp",EDGE,"E596.trimOffspring");var subQ1=sQuery(id+"F25.wireOp",EDGE,"E568.trimOffspring");var subQ2=makeQuery(id+"F25.imprint","INTERSECT",VERTEX,{"derivedFrom":[subQ1,subQ0]});Q362=makeQuery(id+"F25.imprint","IMPRINT",FACE,{"disambiguationData":[TD([[makeQuery(id+"F25.imprint","IMPRINT",EDGE,{"disambiguationData":[TD([[subQ2,-1.0]])],"derivedFrom":subQ1}),-1.0]])]});}
            var Q363;
            {var subQ0=sQuery(id+"F25.wireOp",EDGE,"E577.trimOffspring");var subQ1=sQuery(id+"F25.wireOp",EDGE,"E454.MirrorCS");var subQ2=makeQuery(id+"F25.imprint","INTERSECT",VERTEX,{"derivedFrom":[subQ1,subQ0]});Q363=makeQuery(id+"F25.imprint","IMPRINT",FACE,{"disambiguationData":[TD([[makeQuery(id+"F25.imprint","IMPRINT",EDGE,{"disambiguationData":[TD([[subQ2,-1.0]])],"derivedFrom":subQ1}),1.0]])]});}
            var Q364;
            {var subQ0=sQuery(id+"F25.wireOp",EDGE,"E577.trimOffspring");var subQ1=sQuery(id+"F25.wireOp",EDGE,"E456.MirrorCS");var subQ2=makeQuery(id+"F25.imprint","INTERSECT",VERTEX,{"derivedFrom":[subQ1,subQ0]});Q364=makeQuery(id+"F25.imprint","IMPRINT",FACE,{"disambiguationData":[TD([[makeQuery(id+"F25.imprint","IMPRINT",EDGE,{"disambiguationData":[TD([[subQ2,-1.0]])],"derivedFrom":subQ1}),-1.0]])]});}
            var Q365;
            {var subQ0=sQuery(id+"F25.wireOp",EDGE,"E596.trimOffspring");var subQ1=sQuery(id+"F25.wireOp",EDGE,"E582.trimOffspring");var subQ2=makeQuery(id+"F25.imprint","INTERSECT",VERTEX,{"derivedFrom":[subQ1,subQ0]});Q365=makeQuery(id+"F25.imprint","IMPRINT",FACE,{"disambiguationData":[TD([[makeQuery(id+"F25.imprint","IMPRINT",EDGE,{"disambiguationData":[TD([[subQ2,-1.0]])],"derivedFrom":subQ1}),-1.0]])]});}
            var Q366;
            {var subQ0=sQuery(id+"F25.wireOp",EDGE,"E596.trimOffspring");var subQ1=sQuery(id+"F25.wireOp",EDGE,"E576.trimOffspring");var subQ2=makeQuery(id+"F25.imprint","INTERSECT",VERTEX,{"derivedFrom":[subQ1,subQ0]});Q366=makeQuery(id+"F25.imprint","IMPRINT",FACE,{"disambiguationData":[TD([[makeQuery(id+"F25.imprint","IMPRINT",EDGE,{"disambiguationData":[TD([[subQ2,-1.0]])],"derivedFrom":subQ1}),1.0]])]});}
            var Q367;
            {var subQ0=sQuery(id+"F25.wireOp",EDGE,"E598.trimOffspring");var subQ1=sQuery(id+"F25.wireOp",EDGE,"E582.trimOffspring");var subQ2=makeQuery(id+"F25.imprint","INTERSECT",VERTEX,{"derivedFrom":[subQ1,subQ0]});Q367=makeQuery(id+"F25.imprint","IMPRINT",FACE,{"disambiguationData":[TD([[makeQuery(id+"F25.imprint","IMPRINT",EDGE,{"disambiguationData":[TD([[subQ2,-1.0]])],"derivedFrom":subQ1}),-1.0]])]});}
            var Q368;
            {var subQ0=sQuery(id+"F25.wireOp",EDGE,"E597.trimOffspring");var subQ1=sQuery(id+"F25.wireOp",EDGE,"E576.trimOffspring");var subQ2=makeQuery(id+"F25.imprint","INTERSECT",VERTEX,{"derivedFrom":[subQ1,subQ0]});Q368=makeQuery(id+"F25.imprint","IMPRINT",FACE,{"disambiguationData":[TD([[makeQuery(id+"F25.imprint","IMPRINT",EDGE,{"disambiguationData":[TD([[subQ2,1.0]])],"derivedFrom":subQ1}),1.0]])]});}
            var Q369;
            {var subQ0=sQuery(id+"F25.wireOp",EDGE,"E597.trimOffspring");var subQ1=sQuery(id+"F25.wireOp",EDGE,"E576.trimOffspring");var subQ2=makeQuery(id+"F25.imprint","INTERSECT",VERTEX,{"derivedFrom":[subQ1,subQ0]});Q369=makeQuery(id+"F25.imprint","IMPRINT",FACE,{"disambiguationData":[TD([[makeQuery(id+"F25.imprint","IMPRINT",EDGE,{"disambiguationData":[TD([[subQ2,-1.0]])],"derivedFrom":subQ1}),1.0]])]});}
            var Q370;
            {var subQ0=sQuery(id+"F25.wireOp",EDGE,"E582.trimOffspring");var subQ1=sQuery(id+"F25.wireOp",EDGE,"E585.trimOffspring");var subQ2=makeQuery(id+"F25.imprint","INTERSECT",VERTEX,{"derivedFrom":[subQ1,subQ0]});Q370=makeQuery(id+"F25.imprint","IMPRINT",FACE,{"disambiguationData":[TD([[makeQuery(id+"F25.imprint","IMPRINT",EDGE,{"disambiguationData":[TD([[subQ2,-1.0]])],"derivedFrom":subQ1}),-1.0]])]});}
            var Q371;
            {var subQ0=sQuery(id+"F25.wireOp",EDGE,"E582.trimOffspring");var subQ1=sQuery(id+"F25.wireOp",EDGE,"E585.trimOffspring");var subQ2=makeQuery(id+"F25.imprint","INTERSECT",VERTEX,{"derivedFrom":[subQ1,subQ0]});Q371=makeQuery(id+"F25.imprint","IMPRINT",FACE,{"disambiguationData":[TD([[makeQuery(id+"F25.imprint","IMPRINT",EDGE,{"disambiguationData":[TD([[subQ2,-1.0]])],"derivedFrom":subQ1}),1.0]])]});}
            var Q372;
            {var subQ0=sQuery(id+"F25.wireOp",EDGE,"E585.trimOffspring");var subQ1=sQuery(id+"F25.wireOp",EDGE,"E576.trimOffspring");var subQ2=makeQuery(id+"F25.imprint","INTERSECT",VERTEX,{"derivedFrom":[subQ1,subQ0]});Q372=makeQuery(id+"F25.imprint","IMPRINT",FACE,{"disambiguationData":[TD([[makeQuery(id+"F25.imprint","IMPRINT",EDGE,{"disambiguationData":[TD([[subQ2,-1.0]])],"derivedFrom":subQ1}),1.0]])]});}
            var Q373;
            {var subQ0=sQuery(id+"F25.wireOp",EDGE,"E589.trimOffspring");var subQ1=sQuery(id+"F25.wireOp",EDGE,"E576.trimOffspring");var subQ2=makeQuery(id+"F25.imprint","INTERSECT",VERTEX,{"derivedFrom":[subQ1,subQ0]});Q373=makeQuery(id+"F25.imprint","IMPRINT",FACE,{"disambiguationData":[TD([[makeQuery(id+"F25.imprint","IMPRINT",EDGE,{"disambiguationData":[TD([[subQ2,1.0]])],"derivedFrom":subQ1}),1.0]])]});}
            var Q374;
            {var subQ0=sQuery(id+"F25.wireOp",EDGE,"E433.MirrorCS");Q374=makeQuery(id+"F25.imprint","IMPRINT",FACE,{"disambiguationData":[TD([[makeQuery(id+"F25.imprint","IMPRINT",EDGE,{"derivedFrom":subQ0}),1.0]])]});}
            var Q375;
            {var subQ3=sQuery(id+"F25.wireOp",EDGE,"E585.trimOffspring");var subQ5=sQuery(id+"F25.wireOp",EDGE,"E576.trimOffspring");var subQ6=makeQuery(id+"F25.imprint","INTERSECT",VERTEX,{"derivedFrom":[subQ5,subQ3]});Q375=makeQuery(id+"F25.imprint","IMPRINT",FACE,{"disambiguationData":[TD([[makeQuery(id+"F25.imprint","IMPRINT",EDGE,{"disambiguationData":[TD([[subQ6,-1.0]])],"derivedFrom":subQ5}),-1.0]])]});}
            var Q376;
            {var subQ0=sQuery(id+"F25.wireOp",EDGE,"E589.trimOffspring");var subQ1=sQuery(id+"F25.wireOp",EDGE,"E582.trimOffspring");var subQ2=makeQuery(id+"F25.imprint","INTERSECT",VERTEX,{"derivedFrom":[subQ1,subQ0]});Q376=makeQuery(id+"F25.imprint","IMPRINT",FACE,{"disambiguationData":[TD([[makeQuery(id+"F25.imprint","IMPRINT",EDGE,{"disambiguationData":[TD([[subQ2,1.0]])],"derivedFrom":subQ1}),-1.0]])]});}
            var Q377;
            {var subQ0=sQuery(id+"F25.wireOp",EDGE,"E578.trimOffspring");var subQ1=sQuery(id+"F25.wireOp",EDGE,"E454.MirrorCS");var subQ2=makeQuery(id+"F25.imprint","INTERSECT",VERTEX,{"derivedFrom":[subQ1,subQ0]});Q377=makeQuery(id+"F25.imprint","IMPRINT",FACE,{"disambiguationData":[TD([[makeQuery(id+"F25.imprint","IMPRINT",EDGE,{"disambiguationData":[TD([[subQ2,-1.0]])],"derivedFrom":subQ1}),1.0]])]});}
            var Q378;
            {var subQ0=sQuery(id+"F25.wireOp",EDGE,"E574.trimOffspring");var subQ1=sQuery(id+"F25.wireOp",EDGE,"E456.MirrorCS");var subQ2=makeQuery(id+"F25.imprint","INTERSECT",VERTEX,{"derivedFrom":[subQ1,subQ0]});Q378=makeQuery(id+"F25.imprint","IMPRINT",FACE,{"disambiguationData":[TD([[makeQuery(id+"F25.imprint","IMPRINT",EDGE,{"disambiguationData":[TD([[subQ2,1.0]])],"derivedFrom":subQ1}),-1.0]])]});}
            var Q379;
            {var subQ0=sQuery(id+"F25.wireOp",EDGE,"E574.trimOffspring");var subQ1=sQuery(id+"F25.wireOp",EDGE,"E454.MirrorCS");var subQ2=makeQuery(id+"F25.imprint","INTERSECT",VERTEX,{"derivedFrom":[subQ1,subQ0]});Q379=makeQuery(id+"F25.imprint","IMPRINT",FACE,{"disambiguationData":[TD([[makeQuery(id+"F25.imprint","IMPRINT",EDGE,{"disambiguationData":[TD([[subQ2,-1.0]])],"derivedFrom":subQ1}),1.0]])]});}
            var Q380;
            {var subQ0=sQuery(id+"F25.wireOp",EDGE,"E574.trimOffspring");var subQ1=sQuery(id+"F25.wireOp",EDGE,"E456.MirrorCS");var subQ2=makeQuery(id+"F25.imprint","INTERSECT",VERTEX,{"derivedFrom":[subQ1,subQ0]});Q380=makeQuery(id+"F25.imprint","IMPRINT",FACE,{"disambiguationData":[TD([[makeQuery(id+"F25.imprint","IMPRINT",EDGE,{"disambiguationData":[TD([[subQ2,-1.0]])],"derivedFrom":subQ1}),-1.0]])]});}
            var Q381;
            {var subQ0=sQuery(id+"F25.wireOp",EDGE,"E580.trimOffspring");var subQ1=sQuery(id+"F25.wireOp",EDGE,"E454.MirrorCS");var subQ2=makeQuery(id+"F25.imprint","INTERSECT",VERTEX,{"derivedFrom":[subQ1,subQ0]});Q381=makeQuery(id+"F25.imprint","IMPRINT",FACE,{"disambiguationData":[TD([[makeQuery(id+"F25.imprint","IMPRINT",EDGE,{"disambiguationData":[TD([[subQ2,-1.0]])],"derivedFrom":subQ1}),1.0]])]});}
            var Q382;
            {var subQ0=sQuery(id+"F25.wireOp",EDGE,"E580.trimOffspring");var subQ1=sQuery(id+"F25.wireOp",EDGE,"E456.MirrorCS");var subQ2=makeQuery(id+"F25.imprint","INTERSECT",VERTEX,{"derivedFrom":[subQ1,subQ0]});Q382=makeQuery(id+"F25.imprint","IMPRINT",FACE,{"disambiguationData":[TD([[makeQuery(id+"F25.imprint","IMPRINT",EDGE,{"disambiguationData":[TD([[subQ2,-1.0]])],"derivedFrom":subQ1}),-1.0]])]});}
            var Q383;
            {var subQ0=sQuery(id+"F25.wireOp",EDGE,"E579.trimOffspring");var subQ1=sQuery(id+"F25.wireOp",EDGE,"E454.MirrorCS");var subQ2=makeQuery(id+"F25.imprint","INTERSECT",VERTEX,{"derivedFrom":[subQ1,subQ0]});Q383=makeQuery(id+"F25.imprint","IMPRINT",FACE,{"disambiguationData":[TD([[makeQuery(id+"F25.imprint","IMPRINT",EDGE,{"disambiguationData":[TD([[subQ2,-1.0]])],"derivedFrom":subQ1}),1.0]])]});}
            var Q384;
            {var subQ0=sQuery(id+"F25.wireOp",EDGE,"E581.trimOffspring");var subQ1=sQuery(id+"F25.wireOp",EDGE,"E456.MirrorCS");var subQ2=makeQuery(id+"F25.imprint","INTERSECT",VERTEX,{"derivedFrom":[subQ1,subQ0]});Q384=makeQuery(id+"F25.imprint","IMPRINT",FACE,{"disambiguationData":[TD([[makeQuery(id+"F25.imprint","IMPRINT",EDGE,{"disambiguationData":[TD([[subQ2,1.0]])],"derivedFrom":subQ1}),-1.0]])]});}
            var Q385;
            {var subQ0=sQuery(id+"F25.wireOp",EDGE,"E581.trimOffspring");var subQ1=sQuery(id+"F25.wireOp",EDGE,"E454.MirrorCS");var subQ2=makeQuery(id+"F25.imprint","INTERSECT",VERTEX,{"derivedFrom":[subQ1,subQ0]});Q385=makeQuery(id+"F25.imprint","IMPRINT",FACE,{"disambiguationData":[TD([[makeQuery(id+"F25.imprint","IMPRINT",EDGE,{"disambiguationData":[TD([[subQ2,-1.0]])],"derivedFrom":subQ1}),1.0]])]});}
            var Q386;
            {var subQ0=sQuery(id+"F25.wireOp",EDGE,"E581.trimOffspring");var subQ1=sQuery(id+"F25.wireOp",EDGE,"E456.MirrorCS");var subQ2=makeQuery(id+"F25.imprint","INTERSECT",VERTEX,{"derivedFrom":[subQ1,subQ0]});Q386=makeQuery(id+"F25.imprint","IMPRINT",FACE,{"disambiguationData":[TD([[makeQuery(id+"F25.imprint","IMPRINT",EDGE,{"disambiguationData":[TD([[subQ2,-1.0]])],"derivedFrom":subQ1}),-1.0]])]});}
            var Q387;
            {var subQ0=sQuery(id+"F25.wireOp",EDGE,"E585.trimOffspring");var subQ1=sQuery(id+"F25.wireOp",EDGE,"E454.MirrorCS");var subQ2=makeQuery(id+"F25.imprint","INTERSECT",VERTEX,{"derivedFrom":[subQ1,subQ0]});Q387=makeQuery(id+"F25.imprint","IMPRINT",FACE,{"disambiguationData":[TD([[makeQuery(id+"F25.imprint","IMPRINT",EDGE,{"disambiguationData":[TD([[subQ2,-1.0]])],"derivedFrom":subQ1}),1.0]])]});}
            var Q388;
            {var subQ3=sQuery(id+"F25.wireOp",EDGE,"E585.trimOffspring");var subQ5=sQuery(id+"F25.wireOp",EDGE,"E441.MirrorCS");var subQ6=makeQuery(id+"F25.imprint","INTERSECT",VERTEX,{"derivedFrom":[subQ5,subQ3]});Q388=makeQuery(id+"F25.imprint","IMPRINT",FACE,{"disambiguationData":[TD([[makeQuery(id+"F25.imprint","IMPRINT",EDGE,{"disambiguationData":[TD([[subQ6,-1.0]])],"derivedFrom":subQ5}),1.0]])]});}
            var Q389;
            {var subQ0=sQuery(id+"F25.wireOp",EDGE,"E433.MirrorCS");Q389=makeQuery(id+"F25.imprint","IMPRINT",FACE,{"disambiguationData":[TD([[makeQuery(id+"F25.imprint","IMPRINT",EDGE,{"derivedFrom":subQ0}),-1.0]])]});}
            var Q390;
            {var subQ0=sQuery(id+"F25.wireOp",EDGE,"E589.trimOffspring");var subQ1=sQuery(id+"F25.wireOp",EDGE,"E454.MirrorCS");var subQ2=makeQuery(id+"F25.imprint","INTERSECT",VERTEX,{"derivedFrom":[subQ1,subQ0]});Q390=makeQuery(id+"F25.imprint","IMPRINT",FACE,{"disambiguationData":[TD([[makeQuery(id+"F25.imprint","IMPRINT",EDGE,{"disambiguationData":[TD([[subQ2,1.0]])],"derivedFrom":subQ1}),1.0]])]});}
            var Q391;
            {var subQ0=sQuery(id+"F25.wireOp",EDGE,"E608.trimOffspring");var subQ1=sQuery(id+"F25.wireOp",EDGE,"E423.MirrorCS");var subQ2=makeQuery(id+"F25.imprint","INTERSECT",VERTEX,{"derivedFrom":[subQ1,subQ0]});Q391=makeQuery(id+"F25.imprint","IMPRINT",FACE,{"disambiguationData":[TD([[makeQuery(id+"F25.imprint","IMPRINT",EDGE,{"disambiguationData":[TD([[subQ2,-1.0]])],"derivedFrom":subQ1}),1.0]])]});}
            var Q392;
            {var subQ0=sQuery(id+"F25.wireOp",EDGE,"E608.trimOffspring");var subQ1=sQuery(id+"F25.wireOp",EDGE,"E427.MirrorCS");var subQ2=makeQuery(id+"F25.imprint","INTERSECT",VERTEX,{"derivedFrom":[subQ1,subQ0]});Q392=makeQuery(id+"F25.imprint","IMPRINT",FACE,{"disambiguationData":[TD([[makeQuery(id+"F25.imprint","IMPRINT",EDGE,{"disambiguationData":[TD([[subQ2,-1.0]])],"derivedFrom":subQ1}),1.0]])]});}
            var Q393;
            {var subQ0=sQuery(id+"F25.wireOp",EDGE,"E584.trimOffspring");Q393=makeQuery(id+"F25.imprint","IMPRINT",FACE,{"disambiguationData":[TD([[makeQuery(id+"F25.imprint","IMPRINT",EDGE,{"derivedFrom":subQ0}),1.0]])]});}
            var Q394;
            {var subQ3=sQuery(id+"F25.wireOp",EDGE,"E608.trimOffspring");var subQ5=sQuery(id+"F25.wireOp",EDGE,"E448.MirrorCS");var subQ6=makeQuery(id+"F25.imprint","INTERSECT",VERTEX,{"derivedFrom":[subQ5,subQ3]});Q394=makeQuery(id+"F25.imprint","IMPRINT",FACE,{"disambiguationData":[TD([[makeQuery(id+"F25.imprint","IMPRINT",EDGE,{"disambiguationData":[TD([[subQ6,-1.0]])],"derivedFrom":subQ5}),-1.0]])]});}
            var Q395;
            {var subQ0=sQuery(id+"F25.wireOp",EDGE,"E608.trimOffspring");var subQ1=sQuery(id+"F25.wireOp",EDGE,"E431.MirrorCS");var subQ2=makeQuery(id+"F25.imprint","INTERSECT",VERTEX,{"derivedFrom":[subQ1,subQ0]});Q395=makeQuery(id+"F25.imprint","IMPRINT",FACE,{"disambiguationData":[TD([[makeQuery(id+"F25.imprint","IMPRINT",EDGE,{"disambiguationData":[TD([[subQ2,-1.0]])],"derivedFrom":subQ1}),-1.0]])]});}
            var Q396;
            {var subQ0=sQuery(id+"F25.wireOp",EDGE,"E608.trimOffspring");var subQ1=sQuery(id+"F25.wireOp",EDGE,"E431.MirrorCS");var subQ2=makeQuery(id+"F25.imprint","INTERSECT",VERTEX,{"derivedFrom":[subQ1,subQ0]});Q396=makeQuery(id+"F25.imprint","IMPRINT",FACE,{"disambiguationData":[TD([[makeQuery(id+"F25.imprint","IMPRINT",EDGE,{"disambiguationData":[TD([[subQ2,-1.0]])],"derivedFrom":subQ1}),1.0]])]});}
            var Q397;
            {var subQ0=sQuery(id+"F25.wireOp",EDGE,"E608.trimOffspring");var subQ1=sQuery(id+"F25.wireOp",EDGE,"E446.MirrorCS");var subQ2=makeQuery(id+"F25.imprint","INTERSECT",VERTEX,{"derivedFrom":[subQ1,subQ0]});Q397=makeQuery(id+"F25.imprint","IMPRINT",FACE,{"disambiguationData":[TD([[makeQuery(id+"F25.imprint","IMPRINT",EDGE,{"disambiguationData":[TD([[subQ2,-1.0]])],"derivedFrom":subQ1}),1.0]])]});}
            var Q398;
            {var subQ0=sQuery(id+"F25.wireOp",EDGE,"E608.trimOffspring");var subQ1=sQuery(id+"F25.wireOp",EDGE,"E444.MirrorCS");var subQ2=makeQuery(id+"F25.imprint","INTERSECT",VERTEX,{"derivedFrom":[subQ1,subQ0]});Q398=makeQuery(id+"F25.imprint","IMPRINT",FACE,{"disambiguationData":[TD([[makeQuery(id+"F25.imprint","IMPRINT",EDGE,{"disambiguationData":[TD([[subQ2,-1.0]])],"derivedFrom":subQ1}),-1.0]])]});}
            var Q399;
            {var subQ0=sQuery(id+"F25.wireOp",EDGE,"E603.trimOffspring");var subQ1=sQuery(id+"F25.wireOp",EDGE,"E444.MirrorCS");var subQ2=makeQuery(id+"F25.imprint","INTERSECT",VERTEX,{"derivedFrom":[subQ1,subQ0]});Q399=makeQuery(id+"F25.imprint","IMPRINT",FACE,{"disambiguationData":[TD([[makeQuery(id+"F25.imprint","IMPRINT",EDGE,{"disambiguationData":[TD([[subQ2,-1.0]])],"derivedFrom":subQ1}),-1.0]])]});}
            var Q400;
            {var subQ0=sQuery(id+"F25.wireOp",EDGE,"E603.trimOffspring");var subQ1=sQuery(id+"F25.wireOp",EDGE,"E446.MirrorCS");var subQ2=makeQuery(id+"F25.imprint","INTERSECT",VERTEX,{"derivedFrom":[subQ1,subQ0]});Q400=makeQuery(id+"F25.imprint","IMPRINT",FACE,{"disambiguationData":[TD([[makeQuery(id+"F25.imprint","IMPRINT",EDGE,{"disambiguationData":[TD([[subQ2,-1.0]])],"derivedFrom":subQ1}),1.0]])]});}
            var Q401;
            {var subQ0=sQuery(id+"F25.wireOp",EDGE,"E602.trimOffspring");var subQ1=sQuery(id+"F25.wireOp",EDGE,"E446.MirrorCS");var subQ2=makeQuery(id+"F25.imprint","INTERSECT",VERTEX,{"derivedFrom":[subQ1,subQ0]});Q401=makeQuery(id+"F25.imprint","IMPRINT",FACE,{"disambiguationData":[TD([[makeQuery(id+"F25.imprint","IMPRINT",EDGE,{"disambiguationData":[TD([[subQ2,-1.0]])],"derivedFrom":subQ1}),1.0]])]});}
            var Q402;
            {var subQ0=sQuery(id+"F25.wireOp",EDGE,"E601.trimOffspring");var subQ1=sQuery(id+"F25.wireOp",EDGE,"E446.MirrorCS");var subQ2=makeQuery(id+"F25.imprint","INTERSECT",VERTEX,{"derivedFrom":[subQ1,subQ0]});Q402=makeQuery(id+"F25.imprint","IMPRINT",FACE,{"disambiguationData":[TD([[makeQuery(id+"F25.imprint","IMPRINT",EDGE,{"disambiguationData":[TD([[subQ2,-1.0]])],"derivedFrom":subQ1}),1.0]])]});}
            var Q403;
            {var subQ0=sQuery(id+"F25.wireOp",EDGE,"E590.trimOffspring");var subQ1=sQuery(id+"F25.wireOp",EDGE,"E446.MirrorCS");var subQ2=makeQuery(id+"F25.imprint","INTERSECT",VERTEX,{"derivedFrom":[subQ1,subQ0]});Q403=makeQuery(id+"F25.imprint","IMPRINT",FACE,{"disambiguationData":[TD([[makeQuery(id+"F25.imprint","IMPRINT",EDGE,{"disambiguationData":[TD([[subQ2,-1.0]])],"derivedFrom":subQ1}),1.0]])]});}
            var Q404;
            {var subQ0=sQuery(id+"F25.wireOp",EDGE,"E593.trimOffspring");var subQ1=sQuery(id+"F25.wireOp",EDGE,"E446.MirrorCS");var subQ2=makeQuery(id+"F25.imprint","INTERSECT",VERTEX,{"derivedFrom":[subQ1,subQ0]});Q404=makeQuery(id+"F25.imprint","IMPRINT",FACE,{"disambiguationData":[TD([[makeQuery(id+"F25.imprint","IMPRINT",EDGE,{"disambiguationData":[TD([[subQ2,-1.0]])],"derivedFrom":subQ1}),1.0]])]});}
            var Q405;
            {var subQ0=sQuery(id+"F25.wireOp",EDGE,"E591.trimOffspring");var subQ1=sQuery(id+"F25.wireOp",EDGE,"E446.MirrorCS");var subQ2=makeQuery(id+"F25.imprint","INTERSECT",VERTEX,{"derivedFrom":[subQ1,subQ0]});Q405=makeQuery(id+"F25.imprint","IMPRINT",FACE,{"disambiguationData":[TD([[makeQuery(id+"F25.imprint","IMPRINT",EDGE,{"disambiguationData":[TD([[subQ2,1.0]])],"derivedFrom":subQ1}),1.0]])]});}
            var Q406;
            {var subQ0=sQuery(id+"F25.wireOp",EDGE,"E591.trimOffspring");var subQ1=sQuery(id+"F25.wireOp",EDGE,"E444.MirrorCS");var subQ2=makeQuery(id+"F25.imprint","INTERSECT",VERTEX,{"derivedFrom":[subQ1,subQ0]});Q406=makeQuery(id+"F25.imprint","IMPRINT",FACE,{"disambiguationData":[TD([[makeQuery(id+"F25.imprint","IMPRINT",EDGE,{"disambiguationData":[TD([[subQ2,1.0]])],"derivedFrom":subQ1}),-1.0]])]});}
            var Q407;
            {var subQ0=sQuery(id+"F25.wireOp",EDGE,"E591.trimOffspring");var subQ1=sQuery(id+"F25.wireOp",EDGE,"E444.MirrorCS");var subQ2=makeQuery(id+"F25.imprint","INTERSECT",VERTEX,{"derivedFrom":[subQ1,subQ0]});Q407=makeQuery(id+"F25.imprint","IMPRINT",FACE,{"disambiguationData":[TD([[makeQuery(id+"F25.imprint","IMPRINT",EDGE,{"disambiguationData":[TD([[subQ2,1.0]])],"derivedFrom":subQ1}),1.0]])]});}
            var Q408;
            {var subQ0=sQuery(id+"F25.wireOp",EDGE,"E591.trimOffspring");var subQ5=sQuery(id+"F25.wireOp",EDGE,"E427.MirrorCS");var subQ6=makeQuery(id+"F25.imprint","INTERSECT",VERTEX,{"derivedFrom":[subQ5,subQ0]});Q408=makeQuery(id+"F25.imprint","IMPRINT",FACE,{"disambiguationData":[TD([[makeQuery(id+"F25.imprint","IMPRINT",EDGE,{"disambiguationData":[TD([[subQ6,1.0]])],"derivedFrom":subQ5}),-1.0]])]});}
            var Q409;
            {var subQ0=sQuery(id+"F25.wireOp",EDGE,"E593.trimOffspring");var subQ5=sQuery(id+"F25.wireOp",EDGE,"E427.MirrorCS");var subQ7=makeQuery(id+"F25.imprint","INTERSECT",VERTEX,{"derivedFrom":[subQ5,subQ0]});Q409=makeQuery(id+"F25.imprint","IMPRINT",FACE,{"disambiguationData":[TD([[makeQuery(id+"F25.imprint","IMPRINT",EDGE,{"disambiguationData":[TD([[subQ7,-1.0]])],"derivedFrom":subQ5}),-1.0]])]});}
            var Q410;
            {var subQ0=sQuery(id+"F25.wireOp",EDGE,"E590.trimOffspring");var subQ5=sQuery(id+"F25.wireOp",EDGE,"E427.MirrorCS");var subQ6=makeQuery(id+"F25.imprint","INTERSECT",VERTEX,{"derivedFrom":[subQ5,subQ0]});Q410=makeQuery(id+"F25.imprint","IMPRINT",FACE,{"disambiguationData":[TD([[makeQuery(id+"F25.imprint","IMPRINT",EDGE,{"disambiguationData":[TD([[subQ6,-1.0]])],"derivedFrom":subQ5}),-1.0]])]});}
            var Q411;
            {var subQ3=sQuery(id+"F25.wireOp",EDGE,"E567.trimOffspring");var subQ5=sQuery(id+"F25.wireOp",EDGE,"E427.MirrorCS");var subQ6=makeQuery(id+"F25.imprint","INTERSECT",VERTEX,{"derivedFrom":[subQ5,subQ3]});Q411=makeQuery(id+"F25.imprint","IMPRINT",FACE,{"disambiguationData":[TD([[makeQuery(id+"F25.imprint","IMPRINT",EDGE,{"disambiguationData":[TD([[subQ6,-1.0]])],"derivedFrom":subQ5}),-1.0]])]});}
            var Q412;
            {var subQ0=sQuery(id+"F25.wireOp",EDGE,"E594.trimOffspring");var subQ5=sQuery(id+"F25.wireOp",EDGE,"E427.MirrorCS");var subQ6=makeQuery(id+"F25.imprint","INTERSECT",VERTEX,{"derivedFrom":[subQ5,subQ0]});Q412=makeQuery(id+"F25.imprint","IMPRINT",FACE,{"disambiguationData":[TD([[makeQuery(id+"F25.imprint","IMPRINT",EDGE,{"disambiguationData":[TD([[subQ6,-1.0]])],"derivedFrom":subQ5}),-1.0]])]});}
            var Q413;
            {var subQ3=sQuery(id+"F25.wireOp",EDGE,"E599.trimOffspring");var subQ5=sQuery(id+"F25.wireOp",EDGE,"E427.MirrorCS");var subQ6=makeQuery(id+"F25.imprint","INTERSECT",VERTEX,{"derivedFrom":[subQ5,subQ3]});Q413=makeQuery(id+"F25.imprint","IMPRINT",FACE,{"disambiguationData":[TD([[makeQuery(id+"F25.imprint","IMPRINT",EDGE,{"disambiguationData":[TD([[subQ6,-1.0]])],"derivedFrom":subQ5}),-1.0]])]});}
            var Q414;
            {var subQ0=sQuery(id+"F25.wireOp",EDGE,"E599.trimOffspring");var subQ1=sQuery(id+"F25.wireOp",EDGE,"E427.MirrorCS");var subQ2=makeQuery(id+"F25.imprint","INTERSECT",VERTEX,{"derivedFrom":[subQ1,subQ0]});Q414=makeQuery(id+"F25.imprint","IMPRINT",FACE,{"disambiguationData":[TD([[makeQuery(id+"F25.imprint","IMPRINT",EDGE,{"disambiguationData":[TD([[subQ2,-1.0]])],"derivedFrom":subQ1}),1.0]])]});}
            var Q415;
            {var subQ0=sQuery(id+"F25.wireOp",EDGE,"E594.trimOffspring");var subQ1=sQuery(id+"F25.wireOp",EDGE,"E427.MirrorCS");var subQ2=makeQuery(id+"F25.imprint","INTERSECT",VERTEX,{"derivedFrom":[subQ1,subQ0]});Q415=makeQuery(id+"F25.imprint","IMPRINT",FACE,{"disambiguationData":[TD([[makeQuery(id+"F25.imprint","IMPRINT",EDGE,{"disambiguationData":[TD([[subQ2,-1.0]])],"derivedFrom":subQ1}),1.0]])]});}
            var Q416;
            {var subQ0=sQuery(id+"F25.wireOp",EDGE,"E567.trimOffspring");var subQ1=sQuery(id+"F25.wireOp",EDGE,"E427.MirrorCS");var subQ2=makeQuery(id+"F25.imprint","INTERSECT",VERTEX,{"derivedFrom":[subQ1,subQ0]});Q416=makeQuery(id+"F25.imprint","IMPRINT",FACE,{"disambiguationData":[TD([[makeQuery(id+"F25.imprint","IMPRINT",EDGE,{"disambiguationData":[TD([[subQ2,-1.0]])],"derivedFrom":subQ1}),1.0]])]});}
            var Q417;
            {var subQ0=sQuery(id+"F25.wireOp",EDGE,"E590.trimOffspring");var subQ1=sQuery(id+"F25.wireOp",EDGE,"E427.MirrorCS");var subQ2=makeQuery(id+"F25.imprint","INTERSECT",VERTEX,{"derivedFrom":[subQ1,subQ0]});Q417=makeQuery(id+"F25.imprint","IMPRINT",FACE,{"disambiguationData":[TD([[makeQuery(id+"F25.imprint","IMPRINT",EDGE,{"disambiguationData":[TD([[subQ2,-1.0]])],"derivedFrom":subQ1}),1.0]])]});}
            var Q418;
            {var subQ0=sQuery(id+"F25.wireOp",EDGE,"E593.trimOffspring");var subQ1=sQuery(id+"F25.wireOp",EDGE,"E427.MirrorCS");var subQ2=makeQuery(id+"F25.imprint","INTERSECT",VERTEX,{"derivedFrom":[subQ1,subQ0]});Q418=makeQuery(id+"F25.imprint","IMPRINT",FACE,{"disambiguationData":[TD([[makeQuery(id+"F25.imprint","IMPRINT",EDGE,{"disambiguationData":[TD([[subQ2,-1.0]])],"derivedFrom":subQ1}),1.0]])]});}
            var Q419;
            {var subQ0=sQuery(id+"F25.wireOp",EDGE,"E591.trimOffspring");var subQ1=sQuery(id+"F25.wireOp",EDGE,"E427.MirrorCS");var subQ2=makeQuery(id+"F25.imprint","INTERSECT",VERTEX,{"derivedFrom":[subQ1,subQ0]});Q419=makeQuery(id+"F25.imprint","IMPRINT",FACE,{"disambiguationData":[TD([[makeQuery(id+"F25.imprint","IMPRINT",EDGE,{"disambiguationData":[TD([[subQ2,1.0]])],"derivedFrom":subQ1}),1.0]])]});}
            var Q420;
            {var subQ0=sQuery(id+"F25.wireOp",EDGE,"E591.trimOffspring");var subQ1=sQuery(id+"F25.wireOp",EDGE,"E440.MirrorCS");var subQ2=makeQuery(id+"F25.imprint","INTERSECT",VERTEX,{"derivedFrom":[subQ1,subQ0]});Q420=makeQuery(id+"F25.imprint","IMPRINT",FACE,{"disambiguationData":[TD([[makeQuery(id+"F25.imprint","IMPRINT",EDGE,{"disambiguationData":[TD([[subQ2,1.0]])],"derivedFrom":subQ1}),1.0]])]});}
            var Q421;
            {var subQ0=sQuery(id+"F25.wireOp",EDGE,"E591.trimOffspring");var subQ1=sQuery(id+"F25.wireOp",EDGE,"E431.MirrorCS");var subQ2=makeQuery(id+"F25.imprint","INTERSECT",VERTEX,{"derivedFrom":[subQ1,subQ0]});Q421=makeQuery(id+"F25.imprint","IMPRINT",FACE,{"disambiguationData":[TD([[makeQuery(id+"F25.imprint","IMPRINT",EDGE,{"disambiguationData":[TD([[subQ2,1.0]])],"derivedFrom":subQ1}),-1.0]])]});}
            var Q422;
            {var subQ0=sQuery(id+"F25.wireOp",EDGE,"E593.trimOffspring");var subQ1=sQuery(id+"F25.wireOp",EDGE,"E440.MirrorCS");var subQ2=makeQuery(id+"F25.imprint","INTERSECT",VERTEX,{"derivedFrom":[subQ1,subQ0]});Q422=makeQuery(id+"F25.imprint","IMPRINT",FACE,{"disambiguationData":[TD([[makeQuery(id+"F25.imprint","IMPRINT",EDGE,{"disambiguationData":[TD([[subQ2,-1.0]])],"derivedFrom":subQ1}),1.0]])]});}
            var Q423;
            {var subQ0=sQuery(id+"F25.wireOp",EDGE,"E593.trimOffspring");var subQ1=sQuery(id+"F25.wireOp",EDGE,"E431.MirrorCS");var subQ2=makeQuery(id+"F25.imprint","INTERSECT",VERTEX,{"derivedFrom":[subQ1,subQ0]});Q423=makeQuery(id+"F25.imprint","IMPRINT",FACE,{"disambiguationData":[TD([[makeQuery(id+"F25.imprint","IMPRINT",EDGE,{"disambiguationData":[TD([[subQ2,-1.0]])],"derivedFrom":subQ1}),-1.0]])]});}
            var Q424;
            {var subQ0=sQuery(id+"F25.wireOp",EDGE,"E590.trimOffspring");var subQ1=sQuery(id+"F25.wireOp",EDGE,"E440.MirrorCS");var subQ2=makeQuery(id+"F25.imprint","INTERSECT",VERTEX,{"derivedFrom":[subQ1,subQ0]});Q424=makeQuery(id+"F25.imprint","IMPRINT",FACE,{"disambiguationData":[TD([[makeQuery(id+"F25.imprint","IMPRINT",EDGE,{"disambiguationData":[TD([[subQ2,-1.0]])],"derivedFrom":subQ1}),1.0]])]});}
            var Q425;
            {var subQ0=sQuery(id+"F25.wireOp",EDGE,"E590.trimOffspring");var subQ1=sQuery(id+"F25.wireOp",EDGE,"E431.MirrorCS");var subQ2=makeQuery(id+"F25.imprint","INTERSECT",VERTEX,{"derivedFrom":[subQ1,subQ0]});Q425=makeQuery(id+"F25.imprint","IMPRINT",FACE,{"disambiguationData":[TD([[makeQuery(id+"F25.imprint","IMPRINT",EDGE,{"disambiguationData":[TD([[subQ2,-1.0]])],"derivedFrom":subQ1}),-1.0]])]});}
            var Q426;
            {var subQ0=sQuery(id+"F25.wireOp",EDGE,"E601.trimOffspring");var subQ5=sQuery(id+"F25.wireOp",EDGE,"E448.MirrorCS");var subQ6=makeQuery(id+"F25.imprint","INTERSECT",VERTEX,{"derivedFrom":[subQ5,subQ0]});Q426=makeQuery(id+"F25.imprint","IMPRINT",FACE,{"disambiguationData":[TD([[makeQuery(id+"F25.imprint","IMPRINT",EDGE,{"disambiguationData":[TD([[subQ6,-1.0]])],"derivedFrom":subQ5}),-1.0]])]});}
            var Q427;
            {var subQ0=sQuery(id+"F25.wireOp",EDGE,"E601.trimOffspring");var subQ1=sQuery(id+"F25.wireOp",EDGE,"E431.MirrorCS");var subQ2=makeQuery(id+"F25.imprint","INTERSECT",VERTEX,{"derivedFrom":[subQ1,subQ0]});Q427=makeQuery(id+"F25.imprint","IMPRINT",FACE,{"disambiguationData":[TD([[makeQuery(id+"F25.imprint","IMPRINT",EDGE,{"disambiguationData":[TD([[subQ2,-1.0]])],"derivedFrom":subQ1}),-1.0]])]});}
            var Q428;
            {var subQ0=sQuery(id+"F25.wireOp",EDGE,"E602.trimOffspring");var subQ5=sQuery(id+"F25.wireOp",EDGE,"E448.MirrorCS");var subQ6=makeQuery(id+"F25.imprint","INTERSECT",VERTEX,{"derivedFrom":[subQ5,subQ0]});Q428=makeQuery(id+"F25.imprint","IMPRINT",FACE,{"disambiguationData":[TD([[makeQuery(id+"F25.imprint","IMPRINT",EDGE,{"disambiguationData":[TD([[subQ6,-1.0]])],"derivedFrom":subQ5}),-1.0]])]});}
            var Q429;
            {var subQ0=sQuery(id+"F25.wireOp",EDGE,"E602.trimOffspring");var subQ1=sQuery(id+"F25.wireOp",EDGE,"E431.MirrorCS");var subQ2=makeQuery(id+"F25.imprint","INTERSECT",VERTEX,{"derivedFrom":[subQ1,subQ0]});Q429=makeQuery(id+"F25.imprint","IMPRINT",FACE,{"disambiguationData":[TD([[makeQuery(id+"F25.imprint","IMPRINT",EDGE,{"disambiguationData":[TD([[subQ2,-1.0]])],"derivedFrom":subQ1}),-1.0]])]});}
            var Q430;
            {var subQ3=sQuery(id+"F25.wireOp",EDGE,"E603.trimOffspring");var subQ5=sQuery(id+"F25.wireOp",EDGE,"E448.MirrorCS");var subQ7=makeQuery(id+"F25.imprint","INTERSECT",VERTEX,{"derivedFrom":[subQ5,subQ3]});Q430=makeQuery(id+"F25.imprint","IMPRINT",FACE,{"disambiguationData":[TD([[makeQuery(id+"F25.imprint","IMPRINT",EDGE,{"disambiguationData":[TD([[subQ7,-1.0]])],"derivedFrom":subQ5}),-1.0]])]});}
            var Q431;
            {var subQ0=sQuery(id+"F25.wireOp",EDGE,"E603.trimOffspring");var subQ1=sQuery(id+"F25.wireOp",EDGE,"E431.MirrorCS");var subQ2=makeQuery(id+"F25.imprint","INTERSECT",VERTEX,{"derivedFrom":[subQ1,subQ0]});Q431=makeQuery(id+"F25.imprint","IMPRINT",FACE,{"disambiguationData":[TD([[makeQuery(id+"F25.imprint","IMPRINT",EDGE,{"disambiguationData":[TD([[subQ2,-1.0]])],"derivedFrom":subQ1}),-1.0]])]});}
            var Q432;
            {var subQ0=sQuery(id+"F25.wireOp",EDGE,"E595.trimOffspring");var subQ1=sQuery(id+"F25.wireOp",EDGE,"E473.trimOffspring");var subQ2=makeQuery(id+"F25.imprint","INTERSECT",VERTEX,{"derivedFrom":[subQ1,subQ0]});Q432=makeQuery(id+"F25.imprint","IMPRINT",FACE,{"disambiguationData":[TD([[makeQuery(id+"F25.imprint","IMPRINT",EDGE,{"disambiguationData":[TD([[subQ2,-1.0]])],"derivedFrom":subQ1}),1.0]])]});}
            var Q433;
            {var subQ0=sQuery(id+"F25.wireOp",EDGE,"E595.trimOffspring");var subQ1=sQuery(id+"F25.wireOp",EDGE,"E474.trimOffspring");var subQ2=makeQuery(id+"F25.imprint","INTERSECT",VERTEX,{"derivedFrom":[subQ1,subQ0]});Q433=makeQuery(id+"F25.imprint","IMPRINT",FACE,{"disambiguationData":[TD([[makeQuery(id+"F25.imprint","IMPRINT",EDGE,{"disambiguationData":[TD([[subQ2,-1.0]])],"derivedFrom":subQ1}),1.0]])]});}
            var Q434;
            {var subQ0=sQuery(id+"F25.wireOp",EDGE,"E593.trimOffspring");var subQ1=sQuery(id+"F25.wireOp",EDGE,"E474.trimOffspring");var subQ2=makeQuery(id+"F25.imprint","INTERSECT",VERTEX,{"derivedFrom":[subQ1,subQ0]});Q434=makeQuery(id+"F25.imprint","IMPRINT",FACE,{"disambiguationData":[TD([[makeQuery(id+"F25.imprint","IMPRINT",EDGE,{"disambiguationData":[TD([[subQ2,-1.0]])],"derivedFrom":subQ1}),1.0]])]});}
            var Q435;
            {var subQ0=sQuery(id+"F25.wireOp",EDGE,"E590.trimOffspring");var subQ1=sQuery(id+"F25.wireOp",EDGE,"E474.trimOffspring");var subQ2=makeQuery(id+"F25.imprint","INTERSECT",VERTEX,{"derivedFrom":[subQ1,subQ0]});Q435=makeQuery(id+"F25.imprint","IMPRINT",FACE,{"disambiguationData":[TD([[makeQuery(id+"F25.imprint","IMPRINT",EDGE,{"disambiguationData":[TD([[subQ2,-1.0]])],"derivedFrom":subQ1}),1.0]])]});}
            var Q436;
            {var subQ0=sQuery(id+"F25.wireOp",EDGE,"E601.trimOffspring");var subQ1=sQuery(id+"F25.wireOp",EDGE,"E474.trimOffspring");var subQ2=makeQuery(id+"F25.imprint","INTERSECT",VERTEX,{"derivedFrom":[subQ1,subQ0]});Q436=makeQuery(id+"F25.imprint","IMPRINT",FACE,{"disambiguationData":[TD([[makeQuery(id+"F25.imprint","IMPRINT",EDGE,{"disambiguationData":[TD([[subQ2,-1.0]])],"derivedFrom":subQ1}),1.0]])]});}
            var Q437;
            {var subQ0=sQuery(id+"F25.wireOp",EDGE,"E601.trimOffspring");var subQ1=sQuery(id+"F25.wireOp",EDGE,"E475.trimOffspring");var subQ2=makeQuery(id+"F25.imprint","INTERSECT",VERTEX,{"derivedFrom":[subQ1,subQ0]});Q437=makeQuery(id+"F25.imprint","IMPRINT",FACE,{"disambiguationData":[TD([[makeQuery(id+"F25.imprint","IMPRINT",EDGE,{"disambiguationData":[TD([[subQ2,-1.0]])],"derivedFrom":subQ1}),-1.0]])]});}
            var Q438;
            {var subQ3=sQuery(id+"F25.wireOp",EDGE,"E601.trimOffspring");var subQ5=sQuery(id+"F25.wireOp",EDGE,"E475.trimOffspring");var subQ6=makeQuery(id+"F25.imprint","INTERSECT",VERTEX,{"derivedFrom":[subQ5,subQ3]});Q438=makeQuery(id+"F25.imprint","IMPRINT",FACE,{"disambiguationData":[TD([[makeQuery(id+"F25.imprint","IMPRINT",EDGE,{"disambiguationData":[TD([[subQ6,-1.0]])],"derivedFrom":subQ5}),1.0]])]});}
            var Q439;
            {var subQ0=sQuery(id+"F25.wireOp",EDGE,"E590.trimOffspring");var subQ5=sQuery(id+"F25.wireOp",EDGE,"E475.trimOffspring");var subQ6=makeQuery(id+"F25.imprint","INTERSECT",VERTEX,{"derivedFrom":[subQ5,subQ0]});Q439=makeQuery(id+"F25.imprint","IMPRINT",FACE,{"disambiguationData":[TD([[makeQuery(id+"F25.imprint","IMPRINT",EDGE,{"disambiguationData":[TD([[subQ6,-1.0]])],"derivedFrom":subQ5}),1.0]])]});}
            var Q440;
            {var subQ3=sQuery(id+"F25.wireOp",EDGE,"E593.trimOffspring");var subQ5=sQuery(id+"F25.wireOp",EDGE,"E475.trimOffspring");var subQ6=makeQuery(id+"F25.imprint","INTERSECT",VERTEX,{"derivedFrom":[subQ5,subQ3]});Q440=makeQuery(id+"F25.imprint","IMPRINT",FACE,{"disambiguationData":[TD([[makeQuery(id+"F25.imprint","IMPRINT",EDGE,{"disambiguationData":[TD([[subQ6,-1.0]])],"derivedFrom":subQ5}),1.0]])]});}
            var Q441;
            {var subQ0=sQuery(id+"F25.wireOp",EDGE,"E458.MirrorCS");var subQ5=sQuery(id+"F25.wireOp",EDGE,"E477.trimOffspring");var subQ6=makeQuery(id+"F25.imprint","INTERSECT",VERTEX,{"derivedFrom":[subQ0,subQ5]});Q441=makeQuery(id+"F25.imprint","IMPRINT",FACE,{"disambiguationData":[TD([[makeQuery(id+"F25.imprint","IMPRINT",EDGE,{"disambiguationData":[TD([[subQ6,-1.0]])],"derivedFrom":subQ5}),-1.0]])]});}
            var Q442;
            {var subQ0=sQuery(id+"F25.wireOp",EDGE,"E616.trimOffspring");var subQ1=sQuery(id+"F25.wireOp",EDGE,"E458.MirrorCS");var subQ2=makeQuery(id+"F25.imprint","INTERSECT",VERTEX,{"derivedFrom":[subQ1,subQ0]});Q442=makeQuery(id+"F25.imprint","IMPRINT",FACE,{"disambiguationData":[TD([[makeQuery(id+"F25.imprint","IMPRINT",EDGE,{"disambiguationData":[TD([[subQ2,-1.0]])],"derivedFrom":subQ1}),1.0]])]});}
            var Q443;
            {var subQ0=sQuery(id+"F25.wireOp",EDGE,"E595.trimOffspring");var subQ5=sQuery(id+"F25.wireOp",EDGE,"E475.trimOffspring");var subQ6=makeQuery(id+"F25.imprint","INTERSECT",VERTEX,{"derivedFrom":[subQ5,subQ0]});Q443=makeQuery(id+"F25.imprint","IMPRINT",FACE,{"disambiguationData":[TD([[makeQuery(id+"F25.imprint","IMPRINT",EDGE,{"disambiguationData":[TD([[subQ6,-1.0]])],"derivedFrom":subQ5}),1.0]])]});}
            var Q444;
            {var subQ0=sQuery(id+"F25.wireOp",EDGE,"E617.trimOffspring");var subQ1=sQuery(id+"F25.wireOp",EDGE,"E458.MirrorCS");var subQ2=makeQuery(id+"F25.imprint","INTERSECT",VERTEX,{"derivedFrom":[subQ1,subQ0]});Q444=makeQuery(id+"F25.imprint","IMPRINT",FACE,{"disambiguationData":[TD([[makeQuery(id+"F25.imprint","IMPRINT",EDGE,{"disambiguationData":[TD([[subQ2,-1.0]])],"derivedFrom":subQ1}),1.0]])]});}
            var Q445;
            {var subQ0=sQuery(id+"F25.wireOp",EDGE,"E617.trimOffspring");var subQ1=sQuery(id+"F25.wireOp",EDGE,"E419.MirrorCS");var subQ2=makeQuery(id+"F25.imprint","INTERSECT",VERTEX,{"derivedFrom":[subQ1,subQ0]});Q445=makeQuery(id+"F25.imprint","IMPRINT",FACE,{"disambiguationData":[TD([[makeQuery(id+"F25.imprint","IMPRINT",EDGE,{"disambiguationData":[TD([[subQ2,-1.0]])],"derivedFrom":subQ1}),-1.0]])]});}
            var Q446;
            {var subQ0=sQuery(id+"F25.wireOp",EDGE,"E617.trimOffspring");var subQ1=sQuery(id+"F25.wireOp",EDGE,"E417.MirrorCS");var subQ2=makeQuery(id+"F25.imprint","INTERSECT",VERTEX,{"derivedFrom":[subQ1,subQ0]});Q446=makeQuery(id+"F25.imprint","IMPRINT",FACE,{"disambiguationData":[TD([[makeQuery(id+"F25.imprint","IMPRINT",EDGE,{"disambiguationData":[TD([[subQ2,-1.0]])],"derivedFrom":subQ1}),-1.0]])]});}
            var Q447;
            {var subQ0=sQuery(id+"F25.wireOp",EDGE,"E617.trimOffspring");var subQ1=sQuery(id+"F25.wireOp",EDGE,"E417.MirrorCS");var subQ2=makeQuery(id+"F25.imprint","INTERSECT",VERTEX,{"derivedFrom":[subQ1,subQ0]});Q447=makeQuery(id+"F25.imprint","IMPRINT",FACE,{"disambiguationData":[TD([[makeQuery(id+"F25.imprint","IMPRINT",EDGE,{"disambiguationData":[TD([[subQ2,-1.0]])],"derivedFrom":subQ1}),1.0]])]});}
            var Q448;
            {var subQ0=sQuery(id+"F25.wireOp",EDGE,"E617.trimOffspring");var subQ1=sQuery(id+"F25.wireOp",EDGE,"E409.MirrorCS");var subQ2=makeQuery(id+"F25.imprint","INTERSECT",VERTEX,{"derivedFrom":[subQ1,subQ0]});Q448=makeQuery(id+"F25.imprint","IMPRINT",FACE,{"disambiguationData":[TD([[makeQuery(id+"F25.imprint","IMPRINT",EDGE,{"disambiguationData":[TD([[subQ2,-1.0]])],"derivedFrom":subQ1}),-1.0]])]});}
            var Q449;
            {var subQ0=sQuery(id+"F25.wireOp",EDGE,"E473.trimOffspring");var subQ1=sQuery(id+"F25.wireOp",EDGE,"E421.MirrorCS");var subQ2=makeQuery(id+"F25.imprint","INTERSECT",VERTEX,{"derivedFrom":[subQ1,subQ0]});Q449=makeQuery(id+"F25.imprint","IMPRINT",FACE,{"disambiguationData":[TD([[makeQuery(id+"F25.imprint","IMPRINT",EDGE,{"disambiguationData":[TD([[subQ2,-1.0]])],"derivedFrom":subQ1}),1.0]])]});}
            var Q450;
            {var subQ0=sQuery(id+"F25.wireOp",EDGE,"E473.trimOffspring");var subQ1=sQuery(id+"F25.wireOp",EDGE,"E416.MirrorCS");var subQ2=makeQuery(id+"F25.imprint","INTERSECT",VERTEX,{"derivedFrom":[subQ1,subQ0]});Q450=makeQuery(id+"F25.imprint","IMPRINT",FACE,{"disambiguationData":[TD([[makeQuery(id+"F25.imprint","IMPRINT",EDGE,{"disambiguationData":[TD([[subQ2,-1.0]])],"derivedFrom":subQ1}),-1.0]])]});}
            var Q451;
            {var subQ0=sQuery(id+"F25.wireOp",EDGE,"E474.trimOffspring");var subQ1=sQuery(id+"F25.wireOp",EDGE,"E421.MirrorCS");var subQ2=makeQuery(id+"F25.imprint","INTERSECT",VERTEX,{"derivedFrom":[subQ1,subQ0]});Q451=makeQuery(id+"F25.imprint","IMPRINT",FACE,{"disambiguationData":[TD([[makeQuery(id+"F25.imprint","IMPRINT",EDGE,{"disambiguationData":[TD([[subQ2,-1.0]])],"derivedFrom":subQ1}),1.0]])]});}
            var Q452;
            {var subQ0=sQuery(id+"F25.wireOp",EDGE,"E474.trimOffspring");var subQ1=sQuery(id+"F25.wireOp",EDGE,"E416.MirrorCS");var subQ2=makeQuery(id+"F25.imprint","INTERSECT",VERTEX,{"derivedFrom":[subQ1,subQ0]});Q452=makeQuery(id+"F25.imprint","IMPRINT",FACE,{"disambiguationData":[TD([[makeQuery(id+"F25.imprint","IMPRINT",EDGE,{"disambiguationData":[TD([[subQ2,-1.0]])],"derivedFrom":subQ1}),-1.0]])]});}
            var Q453;
            {var subQ0=sQuery(id+"F25.wireOp",EDGE,"E476.trimOffspring");var subQ1=sQuery(id+"F25.wireOp",EDGE,"E421.MirrorCS");var subQ2=makeQuery(id+"F25.imprint","INTERSECT",VERTEX,{"derivedFrom":[subQ1,subQ0]});Q453=makeQuery(id+"F25.imprint","IMPRINT",FACE,{"disambiguationData":[TD([[makeQuery(id+"F25.imprint","IMPRINT",EDGE,{"disambiguationData":[TD([[subQ2,-1.0]])],"derivedFrom":subQ1}),1.0]])]});}
            var Q454;
            {var subQ0=sQuery(id+"F25.wireOp",EDGE,"E476.trimOffspring");var subQ1=sQuery(id+"F25.wireOp",EDGE,"E416.MirrorCS");var subQ2=makeQuery(id+"F25.imprint","INTERSECT",VERTEX,{"derivedFrom":[subQ1,subQ0]});Q454=makeQuery(id+"F25.imprint","IMPRINT",FACE,{"disambiguationData":[TD([[makeQuery(id+"F25.imprint","IMPRINT",EDGE,{"disambiguationData":[TD([[subQ2,-1.0]])],"derivedFrom":subQ1}),-1.0]])]});}
            var Q455;
            {var subQ1=sQuery(id+"F25.wireOp",EDGE,"E421.MirrorCS");var subQ3=sQuery(id+"F25.wireOp",EDGE,"E475.trimOffspring");var subQ4=makeQuery(id+"F25.imprint","INTERSECT",VERTEX,{"derivedFrom":[subQ1,subQ3]});Q455=makeQuery(id+"F25.imprint","IMPRINT",FACE,{"disambiguationData":[TD([[makeQuery(id+"F25.imprint","IMPRINT",EDGE,{"disambiguationData":[TD([[subQ4,1.0]])],"derivedFrom":subQ3}),1.0]])]});}
            var Q456;
            {var subQ1=sQuery(id+"F25.wireOp",EDGE,"E416.MirrorCS");var subQ3=sQuery(id+"F25.wireOp",EDGE,"E475.trimOffspring");var subQ4=makeQuery(id+"F25.imprint","INTERSECT",VERTEX,{"derivedFrom":[subQ1,subQ3]});Q456=makeQuery(id+"F25.imprint","IMPRINT",FACE,{"disambiguationData":[TD([[makeQuery(id+"F25.imprint","IMPRINT",EDGE,{"disambiguationData":[TD([[subQ4,-1.0]])],"derivedFrom":subQ3}),1.0]])]});}
            var Q457;
            {var subQ1=sQuery(id+"F25.wireOp",EDGE,"E417.MirrorCS");var subQ3=sQuery(id+"F25.wireOp",EDGE,"E477.trimOffspring");var subQ4=makeQuery(id+"F25.imprint","INTERSECT",VERTEX,{"derivedFrom":[subQ1,subQ3]});Q457=makeQuery(id+"F25.imprint","IMPRINT",FACE,{"disambiguationData":[TD([[makeQuery(id+"F25.imprint","IMPRINT",EDGE,{"disambiguationData":[TD([[subQ4,-1.0]])],"derivedFrom":subQ3}),-1.0]])]});}
            var Q458;
            {var subQ1=sQuery(id+"F25.wireOp",EDGE,"E417.MirrorCS");var subQ3=sQuery(id+"F25.wireOp",EDGE,"E477.trimOffspring");var subQ4=makeQuery(id+"F25.imprint","INTERSECT",VERTEX,{"derivedFrom":[subQ1,subQ3]});Q458=makeQuery(id+"F25.imprint","IMPRINT",FACE,{"disambiguationData":[TD([[makeQuery(id+"F25.imprint","IMPRINT",EDGE,{"disambiguationData":[TD([[subQ4,1.0]])],"derivedFrom":subQ3}),-1.0]])]});}
            var Q459;
            {var subQ0=sQuery(id+"F25.wireOp",EDGE,"E616.trimOffspring");var subQ1=sQuery(id+"F25.wireOp",EDGE,"E417.MirrorCS");var subQ2=makeQuery(id+"F25.imprint","INTERSECT",VERTEX,{"derivedFrom":[subQ1,subQ0]});Q459=makeQuery(id+"F25.imprint","IMPRINT",FACE,{"disambiguationData":[TD([[makeQuery(id+"F25.imprint","IMPRINT",EDGE,{"disambiguationData":[TD([[subQ2,-1.0]])],"derivedFrom":subQ1}),-1.0]])]});}
            var Q460;
            {var subQ0=sQuery(id+"F25.wireOp",EDGE,"E616.trimOffspring");var subQ1=sQuery(id+"F25.wireOp",EDGE,"E417.MirrorCS");var subQ2=makeQuery(id+"F25.imprint","INTERSECT",VERTEX,{"derivedFrom":[subQ1,subQ0]});Q460=makeQuery(id+"F25.imprint","IMPRINT",FACE,{"disambiguationData":[TD([[makeQuery(id+"F25.imprint","IMPRINT",EDGE,{"disambiguationData":[TD([[subQ2,-1.0]])],"derivedFrom":subQ1}),1.0]])]});}
            var Q461;
            {var subQ0=sQuery(id+"F25.wireOp",EDGE,"E334.MirrorCS");var subQ1=sQuery(id+"F25.wireOp",EDGE,"E324.MirrorCS");var subQ2=makeQuery(id+"F25.imprint","INTERSECT",VERTEX,{"derivedFrom":[subQ1,subQ0]});Q461=makeQuery(id+"F25.imprint","IMPRINT",FACE,{"disambiguationData":[TD([[makeQuery(id+"F25.imprint","IMPRINT",EDGE,{"disambiguationData":[TD([[subQ2,-1.0]])],"derivedFrom":subQ1}),-1.0]])]});}
            var Q462;
            {var subQ0=sQuery(id+"F25.wireOp",EDGE,"E315.MirrorCS");Q462=makeQuery(id+"F25.imprint","IMPRINT",FACE,{"disambiguationData":[TD([[makeQuery(id+"F25.imprint","IMPRINT",EDGE,{"derivedFrom":subQ0}),1.0]])]});}
            var Q463;
            {var subQ5=sQuery(id+"F25.wireOp",EDGE,"E315.MirrorCS");Q463=makeQuery(id+"F25.imprint","IMPRINT",FACE,{"disambiguationData":[TD([[makeQuery(id+"F25.imprint","IMPRINT",EDGE,{"derivedFrom":subQ5}),-1.0]])]});}
            var Q464;
            {var subQ5=sQuery(id+"F25.wireOp",EDGE,"E616.trimOffspring");var subQ6=sQuery(id+"F25.wireOp",EDGE,"E409.MirrorCS");var subQ7=makeQuery(id+"F25.imprint","INTERSECT",VERTEX,{"derivedFrom":[subQ6,subQ5]});Q464=makeQuery(id+"F25.imprint","IMPRINT",FACE,{"disambiguationData":[TD([[makeQuery(id+"F25.imprint","IMPRINT",EDGE,{"disambiguationData":[TD([[subQ7,-1.0]])],"derivedFrom":subQ6}),1.0]])]});}
            var Q465;
            {var subQ4=sQuery(id+"F25.wireOp",EDGE,"E222.right");Q465=makeQuery(id+"F25.imprint","IMPRINT",FACE,{"disambiguationData":[TD([[makeQuery(id+"F25.imprint","IMPRINT",EDGE,{"derivedFrom":subQ4}),1.0]])]});}
            var Q466;
            {var subQ0=sQuery(id+"F25.wireOp",EDGE,"E311.MirrorCS");Q466=makeQuery(id+"F25.imprint","IMPRINT",FACE,{"disambiguationData":[TD([[makeQuery(id+"F25.imprint","IMPRINT",EDGE,{"derivedFrom":subQ0}),1.0]])]});}
            var Q467;
            {var subQ1=sQuery(id+"F25.wireOp",EDGE,"E415.MirrorCS");var subQ3=sQuery(id+"F25.wireOp",EDGE,"E475.trimOffspring");var subQ4=makeQuery(id+"F25.imprint","INTERSECT",VERTEX,{"derivedFrom":[subQ1,subQ3]});Q467=makeQuery(id+"F25.imprint","IMPRINT",FACE,{"disambiguationData":[TD([[makeQuery(id+"F25.imprint","IMPRINT",EDGE,{"disambiguationData":[TD([[subQ4,-1.0]])],"derivedFrom":subQ1}),-1.0]])]});}
            var Q468;
            {var subQ5=sQuery(id+"F25.wireOp",EDGE,"E222.right");Q468=makeQuery(id+"F25.imprint","IMPRINT",FACE,{"disambiguationData":[TD([[makeQuery(id+"F25.imprint","IMPRINT",EDGE,{"derivedFrom":subQ5}),-1.0]])]});}
            var Q469;
            {var subQ1=sQuery(id+"F25.wireOp",EDGE,"E249.right");var subQ3=sQuery(id+"F25.wireOp",EDGE,"E284.trimOffspring");var subQ4=makeQuery(id+"F25.imprint","INTERSECT",VERTEX,{"derivedFrom":[subQ1,subQ3]});Q469=makeQuery(id+"F25.imprint","IMPRINT",FACE,{"disambiguationData":[TD([[makeQuery(id+"F25.imprint","IMPRINT",EDGE,{"disambiguationData":[TD([[subQ4,1.0]])],"derivedFrom":subQ3}),1.0]])]});}
            var Q470;
            {var subQ0=sQuery(id+"F25.wireOp",EDGE,"E476.trimOffspring");var subQ1=sQuery(id+"F25.wireOp",EDGE,"E415.MirrorCS");var subQ2=makeQuery(id+"F25.imprint","INTERSECT",VERTEX,{"derivedFrom":[subQ1,subQ0]});Q470=makeQuery(id+"F25.imprint","IMPRINT",FACE,{"disambiguationData":[TD([[makeQuery(id+"F25.imprint","IMPRINT",EDGE,{"disambiguationData":[TD([[subQ2,-1.0]])],"derivedFrom":subQ1}),-1.0]])]});}
            var Q471;
            {var subQ0=sQuery(id+"F25.wireOp",EDGE,"E474.trimOffspring");var subQ1=sQuery(id+"F25.wireOp",EDGE,"E415.MirrorCS");var subQ2=makeQuery(id+"F25.imprint","INTERSECT",VERTEX,{"derivedFrom":[subQ1,subQ0]});Q471=makeQuery(id+"F25.imprint","IMPRINT",FACE,{"disambiguationData":[TD([[makeQuery(id+"F25.imprint","IMPRINT",EDGE,{"disambiguationData":[TD([[subQ2,-1.0]])],"derivedFrom":subQ1}),-1.0]])]});}
            var Q472;
            {var subQ0=sQuery(id+"F25.wireOp",EDGE,"E473.trimOffspring");var subQ1=sQuery(id+"F25.wireOp",EDGE,"E415.MirrorCS");var subQ2=makeQuery(id+"F25.imprint","INTERSECT",VERTEX,{"derivedFrom":[subQ1,subQ0]});Q472=makeQuery(id+"F25.imprint","IMPRINT",FACE,{"disambiguationData":[TD([[makeQuery(id+"F25.imprint","IMPRINT",EDGE,{"disambiguationData":[TD([[subQ2,-1.0]])],"derivedFrom":subQ1}),-1.0]])]});}
            var Q473;
            {var subQ1=sQuery(id+"F25.wireOp",EDGE,"E250.right");var subQ3=sQuery(id+"F25.wireOp",EDGE,"E284.trimOffspring");var subQ4=makeQuery(id+"F25.imprint","INTERSECT",VERTEX,{"derivedFrom":[subQ1,subQ3]});Q473=makeQuery(id+"F25.imprint","IMPRINT",FACE,{"disambiguationData":[TD([[makeQuery(id+"F25.imprint","IMPRINT",EDGE,{"disambiguationData":[TD([[subQ4,1.0]])],"derivedFrom":subQ3}),1.0]])]});}
            var Q474;
            {var subQ3=sQuery(id+"F25.wireOp",EDGE,"E284.trimOffspring");var subQ5=sQuery(id+"F25.wireOp",EDGE,"E251.right");var subQ7=makeQuery(id+"F25.imprint","INTERSECT",VERTEX,{"derivedFrom":[subQ5,subQ3]});Q474=makeQuery(id+"F25.imprint","IMPRINT",FACE,{"disambiguationData":[TD([[makeQuery(id+"F25.imprint","IMPRINT",EDGE,{"disambiguationData":[TD([[subQ7,-1.0]])],"derivedFrom":subQ3}),1.0]])]});}
            var Q475;
            {var subQ3=sQuery(id+"F25.wireOp",EDGE,"E510.trimOffspring");var subQ5=sQuery(id+"F25.wireOp",EDGE,"E249.right");var subQ6=makeQuery(id+"F25.imprint","INTERSECT",VERTEX,{"derivedFrom":[subQ5,subQ3]});Q475=makeQuery(id+"F25.imprint","IMPRINT",FACE,{"disambiguationData":[TD([[makeQuery(id+"F25.imprint","IMPRINT",EDGE,{"disambiguationData":[TD([[subQ6,-1.0]])],"derivedFrom":subQ5}),-1.0]])]});}
            var Q476;
            {var subQ0=sQuery(id+"F25.wireOp",EDGE,"E335.MirrorCS");var subQ5=sQuery(id+"F25.wireOp",EDGE,"E387.MirrorCS");var subQ6=makeQuery(id+"F25.imprint","INTERSECT",VERTEX,{"derivedFrom":[subQ0,subQ5]});Q476=makeQuery(id+"F25.imprint","IMPRINT",FACE,{"disambiguationData":[TD([[makeQuery(id+"F25.imprint","IMPRINT",EDGE,{"disambiguationData":[TD([[subQ6,1.0]])],"derivedFrom":subQ5}),1.0]])]});}
            var Q477;
            {var subQ0=sQuery(id+"F25.wireOp",EDGE,"E234.right");Q477=makeQuery(id+"F25.imprint","IMPRINT",FACE,{"disambiguationData":[TD([[makeQuery(id+"F25.imprint","IMPRINT",EDGE,{"derivedFrom":subQ0}),1.0]])]});}
            var Q478;
            {var subQ0=sQuery(id+"F25.wireOp",EDGE,"E232.right");Q478=makeQuery(id+"F25.imprint","IMPRINT",FACE,{"disambiguationData":[TD([[makeQuery(id+"F25.imprint","IMPRINT",EDGE,{"derivedFrom":subQ0}),-1.0]])]});}
            var Q479;
            {var subQ5=sQuery(id+"F25.wireOp",EDGE,"E234.right");Q479=makeQuery(id+"F25.imprint","IMPRINT",FACE,{"disambiguationData":[TD([[makeQuery(id+"F25.imprint","IMPRINT",EDGE,{"derivedFrom":subQ5}),-1.0]])]});}
            var Q480;
            {var subQ5=sQuery(id+"F25.wireOp",EDGE,"E232.right");Q480=makeQuery(id+"F25.imprint","IMPRINT",FACE,{"disambiguationData":[TD([[makeQuery(id+"F25.imprint","IMPRINT",EDGE,{"derivedFrom":subQ5}),1.0]])]});}
            var Q481;
            {var subQ0=sQuery(id+"F25.wireOp",EDGE,"E522.trimOffspring");var subQ1=sQuery(id+"F25.wireOp",EDGE,"E249.right");var subQ2=makeQuery(id+"F25.imprint","INTERSECT",VERTEX,{"derivedFrom":[subQ1,subQ0]});Q481=makeQuery(id+"F25.imprint","IMPRINT",FACE,{"disambiguationData":[TD([[makeQuery(id+"F25.imprint","IMPRINT",EDGE,{"disambiguationData":[TD([[subQ2,-1.0]])],"derivedFrom":subQ1}),1.0]])]});}
            var Q482;
            {var subQ0=sQuery(id+"F25.wireOp",EDGE,"E524.trimOffspring");var subQ1=sQuery(id+"F25.wireOp",EDGE,"E249.right");var subQ2=makeQuery(id+"F25.imprint","INTERSECT",VERTEX,{"derivedFrom":[subQ1,subQ0]});Q482=makeQuery(id+"F25.imprint","IMPRINT",FACE,{"disambiguationData":[TD([[makeQuery(id+"F25.imprint","IMPRINT",EDGE,{"disambiguationData":[TD([[subQ2,-1.0]])],"derivedFrom":subQ1}),1.0]])]});}
            var Q483;
            {var subQ0=sQuery(id+"F25.wireOp",EDGE,"E522.trimOffspring");var subQ1=sQuery(id+"F25.wireOp",EDGE,"E250.right");var subQ2=makeQuery(id+"F25.imprint","INTERSECT",VERTEX,{"derivedFrom":[subQ1,subQ0]});Q483=makeQuery(id+"F25.imprint","IMPRINT",FACE,{"disambiguationData":[TD([[makeQuery(id+"F25.imprint","IMPRINT",EDGE,{"disambiguationData":[TD([[subQ2,-1.0]])],"derivedFrom":subQ1}),1.0]])]});}
            var Q484;
            {var subQ0=sQuery(id+"F25.wireOp",EDGE,"E522.trimOffspring");var subQ1=sQuery(id+"F25.wireOp",EDGE,"E250.left");var subQ2=makeQuery(id+"F25.imprint","INTERSECT",VERTEX,{"derivedFrom":[subQ1,subQ0]});Q484=makeQuery(id+"F25.imprint","IMPRINT",FACE,{"disambiguationData":[TD([[makeQuery(id+"F25.imprint","IMPRINT",EDGE,{"disambiguationData":[TD([[subQ2,-1.0]])],"derivedFrom":subQ1}),1.0]])]});}
            var Q485;
            {var subQ0=sQuery(id+"F25.wireOp",EDGE,"E524.trimOffspring");var subQ1=sQuery(id+"F25.wireOp",EDGE,"E250.left");var subQ2=makeQuery(id+"F25.imprint","INTERSECT",VERTEX,{"derivedFrom":[subQ1,subQ0]});Q485=makeQuery(id+"F25.imprint","IMPRINT",FACE,{"disambiguationData":[TD([[makeQuery(id+"F25.imprint","IMPRINT",EDGE,{"disambiguationData":[TD([[subQ2,-1.0]])],"derivedFrom":subQ1}),1.0]])]});}
            var Q486;
            {var subQ0=sQuery(id+"F25.wireOp",EDGE,"E524.trimOffspring");var subQ1=sQuery(id+"F25.wireOp",EDGE,"E250.right");var subQ2=makeQuery(id+"F25.imprint","INTERSECT",VERTEX,{"derivedFrom":[subQ1,subQ0]});Q486=makeQuery(id+"F25.imprint","IMPRINT",FACE,{"disambiguationData":[TD([[makeQuery(id+"F25.imprint","IMPRINT",EDGE,{"disambiguationData":[TD([[subQ2,-1.0]])],"derivedFrom":subQ1}),1.0]])]});}
            var Q487;
            {var subQ0=sQuery(id+"F25.wireOp",EDGE,"E525.trimOffspring");var subQ1=sQuery(id+"F25.wireOp",EDGE,"E250.right");var subQ2=makeQuery(id+"F25.imprint","INTERSECT",VERTEX,{"derivedFrom":[subQ1,subQ0]});Q487=makeQuery(id+"F25.imprint","IMPRINT",FACE,{"disambiguationData":[TD([[makeQuery(id+"F25.imprint","IMPRINT",EDGE,{"disambiguationData":[TD([[subQ2,-1.0]])],"derivedFrom":subQ1}),1.0]])]});}
            var Q488;
            {var subQ0=sQuery(id+"F25.wireOp",EDGE,"E334.MirrorCS");var subQ1=sQuery(id+"F25.wireOp",EDGE,"E324.MirrorCS");var subQ2=makeQuery(id+"F25.imprint","INTERSECT",VERTEX,{"derivedFrom":[subQ1,subQ0]});Q488=makeQuery(id+"F25.imprint","IMPRINT",FACE,{"disambiguationData":[TD([[makeQuery(id+"F25.imprint","IMPRINT",EDGE,{"disambiguationData":[TD([[subQ2,-1.0]])],"derivedFrom":subQ1}),1.0]])]});}
            var Q489;
            {var subQ0=sQuery(id+"F25.wireOp",EDGE,"E365.MirrorCS");var subQ1=sQuery(id+"F25.wireOp",EDGE,"E324.MirrorCS");var subQ2=makeQuery(id+"F25.imprint","INTERSECT",VERTEX,{"derivedFrom":[subQ1,subQ0]});Q489=makeQuery(id+"F25.imprint","IMPRINT",FACE,{"disambiguationData":[TD([[makeQuery(id+"F25.imprint","IMPRINT",EDGE,{"disambiguationData":[TD([[subQ2,-1.0]])],"derivedFrom":subQ1}),1.0]])]});}
            var Q490;
            {var subQ0=sQuery(id+"F25.wireOp",EDGE,"E334.MirrorCS");var subQ1=sQuery(id+"F25.wireOp",EDGE,"E349.MirrorCS");var subQ2=makeQuery(id+"F25.imprint","INTERSECT",VERTEX,{"derivedFrom":[subQ1,subQ0]});Q490=makeQuery(id+"F25.imprint","IMPRINT",FACE,{"disambiguationData":[TD([[makeQuery(id+"F25.imprint","IMPRINT",EDGE,{"disambiguationData":[TD([[subQ2,-1.0]])],"derivedFrom":subQ1}),-1.0]])]});}
            var Q491;
            {var subQ0=sQuery(id+"F25.wireOp",EDGE,"E365.MirrorCS");var subQ1=sQuery(id+"F25.wireOp",EDGE,"E349.MirrorCS");var subQ2=makeQuery(id+"F25.imprint","INTERSECT",VERTEX,{"derivedFrom":[subQ1,subQ0]});Q491=makeQuery(id+"F25.imprint","IMPRINT",FACE,{"disambiguationData":[TD([[makeQuery(id+"F25.imprint","IMPRINT",EDGE,{"disambiguationData":[TD([[subQ2,-1.0]])],"derivedFrom":subQ1}),-1.0]])]});}
            var Q492;
            {var subQ0=sQuery(id+"F25.wireOp",EDGE,"E525.trimOffspring");var subQ1=sQuery(id+"F25.wireOp",EDGE,"E250.left");var subQ2=makeQuery(id+"F25.imprint","INTERSECT",VERTEX,{"derivedFrom":[subQ1,subQ0]});Q492=makeQuery(id+"F25.imprint","IMPRINT",FACE,{"disambiguationData":[TD([[makeQuery(id+"F25.imprint","IMPRINT",EDGE,{"disambiguationData":[TD([[subQ2,-1.0]])],"derivedFrom":subQ1}),1.0]])]});}
            var Q493;
            {var subQ0=sQuery(id+"F25.wireOp",EDGE,"E285.trimOffspring");var subQ1=sQuery(id+"F25.wireOp",EDGE,"E250.left");var subQ2=makeQuery(id+"F25.imprint","INTERSECT",VERTEX,{"derivedFrom":[subQ1,subQ0]});Q493=makeQuery(id+"F25.imprint","IMPRINT",FACE,{"disambiguationData":[TD([[makeQuery(id+"F25.imprint","IMPRINT",EDGE,{"disambiguationData":[TD([[subQ2,-1.0]])],"derivedFrom":subQ1}),1.0]])]});}
            var Q494;
            {var subQ0=sQuery(id+"F25.wireOp",EDGE,"E286.trimOffspring");var subQ1=sQuery(id+"F25.wireOp",EDGE,"E250.left");var subQ2=makeQuery(id+"F25.imprint","INTERSECT",VERTEX,{"derivedFrom":[subQ1,subQ0]});Q494=makeQuery(id+"F25.imprint","IMPRINT",FACE,{"disambiguationData":[TD([[makeQuery(id+"F25.imprint","IMPRINT",EDGE,{"disambiguationData":[TD([[subQ2,-1.0]])],"derivedFrom":subQ1}),1.0]])]});}
            var Q495;
            {var subQ0=sQuery(id+"F25.wireOp",EDGE,"E285.trimOffspring");var subQ1=sQuery(id+"F25.wireOp",EDGE,"E250.right");var subQ2=makeQuery(id+"F25.imprint","INTERSECT",VERTEX,{"derivedFrom":[subQ1,subQ0]});Q495=makeQuery(id+"F25.imprint","IMPRINT",FACE,{"disambiguationData":[TD([[makeQuery(id+"F25.imprint","IMPRINT",EDGE,{"disambiguationData":[TD([[subQ2,-1.0]])],"derivedFrom":subQ1}),1.0]])]});}
            var Q496;
            {var subQ0=sQuery(id+"F25.wireOp",EDGE,"E286.trimOffspring");var subQ1=sQuery(id+"F25.wireOp",EDGE,"E250.right");var subQ2=makeQuery(id+"F25.imprint","INTERSECT",VERTEX,{"derivedFrom":[subQ1,subQ0]});Q496=makeQuery(id+"F25.imprint","IMPRINT",FACE,{"disambiguationData":[TD([[makeQuery(id+"F25.imprint","IMPRINT",EDGE,{"disambiguationData":[TD([[subQ2,-1.0]])],"derivedFrom":subQ1}),1.0]])]});}
            var Q497;
            {var subQ0=sQuery(id+"F25.wireOp",EDGE,"E223.right");Q497=makeQuery(id+"F25.imprint","IMPRINT",FACE,{"disambiguationData":[TD([[makeQuery(id+"F25.imprint","IMPRINT",EDGE,{"derivedFrom":subQ0}),1.0]])]});}
            var Q498;
            {var subQ0=sQuery(id+"F25.wireOp",EDGE,"E224.right");Q498=makeQuery(id+"F25.imprint","IMPRINT",FACE,{"disambiguationData":[TD([[makeQuery(id+"F25.imprint","IMPRINT",EDGE,{"derivedFrom":subQ0}),-1.0]])]});}
            var Q499;
            {var subQ5=sQuery(id+"F25.wireOp",EDGE,"E224.right");Q499=makeQuery(id+"F25.imprint","IMPRINT",FACE,{"disambiguationData":[TD([[makeQuery(id+"F25.imprint","IMPRINT",EDGE,{"derivedFrom":subQ5}),1.0]])]});}
            var Q500;
            {var subQ5=sQuery(id+"F25.wireOp",EDGE,"E223.right");Q500=makeQuery(id+"F25.imprint","IMPRINT",FACE,{"disambiguationData":[TD([[makeQuery(id+"F25.imprint","IMPRINT",EDGE,{"derivedFrom":subQ5}),-1.0]])]});}
            var Q501;
            {var subQ0=sQuery(id+"F25.wireOp",EDGE,"E285.trimOffspring");var subQ1=sQuery(id+"F25.wireOp",EDGE,"E249.right");var subQ2=makeQuery(id+"F25.imprint","INTERSECT",VERTEX,{"derivedFrom":[subQ1,subQ0]});Q501=makeQuery(id+"F25.imprint","IMPRINT",FACE,{"disambiguationData":[TD([[makeQuery(id+"F25.imprint","IMPRINT",EDGE,{"disambiguationData":[TD([[subQ2,-1.0]])],"derivedFrom":subQ1}),1.0]])]});}
            var Q502;
            {var subQ0=sQuery(id+"F25.wireOp",EDGE,"E286.trimOffspring");var subQ1=sQuery(id+"F25.wireOp",EDGE,"E249.right");var subQ2=makeQuery(id+"F25.imprint","INTERSECT",VERTEX,{"derivedFrom":[subQ1,subQ0]});Q502=makeQuery(id+"F25.imprint","IMPRINT",FACE,{"disambiguationData":[TD([[makeQuery(id+"F25.imprint","IMPRINT",EDGE,{"disambiguationData":[TD([[subQ2,-1.0]])],"derivedFrom":subQ1}),1.0]])]});}
            var Q503;
            {var subQ0=sQuery(id+"F25.wireOp",EDGE,"E235.right");Q503=makeQuery(id+"F25.imprint","IMPRINT",FACE,{"disambiguationData":[TD([[makeQuery(id+"F25.imprint","IMPRINT",EDGE,{"derivedFrom":subQ0}),-1.0]])]});}
            var Q504;
            {var subQ0=sQuery(id+"F25.wireOp",EDGE,"E299.MirrorCS");Q504=makeQuery(id+"F25.imprint","IMPRINT",FACE,{"disambiguationData":[TD([[makeQuery(id+"F25.imprint","IMPRINT",EDGE,{"derivedFrom":subQ0}),1.0]])]});}
            var Q505;
            {var subQ0=sQuery(id+"F25.wireOp",EDGE,"E364.MirrorCS");var subQ1=sQuery(id+"F25.wireOp",EDGE,"E332.MirrorCS");var subQ2=makeQuery(id+"F25.imprint","INTERSECT",VERTEX,{"derivedFrom":[subQ1,subQ0]});Q505=makeQuery(id+"F25.imprint","IMPRINT",FACE,{"disambiguationData":[TD([[makeQuery(id+"F25.imprint","IMPRINT",EDGE,{"disambiguationData":[TD([[subQ2,-1.0]])],"derivedFrom":subQ1}),-1.0]])]});}
            var Q506;
            {var subQ0=sQuery(id+"F25.wireOp",EDGE,"E340.MirrorCS");var subQ1=sQuery(id+"F25.wireOp",EDGE,"E364.MirrorCS");var subQ2=makeQuery(id+"F25.imprint","INTERSECT",VERTEX,{"derivedFrom":[subQ1,subQ0]});Q506=makeQuery(id+"F25.imprint","IMPRINT",FACE,{"disambiguationData":[TD([[makeQuery(id+"F25.imprint","IMPRINT",EDGE,{"disambiguationData":[TD([[subQ2,-1.0]])],"derivedFrom":subQ1}),1.0]])]});}
            var Q507;
            {var subQ0=sQuery(id+"F25.wireOp",EDGE,"E364.MirrorCS");var subQ1=sQuery(id+"F25.wireOp",EDGE,"E363.MirrorCS");var subQ2=makeQuery(id+"F25.imprint","INTERSECT",VERTEX,{"derivedFrom":[subQ1,subQ0]});Q507=makeQuery(id+"F25.imprint","IMPRINT",FACE,{"disambiguationData":[TD([[makeQuery(id+"F25.imprint","IMPRINT",EDGE,{"disambiguationData":[TD([[subQ2,-1.0]])],"derivedFrom":subQ1}),1.0]])]});}
            var Q508;
            {var subQ0=sQuery(id+"F25.wireOp",EDGE,"E388.MirrorCS");var subQ1=sQuery(id+"F25.wireOp",EDGE,"E332.MirrorCS");var subQ2=makeQuery(id+"F25.imprint","INTERSECT",VERTEX,{"derivedFrom":[subQ1,subQ0]});Q508=makeQuery(id+"F25.imprint","IMPRINT",FACE,{"disambiguationData":[TD([[makeQuery(id+"F25.imprint","IMPRINT",EDGE,{"disambiguationData":[TD([[subQ2,-1.0]])],"derivedFrom":subQ1}),-1.0]])]});}
            var Q509;
            {var subQ0=sQuery(id+"F25.wireOp",EDGE,"E340.MirrorCS");var subQ1=sQuery(id+"F25.wireOp",EDGE,"E364.MirrorCS");var subQ2=makeQuery(id+"F25.imprint","INTERSECT",VERTEX,{"derivedFrom":[subQ1,subQ0]});Q509=makeQuery(id+"F25.imprint","IMPRINT",FACE,{"disambiguationData":[TD([[makeQuery(id+"F25.imprint","IMPRINT",EDGE,{"disambiguationData":[TD([[subQ2,-1.0]])],"derivedFrom":subQ1}),-1.0]])]});}
            var Q510;
            {var subQ0=sQuery(id+"F25.wireOp",EDGE,"E359.MirrorCS");var subQ1=sQuery(id+"F25.wireOp",EDGE,"E332.MirrorCS");var subQ2=makeQuery(id+"F25.imprint","INTERSECT",VERTEX,{"derivedFrom":[subQ1,subQ0]});Q510=makeQuery(id+"F25.imprint","IMPRINT",FACE,{"disambiguationData":[TD([[makeQuery(id+"F25.imprint","IMPRINT",EDGE,{"disambiguationData":[TD([[subQ2,-1.0]])],"derivedFrom":subQ1}),-1.0]])]});}
            var Q511;
            {var subQ0=sQuery(id+"F25.wireOp",EDGE,"E340.MirrorCS");var subQ1=sQuery(id+"F25.wireOp",EDGE,"E359.MirrorCS");var subQ2=makeQuery(id+"F25.imprint","INTERSECT",VERTEX,{"derivedFrom":[subQ1,subQ0]});Q511=makeQuery(id+"F25.imprint","IMPRINT",FACE,{"disambiguationData":[TD([[makeQuery(id+"F25.imprint","IMPRINT",EDGE,{"disambiguationData":[TD([[subQ2,-1.0]])],"derivedFrom":subQ1}),1.0]])]});}
            var Q512;
            {var subQ0=sQuery(id+"F25.wireOp",EDGE,"E342.MirrorCS");var subQ1=sQuery(id+"F25.wireOp",EDGE,"E332.MirrorCS");var subQ2=makeQuery(id+"F25.imprint","INTERSECT",VERTEX,{"derivedFrom":[subQ1,subQ0]});Q512=makeQuery(id+"F25.imprint","IMPRINT",FACE,{"disambiguationData":[TD([[makeQuery(id+"F25.imprint","IMPRINT",EDGE,{"disambiguationData":[TD([[subQ2,-1.0]])],"derivedFrom":subQ1}),-1.0]])]});}
            var Q513;
            {var subQ0=sQuery(id+"F25.wireOp",EDGE,"E340.MirrorCS");var subQ1=sQuery(id+"F25.wireOp",EDGE,"E342.MirrorCS");var subQ2=makeQuery(id+"F25.imprint","INTERSECT",VERTEX,{"derivedFrom":[subQ1,subQ0]});Q513=makeQuery(id+"F25.imprint","IMPRINT",FACE,{"disambiguationData":[TD([[makeQuery(id+"F25.imprint","IMPRINT",EDGE,{"disambiguationData":[TD([[subQ2,-1.0]])],"derivedFrom":subQ1}),1.0]])]});}
            var Q514;
            {var subQ0=sQuery(id+"F25.wireOp",EDGE,"E332.MirrorCS");var subQ1=sQuery(id+"F25.wireOp",EDGE,"E328.MirrorCS");var subQ2=makeQuery(id+"F25.imprint","INTERSECT",VERTEX,{"derivedFrom":[subQ1,subQ0]});Q514=makeQuery(id+"F25.imprint","IMPRINT",FACE,{"disambiguationData":[TD([[makeQuery(id+"F25.imprint","IMPRINT",EDGE,{"disambiguationData":[TD([[subQ2,-1.0]])],"derivedFrom":subQ1}),1.0]])]});}
            var Q515;
            {var subQ0=sQuery(id+"F25.wireOp",EDGE,"E340.MirrorCS");var subQ1=sQuery(id+"F25.wireOp",EDGE,"E328.MirrorCS");var subQ2=makeQuery(id+"F25.imprint","INTERSECT",VERTEX,{"derivedFrom":[subQ1,subQ0]});Q515=makeQuery(id+"F25.imprint","IMPRINT",FACE,{"disambiguationData":[TD([[makeQuery(id+"F25.imprint","IMPRINT",EDGE,{"disambiguationData":[TD([[subQ2,-1.0]])],"derivedFrom":subQ1}),1.0]])]});}
            var Q516;
            {var subQ0=sQuery(id+"F25.wireOp",EDGE,"E340.MirrorCS");var subQ1=sQuery(id+"F25.wireOp",EDGE,"E328.MirrorCS");var subQ2=makeQuery(id+"F25.imprint","INTERSECT",VERTEX,{"derivedFrom":[subQ1,subQ0]});Q516=makeQuery(id+"F25.imprint","IMPRINT",FACE,{"disambiguationData":[TD([[makeQuery(id+"F25.imprint","IMPRINT",EDGE,{"disambiguationData":[TD([[subQ2,-1.0]])],"derivedFrom":subQ1}),-1.0]])]});}
            var Q517;
            {var subQ0=sQuery(id+"F25.wireOp",EDGE,"E332.MirrorCS");var subQ1=sQuery(id+"F25.wireOp",EDGE,"E328.MirrorCS");var subQ2=makeQuery(id+"F25.imprint","INTERSECT",VERTEX,{"derivedFrom":[subQ1,subQ0]});Q517=makeQuery(id+"F25.imprint","IMPRINT",FACE,{"disambiguationData":[TD([[makeQuery(id+"F25.imprint","IMPRINT",EDGE,{"disambiguationData":[TD([[subQ2,-1.0]])],"derivedFrom":subQ1}),-1.0]])]});}
            var Q518;
            {var subQ0=sQuery(id+"F25.wireOp",EDGE,"E358.MirrorCS");var subQ1=sQuery(id+"F25.wireOp",EDGE,"E332.MirrorCS");var subQ2=makeQuery(id+"F25.imprint","INTERSECT",VERTEX,{"derivedFrom":[subQ1,subQ0]});Q518=makeQuery(id+"F25.imprint","IMPRINT",FACE,{"disambiguationData":[TD([[makeQuery(id+"F25.imprint","IMPRINT",EDGE,{"disambiguationData":[TD([[subQ2,-1.0]])],"derivedFrom":subQ1}),-1.0]])]});}
            var Q519;
            {var subQ0=sQuery(id+"F25.wireOp",EDGE,"E340.MirrorCS");var subQ1=sQuery(id+"F25.wireOp",EDGE,"E358.MirrorCS");var subQ2=makeQuery(id+"F25.imprint","INTERSECT",VERTEX,{"derivedFrom":[subQ1,subQ0]});Q519=makeQuery(id+"F25.imprint","IMPRINT",FACE,{"disambiguationData":[TD([[makeQuery(id+"F25.imprint","IMPRINT",EDGE,{"disambiguationData":[TD([[subQ2,-1.0]])],"derivedFrom":subQ1}),1.0]])]});}
            var Q520;
            {var subQ0=sQuery(id+"F25.wireOp",EDGE,"E364.MirrorCS");var subQ1=sQuery(id+"F25.wireOp",EDGE,"E331.MirrorCS");var subQ2=makeQuery(id+"F25.imprint","INTERSECT",VERTEX,{"derivedFrom":[subQ1,subQ0]});Q520=makeQuery(id+"F25.imprint","IMPRINT",FACE,{"disambiguationData":[TD([[makeQuery(id+"F25.imprint","IMPRINT",EDGE,{"disambiguationData":[TD([[subQ2,-1.0]])],"derivedFrom":subQ1}),1.0]])]});}
            var Q521;
            {var subQ0=sQuery(id+"F25.wireOp",EDGE,"E388.MirrorCS");var subQ1=sQuery(id+"F25.wireOp",EDGE,"E331.MirrorCS");var subQ2=makeQuery(id+"F25.imprint","INTERSECT",VERTEX,{"derivedFrom":[subQ1,subQ0]});Q521=makeQuery(id+"F25.imprint","IMPRINT",FACE,{"disambiguationData":[TD([[makeQuery(id+"F25.imprint","IMPRINT",EDGE,{"disambiguationData":[TD([[subQ2,-1.0]])],"derivedFrom":subQ1}),1.0]])]});}
            var Q522;
            {var subQ0=sQuery(id+"F25.wireOp",EDGE,"E364.MirrorCS");var subQ1=sQuery(id+"F25.wireOp",EDGE,"E331.MirrorCS");var subQ2=makeQuery(id+"F25.imprint","INTERSECT",VERTEX,{"derivedFrom":[subQ1,subQ0]});Q522=makeQuery(id+"F25.imprint","IMPRINT",FACE,{"disambiguationData":[TD([[makeQuery(id+"F25.imprint","IMPRINT",EDGE,{"disambiguationData":[TD([[subQ2,-1.0]])],"derivedFrom":subQ1}),-1.0]])]});}
            var Q523;
            {var subQ0=sQuery(id+"F25.wireOp",EDGE,"E388.MirrorCS");var subQ1=sQuery(id+"F25.wireOp",EDGE,"E331.MirrorCS");var subQ2=makeQuery(id+"F25.imprint","INTERSECT",VERTEX,{"derivedFrom":[subQ1,subQ0]});Q523=makeQuery(id+"F25.imprint","IMPRINT",FACE,{"disambiguationData":[TD([[makeQuery(id+"F25.imprint","IMPRINT",EDGE,{"disambiguationData":[TD([[subQ2,-1.0]])],"derivedFrom":subQ1}),-1.0]])]});}
            var Q524;
            {var subQ0=sQuery(id+"F25.wireOp",EDGE,"E359.MirrorCS");var subQ1=sQuery(id+"F25.wireOp",EDGE,"E331.MirrorCS");var subQ2=makeQuery(id+"F25.imprint","INTERSECT",VERTEX,{"derivedFrom":[subQ1,subQ0]});Q524=makeQuery(id+"F25.imprint","IMPRINT",FACE,{"disambiguationData":[TD([[makeQuery(id+"F25.imprint","IMPRINT",EDGE,{"disambiguationData":[TD([[subQ2,-1.0]])],"derivedFrom":subQ1}),1.0]])]});}
            var Q525;
            {var subQ0=sQuery(id+"F25.wireOp",EDGE,"E363.MirrorCS");var subQ1=sQuery(id+"F25.wireOp",EDGE,"E342.MirrorCS");var subQ2=makeQuery(id+"F25.imprint","INTERSECT",VERTEX,{"derivedFrom":[subQ1,subQ0]});Q525=makeQuery(id+"F25.imprint","IMPRINT",FACE,{"disambiguationData":[TD([[makeQuery(id+"F25.imprint","IMPRINT",EDGE,{"disambiguationData":[TD([[subQ2,-1.0]])],"derivedFrom":subQ1}),1.0]])]});}
            var Q526;
            {var subQ0=sQuery(id+"F25.wireOp",EDGE,"E363.MirrorCS");var subQ1=sQuery(id+"F25.wireOp",EDGE,"E328.MirrorCS");var subQ2=makeQuery(id+"F25.imprint","INTERSECT",VERTEX,{"derivedFrom":[subQ1,subQ0]});Q526=makeQuery(id+"F25.imprint","IMPRINT",FACE,{"disambiguationData":[TD([[makeQuery(id+"F25.imprint","IMPRINT",EDGE,{"disambiguationData":[TD([[subQ2,-1.0]])],"derivedFrom":subQ1}),1.0]])]});}
            var Q527;
            {var subQ0=sQuery(id+"F25.wireOp",EDGE,"E363.MirrorCS");var subQ1=sQuery(id+"F25.wireOp",EDGE,"E328.MirrorCS");var subQ2=makeQuery(id+"F25.imprint","INTERSECT",VERTEX,{"derivedFrom":[subQ1,subQ0]});Q527=makeQuery(id+"F25.imprint","IMPRINT",FACE,{"disambiguationData":[TD([[makeQuery(id+"F25.imprint","IMPRINT",EDGE,{"disambiguationData":[TD([[subQ2,-1.0]])],"derivedFrom":subQ1}),-1.0]])]});}
            var Q528;
            {var subQ0=sQuery(id+"F25.wireOp",EDGE,"E358.MirrorCS");var subQ1=sQuery(id+"F25.wireOp",EDGE,"E331.MirrorCS");var subQ2=makeQuery(id+"F25.imprint","INTERSECT",VERTEX,{"derivedFrom":[subQ1,subQ0]});Q528=makeQuery(id+"F25.imprint","IMPRINT",FACE,{"disambiguationData":[TD([[makeQuery(id+"F25.imprint","IMPRINT",EDGE,{"disambiguationData":[TD([[subQ2,-1.0]])],"derivedFrom":subQ1}),1.0]])]});}
            var Q529;
            {var subQ0=sQuery(id+"F25.wireOp",EDGE,"E359.MirrorCS");var subQ1=sQuery(id+"F25.wireOp",EDGE,"E331.MirrorCS");var subQ2=makeQuery(id+"F25.imprint","INTERSECT",VERTEX,{"derivedFrom":[subQ1,subQ0]});Q529=makeQuery(id+"F25.imprint","IMPRINT",FACE,{"disambiguationData":[TD([[makeQuery(id+"F25.imprint","IMPRINT",EDGE,{"disambiguationData":[TD([[subQ2,-1.0]])],"derivedFrom":subQ1}),-1.0]])]});}
            var Q530;
            {var subQ0=sQuery(id+"F25.wireOp",EDGE,"E331.MirrorCS");var subQ1=sQuery(id+"F25.wireOp",EDGE,"E342.MirrorCS");var subQ2=makeQuery(id+"F25.imprint","INTERSECT",VERTEX,{"derivedFrom":[subQ1,subQ0]});Q530=makeQuery(id+"F25.imprint","IMPRINT",FACE,{"disambiguationData":[TD([[makeQuery(id+"F25.imprint","IMPRINT",EDGE,{"disambiguationData":[TD([[subQ2,-1.0]])],"derivedFrom":subQ1}),1.0]])]});}
            var Q531;
            {var subQ0=sQuery(id+"F25.wireOp",EDGE,"E331.MirrorCS");var subQ1=sQuery(id+"F25.wireOp",EDGE,"E328.MirrorCS");var subQ2=makeQuery(id+"F25.imprint","INTERSECT",VERTEX,{"derivedFrom":[subQ1,subQ0]});Q531=makeQuery(id+"F25.imprint","IMPRINT",FACE,{"disambiguationData":[TD([[makeQuery(id+"F25.imprint","IMPRINT",EDGE,{"disambiguationData":[TD([[subQ2,-1.0]])],"derivedFrom":subQ1}),1.0]])]});}
            var Q532;
            {var subQ0=sQuery(id+"F25.wireOp",EDGE,"E331.MirrorCS");var subQ1=sQuery(id+"F25.wireOp",EDGE,"E328.MirrorCS");var subQ2=makeQuery(id+"F25.imprint","INTERSECT",VERTEX,{"derivedFrom":[subQ1,subQ0]});Q532=makeQuery(id+"F25.imprint","IMPRINT",FACE,{"disambiguationData":[TD([[makeQuery(id+"F25.imprint","IMPRINT",EDGE,{"disambiguationData":[TD([[subQ2,-1.0]])],"derivedFrom":subQ1}),-1.0]])]});}
            var Q533;
            {var subQ0=sQuery(id+"F25.wireOp",EDGE,"E358.MirrorCS");var subQ1=sQuery(id+"F25.wireOp",EDGE,"E331.MirrorCS");var subQ2=makeQuery(id+"F25.imprint","INTERSECT",VERTEX,{"derivedFrom":[subQ1,subQ0]});Q533=makeQuery(id+"F25.imprint","IMPRINT",FACE,{"disambiguationData":[TD([[makeQuery(id+"F25.imprint","IMPRINT",EDGE,{"disambiguationData":[TD([[subQ2,-1.0]])],"derivedFrom":subQ1}),-1.0]])]});}
            var Q534;
            {var subQ0=sQuery(id+"F25.wireOp",EDGE,"E364.MirrorCS");var subQ1=sQuery(id+"F25.wireOp",EDGE,"E329.MirrorCS");var subQ2=makeQuery(id+"F25.imprint","INTERSECT",VERTEX,{"derivedFrom":[subQ1,subQ0]});Q534=makeQuery(id+"F25.imprint","IMPRINT",FACE,{"disambiguationData":[TD([[makeQuery(id+"F25.imprint","IMPRINT",EDGE,{"disambiguationData":[TD([[subQ2,-1.0]])],"derivedFrom":subQ1}),1.0]])]});}
            var Q535;
            {var subQ0=sQuery(id+"F25.wireOp",EDGE,"E364.MirrorCS");var subQ1=sQuery(id+"F25.wireOp",EDGE,"E329.MirrorCS");var subQ2=makeQuery(id+"F25.imprint","INTERSECT",VERTEX,{"derivedFrom":[subQ1,subQ0]});Q535=makeQuery(id+"F25.imprint","IMPRINT",FACE,{"disambiguationData":[TD([[makeQuery(id+"F25.imprint","IMPRINT",EDGE,{"disambiguationData":[TD([[subQ2,-1.0]])],"derivedFrom":subQ1}),-1.0]])]});}
            var Q536;
            {var subQ0=sQuery(id+"F25.wireOp",EDGE,"E364.MirrorCS");var subQ1=sQuery(id+"F25.wireOp",EDGE,"E354.MirrorCS");var subQ2=makeQuery(id+"F25.imprint","INTERSECT",VERTEX,{"derivedFrom":[subQ1,subQ0]});Q536=makeQuery(id+"F25.imprint","IMPRINT",FACE,{"disambiguationData":[TD([[makeQuery(id+"F25.imprint","IMPRINT",EDGE,{"disambiguationData":[TD([[subQ2,-1.0]])],"derivedFrom":subQ1}),1.0]])]});}
            var Q537;
            {var subQ0=sQuery(id+"F25.wireOp",EDGE,"E388.MirrorCS");var subQ1=sQuery(id+"F25.wireOp",EDGE,"E329.MirrorCS");var subQ2=makeQuery(id+"F25.imprint","INTERSECT",VERTEX,{"derivedFrom":[subQ1,subQ0]});Q537=makeQuery(id+"F25.imprint","IMPRINT",FACE,{"disambiguationData":[TD([[makeQuery(id+"F25.imprint","IMPRINT",EDGE,{"disambiguationData":[TD([[subQ2,-1.0]])],"derivedFrom":subQ1}),-1.0]])]});}
            var Q538;
            {var subQ0=sQuery(id+"F25.wireOp",EDGE,"E388.MirrorCS");var subQ1=sQuery(id+"F25.wireOp",EDGE,"E354.MirrorCS");var subQ2=makeQuery(id+"F25.imprint","INTERSECT",VERTEX,{"derivedFrom":[subQ1,subQ0]});Q538=makeQuery(id+"F25.imprint","IMPRINT",FACE,{"disambiguationData":[TD([[makeQuery(id+"F25.imprint","IMPRINT",EDGE,{"disambiguationData":[TD([[subQ2,-1.0]])],"derivedFrom":subQ1}),1.0]])]});}
            var Q539;
            {var subQ0=sQuery(id+"F25.wireOp",EDGE,"E359.MirrorCS");var subQ1=sQuery(id+"F25.wireOp",EDGE,"E329.MirrorCS");var subQ2=makeQuery(id+"F25.imprint","INTERSECT",VERTEX,{"derivedFrom":[subQ1,subQ0]});Q539=makeQuery(id+"F25.imprint","IMPRINT",FACE,{"disambiguationData":[TD([[makeQuery(id+"F25.imprint","IMPRINT",EDGE,{"disambiguationData":[TD([[subQ2,-1.0]])],"derivedFrom":subQ1}),-1.0]])]});}
            var Q540;
            {var subQ0=sQuery(id+"F25.wireOp",EDGE,"E359.MirrorCS");var subQ1=sQuery(id+"F25.wireOp",EDGE,"E354.MirrorCS");var subQ2=makeQuery(id+"F25.imprint","INTERSECT",VERTEX,{"derivedFrom":[subQ1,subQ0]});Q540=makeQuery(id+"F25.imprint","IMPRINT",FACE,{"disambiguationData":[TD([[makeQuery(id+"F25.imprint","IMPRINT",EDGE,{"disambiguationData":[TD([[subQ2,-1.0]])],"derivedFrom":subQ1}),1.0]])]});}
            var Q541;
            {var subQ0=sQuery(id+"F25.wireOp",EDGE,"E342.MirrorCS");var subQ1=sQuery(id+"F25.wireOp",EDGE,"E329.MirrorCS");var subQ2=makeQuery(id+"F25.imprint","INTERSECT",VERTEX,{"derivedFrom":[subQ1,subQ0]});Q541=makeQuery(id+"F25.imprint","IMPRINT",FACE,{"disambiguationData":[TD([[makeQuery(id+"F25.imprint","IMPRINT",EDGE,{"disambiguationData":[TD([[subQ2,-1.0]])],"derivedFrom":subQ1}),-1.0]])]});}
            var Q542;
            {var subQ0=sQuery(id+"F25.wireOp",EDGE,"E345.MirrorCS");var subQ1=sQuery(id+"F25.wireOp",EDGE,"E342.MirrorCS");var subQ2=makeQuery(id+"F25.imprint","INTERSECT",VERTEX,{"derivedFrom":[subQ1,subQ0]});Q542=makeQuery(id+"F25.imprint","IMPRINT",FACE,{"disambiguationData":[TD([[makeQuery(id+"F25.imprint","IMPRINT",EDGE,{"disambiguationData":[TD([[subQ2,-1.0]])],"derivedFrom":subQ1}),1.0]])]});}
            var Q543;
            {var subQ0=sQuery(id+"F25.wireOp",EDGE,"E329.MirrorCS");var subQ1=sQuery(id+"F25.wireOp",EDGE,"E328.MirrorCS");var subQ2=makeQuery(id+"F25.imprint","INTERSECT",VERTEX,{"derivedFrom":[subQ1,subQ0]});Q543=makeQuery(id+"F25.imprint","IMPRINT",FACE,{"disambiguationData":[TD([[makeQuery(id+"F25.imprint","IMPRINT",EDGE,{"disambiguationData":[TD([[subQ2,-1.0]])],"derivedFrom":subQ1}),1.0]])]});}
            var Q544;
            {var subQ0=sQuery(id+"F25.wireOp",EDGE,"E345.MirrorCS");var subQ1=sQuery(id+"F25.wireOp",EDGE,"E328.MirrorCS");var subQ2=makeQuery(id+"F25.imprint","INTERSECT",VERTEX,{"derivedFrom":[subQ1,subQ0]});Q544=makeQuery(id+"F25.imprint","IMPRINT",FACE,{"disambiguationData":[TD([[makeQuery(id+"F25.imprint","IMPRINT",EDGE,{"disambiguationData":[TD([[subQ2,-1.0]])],"derivedFrom":subQ1}),1.0]])]});}
            var Q545;
            {var subQ0=sQuery(id+"F25.wireOp",EDGE,"E329.MirrorCS");var subQ1=sQuery(id+"F25.wireOp",EDGE,"E328.MirrorCS");var subQ2=makeQuery(id+"F25.imprint","INTERSECT",VERTEX,{"derivedFrom":[subQ1,subQ0]});Q545=makeQuery(id+"F25.imprint","IMPRINT",FACE,{"disambiguationData":[TD([[makeQuery(id+"F25.imprint","IMPRINT",EDGE,{"disambiguationData":[TD([[subQ2,-1.0]])],"derivedFrom":subQ1}),-1.0]])]});}
            var Q546;
            {var subQ0=sQuery(id+"F25.wireOp",EDGE,"E345.MirrorCS");var subQ1=sQuery(id+"F25.wireOp",EDGE,"E328.MirrorCS");var subQ2=makeQuery(id+"F25.imprint","INTERSECT",VERTEX,{"derivedFrom":[subQ1,subQ0]});Q546=makeQuery(id+"F25.imprint","IMPRINT",FACE,{"disambiguationData":[TD([[makeQuery(id+"F25.imprint","IMPRINT",EDGE,{"disambiguationData":[TD([[subQ2,-1.0]])],"derivedFrom":subQ1}),-1.0]])]});}
            var Q547;
            {var subQ0=sQuery(id+"F25.wireOp",EDGE,"E358.MirrorCS");var subQ1=sQuery(id+"F25.wireOp",EDGE,"E329.MirrorCS");var subQ2=makeQuery(id+"F25.imprint","INTERSECT",VERTEX,{"derivedFrom":[subQ1,subQ0]});Q547=makeQuery(id+"F25.imprint","IMPRINT",FACE,{"disambiguationData":[TD([[makeQuery(id+"F25.imprint","IMPRINT",EDGE,{"disambiguationData":[TD([[subQ2,-1.0]])],"derivedFrom":subQ1}),-1.0]])]});}
            var Q548;
            {var subQ0=sQuery(id+"F25.wireOp",EDGE,"E358.MirrorCS");var subQ1=sQuery(id+"F25.wireOp",EDGE,"E354.MirrorCS");var subQ2=makeQuery(id+"F25.imprint","INTERSECT",VERTEX,{"derivedFrom":[subQ1,subQ0]});Q548=makeQuery(id+"F25.imprint","IMPRINT",FACE,{"disambiguationData":[TD([[makeQuery(id+"F25.imprint","IMPRINT",EDGE,{"disambiguationData":[TD([[subQ2,-1.0]])],"derivedFrom":subQ1}),1.0]])]});}
            var Q549;
            {var subQ0=sQuery(id+"F25.wireOp",EDGE,"E358.MirrorCS");var subQ1=sQuery(id+"F25.wireOp",EDGE,"E354.MirrorCS");var subQ2=makeQuery(id+"F25.imprint","INTERSECT",VERTEX,{"derivedFrom":[subQ1,subQ0]});Q549=makeQuery(id+"F25.imprint","IMPRINT",FACE,{"disambiguationData":[TD([[makeQuery(id+"F25.imprint","IMPRINT",EDGE,{"disambiguationData":[TD([[subQ2,-1.0]])],"derivedFrom":subQ1}),-1.0]])]});}
            var Q550;
            {var subQ0=sQuery(id+"F25.wireOp",EDGE,"E384.MirrorCS");var subQ1=sQuery(id+"F25.wireOp",EDGE,"E358.MirrorCS");var subQ2=makeQuery(id+"F25.imprint","INTERSECT",VERTEX,{"derivedFrom":[subQ1,subQ0]});Q550=makeQuery(id+"F25.imprint","IMPRINT",FACE,{"disambiguationData":[TD([[makeQuery(id+"F25.imprint","IMPRINT",EDGE,{"disambiguationData":[TD([[subQ2,-1.0]])],"derivedFrom":subQ1}),1.0]])]});}
            var Q551;
            {var subQ0=sQuery(id+"F25.wireOp",EDGE,"E373.MirrorCS");var subQ1=sQuery(id+"F25.wireOp",EDGE,"E342.MirrorCS");var subQ2=makeQuery(id+"F25.imprint","INTERSECT",VERTEX,{"derivedFrom":[subQ1,subQ0]});Q551=makeQuery(id+"F25.imprint","IMPRINT",FACE,{"disambiguationData":[TD([[makeQuery(id+"F25.imprint","IMPRINT",EDGE,{"disambiguationData":[TD([[subQ2,-1.0]])],"derivedFrom":subQ1}),1.0]])]});}
            var Q552;
            {var subQ0=sQuery(id+"F25.wireOp",EDGE,"E344.MirrorCS");var subQ1=sQuery(id+"F25.wireOp",EDGE,"E342.MirrorCS");var subQ2=makeQuery(id+"F25.imprint","INTERSECT",VERTEX,{"derivedFrom":[subQ1,subQ0]});Q552=makeQuery(id+"F25.imprint","IMPRINT",FACE,{"disambiguationData":[TD([[makeQuery(id+"F25.imprint","IMPRINT",EDGE,{"disambiguationData":[TD([[subQ2,-1.0]])],"derivedFrom":subQ1}),1.0]])]});}
            var Q553;
            {var subQ0=sQuery(id+"F25.wireOp",EDGE,"E344.MirrorCS");var subQ1=sQuery(id+"F25.wireOp",EDGE,"E328.MirrorCS");var subQ2=makeQuery(id+"F25.imprint","INTERSECT",VERTEX,{"derivedFrom":[subQ1,subQ0]});Q553=makeQuery(id+"F25.imprint","IMPRINT",FACE,{"disambiguationData":[TD([[makeQuery(id+"F25.imprint","IMPRINT",EDGE,{"disambiguationData":[TD([[subQ2,-1.0]])],"derivedFrom":subQ1}),1.0]])]});}
            var Q554;
            {var subQ0=sQuery(id+"F25.wireOp",EDGE,"E344.MirrorCS");var subQ1=sQuery(id+"F25.wireOp",EDGE,"E328.MirrorCS");var subQ2=makeQuery(id+"F25.imprint","INTERSECT",VERTEX,{"derivedFrom":[subQ1,subQ0]});Q554=makeQuery(id+"F25.imprint","IMPRINT",FACE,{"disambiguationData":[TD([[makeQuery(id+"F25.imprint","IMPRINT",EDGE,{"disambiguationData":[TD([[subQ2,-1.0]])],"derivedFrom":subQ1}),-1.0]])]});}
            var Q555;
            {var subQ0=sQuery(id+"F25.wireOp",EDGE,"E344.MirrorCS");var subQ1=sQuery(id+"F25.wireOp",EDGE,"E358.MirrorCS");var subQ2=makeQuery(id+"F25.imprint","INTERSECT",VERTEX,{"derivedFrom":[subQ1,subQ0]});Q555=makeQuery(id+"F25.imprint","IMPRINT",FACE,{"disambiguationData":[TD([[makeQuery(id+"F25.imprint","IMPRINT",EDGE,{"disambiguationData":[TD([[subQ2,-1.0]])],"derivedFrom":subQ1}),1.0]])]});}
            var Q556;
            {var subQ0=sQuery(id+"F25.wireOp",EDGE,"E378.MirrorCS");var subQ1=sQuery(id+"F25.wireOp",EDGE,"E342.MirrorCS");var subQ2=makeQuery(id+"F25.imprint","INTERSECT",VERTEX,{"derivedFrom":[subQ1,subQ0]});Q556=makeQuery(id+"F25.imprint","IMPRINT",FACE,{"disambiguationData":[TD([[makeQuery(id+"F25.imprint","IMPRINT",EDGE,{"disambiguationData":[TD([[subQ2,-1.0]])],"derivedFrom":subQ1}),1.0]])]});}
            var Q557;
            {var subQ0=sQuery(id+"F25.wireOp",EDGE,"E378.MirrorCS");var subQ1=sQuery(id+"F25.wireOp",EDGE,"E328.MirrorCS");var subQ2=makeQuery(id+"F25.imprint","INTERSECT",VERTEX,{"derivedFrom":[subQ1,subQ0]});Q557=makeQuery(id+"F25.imprint","IMPRINT",FACE,{"disambiguationData":[TD([[makeQuery(id+"F25.imprint","IMPRINT",EDGE,{"disambiguationData":[TD([[subQ2,-1.0]])],"derivedFrom":subQ1}),1.0]])]});}
            var Q558;
            {var subQ0=sQuery(id+"F25.wireOp",EDGE,"E378.MirrorCS");var subQ1=sQuery(id+"F25.wireOp",EDGE,"E328.MirrorCS");var subQ2=makeQuery(id+"F25.imprint","INTERSECT",VERTEX,{"derivedFrom":[subQ1,subQ0]});Q558=makeQuery(id+"F25.imprint","IMPRINT",FACE,{"disambiguationData":[TD([[makeQuery(id+"F25.imprint","IMPRINT",EDGE,{"disambiguationData":[TD([[subQ2,-1.0]])],"derivedFrom":subQ1}),-1.0]])]});}
            var Q559;
            {var subQ0=sQuery(id+"F25.wireOp",EDGE,"E378.MirrorCS");var subQ1=sQuery(id+"F25.wireOp",EDGE,"E358.MirrorCS");var subQ2=makeQuery(id+"F25.imprint","INTERSECT",VERTEX,{"derivedFrom":[subQ1,subQ0]});Q559=makeQuery(id+"F25.imprint","IMPRINT",FACE,{"disambiguationData":[TD([[makeQuery(id+"F25.imprint","IMPRINT",EDGE,{"disambiguationData":[TD([[subQ2,-1.0]])],"derivedFrom":subQ1}),1.0]])]});}
            var Q560;
            {var subQ0=sQuery(id+"F25.wireOp",EDGE,"E348.MirrorCS");var subQ1=sQuery(id+"F25.wireOp",EDGE,"E358.MirrorCS");var subQ2=makeQuery(id+"F25.imprint","INTERSECT",VERTEX,{"derivedFrom":[subQ1,subQ0]});Q560=makeQuery(id+"F25.imprint","IMPRINT",FACE,{"disambiguationData":[TD([[makeQuery(id+"F25.imprint","IMPRINT",EDGE,{"disambiguationData":[TD([[subQ2,-1.0]])],"derivedFrom":subQ1}),1.0]])]});}
            var Q561;
            {var subQ0=sQuery(id+"F25.wireOp",EDGE,"E358.MirrorCS");var subQ1=sQuery(id+"F25.wireOp",EDGE,"E335.MirrorCS");var subQ2=makeQuery(id+"F25.imprint","INTERSECT",VERTEX,{"derivedFrom":[subQ1,subQ0]});Q561=makeQuery(id+"F25.imprint","IMPRINT",FACE,{"disambiguationData":[TD([[makeQuery(id+"F25.imprint","IMPRINT",EDGE,{"disambiguationData":[TD([[subQ2,-1.0]])],"derivedFrom":subQ1}),1.0]])]});}
            var Q562;
            {var subQ0=sQuery(id+"F25.wireOp",EDGE,"E358.MirrorCS");var subQ1=sQuery(id+"F25.wireOp",EDGE,"E335.MirrorCS");var subQ2=makeQuery(id+"F25.imprint","INTERSECT",VERTEX,{"derivedFrom":[subQ1,subQ0]});Q562=makeQuery(id+"F25.imprint","IMPRINT",FACE,{"disambiguationData":[TD([[makeQuery(id+"F25.imprint","IMPRINT",EDGE,{"disambiguationData":[TD([[subQ2,-1.0]])],"derivedFrom":subQ1}),-1.0]])]});}
            var Q563;
            {var subQ0=sQuery(id+"F25.wireOp",EDGE,"E393.MirrorCS");var subQ1=sQuery(id+"F25.wireOp",EDGE,"E335.MirrorCS");var subQ2=makeQuery(id+"F25.imprint","INTERSECT",VERTEX,{"derivedFrom":[subQ1,subQ0]});Q563=makeQuery(id+"F25.imprint","IMPRINT",FACE,{"disambiguationData":[TD([[makeQuery(id+"F25.imprint","IMPRINT",EDGE,{"disambiguationData":[TD([[subQ2,-1.0]])],"derivedFrom":subQ1}),-1.0]])]});}
            var Q564;
            {var subQ0=sQuery(id+"F25.wireOp",EDGE,"E335.MirrorCS");var subQ1=sQuery(id+"F25.wireOp",EDGE,"E326.MirrorCS");var subQ2=makeQuery(id+"F25.imprint","INTERSECT",VERTEX,{"derivedFrom":[subQ1,subQ0]});Q564=makeQuery(id+"F25.imprint","IMPRINT",FACE,{"disambiguationData":[TD([[makeQuery(id+"F25.imprint","IMPRINT",EDGE,{"disambiguationData":[TD([[subQ2,-1.0]])],"derivedFrom":subQ1}),1.0]])]});}
            var Q565;
            {var subQ0=sQuery(id+"F25.wireOp",EDGE,"E394.MirrorCS");var subQ1=sQuery(id+"F25.wireOp",EDGE,"E335.MirrorCS");var subQ2=makeQuery(id+"F25.imprint","INTERSECT",VERTEX,{"derivedFrom":[subQ1,subQ0]});Q565=makeQuery(id+"F25.imprint","IMPRINT",FACE,{"disambiguationData":[TD([[makeQuery(id+"F25.imprint","IMPRINT",EDGE,{"disambiguationData":[TD([[subQ2,-1.0]])],"derivedFrom":subQ1}),-1.0]])]});}
            var Q566;
            {var subQ0=sQuery(id+"F25.wireOp",EDGE,"E360.MirrorCS");var subQ1=sQuery(id+"F25.wireOp",EDGE,"E335.MirrorCS");var subQ2=makeQuery(id+"F25.imprint","INTERSECT",VERTEX,{"derivedFrom":[subQ1,subQ0]});Q566=makeQuery(id+"F25.imprint","IMPRINT",FACE,{"disambiguationData":[TD([[makeQuery(id+"F25.imprint","IMPRINT",EDGE,{"disambiguationData":[TD([[subQ2,-1.0]])],"derivedFrom":subQ1}),-1.0]])]});}
            var Q567;
            {var subQ0=sQuery(id+"F25.wireOp",EDGE,"E336.MirrorCS");var subQ1=sQuery(id+"F25.wireOp",EDGE,"E335.MirrorCS");var subQ2=makeQuery(id+"F25.imprint","INTERSECT",VERTEX,{"derivedFrom":[subQ1,subQ0]});Q567=makeQuery(id+"F25.imprint","IMPRINT",FACE,{"disambiguationData":[TD([[makeQuery(id+"F25.imprint","IMPRINT",EDGE,{"disambiguationData":[TD([[subQ2,-1.0]])],"derivedFrom":subQ1}),-1.0]])]});}
            var Q568;
            {var subQ0=sQuery(id+"F25.wireOp",EDGE,"E383.MirrorCS");var subQ1=sQuery(id+"F25.wireOp",EDGE,"E335.MirrorCS");var subQ2=makeQuery(id+"F25.imprint","INTERSECT",VERTEX,{"derivedFrom":[subQ1,subQ0]});Q568=makeQuery(id+"F25.imprint","IMPRINT",FACE,{"disambiguationData":[TD([[makeQuery(id+"F25.imprint","IMPRINT",EDGE,{"disambiguationData":[TD([[subQ2,-1.0]])],"derivedFrom":subQ1}),-1.0]])]});}
            var Q569;
            {var subQ0=sQuery(id+"F25.wireOp",EDGE,"E350.MirrorCS");var subQ1=sQuery(id+"F25.wireOp",EDGE,"E335.MirrorCS");var subQ2=makeQuery(id+"F25.imprint","INTERSECT",VERTEX,{"derivedFrom":[subQ1,subQ0]});Q569=makeQuery(id+"F25.imprint","IMPRINT",FACE,{"disambiguationData":[TD([[makeQuery(id+"F25.imprint","IMPRINT",EDGE,{"disambiguationData":[TD([[subQ2,-1.0]])],"derivedFrom":subQ1}),-1.0]])]});}
            var Q570;
            {var subQ0=sQuery(id+"F25.wireOp",EDGE,"E383.MirrorCS");var subQ1=sQuery(id+"F25.wireOp",EDGE,"E335.MirrorCS");var subQ2=makeQuery(id+"F25.imprint","INTERSECT",VERTEX,{"derivedFrom":[subQ1,subQ0]});Q570=makeQuery(id+"F25.imprint","IMPRINT",FACE,{"disambiguationData":[TD([[makeQuery(id+"F25.imprint","IMPRINT",EDGE,{"disambiguationData":[TD([[subQ2,-1.0]])],"derivedFrom":subQ1}),1.0]])]});}
            var Q571;
            {var subQ0=sQuery(id+"F25.wireOp",EDGE,"E350.MirrorCS");var subQ1=sQuery(id+"F25.wireOp",EDGE,"E335.MirrorCS");var subQ2=makeQuery(id+"F25.imprint","INTERSECT",VERTEX,{"derivedFrom":[subQ1,subQ0]});Q571=makeQuery(id+"F25.imprint","IMPRINT",FACE,{"disambiguationData":[TD([[makeQuery(id+"F25.imprint","IMPRINT",EDGE,{"disambiguationData":[TD([[subQ2,-1.0]])],"derivedFrom":subQ1}),1.0]])]});}
            var Q572;
            {var subQ0=sQuery(id+"F25.wireOp",EDGE,"E350.MirrorCS");var subQ1=sQuery(id+"F25.wireOp",EDGE,"E344.MirrorCS");var subQ2=makeQuery(id+"F25.imprint","INTERSECT",VERTEX,{"derivedFrom":[subQ1,subQ0]});Q572=makeQuery(id+"F25.imprint","IMPRINT",FACE,{"disambiguationData":[TD([[makeQuery(id+"F25.imprint","IMPRINT",EDGE,{"disambiguationData":[TD([[subQ2,-1.0]])],"derivedFrom":subQ1}),1.0]])]});}
            var Q573;
            {var subQ0=sQuery(id+"F25.wireOp",EDGE,"E383.MirrorCS");var subQ1=sQuery(id+"F25.wireOp",EDGE,"E344.MirrorCS");var subQ2=makeQuery(id+"F25.imprint","INTERSECT",VERTEX,{"derivedFrom":[subQ1,subQ0]});Q573=makeQuery(id+"F25.imprint","IMPRINT",FACE,{"disambiguationData":[TD([[makeQuery(id+"F25.imprint","IMPRINT",EDGE,{"disambiguationData":[TD([[subQ2,-1.0]])],"derivedFrom":subQ1}),1.0]])]});}
            var Q574;
            {var subQ0=sQuery(id+"F25.wireOp",EDGE,"E350.MirrorCS");var subQ1=sQuery(id+"F25.wireOp",EDGE,"E344.MirrorCS");var subQ2=makeQuery(id+"F25.imprint","INTERSECT",VERTEX,{"derivedFrom":[subQ1,subQ0]});Q574=makeQuery(id+"F25.imprint","IMPRINT",FACE,{"disambiguationData":[TD([[makeQuery(id+"F25.imprint","IMPRINT",EDGE,{"disambiguationData":[TD([[subQ2,-1.0]])],"derivedFrom":subQ1}),-1.0]])]});}
            var Q575;
            {var subQ0=sQuery(id+"F25.wireOp",EDGE,"E383.MirrorCS");var subQ1=sQuery(id+"F25.wireOp",EDGE,"E344.MirrorCS");var subQ2=makeQuery(id+"F25.imprint","INTERSECT",VERTEX,{"derivedFrom":[subQ1,subQ0]});Q575=makeQuery(id+"F25.imprint","IMPRINT",FACE,{"disambiguationData":[TD([[makeQuery(id+"F25.imprint","IMPRINT",EDGE,{"disambiguationData":[TD([[subQ2,-1.0]])],"derivedFrom":subQ1}),-1.0]])]});}
            var Q576;
            {var subQ0=sQuery(id+"F25.wireOp",EDGE,"E373.MirrorCS");var subQ1=sQuery(id+"F25.wireOp",EDGE,"E350.MirrorCS");var subQ2=makeQuery(id+"F25.imprint","INTERSECT",VERTEX,{"derivedFrom":[subQ1,subQ0]});Q576=makeQuery(id+"F25.imprint","IMPRINT",FACE,{"disambiguationData":[TD([[makeQuery(id+"F25.imprint","IMPRINT",EDGE,{"disambiguationData":[TD([[subQ2,-1.0]])],"derivedFrom":subQ1}),1.0]])]});}
            var Q577;
            {var subQ0=sQuery(id+"F25.wireOp",EDGE,"E373.MirrorCS");var subQ1=sQuery(id+"F25.wireOp",EDGE,"E350.MirrorCS");var subQ2=makeQuery(id+"F25.imprint","INTERSECT",VERTEX,{"derivedFrom":[subQ1,subQ0]});Q577=makeQuery(id+"F25.imprint","IMPRINT",FACE,{"disambiguationData":[TD([[makeQuery(id+"F25.imprint","IMPRINT",EDGE,{"disambiguationData":[TD([[subQ2,-1.0]])],"derivedFrom":subQ1}),-1.0]])]});}
            var Q578;
            {var subQ0=sQuery(id+"F25.wireOp",EDGE,"E360.MirrorCS");var subQ1=sQuery(id+"F25.wireOp",EDGE,"E335.MirrorCS");var subQ2=makeQuery(id+"F25.imprint","INTERSECT",VERTEX,{"derivedFrom":[subQ1,subQ0]});Q578=makeQuery(id+"F25.imprint","IMPRINT",FACE,{"disambiguationData":[TD([[makeQuery(id+"F25.imprint","IMPRINT",EDGE,{"disambiguationData":[TD([[subQ2,-1.0]])],"derivedFrom":subQ1}),1.0]])]});}
            var Q579;
            {var subQ0=sQuery(id+"F25.wireOp",EDGE,"E394.MirrorCS");var subQ1=sQuery(id+"F25.wireOp",EDGE,"E335.MirrorCS");var subQ2=makeQuery(id+"F25.imprint","INTERSECT",VERTEX,{"derivedFrom":[subQ1,subQ0]});Q579=makeQuery(id+"F25.imprint","IMPRINT",FACE,{"disambiguationData":[TD([[makeQuery(id+"F25.imprint","IMPRINT",EDGE,{"disambiguationData":[TD([[subQ2,-1.0]])],"derivedFrom":subQ1}),1.0]])]});}
            var Q580;
            {var subQ0=sQuery(id+"F25.wireOp",EDGE,"E350.MirrorCS");var subQ1=sQuery(id+"F25.wireOp",EDGE,"E348.MirrorCS");var subQ2=makeQuery(id+"F25.imprint","INTERSECT",VERTEX,{"derivedFrom":[subQ1,subQ0]});Q580=makeQuery(id+"F25.imprint","IMPRINT",FACE,{"disambiguationData":[TD([[makeQuery(id+"F25.imprint","IMPRINT",EDGE,{"disambiguationData":[TD([[subQ2,-1.0]])],"derivedFrom":subQ1}),-1.0]])]});}
            var Q581;
            {var subQ0=sQuery(id+"F25.wireOp",EDGE,"E383.MirrorCS");var subQ1=sQuery(id+"F25.wireOp",EDGE,"E348.MirrorCS");var subQ2=makeQuery(id+"F25.imprint","INTERSECT",VERTEX,{"derivedFrom":[subQ1,subQ0]});Q581=makeQuery(id+"F25.imprint","IMPRINT",FACE,{"disambiguationData":[TD([[makeQuery(id+"F25.imprint","IMPRINT",EDGE,{"disambiguationData":[TD([[subQ2,-1.0]])],"derivedFrom":subQ1}),-1.0]])]});}
            var Q582;
            {var subQ0=sQuery(id+"F25.wireOp",EDGE,"E383.MirrorCS");var subQ1=sQuery(id+"F25.wireOp",EDGE,"E348.MirrorCS");var subQ2=makeQuery(id+"F25.imprint","INTERSECT",VERTEX,{"derivedFrom":[subQ1,subQ0]});Q582=makeQuery(id+"F25.imprint","IMPRINT",FACE,{"disambiguationData":[TD([[makeQuery(id+"F25.imprint","IMPRINT",EDGE,{"disambiguationData":[TD([[subQ2,-1.0]])],"derivedFrom":subQ1}),1.0]])]});}
            var Q583;
            {var subQ0=sQuery(id+"F25.wireOp",EDGE,"E350.MirrorCS");var subQ1=sQuery(id+"F25.wireOp",EDGE,"E348.MirrorCS");var subQ2=makeQuery(id+"F25.imprint","INTERSECT",VERTEX,{"derivedFrom":[subQ1,subQ0]});Q583=makeQuery(id+"F25.imprint","IMPRINT",FACE,{"disambiguationData":[TD([[makeQuery(id+"F25.imprint","IMPRINT",EDGE,{"disambiguationData":[TD([[subQ2,-1.0]])],"derivedFrom":subQ1}),1.0]])]});}
            var Q584;
            {var subQ0=sQuery(id+"F25.wireOp",EDGE,"E310.MirrorCS");Q584=makeQuery(id+"F25.imprint","IMPRINT",FACE,{"disambiguationData":[TD([[makeQuery(id+"F25.imprint","IMPRINT",EDGE,{"derivedFrom":subQ0}),-1.0]])]});}
            var Q585;
            {var subQ0=sQuery(id+"F25.wireOp",EDGE,"E384.MirrorCS");var subQ1=sQuery(id+"F25.wireOp",EDGE,"E351.MirrorCS");var subQ2=makeQuery(id+"F25.imprint","INTERSECT",VERTEX,{"derivedFrom":[subQ1,subQ0]});Q585=makeQuery(id+"F25.imprint","IMPRINT",FACE,{"disambiguationData":[TD([[makeQuery(id+"F25.imprint","IMPRINT",EDGE,{"disambiguationData":[TD([[subQ2,-1.0]])],"derivedFrom":subQ1}),1.0]])]});}
            var Q586;
            {var subQ0=sQuery(id+"F25.wireOp",EDGE,"E384.MirrorCS");var subQ1=sQuery(id+"F25.wireOp",EDGE,"E326.MirrorCS");var subQ2=makeQuery(id+"F25.imprint","INTERSECT",VERTEX,{"derivedFrom":[subQ1,subQ0]});Q586=makeQuery(id+"F25.imprint","IMPRINT",FACE,{"disambiguationData":[TD([[makeQuery(id+"F25.imprint","IMPRINT",EDGE,{"disambiguationData":[TD([[subQ2,-1.0]])],"derivedFrom":subQ1}),-1.0]])]});}
            var Q587;
            {var subQ0=sQuery(id+"F25.wireOp",EDGE,"E344.MirrorCS");var subQ1=sQuery(id+"F25.wireOp",EDGE,"E326.MirrorCS");var subQ2=makeQuery(id+"F25.imprint","INTERSECT",VERTEX,{"derivedFrom":[subQ1,subQ0]});Q587=makeQuery(id+"F25.imprint","IMPRINT",FACE,{"disambiguationData":[TD([[makeQuery(id+"F25.imprint","IMPRINT",EDGE,{"disambiguationData":[TD([[subQ2,-1.0]])],"derivedFrom":subQ1}),-1.0]])]});}
            var Q588;
            {var subQ0=sQuery(id+"F25.wireOp",EDGE,"E373.MirrorCS");var subQ1=sQuery(id+"F25.wireOp",EDGE,"E326.MirrorCS");var subQ2=makeQuery(id+"F25.imprint","INTERSECT",VERTEX,{"derivedFrom":[subQ1,subQ0]});Q588=makeQuery(id+"F25.imprint","IMPRINT",FACE,{"disambiguationData":[TD([[makeQuery(id+"F25.imprint","IMPRINT",EDGE,{"disambiguationData":[TD([[subQ2,-1.0]])],"derivedFrom":subQ1}),-1.0]])]});}
            var Q589;
            {var subQ0=sQuery(id+"F25.wireOp",EDGE,"E378.MirrorCS");var subQ1=sQuery(id+"F25.wireOp",EDGE,"E326.MirrorCS");var subQ2=makeQuery(id+"F25.imprint","INTERSECT",VERTEX,{"derivedFrom":[subQ1,subQ0]});Q589=makeQuery(id+"F25.imprint","IMPRINT",FACE,{"disambiguationData":[TD([[makeQuery(id+"F25.imprint","IMPRINT",EDGE,{"disambiguationData":[TD([[subQ2,-1.0]])],"derivedFrom":subQ1}),-1.0]])]});}
            var Q590;
            {var subQ0=sQuery(id+"F25.wireOp",EDGE,"E348.MirrorCS");var subQ1=sQuery(id+"F25.wireOp",EDGE,"E326.MirrorCS");var subQ2=makeQuery(id+"F25.imprint","INTERSECT",VERTEX,{"derivedFrom":[subQ1,subQ0]});Q590=makeQuery(id+"F25.imprint","IMPRINT",FACE,{"disambiguationData":[TD([[makeQuery(id+"F25.imprint","IMPRINT",EDGE,{"disambiguationData":[TD([[subQ2,-1.0]])],"derivedFrom":subQ1}),-1.0]])]});}
            var Q591;
            {var subQ0=sQuery(id+"F25.wireOp",EDGE,"E369.MirrorCS");var subQ1=sQuery(id+"F25.wireOp",EDGE,"E326.MirrorCS");var subQ2=makeQuery(id+"F25.imprint","INTERSECT",VERTEX,{"derivedFrom":[subQ1,subQ0]});Q591=makeQuery(id+"F25.imprint","IMPRINT",FACE,{"disambiguationData":[TD([[makeQuery(id+"F25.imprint","IMPRINT",EDGE,{"disambiguationData":[TD([[subQ2,-1.0]])],"derivedFrom":subQ1}),-1.0]])]});}
            var Q592;
            {var subQ0=sQuery(id+"F25.wireOp",EDGE,"E335.MirrorCS");var subQ1=sQuery(id+"F25.wireOp",EDGE,"E326.MirrorCS");var subQ2=makeQuery(id+"F25.imprint","INTERSECT",VERTEX,{"derivedFrom":[subQ1,subQ0]});Q592=makeQuery(id+"F25.imprint","IMPRINT",FACE,{"disambiguationData":[TD([[makeQuery(id+"F25.imprint","IMPRINT",EDGE,{"disambiguationData":[TD([[subQ2,-1.0]])],"derivedFrom":subQ1}),-1.0]])]});}
            var Q593;
            {var subQ0=sQuery(id+"F25.wireOp",EDGE,"E394.MirrorCS");var subQ1=sQuery(id+"F25.wireOp",EDGE,"E348.MirrorCS");var subQ2=makeQuery(id+"F25.imprint","INTERSECT",VERTEX,{"derivedFrom":[subQ1,subQ0]});Q593=makeQuery(id+"F25.imprint","IMPRINT",FACE,{"disambiguationData":[TD([[makeQuery(id+"F25.imprint","IMPRINT",EDGE,{"disambiguationData":[TD([[subQ2,-1.0]])],"derivedFrom":subQ1}),-1.0]])]});}
            var Q594;
            {var subQ0=sQuery(id+"F25.wireOp",EDGE,"E348.MirrorCS");var subQ1=sQuery(id+"F25.wireOp",EDGE,"E336.MirrorCS");var subQ2=makeQuery(id+"F25.imprint","INTERSECT",VERTEX,{"derivedFrom":[subQ1,subQ0]});Q594=makeQuery(id+"F25.imprint","IMPRINT",FACE,{"disambiguationData":[TD([[makeQuery(id+"F25.imprint","IMPRINT",EDGE,{"disambiguationData":[TD([[subQ2,-1.0]])],"derivedFrom":subQ1}),-1.0]])]});}
            var Q595;
            {var subQ0=sQuery(id+"F25.wireOp",EDGE,"E378.MirrorCS");var subQ1=sQuery(id+"F25.wireOp",EDGE,"E336.MirrorCS");var subQ2=makeQuery(id+"F25.imprint","INTERSECT",VERTEX,{"derivedFrom":[subQ1,subQ0]});Q595=makeQuery(id+"F25.imprint","IMPRINT",FACE,{"disambiguationData":[TD([[makeQuery(id+"F25.imprint","IMPRINT",EDGE,{"disambiguationData":[TD([[subQ2,-1.0]])],"derivedFrom":subQ1}),-1.0]])]});}
            var Q596;
            {var subQ0=sQuery(id+"F25.wireOp",EDGE,"E394.MirrorCS");var subQ1=sQuery(id+"F25.wireOp",EDGE,"E348.MirrorCS");var subQ2=makeQuery(id+"F25.imprint","INTERSECT",VERTEX,{"derivedFrom":[subQ1,subQ0]});Q596=makeQuery(id+"F25.imprint","IMPRINT",FACE,{"disambiguationData":[TD([[makeQuery(id+"F25.imprint","IMPRINT",EDGE,{"disambiguationData":[TD([[subQ2,-1.0]])],"derivedFrom":subQ1}),1.0]])]});}
            var Q597;
            {var subQ0=sQuery(id+"F25.wireOp",EDGE,"E394.MirrorCS");var subQ1=sQuery(id+"F25.wireOp",EDGE,"E373.MirrorCS");var subQ2=makeQuery(id+"F25.imprint","INTERSECT",VERTEX,{"derivedFrom":[subQ1,subQ0]});Q597=makeQuery(id+"F25.imprint","IMPRINT",FACE,{"disambiguationData":[TD([[makeQuery(id+"F25.imprint","IMPRINT",EDGE,{"disambiguationData":[TD([[subQ2,-1.0]])],"derivedFrom":subQ1}),-1.0]])]});}
            var Q598;
            {var subQ0=sQuery(id+"F25.wireOp",EDGE,"E373.MirrorCS");var subQ1=sQuery(id+"F25.wireOp",EDGE,"E336.MirrorCS");var subQ2=makeQuery(id+"F25.imprint","INTERSECT",VERTEX,{"derivedFrom":[subQ1,subQ0]});Q598=makeQuery(id+"F25.imprint","IMPRINT",FACE,{"disambiguationData":[TD([[makeQuery(id+"F25.imprint","IMPRINT",EDGE,{"disambiguationData":[TD([[subQ2,-1.0]])],"derivedFrom":subQ1}),-1.0]])]});}
            var Q599;
            {var subQ0=sQuery(id+"F25.wireOp",EDGE,"E344.MirrorCS");var subQ1=sQuery(id+"F25.wireOp",EDGE,"E336.MirrorCS");var subQ2=makeQuery(id+"F25.imprint","INTERSECT",VERTEX,{"derivedFrom":[subQ1,subQ0]});Q599=makeQuery(id+"F25.imprint","IMPRINT",FACE,{"disambiguationData":[TD([[makeQuery(id+"F25.imprint","IMPRINT",EDGE,{"disambiguationData":[TD([[subQ2,-1.0]])],"derivedFrom":subQ1}),-1.0]])]});}
            var Q600;
            {var subQ0=sQuery(id+"F25.wireOp",EDGE,"E394.MirrorCS");var subQ1=sQuery(id+"F25.wireOp",EDGE,"E344.MirrorCS");var subQ2=makeQuery(id+"F25.imprint","INTERSECT",VERTEX,{"derivedFrom":[subQ1,subQ0]});Q600=makeQuery(id+"F25.imprint","IMPRINT",FACE,{"disambiguationData":[TD([[makeQuery(id+"F25.imprint","IMPRINT",EDGE,{"disambiguationData":[TD([[subQ2,-1.0]])],"derivedFrom":subQ1}),-1.0]])]});}
            var Q601;
            {var subQ0=sQuery(id+"F25.wireOp",EDGE,"E394.MirrorCS");var subQ1=sQuery(id+"F25.wireOp",EDGE,"E344.MirrorCS");var subQ2=makeQuery(id+"F25.imprint","INTERSECT",VERTEX,{"derivedFrom":[subQ1,subQ0]});Q601=makeQuery(id+"F25.imprint","IMPRINT",FACE,{"disambiguationData":[TD([[makeQuery(id+"F25.imprint","IMPRINT",EDGE,{"disambiguationData":[TD([[subQ2,-1.0]])],"derivedFrom":subQ1}),1.0]])]});}
            var Q602;
            {var subQ0=sQuery(id+"F25.wireOp",EDGE,"E384.MirrorCS");var subQ1=sQuery(id+"F25.wireOp",EDGE,"E336.MirrorCS");var subQ2=makeQuery(id+"F25.imprint","INTERSECT",VERTEX,{"derivedFrom":[subQ1,subQ0]});Q602=makeQuery(id+"F25.imprint","IMPRINT",FACE,{"disambiguationData":[TD([[makeQuery(id+"F25.imprint","IMPRINT",EDGE,{"disambiguationData":[TD([[subQ2,-1.0]])],"derivedFrom":subQ1}),-1.0]])]});}
            extrude(context, id + "F33", {"entities" : qUnion([Q0, Q1, Q2, Q3, Q4, Q5, Q6, Q7, Q8, Q9, Q10, Q11, Q12, Q13, Q14, Q15, Q16, Q17, Q18, Q19, Q20, Q21, Q22, Q23, Q24, Q25, Q26, Q27, Q28, Q29, Q30, Q31, Q32, Q33, Q34, Q35, Q36, Q37, Q38, Q39, Q40, Q41, Q42, Q43, Q44, Q45, Q46, Q47, Q48, Q49, Q50, Q51, Q52, Q53, Q54, Q55, Q56, Q57, Q58, Q59, Q60, Q61, Q62, Q63, Q64, Q65, Q66, Q67, Q68, Q69, Q70, Q71, Q72, Q73, Q74, Q75, Q76, Q77, Q78, Q79, Q80, Q81, Q82, Q83, Q84, Q85, Q86, Q87, Q88, Q89, Q90, Q91, Q92, Q93, Q94, Q95, Q96, Q97, Q98, Q99, Q100, Q101, Q102, Q103, Q104, Q105, Q106, Q107, Q108, Q109, Q110, Q111, Q112, Q113, Q114, Q115, Q116, Q117, Q118, Q119, Q120, Q121, Q122, Q123, Q124, Q125, Q126, Q127, Q128, Q129, Q130, Q131, Q132, Q133, Q134, Q135, Q136, Q137, Q138, Q139, Q140, Q141, Q142, Q143, Q144, Q145, Q146, Q147, Q148, Q149, Q150, Q151, Q152, Q153, Q154, Q155, Q156, Q157, Q158, Q159, Q160, Q161, Q162, Q163, Q164, Q165, Q166, Q167, Q168, Q169, Q170, Q171, Q172, Q173, Q174, Q175, Q176, Q177, Q178, Q179, Q180, Q181, Q182, Q183, Q184, Q185, Q186, Q187, Q188, Q189, Q190, Q191, Q192, Q193, Q194, Q195, Q196, Q197, Q198, Q199, Q200, Q201, Q202, Q203, Q204, Q205, Q206, Q207, Q208, Q209, Q210, Q211, Q212, Q213, Q214, Q215, Q216, Q217, Q218, Q219, Q220, Q221, Q222, Q223, Q224, Q225, Q226, Q227, Q228, Q229, Q230, Q231, Q232, Q233, Q234, Q235, Q236, Q237, Q238, Q239, Q240, Q241, Q242, Q243, Q244, Q245, Q246, Q247, Q248, Q249, Q250, Q251, Q252, Q253, Q254, Q255, Q256, Q257, Q258, Q259, Q260, Q261, Q262, Q263, Q264, Q265, Q266, Q267, Q268, Q269, Q270, Q271, Q272, Q273, Q274, Q275, Q276, Q277, Q278, Q279, Q280, Q281, Q282, Q283, Q284, Q285, Q286, Q287, Q288, Q289, Q290, Q291, Q292, Q293, Q294, Q295, Q296, Q297, Q298, Q299, Q300, Q301, Q302, Q303, Q304, Q305, Q306, Q307, Q308, Q309, Q310, Q311, Q312, Q313, Q314, Q315, Q316, Q317, Q318, Q319, Q320, Q321, Q322, Q323, Q324, Q325, Q326, Q327, Q328, Q329, Q330, Q331, Q332, Q333, Q334, Q335, Q336, Q337, Q338, Q339, Q340, Q341, Q342, Q343, Q344, Q345, Q346, Q347, Q348, Q349, Q350, Q351, Q352, Q353, Q354, Q355, Q356, Q357, Q358, Q359, Q360, Q361, Q362, Q363, Q364, Q365, Q366, Q367, Q368, Q369, Q370, Q371, Q372, Q373, Q374, Q375, Q376, Q377, Q378, Q379, Q380, Q381, Q382, Q383, Q384, Q385, Q386, Q387, Q388, Q389, Q390, Q391, Q392, Q393, Q394, Q395, Q396, Q397, Q398, Q399, Q400, Q401, Q402, Q403, Q404, Q405, Q406, Q407, Q408, Q409, Q410, Q411, Q412, Q413, Q414, Q415, Q416, Q417, Q418, Q419, Q420, Q421, Q422, Q423, Q424, Q425, Q426, Q427, Q428, Q429, Q430, Q431, Q432, Q433, Q434, Q435, Q436, Q437, Q438, Q439, Q440, Q441, Q442, Q443, Q444, Q445, Q446, Q447, Q448, Q449, Q450, Q451, Q452, Q453, Q454, Q455, Q456, Q457, Q458, Q459, Q460, Q461, Q462, Q463, Q464, Q465, Q466, Q467, Q468, Q469, Q470, Q471, Q472, Q473, Q474, Q475, Q476, Q477, Q478, Q479, Q480, Q481, Q482, Q483, Q484, Q485, Q486, Q487, Q488, Q489, Q490, Q491, Q492, Q493, Q494, Q495, Q496, Q497, Q498, Q499, Q500, Q501, Q502, Q503, Q504, Q505, Q506, Q507, Q508, Q509, Q510, Q511, Q512, Q513, Q514, Q515, Q516, Q517, Q518, Q519, Q520, Q521, Q522, Q523, Q524, Q525, Q526, Q527, Q528, Q529, Q530, Q531, Q532, Q533, Q534, Q535, Q536, Q537, Q538, Q539, Q540, Q541, Q542, Q543, Q544, Q545, Q546, Q547, Q548, Q549, Q550, Q551, Q552, Q553, Q554, Q555, Q556, Q557, Q558, Q559, Q560, Q561, Q562, Q563, Q564, Q565, Q566, Q567, Q568, Q569, Q570, Q571, Q572, Q573, Q574, Q575, Q576, Q577, Q578, Q579, Q580, Q581, Q582, Q583, Q584, Q585, Q586, Q587, Q588, Q589, Q590, Q591, Q592, Q593, Q594, Q595, Q596, Q597, Q598, Q599, Q600, Q601, Q602]), "operationType" : NewBodyOperationType.REMOVE, "depth" : 25 * mm, "offsetDistance" : 25 * mm});
        }
        {
            var Q0;
            Q0=makeQuery(id+"F33.boolean.opBoolean","SPLIT",BODY,{"disambiguationData":[OD(4.0)],"derivedFrom":makeQuery(id+"F5.opExtrude","SWEPT_BODY",BODY,{"disambiguationData":[OSD([sQuery(id+"F2.wireOp",EDGE,"E74.top"),sQuery(id+"F2.wireOp",EDGE,"E75"),sQuery(id+"F2.wireOp",EDGE,"E76"),sQuery(id+"F2.wireOp",EDGE,"E77"),sQuery(id+"F2.wireOp",EDGE,"E89"),sQuery(id+"F2.wireOp",EDGE,"E90.trimOffspring"),sQuery(id+"F2.wireOp",EDGE,"E91"),sQuery(id+"F2.wireOp",EDGE,"E97.MirrorCS"),sQuery(id+"F2.wireOp",EDGE,"E98.MirrorCS"),sQuery(id+"F2.wireOp",EDGE,"E99.MirrorCS"),sQuery(id+"F2.wireOp",EDGE,"E100.MirrorCS"),sQuery(id+"F2.wireOp",EDGE,"E102.MirrorCS"),sQuery(id+"F2.wireOp",EDGE,"E103.MirrorCS"),sQuery(id+"F2.wireOp",EDGE,"E107.MirrorCS"),sQuery(id+"F2.wireOp",EDGE,"E108.MirrorCS"),sQuery(id+"F2.wireOp",EDGE,"E109.MirrorCS"),sQuery(id+"F2.wireOp",EDGE,"E110.MirrorCS"),sQuery(id+"F2.wireOp",EDGE,"E111.MirrorCS"),sQuery(id+"F2.wireOp",EDGE,"E115.MirrorCS"),sQuery(id+"F2.wireOp",EDGE,"E117.MirrorCS"),sQuery(id+"F2.wireOp",EDGE,"E121.MirrorCS"),sQuery(id+"F2.wireOp",EDGE,"E122.MirrorCS"),sQuery(id+"F2.wireOp",EDGE,"E123.MirrorCS"),sQuery(id+"F2.wireOp",EDGE,"E124.MirrorCS"),sQuery(id+"F2.wireOp",EDGE,"E126.MirrorCS"),sQuery(id+"F2.wireOp",EDGE,"E127.MirrorCS"),sQuery(id+"F2.wireOp",EDGE,"E128.MirrorCS"),sQuery(id+"F2.wireOp",EDGE,"E129.MirrorCS")])]})});
            var Q1;
            Q1=makeQuery(id+"F33.boolean.opBoolean","SPLIT",BODY,{"disambiguationData":[OD(3.0)],"derivedFrom":makeQuery(id+"F5.opExtrude","SWEPT_BODY",BODY,{"disambiguationData":[OSD([sQuery(id+"F2.wireOp",EDGE,"E74.top"),sQuery(id+"F2.wireOp",EDGE,"E75"),sQuery(id+"F2.wireOp",EDGE,"E76"),sQuery(id+"F2.wireOp",EDGE,"E77"),sQuery(id+"F2.wireOp",EDGE,"E89"),sQuery(id+"F2.wireOp",EDGE,"E90.trimOffspring"),sQuery(id+"F2.wireOp",EDGE,"E91"),sQuery(id+"F2.wireOp",EDGE,"E97.MirrorCS"),sQuery(id+"F2.wireOp",EDGE,"E98.MirrorCS"),sQuery(id+"F2.wireOp",EDGE,"E99.MirrorCS"),sQuery(id+"F2.wireOp",EDGE,"E100.MirrorCS"),sQuery(id+"F2.wireOp",EDGE,"E102.MirrorCS"),sQuery(id+"F2.wireOp",EDGE,"E103.MirrorCS"),sQuery(id+"F2.wireOp",EDGE,"E107.MirrorCS"),sQuery(id+"F2.wireOp",EDGE,"E108.MirrorCS"),sQuery(id+"F2.wireOp",EDGE,"E109.MirrorCS"),sQuery(id+"F2.wireOp",EDGE,"E110.MirrorCS"),sQuery(id+"F2.wireOp",EDGE,"E111.MirrorCS"),sQuery(id+"F2.wireOp",EDGE,"E115.MirrorCS"),sQuery(id+"F2.wireOp",EDGE,"E117.MirrorCS"),sQuery(id+"F2.wireOp",EDGE,"E121.MirrorCS"),sQuery(id+"F2.wireOp",EDGE,"E122.MirrorCS"),sQuery(id+"F2.wireOp",EDGE,"E123.MirrorCS"),sQuery(id+"F2.wireOp",EDGE,"E124.MirrorCS"),sQuery(id+"F2.wireOp",EDGE,"E126.MirrorCS"),sQuery(id+"F2.wireOp",EDGE,"E127.MirrorCS"),sQuery(id+"F2.wireOp",EDGE,"E128.MirrorCS"),sQuery(id+"F2.wireOp",EDGE,"E129.MirrorCS")])]})});
            var Q2;
            Q2=makeQuery(id+"F33.boolean.opBoolean","SPLIT",BODY,{"disambiguationData":[OD(2.0)],"derivedFrom":makeQuery(id+"F5.opExtrude","SWEPT_BODY",BODY,{"disambiguationData":[OSD([sQuery(id+"F2.wireOp",EDGE,"E74.top"),sQuery(id+"F2.wireOp",EDGE,"E75"),sQuery(id+"F2.wireOp",EDGE,"E76"),sQuery(id+"F2.wireOp",EDGE,"E77"),sQuery(id+"F2.wireOp",EDGE,"E89"),sQuery(id+"F2.wireOp",EDGE,"E90.trimOffspring"),sQuery(id+"F2.wireOp",EDGE,"E91"),sQuery(id+"F2.wireOp",EDGE,"E97.MirrorCS"),sQuery(id+"F2.wireOp",EDGE,"E98.MirrorCS"),sQuery(id+"F2.wireOp",EDGE,"E99.MirrorCS"),sQuery(id+"F2.wireOp",EDGE,"E100.MirrorCS"),sQuery(id+"F2.wireOp",EDGE,"E102.MirrorCS"),sQuery(id+"F2.wireOp",EDGE,"E103.MirrorCS"),sQuery(id+"F2.wireOp",EDGE,"E107.MirrorCS"),sQuery(id+"F2.wireOp",EDGE,"E108.MirrorCS"),sQuery(id+"F2.wireOp",EDGE,"E109.MirrorCS"),sQuery(id+"F2.wireOp",EDGE,"E110.MirrorCS"),sQuery(id+"F2.wireOp",EDGE,"E111.MirrorCS"),sQuery(id+"F2.wireOp",EDGE,"E115.MirrorCS"),sQuery(id+"F2.wireOp",EDGE,"E117.MirrorCS"),sQuery(id+"F2.wireOp",EDGE,"E121.MirrorCS"),sQuery(id+"F2.wireOp",EDGE,"E122.MirrorCS"),sQuery(id+"F2.wireOp",EDGE,"E123.MirrorCS"),sQuery(id+"F2.wireOp",EDGE,"E124.MirrorCS"),sQuery(id+"F2.wireOp",EDGE,"E126.MirrorCS"),sQuery(id+"F2.wireOp",EDGE,"E127.MirrorCS"),sQuery(id+"F2.wireOp",EDGE,"E128.MirrorCS"),sQuery(id+"F2.wireOp",EDGE,"E129.MirrorCS")])]})});
            var Q3;
            Q3=makeQuery(id+"F33.boolean.opBoolean","SPLIT",BODY,{"disambiguationData":[OD(1.0)],"derivedFrom":makeQuery(id+"F5.opExtrude","SWEPT_BODY",BODY,{"disambiguationData":[OSD([sQuery(id+"F2.wireOp",EDGE,"E74.top"),sQuery(id+"F2.wireOp",EDGE,"E75"),sQuery(id+"F2.wireOp",EDGE,"E76"),sQuery(id+"F2.wireOp",EDGE,"E77"),sQuery(id+"F2.wireOp",EDGE,"E89"),sQuery(id+"F2.wireOp",EDGE,"E90.trimOffspring"),sQuery(id+"F2.wireOp",EDGE,"E91"),sQuery(id+"F2.wireOp",EDGE,"E97.MirrorCS"),sQuery(id+"F2.wireOp",EDGE,"E98.MirrorCS"),sQuery(id+"F2.wireOp",EDGE,"E99.MirrorCS"),sQuery(id+"F2.wireOp",EDGE,"E100.MirrorCS"),sQuery(id+"F2.wireOp",EDGE,"E102.MirrorCS"),sQuery(id+"F2.wireOp",EDGE,"E103.MirrorCS"),sQuery(id+"F2.wireOp",EDGE,"E107.MirrorCS"),sQuery(id+"F2.wireOp",EDGE,"E108.MirrorCS"),sQuery(id+"F2.wireOp",EDGE,"E109.MirrorCS"),sQuery(id+"F2.wireOp",EDGE,"E110.MirrorCS"),sQuery(id+"F2.wireOp",EDGE,"E111.MirrorCS"),sQuery(id+"F2.wireOp",EDGE,"E115.MirrorCS"),sQuery(id+"F2.wireOp",EDGE,"E117.MirrorCS"),sQuery(id+"F2.wireOp",EDGE,"E121.MirrorCS"),sQuery(id+"F2.wireOp",EDGE,"E122.MirrorCS"),sQuery(id+"F2.wireOp",EDGE,"E123.MirrorCS"),sQuery(id+"F2.wireOp",EDGE,"E124.MirrorCS"),sQuery(id+"F2.wireOp",EDGE,"E126.MirrorCS"),sQuery(id+"F2.wireOp",EDGE,"E127.MirrorCS"),sQuery(id+"F2.wireOp",EDGE,"E128.MirrorCS"),sQuery(id+"F2.wireOp",EDGE,"E129.MirrorCS")])]})});
            deleteBodies(context, id + "F34", {"entities" : qUnion([Q0, Q1, Q2, Q3])});
        }
        {
            var Q0;
            {var subQ0=sQuery(id+"F25.wireOp",EDGE,"E255.trimOffspring");var subQ1=sQuery(id+"F25.wireOp",EDGE,"E234.top");var subQ2=makeQuery(id+"F25.imprint","INTERSECT",VERTEX,{"derivedFrom":[subQ1,subQ0]});Q0=makeQuery(id+"F25.imprint","IMPRINT",FACE,{"disambiguationData":[TD([[makeQuery(id+"F25.imprint","IMPRINT",EDGE,{"disambiguationData":[TD([[subQ2,-1.0]])],"derivedFrom":subQ1}),-1.0]])]});}
            var Q1;
            {var subQ0=sQuery(id+"F25.wireOp",EDGE,"E255.trimOffspring");var subQ1=sQuery(id+"F25.wireOp",EDGE,"E253.bottom");var subQ2=makeQuery(id+"F25.imprint","INTERSECT",VERTEX,{"derivedFrom":[subQ1,subQ0]});Q1=makeQuery(id+"F25.imprint","IMPRINT",FACE,{"disambiguationData":[TD([[makeQuery(id+"F25.imprint","IMPRINT",EDGE,{"disambiguationData":[TD([[subQ2,-1.0]])],"derivedFrom":subQ1}),1.0]])]});}
            var Q2;
            {var subQ0=sQuery(id+"F25.wireOp",EDGE,"E255.trimOffspring");var subQ1=sQuery(id+"F25.wireOp",EDGE,"E252.top");var subQ2=makeQuery(id+"F25.imprint","INTERSECT",VERTEX,{"derivedFrom":[subQ1,subQ0]});Q2=makeQuery(id+"F25.imprint","IMPRINT",FACE,{"disambiguationData":[TD([[makeQuery(id+"F25.imprint","IMPRINT",EDGE,{"disambiguationData":[TD([[subQ2,-1.0]])],"derivedFrom":subQ1}),1.0]])]});}
            var Q3;
            {var subQ0=sQuery(id+"F25.wireOp",EDGE,"E255.trimOffspring");var subQ1=sQuery(id+"F25.wireOp",EDGE,"E235.top");var subQ2=makeQuery(id+"F25.imprint","INTERSECT",VERTEX,{"derivedFrom":[subQ1,subQ0]});Q3=makeQuery(id+"F25.imprint","IMPRINT",FACE,{"disambiguationData":[TD([[makeQuery(id+"F25.imprint","IMPRINT",EDGE,{"disambiguationData":[TD([[subQ2,-1.0]])],"derivedFrom":subQ1}),1.0]])]});}
            var Q4;
            {var subQ0=sQuery(id+"F25.wireOp",EDGE,"E255.trimOffspring");var subQ1=sQuery(id+"F25.wireOp",EDGE,"E235.top");var subQ2=makeQuery(id+"F25.imprint","INTERSECT",VERTEX,{"derivedFrom":[subQ1,subQ0]});Q4=makeQuery(id+"F25.imprint","IMPRINT",FACE,{"disambiguationData":[TD([[makeQuery(id+"F25.imprint","IMPRINT",EDGE,{"disambiguationData":[TD([[subQ2,-1.0]])],"derivedFrom":subQ1}),-1.0]])]});}
            var Q5;
            {var subQ0=sQuery(id+"F25.wireOp",EDGE,"E255.trimOffspring");var subQ1=sQuery(id+"F25.wireOp",EDGE,"E236.bottom");var subQ2=makeQuery(id+"F25.imprint","INTERSECT",VERTEX,{"derivedFrom":[subQ1,subQ0]});Q5=makeQuery(id+"F25.imprint","IMPRINT",FACE,{"disambiguationData":[TD([[makeQuery(id+"F25.imprint","IMPRINT",EDGE,{"disambiguationData":[TD([[subQ2,-1.0]])],"derivedFrom":subQ1}),-1.0]])]});}
            var Q6;
            {var subQ0=sQuery(id+"F25.wireOp",EDGE,"E256.trimOffspring");var subQ1=sQuery(id+"F25.wireOp",EDGE,"E236.bottom");var subQ2=makeQuery(id+"F25.imprint","INTERSECT",VERTEX,{"derivedFrom":[subQ1,subQ0]});Q6=makeQuery(id+"F25.imprint","IMPRINT",FACE,{"disambiguationData":[TD([[makeQuery(id+"F25.imprint","IMPRINT",EDGE,{"disambiguationData":[TD([[subQ2,-1.0]])],"derivedFrom":subQ1}),-1.0]])]});}
            var Q7;
            {var subQ0=sQuery(id+"F25.wireOp",EDGE,"E256.trimOffspring");var subQ1=sQuery(id+"F25.wireOp",EDGE,"E235.top");var subQ2=makeQuery(id+"F25.imprint","INTERSECT",VERTEX,{"derivedFrom":[subQ1,subQ0]});Q7=makeQuery(id+"F25.imprint","IMPRINT",FACE,{"disambiguationData":[TD([[makeQuery(id+"F25.imprint","IMPRINT",EDGE,{"disambiguationData":[TD([[subQ2,-1.0]])],"derivedFrom":subQ1}),-1.0]])]});}
            var Q8;
            {var subQ0=sQuery(id+"F25.wireOp",EDGE,"E256.trimOffspring");var subQ1=sQuery(id+"F25.wireOp",EDGE,"E235.top");var subQ2=makeQuery(id+"F25.imprint","INTERSECT",VERTEX,{"derivedFrom":[subQ1,subQ0]});Q8=makeQuery(id+"F25.imprint","IMPRINT",FACE,{"disambiguationData":[TD([[makeQuery(id+"F25.imprint","IMPRINT",EDGE,{"disambiguationData":[TD([[subQ2,-1.0]])],"derivedFrom":subQ1}),1.0]])]});}
            var Q9;
            {var subQ0=sQuery(id+"F25.wireOp",EDGE,"E254.trimOffspring");var subQ1=sQuery(id+"F25.wireOp",EDGE,"E235.top");var subQ2=makeQuery(id+"F25.imprint","INTERSECT",VERTEX,{"derivedFrom":[subQ1,subQ0]});Q9=makeQuery(id+"F25.imprint","IMPRINT",FACE,{"disambiguationData":[TD([[makeQuery(id+"F25.imprint","IMPRINT",EDGE,{"disambiguationData":[TD([[subQ2,-1.0]])],"derivedFrom":subQ1}),-1.0]])]});}
            var Q10;
            {var subQ0=sQuery(id+"F25.wireOp",EDGE,"E254.trimOffspring");var subQ1=sQuery(id+"F25.wireOp",EDGE,"E236.bottom");var subQ2=makeQuery(id+"F25.imprint","INTERSECT",VERTEX,{"derivedFrom":[subQ1,subQ0]});Q10=makeQuery(id+"F25.imprint","IMPRINT",FACE,{"disambiguationData":[TD([[makeQuery(id+"F25.imprint","IMPRINT",EDGE,{"disambiguationData":[TD([[subQ2,-1.0]])],"derivedFrom":subQ1}),-1.0]])]});}
            var Q11;
            {var subQ0=sQuery(id+"F25.wireOp",EDGE,"E254.trimOffspring");var subQ1=sQuery(id+"F25.wireOp",EDGE,"E252.top");var subQ2=makeQuery(id+"F25.imprint","INTERSECT",VERTEX,{"derivedFrom":[subQ1,subQ0]});Q11=makeQuery(id+"F25.imprint","IMPRINT",FACE,{"disambiguationData":[TD([[makeQuery(id+"F25.imprint","IMPRINT",EDGE,{"disambiguationData":[TD([[subQ2,1.0]])],"derivedFrom":subQ1}),1.0]])]});}
            var Q12;
            {var subQ0=sQuery(id+"F25.wireOp",EDGE,"E254.trimOffspring");var subQ1=sQuery(id+"F25.wireOp",EDGE,"E253.bottom");var subQ2=makeQuery(id+"F25.imprint","INTERSECT",VERTEX,{"derivedFrom":[subQ1,subQ0]});Q12=makeQuery(id+"F25.imprint","IMPRINT",FACE,{"disambiguationData":[TD([[makeQuery(id+"F25.imprint","IMPRINT",EDGE,{"disambiguationData":[TD([[subQ2,1.0]])],"derivedFrom":subQ1}),1.0]])]});}
            var Q13;
            {var subQ0=sQuery(id+"F25.wireOp",EDGE,"E254.trimOffspring");var subQ5=sQuery(id+"F25.wireOp",EDGE,"E253.top");var subQ6=makeQuery(id+"F25.imprint","INTERSECT",VERTEX,{"derivedFrom":[subQ5,subQ0]});Q13=makeQuery(id+"F25.imprint","IMPRINT",FACE,{"disambiguationData":[TD([[makeQuery(id+"F25.imprint","IMPRINT",EDGE,{"disambiguationData":[TD([[subQ6,1.0]])],"derivedFrom":subQ5}),1.0]])]});}
            var Q14;
            {var subQ0=sQuery(id+"F25.wireOp",EDGE,"E254.trimOffspring");var subQ5=sQuery(id+"F25.wireOp",EDGE,"E235.top");var subQ8=makeQuery(id+"F25.imprint","INTERSECT",VERTEX,{"derivedFrom":[subQ5,subQ0]});Q14=makeQuery(id+"F25.imprint","IMPRINT",FACE,{"disambiguationData":[TD([[makeQuery(id+"F25.imprint","IMPRINT",EDGE,{"disambiguationData":[TD([[subQ8,-1.0]])],"derivedFrom":subQ5}),1.0]])]});}
            var Q15;
            {var subQ0=sQuery(id+"F25.wireOp",EDGE,"E257.trimOffspring");var subQ1=sQuery(id+"F25.wireOp",EDGE,"E235.top");var subQ2=makeQuery(id+"F25.imprint","INTERSECT",VERTEX,{"derivedFrom":[subQ1,subQ0]});Q15=makeQuery(id+"F25.imprint","IMPRINT",FACE,{"disambiguationData":[TD([[makeQuery(id+"F25.imprint","IMPRINT",EDGE,{"disambiguationData":[TD([[subQ2,-1.0]])],"derivedFrom":subQ1}),-1.0]])]});}
            var Q16;
            {var subQ0=sQuery(id+"F25.wireOp",EDGE,"E257.trimOffspring");var subQ1=sQuery(id+"F25.wireOp",EDGE,"E236.bottom");var subQ2=makeQuery(id+"F25.imprint","INTERSECT",VERTEX,{"derivedFrom":[subQ1,subQ0]});Q16=makeQuery(id+"F25.imprint","IMPRINT",FACE,{"disambiguationData":[TD([[makeQuery(id+"F25.imprint","IMPRINT",EDGE,{"disambiguationData":[TD([[subQ2,-1.0]])],"derivedFrom":subQ1}),-1.0]])]});}
            var Q17;
            {var subQ0=sQuery(id+"F25.wireOp",EDGE,"E257.trimOffspring");var subQ1=sQuery(id+"F25.wireOp",EDGE,"E235.top");var subQ2=makeQuery(id+"F25.imprint","INTERSECT",VERTEX,{"derivedFrom":[subQ1,subQ0]});Q17=makeQuery(id+"F25.imprint","IMPRINT",FACE,{"disambiguationData":[TD([[makeQuery(id+"F25.imprint","IMPRINT",EDGE,{"disambiguationData":[TD([[subQ2,-1.0]])],"derivedFrom":subQ1}),1.0]])]});}
            var Q18;
            {var subQ0=sQuery(id+"F25.wireOp",EDGE,"E499.trimOffspring");var subQ1=sQuery(id+"F25.wireOp",EDGE,"E257.trimOffspring");var subQ2=makeQuery(id+"F25.imprint","INTERSECT",VERTEX,{"derivedFrom":[subQ1,subQ0]});Q18=makeQuery(id+"F25.imprint","IMPRINT",FACE,{"disambiguationData":[TD([[makeQuery(id+"F25.imprint","IMPRINT",EDGE,{"disambiguationData":[TD([[subQ2,1.0]])],"derivedFrom":subQ1}),-1.0]])]});}
            var Q19;
            {var subQ0=sQuery(id+"F25.wireOp",EDGE,"E499.trimOffspring");var subQ1=sQuery(id+"F25.wireOp",EDGE,"E257.trimOffspring");var subQ2=makeQuery(id+"F25.imprint","INTERSECT",VERTEX,{"derivedFrom":[subQ1,subQ0]});Q19=makeQuery(id+"F25.imprint","IMPRINT",FACE,{"disambiguationData":[TD([[makeQuery(id+"F25.imprint","IMPRINT",EDGE,{"disambiguationData":[TD([[subQ2,-1.0]])],"derivedFrom":subQ1}),-1.0]])]});}
            var Q20;
            {var subQ0=sQuery(id+"F25.wireOp",EDGE,"E275.trimOffspring");var subQ1=sQuery(id+"F25.wireOp",EDGE,"E245.left");var subQ2=makeQuery(id+"F25.imprint","INTERSECT",VERTEX,{"derivedFrom":[subQ1,subQ0]});Q20=makeQuery(id+"F25.imprint","IMPRINT",FACE,{"disambiguationData":[TD([[makeQuery(id+"F25.imprint","IMPRINT",EDGE,{"disambiguationData":[TD([[subQ2,1.0]])],"derivedFrom":subQ1}),-1.0]])]});}
            var Q21;
            {var subQ2=sQuery(id+"F25.wireOp",EDGE,"E244.right");var subQ6=sQuery(id+"F25.wireOp",EDGE,"E275.trimOffspring");var subQ8=makeQuery(id+"F25.imprint","INTERSECT",VERTEX,{"derivedFrom":[subQ2,subQ6]});Q21=makeQuery(id+"F25.imprint","IMPRINT",FACE,{"disambiguationData":[TD([[makeQuery(id+"F25.imprint","IMPRINT",EDGE,{"disambiguationData":[TD([[subQ8,1.0]])],"derivedFrom":subQ2}),-1.0]])]});}
            var Q22;
            {var subQ0=sQuery(id+"F25.wireOp",EDGE,"E275.trimOffspring");var subQ1=sQuery(id+"F25.wireOp",EDGE,"E243.left");var subQ2=makeQuery(id+"F25.imprint","INTERSECT",VERTEX,{"derivedFrom":[subQ1,subQ0]});Q22=makeQuery(id+"F25.imprint","IMPRINT",FACE,{"disambiguationData":[TD([[makeQuery(id+"F25.imprint","IMPRINT",EDGE,{"disambiguationData":[TD([[subQ2,1.0]])],"derivedFrom":subQ1}),-1.0]])]});}
            var Q23;
            {var subQ0=sQuery(id+"F25.wireOp",EDGE,"E272.trimOffspring");var subQ1=sQuery(id+"F25.wireOp",EDGE,"E245.left");var subQ2=makeQuery(id+"F25.imprint","INTERSECT",VERTEX,{"derivedFrom":[subQ1,subQ0]});Q23=makeQuery(id+"F25.imprint","IMPRINT",FACE,{"disambiguationData":[TD([[makeQuery(id+"F25.imprint","IMPRINT",EDGE,{"disambiguationData":[TD([[subQ2,-1.0]])],"derivedFrom":subQ1}),-1.0]])]});}
            var Q24;
            {var subQ0=sQuery(id+"F25.wireOp",EDGE,"E273.trimOffspring");var subQ1=sQuery(id+"F25.wireOp",EDGE,"E245.right");var subQ2=makeQuery(id+"F25.imprint","INTERSECT",VERTEX,{"derivedFrom":[subQ1,subQ0]});Q24=makeQuery(id+"F25.imprint","IMPRINT",FACE,{"disambiguationData":[TD([[makeQuery(id+"F25.imprint","IMPRINT",EDGE,{"disambiguationData":[TD([[subQ2,1.0]])],"derivedFrom":subQ1}),-1.0]])]});}
            var Q25;
            {var subQ0=sQuery(id+"F25.wireOp",EDGE,"E272.trimOffspring");var subQ1=sQuery(id+"F25.wireOp",EDGE,"E244.right");var subQ2=makeQuery(id+"F25.imprint","INTERSECT",VERTEX,{"derivedFrom":[subQ1,subQ0]});Q25=makeQuery(id+"F25.imprint","IMPRINT",FACE,{"disambiguationData":[TD([[makeQuery(id+"F25.imprint","IMPRINT",EDGE,{"disambiguationData":[TD([[subQ2,-1.0]])],"derivedFrom":subQ1}),-1.0]])]});}
            var Q26;
            {var subQ0=sQuery(id+"F25.wireOp",EDGE,"E275.trimOffspring");var subQ1=sQuery(id+"F25.wireOp",EDGE,"E243.right");var subQ2=makeQuery(id+"F25.imprint","INTERSECT",VERTEX,{"derivedFrom":[subQ1,subQ0]});Q26=makeQuery(id+"F25.imprint","IMPRINT",FACE,{"disambiguationData":[TD([[makeQuery(id+"F25.imprint","IMPRINT",EDGE,{"disambiguationData":[TD([[subQ2,1.0]])],"derivedFrom":subQ1}),-1.0]])]});}
            var Q27;
            {var subQ0=sQuery(id+"F25.wireOp",EDGE,"E272.trimOffspring");var subQ1=sQuery(id+"F25.wireOp",EDGE,"E243.right");var subQ2=makeQuery(id+"F25.imprint","INTERSECT",VERTEX,{"derivedFrom":[subQ1,subQ0]});Q27=makeQuery(id+"F25.imprint","IMPRINT",FACE,{"disambiguationData":[TD([[makeQuery(id+"F25.imprint","IMPRINT",EDGE,{"disambiguationData":[TD([[subQ2,-1.0]])],"derivedFrom":subQ1}),-1.0]])]});}
            var Q28;
            {var subQ0=sQuery(id+"F25.wireOp",EDGE,"E272.trimOffspring");var subQ1=sQuery(id+"F25.wireOp",EDGE,"E243.left");var subQ2=makeQuery(id+"F25.imprint","INTERSECT",VERTEX,{"derivedFrom":[subQ1,subQ0]});Q28=makeQuery(id+"F25.imprint","IMPRINT",FACE,{"disambiguationData":[TD([[makeQuery(id+"F25.imprint","IMPRINT",EDGE,{"disambiguationData":[TD([[subQ2,-1.0]])],"derivedFrom":subQ1}),-1.0]])]});}
            var Q29;
            {var subQ0=sQuery(id+"F25.wireOp",EDGE,"E271.trimOffspring");var subQ1=sQuery(id+"F25.wireOp",EDGE,"E243.right");var subQ2=makeQuery(id+"F25.imprint","INTERSECT",VERTEX,{"derivedFrom":[subQ1,subQ0]});Q29=makeQuery(id+"F25.imprint","IMPRINT",FACE,{"disambiguationData":[TD([[makeQuery(id+"F25.imprint","IMPRINT",EDGE,{"disambiguationData":[TD([[subQ2,1.0]])],"derivedFrom":subQ1}),-1.0]])]});}
            var Q30;
            {var subQ0=sQuery(id+"F25.wireOp",EDGE,"E274.trimOffspring");var subQ1=sQuery(id+"F25.wireOp",EDGE,"E243.right");var subQ2=makeQuery(id+"F25.imprint","INTERSECT",VERTEX,{"derivedFrom":[subQ1,subQ0]});Q30=makeQuery(id+"F25.imprint","IMPRINT",FACE,{"disambiguationData":[TD([[makeQuery(id+"F25.imprint","IMPRINT",EDGE,{"disambiguationData":[TD([[subQ2,-1.0]])],"derivedFrom":subQ1}),-1.0]])]});}
            var Q31;
            {var subQ0=sQuery(id+"F25.wireOp",EDGE,"E274.trimOffspring");var subQ1=sQuery(id+"F25.wireOp",EDGE,"E243.left");var subQ2=makeQuery(id+"F25.imprint","INTERSECT",VERTEX,{"derivedFrom":[subQ1,subQ0]});Q31=makeQuery(id+"F25.imprint","IMPRINT",FACE,{"disambiguationData":[TD([[makeQuery(id+"F25.imprint","IMPRINT",EDGE,{"disambiguationData":[TD([[subQ2,-1.0]])],"derivedFrom":subQ1}),-1.0]])]});}
            var Q32;
            {var subQ0=sQuery(id+"F25.wireOp",EDGE,"E270.trimOffspring");var subQ1=sQuery(id+"F25.wireOp",EDGE,"E243.left");var subQ2=makeQuery(id+"F25.imprint","INTERSECT",VERTEX,{"derivedFrom":[subQ1,subQ0]});Q32=makeQuery(id+"F25.imprint","IMPRINT",FACE,{"disambiguationData":[TD([[makeQuery(id+"F25.imprint","IMPRINT",EDGE,{"disambiguationData":[TD([[subQ2,-1.0]])],"derivedFrom":subQ1}),-1.0]])]});}
            var Q33;
            {var subQ0=sQuery(id+"F25.wireOp",EDGE,"E270.trimOffspring");var subQ1=sQuery(id+"F25.wireOp",EDGE,"E244.right");var subQ2=makeQuery(id+"F25.imprint","INTERSECT",VERTEX,{"derivedFrom":[subQ1,subQ0]});Q33=makeQuery(id+"F25.imprint","IMPRINT",FACE,{"disambiguationData":[TD([[makeQuery(id+"F25.imprint","IMPRINT",EDGE,{"disambiguationData":[TD([[subQ2,-1.0]])],"derivedFrom":subQ1}),-1.0]])]});}
            var Q34;
            {var subQ0=sQuery(id+"F25.wireOp",EDGE,"E274.trimOffspring");var subQ1=sQuery(id+"F25.wireOp",EDGE,"E244.right");var subQ2=makeQuery(id+"F25.imprint","INTERSECT",VERTEX,{"derivedFrom":[subQ1,subQ0]});Q34=makeQuery(id+"F25.imprint","IMPRINT",FACE,{"disambiguationData":[TD([[makeQuery(id+"F25.imprint","IMPRINT",EDGE,{"disambiguationData":[TD([[subQ2,-1.0]])],"derivedFrom":subQ1}),-1.0]])]});}
            var Q35;
            {var subQ0=sQuery(id+"F25.wireOp",EDGE,"E274.trimOffspring");var subQ1=sQuery(id+"F25.wireOp",EDGE,"E245.right");var subQ2=makeQuery(id+"F25.imprint","INTERSECT",VERTEX,{"derivedFrom":[subQ1,subQ0]});Q35=makeQuery(id+"F25.imprint","IMPRINT",FACE,{"disambiguationData":[TD([[makeQuery(id+"F25.imprint","IMPRINT",EDGE,{"disambiguationData":[TD([[subQ2,-1.0]])],"derivedFrom":subQ1}),-1.0]])]});}
            var Q36;
            {var subQ0=sQuery(id+"F25.wireOp",EDGE,"E270.trimOffspring");var subQ1=sQuery(id+"F25.wireOp",EDGE,"E245.right");var subQ2=makeQuery(id+"F25.imprint","INTERSECT",VERTEX,{"derivedFrom":[subQ1,subQ0]});Q36=makeQuery(id+"F25.imprint","IMPRINT",FACE,{"disambiguationData":[TD([[makeQuery(id+"F25.imprint","IMPRINT",EDGE,{"disambiguationData":[TD([[subQ2,-1.0]])],"derivedFrom":subQ1}),-1.0]])]});}
            var Q37;
            {var subQ0=sQuery(id+"F25.wireOp",EDGE,"E270.trimOffspring");var subQ1=sQuery(id+"F25.wireOp",EDGE,"E245.left");var subQ2=makeQuery(id+"F25.imprint","INTERSECT",VERTEX,{"derivedFrom":[subQ1,subQ0]});Q37=makeQuery(id+"F25.imprint","IMPRINT",FACE,{"disambiguationData":[TD([[makeQuery(id+"F25.imprint","IMPRINT",EDGE,{"disambiguationData":[TD([[subQ2,-1.0]])],"derivedFrom":subQ1}),-1.0]])]});}
            var Q38;
            {var subQ0=sQuery(id+"F25.wireOp",EDGE,"E274.trimOffspring");var subQ1=sQuery(id+"F25.wireOp",EDGE,"E245.left");var subQ2=makeQuery(id+"F25.imprint","INTERSECT",VERTEX,{"derivedFrom":[subQ1,subQ0]});Q38=makeQuery(id+"F25.imprint","IMPRINT",FACE,{"disambiguationData":[TD([[makeQuery(id+"F25.imprint","IMPRINT",EDGE,{"disambiguationData":[TD([[subQ2,-1.0]])],"derivedFrom":subQ1}),-1.0]])]});}
            var Q39;
            {var subQ0=sQuery(id+"F25.wireOp",EDGE,"E274.trimOffspring");var subQ1=sQuery(id+"F25.wireOp",EDGE,"E246.right");var subQ2=makeQuery(id+"F25.imprint","INTERSECT",VERTEX,{"derivedFrom":[subQ1,subQ0]});Q39=makeQuery(id+"F25.imprint","IMPRINT",FACE,{"disambiguationData":[TD([[makeQuery(id+"F25.imprint","IMPRINT",EDGE,{"disambiguationData":[TD([[subQ2,-1.0]])],"derivedFrom":subQ1}),-1.0]])]});}
            var Q40;
            {var subQ0=sQuery(id+"F25.wireOp",EDGE,"E270.trimOffspring");var subQ1=sQuery(id+"F25.wireOp",EDGE,"E246.right");var subQ2=makeQuery(id+"F25.imprint","INTERSECT",VERTEX,{"derivedFrom":[subQ1,subQ0]});Q40=makeQuery(id+"F25.imprint","IMPRINT",FACE,{"disambiguationData":[TD([[makeQuery(id+"F25.imprint","IMPRINT",EDGE,{"disambiguationData":[TD([[subQ2,-1.0]])],"derivedFrom":subQ1}),-1.0]])]});}
            var Q41;
            {var subQ0=sQuery(id+"F25.wireOp",EDGE,"E259.trimOffspring");var subQ1=sQuery(id+"F25.wireOp",EDGE,"E236.bottom");var subQ2=makeQuery(id+"F25.imprint","INTERSECT",VERTEX,{"derivedFrom":[subQ1,subQ0]});Q41=makeQuery(id+"F25.imprint","IMPRINT",FACE,{"disambiguationData":[TD([[makeQuery(id+"F25.imprint","IMPRINT",EDGE,{"disambiguationData":[TD([[subQ2,-1.0]])],"derivedFrom":subQ1}),-1.0]])]});}
            var Q42;
            {var subQ0=sQuery(id+"F25.wireOp",EDGE,"E259.trimOffspring");var subQ1=sQuery(id+"F25.wireOp",EDGE,"E235.top");var subQ2=makeQuery(id+"F25.imprint","INTERSECT",VERTEX,{"derivedFrom":[subQ1,subQ0]});Q42=makeQuery(id+"F25.imprint","IMPRINT",FACE,{"disambiguationData":[TD([[makeQuery(id+"F25.imprint","IMPRINT",EDGE,{"disambiguationData":[TD([[subQ2,-1.0]])],"derivedFrom":subQ1}),-1.0]])]});}
            var Q43;
            {var subQ0=sQuery(id+"F25.wireOp",EDGE,"E259.trimOffspring");var subQ1=sQuery(id+"F25.wireOp",EDGE,"E235.top");var subQ2=makeQuery(id+"F25.imprint","INTERSECT",VERTEX,{"derivedFrom":[subQ1,subQ0]});Q43=makeQuery(id+"F25.imprint","IMPRINT",FACE,{"disambiguationData":[TD([[makeQuery(id+"F25.imprint","IMPRINT",EDGE,{"disambiguationData":[TD([[subQ2,-1.0]])],"derivedFrom":subQ1}),1.0]])]});}
            var Q44;
            {var subQ0=sQuery(id+"F25.wireOp",EDGE,"E499.trimOffspring");var subQ1=sQuery(id+"F25.wireOp",EDGE,"E258.trimOffspring");var subQ2=makeQuery(id+"F25.imprint","INTERSECT",VERTEX,{"derivedFrom":[subQ1,subQ0]});Q44=makeQuery(id+"F25.imprint","IMPRINT",FACE,{"disambiguationData":[TD([[makeQuery(id+"F25.imprint","IMPRINT",EDGE,{"disambiguationData":[TD([[subQ2,1.0]])],"derivedFrom":subQ1}),1.0]])]});}
            var Q45;
            {var subQ0=sQuery(id+"F25.wireOp",EDGE,"E499.trimOffspring");var subQ1=sQuery(id+"F25.wireOp",EDGE,"E258.trimOffspring");var subQ2=makeQuery(id+"F25.imprint","INTERSECT",VERTEX,{"derivedFrom":[subQ1,subQ0]});Q45=makeQuery(id+"F25.imprint","IMPRINT",FACE,{"disambiguationData":[TD([[makeQuery(id+"F25.imprint","IMPRINT",EDGE,{"disambiguationData":[TD([[subQ2,-1.0]])],"derivedFrom":subQ1}),1.0]])]});}
            var Q46;
            {var subQ0=sQuery(id+"F25.wireOp",EDGE,"E294.trimOffspring");var subQ1=sQuery(id+"F25.wireOp",EDGE,"E249.right");var subQ2=makeQuery(id+"F25.imprint","INTERSECT",VERTEX,{"derivedFrom":[subQ1,subQ0]});Q46=makeQuery(id+"F25.imprint","IMPRINT",FACE,{"disambiguationData":[TD([[makeQuery(id+"F25.imprint","IMPRINT",EDGE,{"disambiguationData":[TD([[subQ2,-1.0]])],"derivedFrom":subQ1}),1.0]])]});}
            var Q47;
            {var subQ0=sQuery(id+"F25.wireOp",EDGE,"E365.MirrorCS");var subQ1=sQuery(id+"F25.wireOp",EDGE,"E347.MirrorCS");var subQ2=makeQuery(id+"F25.imprint","INTERSECT",VERTEX,{"derivedFrom":[subQ1,subQ0]});Q47=makeQuery(id+"F25.imprint","IMPRINT",FACE,{"disambiguationData":[TD([[makeQuery(id+"F25.imprint","IMPRINT",EDGE,{"disambiguationData":[TD([[subQ2,-1.0]])],"derivedFrom":subQ1}),1.0]])]});}
            var Q48;
            {var subQ0=sQuery(id+"F25.wireOp",EDGE,"E269.trimOffspring");var subQ1=sQuery(id+"F25.wireOp",EDGE,"E244.right");var subQ2=makeQuery(id+"F25.imprint","INTERSECT",VERTEX,{"derivedFrom":[subQ1,subQ0]});Q48=makeQuery(id+"F25.imprint","IMPRINT",FACE,{"disambiguationData":[TD([[makeQuery(id+"F25.imprint","IMPRINT",EDGE,{"disambiguationData":[TD([[subQ2,-1.0]])],"derivedFrom":subQ1}),-1.0]])]});}
            var Q49;
            {var subQ0=sQuery(id+"F25.wireOp",EDGE,"E269.trimOffspring");var subQ1=sQuery(id+"F25.wireOp",EDGE,"E246.right");var subQ2=makeQuery(id+"F25.imprint","INTERSECT",VERTEX,{"derivedFrom":[subQ1,subQ0]});Q49=makeQuery(id+"F25.imprint","IMPRINT",FACE,{"disambiguationData":[TD([[makeQuery(id+"F25.imprint","IMPRINT",EDGE,{"disambiguationData":[TD([[subQ2,-1.0]])],"derivedFrom":subQ1}),-1.0]])]});}
            var Q50;
            {var subQ0=sQuery(id+"F25.wireOp",EDGE,"E269.trimOffspring");var subQ1=sQuery(id+"F25.wireOp",EDGE,"E245.right");var subQ2=makeQuery(id+"F25.imprint","INTERSECT",VERTEX,{"derivedFrom":[subQ1,subQ0]});Q50=makeQuery(id+"F25.imprint","IMPRINT",FACE,{"disambiguationData":[TD([[makeQuery(id+"F25.imprint","IMPRINT",EDGE,{"disambiguationData":[TD([[subQ2,-1.0]])],"derivedFrom":subQ1}),-1.0]])]});}
            var Q51;
            {var subQ0=sQuery(id+"F25.wireOp",EDGE,"E269.trimOffspring");var subQ1=sQuery(id+"F25.wireOp",EDGE,"E245.left");var subQ2=makeQuery(id+"F25.imprint","INTERSECT",VERTEX,{"derivedFrom":[subQ1,subQ0]});Q51=makeQuery(id+"F25.imprint","IMPRINT",FACE,{"disambiguationData":[TD([[makeQuery(id+"F25.imprint","IMPRINT",EDGE,{"disambiguationData":[TD([[subQ2,-1.0]])],"derivedFrom":subQ1}),-1.0]])]});}
            var Q52;
            {var subQ0=sQuery(id+"F25.wireOp",EDGE,"E294.trimOffspring");var subQ1=sQuery(id+"F25.wireOp",EDGE,"E250.left");var subQ2=makeQuery(id+"F25.imprint","INTERSECT",VERTEX,{"derivedFrom":[subQ1,subQ0]});Q52=makeQuery(id+"F25.imprint","IMPRINT",FACE,{"disambiguationData":[TD([[makeQuery(id+"F25.imprint","IMPRINT",EDGE,{"disambiguationData":[TD([[subQ2,-1.0]])],"derivedFrom":subQ1}),1.0]])]});}
            var Q53;
            {var subQ0=sQuery(id+"F25.wireOp",EDGE,"E294.trimOffspring");var subQ1=sQuery(id+"F25.wireOp",EDGE,"E250.right");var subQ2=makeQuery(id+"F25.imprint","INTERSECT",VERTEX,{"derivedFrom":[subQ1,subQ0]});Q53=makeQuery(id+"F25.imprint","IMPRINT",FACE,{"disambiguationData":[TD([[makeQuery(id+"F25.imprint","IMPRINT",EDGE,{"disambiguationData":[TD([[subQ2,-1.0]])],"derivedFrom":subQ1}),1.0]])]});}
            var Q54;
            {var subQ0=sQuery(id+"F25.wireOp",EDGE,"E294.trimOffspring");var subQ5=sQuery(id+"F25.wireOp",EDGE,"E249.right");var subQ6=makeQuery(id+"F25.imprint","INTERSECT",VERTEX,{"derivedFrom":[subQ5,subQ0]});Q54=makeQuery(id+"F25.imprint","IMPRINT",FACE,{"disambiguationData":[TD([[makeQuery(id+"F25.imprint","IMPRINT",EDGE,{"disambiguationData":[TD([[subQ6,-1.0]])],"derivedFrom":subQ5}),-1.0]])]});}
            var Q55;
            {var subQ3=sQuery(id+"F25.wireOp",EDGE,"E347.MirrorCS");var subQ5=sQuery(id+"F25.wireOp",EDGE,"E387.MirrorCS");var subQ6=makeQuery(id+"F25.imprint","INTERSECT",VERTEX,{"derivedFrom":[subQ3,subQ5]});Q55=makeQuery(id+"F25.imprint","IMPRINT",FACE,{"disambiguationData":[TD([[makeQuery(id+"F25.imprint","IMPRINT",EDGE,{"disambiguationData":[TD([[subQ6,1.0]])],"derivedFrom":subQ5}),1.0]])]});}
            var Q56;
            {var subQ0=sQuery(id+"F25.wireOp",EDGE,"E269.trimOffspring");var subQ1=sQuery(id+"F25.wireOp",EDGE,"E248.left");var subQ2=makeQuery(id+"F25.imprint","INTERSECT",VERTEX,{"derivedFrom":[subQ1,subQ0]});Q56=makeQuery(id+"F25.imprint","IMPRINT",FACE,{"disambiguationData":[TD([[makeQuery(id+"F25.imprint","IMPRINT",EDGE,{"disambiguationData":[TD([[subQ2,-1.0]])],"derivedFrom":subQ1}),1.0]])]});}
            var Q57;
            {var subQ0=sQuery(id+"F25.wireOp",EDGE,"E269.trimOffspring");var subQ1=sQuery(id+"F25.wireOp",EDGE,"E248.left");var subQ2=makeQuery(id+"F25.imprint","INTERSECT",VERTEX,{"derivedFrom":[subQ1,subQ0]});Q57=makeQuery(id+"F25.imprint","IMPRINT",FACE,{"disambiguationData":[TD([[makeQuery(id+"F25.imprint","IMPRINT",EDGE,{"disambiguationData":[TD([[subQ2,-1.0]])],"derivedFrom":subQ1}),-1.0]])]});}
            var Q58;
            {var subQ0=sQuery(id+"F25.wireOp",EDGE,"E510.trimOffspring");var subQ1=sQuery(id+"F25.wireOp",EDGE,"E280.trimOffspring");var subQ2=makeQuery(id+"F25.imprint","INTERSECT",VERTEX,{"derivedFrom":[subQ1,subQ0]});Q58=makeQuery(id+"F25.imprint","IMPRINT",FACE,{"disambiguationData":[TD([[makeQuery(id+"F25.imprint","IMPRINT",EDGE,{"disambiguationData":[TD([[subQ2,-1.0]])],"derivedFrom":subQ1}),1.0]])]});}
            var Q59;
            {var subQ0=sQuery(id+"F25.wireOp",EDGE,"E512.trimOffspring");var subQ1=sQuery(id+"F25.wireOp",EDGE,"E280.trimOffspring");var subQ2=makeQuery(id+"F25.imprint","INTERSECT",VERTEX,{"derivedFrom":[subQ1,subQ0]});Q59=makeQuery(id+"F25.imprint","IMPRINT",FACE,{"disambiguationData":[TD([[makeQuery(id+"F25.imprint","IMPRINT",EDGE,{"disambiguationData":[TD([[subQ2,-1.0]])],"derivedFrom":subQ1}),1.0]])]});}
            var Q60;
            {var subQ0=sQuery(id+"F25.wireOp",EDGE,"E507.trimOffspring");var subQ1=sQuery(id+"F25.wireOp",EDGE,"E280.trimOffspring");var subQ2=makeQuery(id+"F25.imprint","INTERSECT",VERTEX,{"derivedFrom":[subQ1,subQ0]});Q60=makeQuery(id+"F25.imprint","IMPRINT",FACE,{"disambiguationData":[TD([[makeQuery(id+"F25.imprint","IMPRINT",EDGE,{"disambiguationData":[TD([[subQ2,-1.0]])],"derivedFrom":subQ1}),1.0]])]});}
            var Q61;
            {var subQ0=sQuery(id+"F25.wireOp",EDGE,"E518.trimOffspring");var subQ1=sQuery(id+"F25.wireOp",EDGE,"E280.trimOffspring");var subQ2=makeQuery(id+"F25.imprint","INTERSECT",VERTEX,{"derivedFrom":[subQ1,subQ0]});Q61=makeQuery(id+"F25.imprint","IMPRINT",FACE,{"disambiguationData":[TD([[makeQuery(id+"F25.imprint","IMPRINT",EDGE,{"disambiguationData":[TD([[subQ2,-1.0]])],"derivedFrom":subQ1}),1.0]])]});}
            var Q62;
            {var subQ0=sQuery(id+"F25.wireOp",EDGE,"E519.trimOffspring");var subQ1=sQuery(id+"F25.wireOp",EDGE,"E280.trimOffspring");var subQ2=makeQuery(id+"F25.imprint","INTERSECT",VERTEX,{"derivedFrom":[subQ1,subQ0]});Q62=makeQuery(id+"F25.imprint","IMPRINT",FACE,{"disambiguationData":[TD([[makeQuery(id+"F25.imprint","IMPRINT",EDGE,{"disambiguationData":[TD([[subQ2,-1.0]])],"derivedFrom":subQ1}),1.0]])]});}
            var Q63;
            {var subQ0=sQuery(id+"F25.wireOp",EDGE,"E517.trimOffspring");var subQ1=sQuery(id+"F25.wireOp",EDGE,"E280.trimOffspring");var subQ2=makeQuery(id+"F25.imprint","INTERSECT",VERTEX,{"derivedFrom":[subQ1,subQ0]});Q63=makeQuery(id+"F25.imprint","IMPRINT",FACE,{"disambiguationData":[TD([[makeQuery(id+"F25.imprint","IMPRINT",EDGE,{"disambiguationData":[TD([[subQ2,-1.0]])],"derivedFrom":subQ1}),1.0]])]});}
            extrude(context, id + "F35", {"entities" : qUnion([Q0, Q1, Q2, Q3, Q4, Q5, Q6, Q7, Q8, Q9, Q10, Q11, Q12, Q13, Q14, Q15, Q16, Q17, Q18, Q19, Q20, Q21, Q22, Q23, Q24, Q25, Q26, Q27, Q28, Q29, Q30, Q31, Q32, Q33, Q34, Q35, Q36, Q37, Q38, Q39, Q40, Q41, Q42, Q43, Q44, Q45, Q46, Q47, Q48, Q49, Q50, Q51, Q52, Q53, Q54, Q55, Q56, Q57, Q58, Q59, Q60, Q61, Q62, Q63]), "operationType" : NewBodyOperationType.REMOVE, "depth" : 19.5 * mm, "offsetDistance" : 25 * mm});
        }
        {
            var Q0;
            Q0=qCreatedBy(id+"F1.planeOp",FACE);
            var sketch = newSketch(context, id + "F36", { "sketchPlane" : qUnion([Q0])});
            skLineSegment(sketch, "E716.bottom", {"start": v(-365, 200) * mm, "end": v(365, 200) * mm});
            skLineSegment(sketch, "E716.top", {"start": v(-365, -200) * mm, "end": v(365, -200) * mm});
            skLineSegment(sketch, "E716.left", {"start": v(-365, 200) * mm, "end": v(-365, -200) * mm});
            skLineSegment(sketch, "E716.right", {"start": v(365, 200) * mm, "end": v(365, -200) * mm});
            skPoint(sketch, "E716.middle", {"position": v(0, 0) * mm});
            skLineSegment(sketch, "E717.bottom", {"start": v(0, 0) * mm, "end": v(-365, 0) * mm});
            skLineSegment(sketch, "E717.top", {"start": v(0, -200) * mm, "end": v(-365, -200) * mm});
            skLineSegment(sketch, "E717.left", {"start": v(0, 0) * mm, "end": v(0, -200) * mm});
            skLineSegment(sketch, "E717.right", {"start": v(-365, 0) * mm, "end": v(-365, -200) * mm});
            skLineSegment(sketch, "E718.top", {"start": v(0, 50) * mm, "end": v(-365, 50) * mm});
            skLineSegment(sketch, "E718.left", {"start": v(0, 0) * mm, "end": v(0, 50) * mm});
            skLineSegment(sketch, "E718.right", {"start": v(-365, 0) * mm, "end": v(-365, 50) * mm});
            skLineSegment(sketch, "E719.bottom", {"start": v(0, 0) * mm, "end": v(-182.5, 0) * mm});
            skLineSegment(sketch, "E719.top", {"start": v(0, -50) * mm, "end": v(-182.5, -50) * mm});
            skLineSegment(sketch, "E719.left", {"start": v(0, 0) * mm, "end": v(0, -50) * mm});
            skLineSegment(sketch, "E719.right", {"start": v(-182.5, 0) * mm, "end": v(-182.5, -50) * mm});
            skPoint(sketch, "E720", {"position": v(-319.37, 0) * mm});
            skPoint(sketch, "E721", {"position": v(-273.75, 0) * mm});
            skPoint(sketch, "E722", {"position": v(-228.12, 0) * mm});
            skPoint(sketch, "E723", {"position": v(-192.5, 0) * mm});
            skPoint(sketch, "E724", {"position": v(-172.5, 0) * mm});
            skPoint(sketch, "E725", {"position": v(-136.88, 0) * mm});
            skPoint(sketch, "E726", {"position": v(-91.25, 0) * mm});
            skPoint(sketch, "E727", {"position": v(-45.62, 0) * mm});
            skPoint(sketch, "E728", {"position": v(-10, 0) * mm});
            skPoint(sketch, "E729", {"position": v(10, 0) * mm});
            skPoint(sketch, "E730", {"position": v(-365, -20) * mm});
            skPoint(sketch, "E731", {"position": v(-365, -40) * mm});
            skPoint(sketch, "E732", {"position": v(-365, -60) * mm});
            skPoint(sketch, "E733", {"position": v(-365, -87.5) * mm});
            skPoint(sketch, "E734", {"position": v(-365, -125) * mm});
            skPoint(sketch, "E735", {"position": v(-365, -162.5) * mm});
            skLineSegment(sketch, "E736.bottom", {"start": v(-365, 0) * mm, "end": v(0, 0) * mm});
            skLineSegment(sketch, "E736.top", {"start": v(-365, -0.5) * mm, "end": v(0, -0.5) * mm});
            skLineSegment(sketch, "E736.left", {"start": v(-365, 0) * mm, "end": v(-365, -0.5) * mm});
            skLineSegment(sketch, "E736.right", {"start": v(0, 0) * mm, "end": v(0, -0.5) * mm});
            skLineSegment(sketch, "E737.bottom", {"start": v(-365, -20) * mm, "end": v(0, -20) * mm});
            skLineSegment(sketch, "E737.top", {"start": v(-365, -20.5) * mm, "end": v(0, -20.5) * mm});
            skLineSegment(sketch, "E737.left", {"start": v(-365, -20) * mm, "end": v(-365, -20.5) * mm});
            skLineSegment(sketch, "E737.right", {"start": v(0, -20) * mm, "end": v(0, -20.5) * mm});
            skLineSegment(sketch, "E738.top", {"start": v(-365, -19.5) * mm, "end": v(0, -19.5) * mm});
            skLineSegment(sketch, "E738.left", {"start": v(-365, -20) * mm, "end": v(-365, -19.5) * mm});
            skLineSegment(sketch, "E738.right", {"start": v(0, -20) * mm, "end": v(0, -19.5) * mm});
            skLineSegment(sketch, "E739.bottom", {"start": v(-365, -40) * mm, "end": v(0, -40) * mm});
            skLineSegment(sketch, "E739.top", {"start": v(-365, -39.5) * mm, "end": v(0, -39.5) * mm});
            skLineSegment(sketch, "E739.left", {"start": v(-365, -40) * mm, "end": v(-365, -39.5) * mm});
            skLineSegment(sketch, "E739.right", {"start": v(0, -40) * mm, "end": v(0, -39.5) * mm});
            skLineSegment(sketch, "E740.top", {"start": v(-365, -40.5) * mm, "end": v(0, -40.5) * mm});
            skLineSegment(sketch, "E740.left", {"start": v(-365, -40) * mm, "end": v(-365, -40.5) * mm});
            skLineSegment(sketch, "E740.right", {"start": v(0, -40) * mm, "end": v(0, -40.5) * mm});
            skLineSegment(sketch, "E741.bottom", {"start": v(-365, -50) * mm, "end": v(0, -50) * mm});
            skLineSegment(sketch, "E741.top", {"start": v(-365, -49.5) * mm, "end": v(0, -49.5) * mm});
            skLineSegment(sketch, "E741.left", {"start": v(-365, -50) * mm, "end": v(-365, -49.5) * mm});
            skLineSegment(sketch, "E741.right", {"start": v(0, -50) * mm, "end": v(0, -49.5) * mm});
            skLineSegment(sketch, "E742.top", {"start": v(-365, -50.5) * mm, "end": v(0, -50.5) * mm});
            skLineSegment(sketch, "E742.left", {"start": v(-365, -50) * mm, "end": v(-365, -50.5) * mm});
            skLineSegment(sketch, "E742.right", {"start": v(0, -50) * mm, "end": v(0, -50.5) * mm});
            skLineSegment(sketch, "E743.bottom", {"start": v(-365, -60) * mm, "end": v(0, -60) * mm});
            skLineSegment(sketch, "E743.top", {"start": v(-365, -59.5) * mm, "end": v(0, -59.5) * mm});
            skLineSegment(sketch, "E743.left", {"start": v(-365, -60) * mm, "end": v(-365, -59.5) * mm});
            skLineSegment(sketch, "E743.right", {"start": v(0, -60) * mm, "end": v(0, -59.5) * mm});
            skLineSegment(sketch, "E744.top", {"start": v(-365, -60.5) * mm, "end": v(0, -60.5) * mm});
            skLineSegment(sketch, "E744.left", {"start": v(-365, -60) * mm, "end": v(-365, -60.5) * mm});
            skLineSegment(sketch, "E744.right", {"start": v(0, -60) * mm, "end": v(0, -60.5) * mm});
            skLineSegment(sketch, "E745.bottom", {"start": v(-365, -87.5) * mm, "end": v(0, -87.5) * mm});
            skLineSegment(sketch, "E745.top", {"start": v(-365, -87) * mm, "end": v(0, -87) * mm});
            skLineSegment(sketch, "E745.left", {"start": v(-365, -87.5) * mm, "end": v(-365, -87) * mm});
            skLineSegment(sketch, "E745.right", {"start": v(0, -87.5) * mm, "end": v(0, -87) * mm});
            skLineSegment(sketch, "E746.top", {"start": v(-365, -88) * mm, "end": v(0, -88) * mm});
            skLineSegment(sketch, "E746.left", {"start": v(-365, -87.5) * mm, "end": v(-365, -88) * mm});
            skLineSegment(sketch, "E746.right", {"start": v(0, -87.5) * mm, "end": v(0, -88) * mm});
            skLineSegment(sketch, "E747.bottom", {"start": v(-365, -125) * mm, "end": v(0, -125) * mm});
            skLineSegment(sketch, "E747.top", {"start": v(-365, -124.5) * mm, "end": v(0, -124.5) * mm});
            skLineSegment(sketch, "E747.left", {"start": v(-365, -125) * mm, "end": v(-365, -124.5) * mm});
            skLineSegment(sketch, "E747.right", {"start": v(0, -125) * mm, "end": v(0, -124.5) * mm});
            skLineSegment(sketch, "E748.top", {"start": v(-365, -125.5) * mm, "end": v(0, -125.5) * mm});
            skLineSegment(sketch, "E748.left", {"start": v(-365, -125) * mm, "end": v(-365, -125.5) * mm});
            skLineSegment(sketch, "E748.right", {"start": v(0, -125) * mm, "end": v(0, -125.5) * mm});
            skLineSegment(sketch, "E749.bottom", {"start": v(-365, -162.5) * mm, "end": v(0, -162.5) * mm});
            skLineSegment(sketch, "E749.top", {"start": v(-365, -162) * mm, "end": v(0, -162) * mm});
            skLineSegment(sketch, "E749.left", {"start": v(-365, -162.5) * mm, "end": v(-365, -162) * mm});
            skLineSegment(sketch, "E749.right", {"start": v(0, -162.5) * mm, "end": v(0, -162) * mm});
            skLineSegment(sketch, "E750.top", {"start": v(-365, -163) * mm, "end": v(0, -163) * mm});
            skLineSegment(sketch, "E750.left", {"start": v(-365, -162.5) * mm, "end": v(-365, -163) * mm});
            skLineSegment(sketch, "E750.right", {"start": v(0, -162.5) * mm, "end": v(0, -163) * mm});
            skLineSegment(sketch, "E751.bottom", {"start": v(-319.37, 0) * mm, "end": v(-319.87, 0) * mm});
            skLineSegment(sketch, "E751.top", {"start": v(-319.37, -200) * mm, "end": v(-319.87, -200) * mm});
            skLineSegment(sketch, "E751.left", {"start": v(-319.37, 0) * mm, "end": v(-319.37, -200) * mm});
            skLineSegment(sketch, "E751.right", {"start": v(-319.87, 0) * mm, "end": v(-319.87, -200) * mm});
            skLineSegment(sketch, "E752.bottom", {"start": v(-319.37, 0) * mm, "end": v(-318.87, 0) * mm});
            skLineSegment(sketch, "E752.top", {"start": v(-319.37, -200) * mm, "end": v(-318.87, -200) * mm});
            skLineSegment(sketch, "E752.right", {"start": v(-318.87, 0) * mm, "end": v(-318.87, -200) * mm});
            skLineSegment(sketch, "E753.bottom", {"start": v(-273.75, 0) * mm, "end": v(-274.25, 0) * mm});
            skLineSegment(sketch, "E753.top", {"start": v(-273.75, -200) * mm, "end": v(-274.25, -200) * mm});
            skLineSegment(sketch, "E753.left", {"start": v(-273.75, 0) * mm, "end": v(-273.75, -200) * mm});
            skLineSegment(sketch, "E753.right", {"start": v(-274.25, 0) * mm, "end": v(-274.25, -200) * mm});
            skLineSegment(sketch, "E754.bottom", {"start": v(-273.75, 0) * mm, "end": v(-273.25, 0) * mm});
            skLineSegment(sketch, "E754.top", {"start": v(-273.75, -200) * mm, "end": v(-273.25, -200) * mm});
            skLineSegment(sketch, "E754.right", {"start": v(-273.25, 0) * mm, "end": v(-273.25, -200) * mm});
            skLineSegment(sketch, "E755.bottom", {"start": v(-228.12, 0) * mm, "end": v(-228.62, 0) * mm});
            skLineSegment(sketch, "E755.top", {"start": v(-228.12, -200) * mm, "end": v(-228.62, -200) * mm});
            skLineSegment(sketch, "E755.left", {"start": v(-228.12, 0) * mm, "end": v(-228.12, -200) * mm});
            skLineSegment(sketch, "E755.right", {"start": v(-228.62, 0) * mm, "end": v(-228.62, -200) * mm});
            skLineSegment(sketch, "E756.bottom", {"start": v(-228.12, 0) * mm, "end": v(-227.62, 0) * mm});
            skLineSegment(sketch, "E756.top", {"start": v(-228.12, -200) * mm, "end": v(-227.62, -200) * mm});
            skLineSegment(sketch, "E756.right", {"start": v(-227.62, 0) * mm, "end": v(-227.62, -200) * mm});
            skLineSegment(sketch, "E757.bottom", {"start": v(-192.5, 0) * mm, "end": v(-193, 0) * mm});
            skLineSegment(sketch, "E757.top", {"start": v(-192.5, -200) * mm, "end": v(-193, -200) * mm});
            skLineSegment(sketch, "E757.left", {"start": v(-192.5, 0) * mm, "end": v(-192.5, -200) * mm});
            skLineSegment(sketch, "E757.right", {"start": v(-193, 0) * mm, "end": v(-193, -200) * mm});
            skLineSegment(sketch, "E758.bottom", {"start": v(-192.5, 0) * mm, "end": v(-192, 0) * mm});
            skLineSegment(sketch, "E758.top", {"start": v(-192.5, -200) * mm, "end": v(-192, -200) * mm});
            skLineSegment(sketch, "E758.right", {"start": v(-192, 0) * mm, "end": v(-192, -200) * mm});
            skLineSegment(sketch, "E759.bottom", {"start": v(-182.5, 0) * mm, "end": v(-183, 0) * mm});
            skLineSegment(sketch, "E759.top", {"start": v(-182.5, -200) * mm, "end": v(-183, -200) * mm});
            skLineSegment(sketch, "E759.left", {"start": v(-182.5, 0) * mm, "end": v(-182.5, -200) * mm});
            skLineSegment(sketch, "E759.right", {"start": v(-183, 0) * mm, "end": v(-183, -200) * mm});
            skLineSegment(sketch, "E760.bottom", {"start": v(-182.5, 0) * mm, "end": v(-182, 0) * mm});
            skLineSegment(sketch, "E760.top", {"start": v(-182.5, -200) * mm, "end": v(-182, -200) * mm});
            skLineSegment(sketch, "E760.right", {"start": v(-182, 0) * mm, "end": v(-182, -200) * mm});
            skLineSegment(sketch, "E761.bottom", {"start": v(-172.5, 0) * mm, "end": v(-173, 0) * mm});
            skLineSegment(sketch, "E761.top", {"start": v(-172.5, -200) * mm, "end": v(-173, -200) * mm});
            skLineSegment(sketch, "E761.left", {"start": v(-172.5, 0) * mm, "end": v(-172.5, -200) * mm});
            skLineSegment(sketch, "E761.right", {"start": v(-173, 0) * mm, "end": v(-173, -200) * mm});
            skLineSegment(sketch, "E762.bottom", {"start": v(-172.5, 0) * mm, "end": v(-172, 0) * mm});
            skLineSegment(sketch, "E762.top", {"start": v(-172.5, -200) * mm, "end": v(-172, -200) * mm});
            skLineSegment(sketch, "E762.right", {"start": v(-172, 0) * mm, "end": v(-172, -200) * mm});
            skLineSegment(sketch, "E763.bottom", {"start": v(-136.88, 0) * mm, "end": v(-137.38, 0) * mm});
            skLineSegment(sketch, "E763.top", {"start": v(-136.87, -200) * mm, "end": v(-137.37, -200) * mm});
            skLineSegment(sketch, "E763.left", {"start": v(-136.88, 0) * mm, "end": v(-136.88, -200) * mm});
            skLineSegment(sketch, "E763.right", {"start": v(-137.38, 0) * mm, "end": v(-137.37, -200) * mm});
            skLineSegment(sketch, "E764.bottom", {"start": v(-136.88, 0) * mm, "end": v(-136.38, 0) * mm});
            skLineSegment(sketch, "E764.top", {"start": v(-136.88, -200) * mm, "end": v(-136.38, -200) * mm});
            skLineSegment(sketch, "E764.right", {"start": v(-136.38, 0) * mm, "end": v(-136.38, -200) * mm});
            skLineSegment(sketch, "E765.bottom", {"start": v(-91.25, 0) * mm, "end": v(-91.75, 0) * mm});
            skLineSegment(sketch, "E765.top", {"start": v(-91.25, -200) * mm, "end": v(-91.75, -200) * mm});
            skLineSegment(sketch, "E765.left", {"start": v(-91.25, 0) * mm, "end": v(-91.25, -200) * mm});
            skLineSegment(sketch, "E765.right", {"start": v(-91.75, 0) * mm, "end": v(-91.75, -200) * mm});
            skLineSegment(sketch, "E766.bottom", {"start": v(-91.25, 0) * mm, "end": v(-90.75, 0) * mm});
            skLineSegment(sketch, "E766.top", {"start": v(-91.25, -200) * mm, "end": v(-90.75, -200) * mm});
            skLineSegment(sketch, "E766.right", {"start": v(-90.75, 0) * mm, "end": v(-90.75, -200) * mm});
            skLineSegment(sketch, "E767.bottom", {"start": v(-45.62, 0) * mm, "end": v(-46.12, 0) * mm});
            skLineSegment(sketch, "E767.top", {"start": v(-45.62, -200) * mm, "end": v(-46.12, -200) * mm});
            skLineSegment(sketch, "E767.left", {"start": v(-45.62, 0) * mm, "end": v(-45.62, -200) * mm});
            skLineSegment(sketch, "E767.right", {"start": v(-46.12, 0) * mm, "end": v(-46.12, -200) * mm});
            skLineSegment(sketch, "E768.bottom", {"start": v(-45.62, 0) * mm, "end": v(-45.12, 0) * mm});
            skLineSegment(sketch, "E768.top", {"start": v(-45.62, -200) * mm, "end": v(-45.12, -200) * mm});
            skLineSegment(sketch, "E768.right", {"start": v(-45.12, 0) * mm, "end": v(-45.12, -200) * mm});
            skLineSegment(sketch, "E769.bottom", {"start": v(0, 0) * mm, "end": v(-0.5, 0) * mm});
            skLineSegment(sketch, "E769.top", {"start": v(0, -200) * mm, "end": v(-0.5, -200) * mm});
            skLineSegment(sketch, "E769.right", {"start": v(-0.5, 0) * mm, "end": v(-0.5, -200) * mm});
            skLineSegment(sketch, "E770.bottom", {"start": v(-10, 0) * mm, "end": v(-9.5, 0) * mm});
            skLineSegment(sketch, "E770.top", {"start": v(-10, -200) * mm, "end": v(-9.5, -200) * mm});
            skLineSegment(sketch, "E770.left", {"start": v(-10, 0) * mm, "end": v(-10, -200) * mm});
            skLineSegment(sketch, "E770.right", {"start": v(-9.5, 0) * mm, "end": v(-9.5, -200) * mm});
            skLineSegment(sketch, "E771.bottom", {"start": v(-10, 0) * mm, "end": v(-10.5, 0) * mm});
            skLineSegment(sketch, "E771.top", {"start": v(-10, -200) * mm, "end": v(-10.5, -200) * mm});
            skLineSegment(sketch, "E771.right", {"start": v(-10.5, 0) * mm, "end": v(-10.5, -200) * mm});
            skLineSegment(sketch, "E772.MirrorCS", {"start": v(365, 0) * mm, "end": v(0, 0) * mm});
            skLineSegment(sketch, "E773.MirrorCS", {"start": v(365, -0.5) * mm, "end": v(0, -0.5) * mm});
            skLineSegment(sketch, "E774.MirrorCS", {"start": v(365, -19.5) * mm, "end": v(0, -19.5) * mm});
            skLineSegment(sketch, "E775.MirrorCS", {"start": v(365, -20) * mm, "end": v(0, -20) * mm});
            skLineSegment(sketch, "E776.MirrorCS", {"start": v(365, -20.5) * mm, "end": v(0, -20.5) * mm});
            skLineSegment(sketch, "E777.MirrorCS", {"start": v(0.5, 0) * mm, "end": v(0.5, -200) * mm});
            skLineSegment(sketch, "E778.MirrorCS", {"start": v(365, -39.5) * mm, "end": v(0, -39.5) * mm});
            skLineSegment(sketch, "E779.MirrorCS", {"start": v(365, -40) * mm, "end": v(0, -40) * mm});
            skLineSegment(sketch, "E780.MirrorCS", {"start": v(365, -40.5) * mm, "end": v(0, -40.5) * mm});
            skLineSegment(sketch, "E781.MirrorCS", {"start": v(365, -49.5) * mm, "end": v(0, -49.5) * mm});
            skLineSegment(sketch, "E782.MirrorCS", {"start": v(0, -50) * mm, "end": v(182.5, -50) * mm});
            skLineSegment(sketch, "E783.MirrorCS", {"start": v(365, -50.5) * mm, "end": v(0, -50.5) * mm});
            skLineSegment(sketch, "E784.MirrorCS", {"start": v(365, -59.5) * mm, "end": v(0, -59.5) * mm});
            skLineSegment(sketch, "E785.MirrorCS", {"start": v(365, -60) * mm, "end": v(0, -60) * mm});
            skLineSegment(sketch, "E786.MirrorCS", {"start": v(365, -60.5) * mm, "end": v(0, -60.5) * mm});
            skLineSegment(sketch, "E787.MirrorCS", {"start": v(365, -87) * mm, "end": v(0, -87) * mm});
            skLineSegment(sketch, "E788.MirrorCS", {"start": v(365, -87.5) * mm, "end": v(0, -87.5) * mm});
            skLineSegment(sketch, "E789.MirrorCS", {"start": v(365, -88) * mm, "end": v(0, -88) * mm});
            skLineSegment(sketch, "E790.MirrorCS", {"start": v(365, -124.5) * mm, "end": v(0, -124.5) * mm});
            skLineSegment(sketch, "E791.MirrorCS", {"start": v(365, -125) * mm, "end": v(0, -125) * mm});
            skLineSegment(sketch, "E792.MirrorCS", {"start": v(365, -125.5) * mm, "end": v(0, -125.5) * mm});
            skLineSegment(sketch, "E793.MirrorCS", {"start": v(365, -162) * mm, "end": v(0, -162) * mm});
            skLineSegment(sketch, "E794.MirrorCS", {"start": v(365, -162.5) * mm, "end": v(0, -162.5) * mm});
            skLineSegment(sketch, "E795.MirrorCS", {"start": v(365, -163) * mm, "end": v(0, -163) * mm});
            skLineSegment(sketch, "E796.MirrorCS", {"start": v(9.5, 0) * mm, "end": v(9.5, -200) * mm});
            skLineSegment(sketch, "E797.MirrorCS", {"start": v(10, 0) * mm, "end": v(10, -200) * mm});
            skLineSegment(sketch, "E798.MirrorCS", {"start": v(10.5, 0) * mm, "end": v(10.5, -200) * mm});
            skLineSegment(sketch, "E799.MirrorCS", {"start": v(45.12, 0) * mm, "end": v(45.12, -200) * mm});
            skLineSegment(sketch, "E800.MirrorCS", {"start": v(45.62, 0) * mm, "end": v(45.62, -200) * mm});
            skLineSegment(sketch, "E801.MirrorCS", {"start": v(46.12, 0) * mm, "end": v(46.12, -200) * mm});
            skLineSegment(sketch, "E802.MirrorCS", {"start": v(90.75, 0) * mm, "end": v(90.75, -200) * mm});
            skLineSegment(sketch, "E803.MirrorCS", {"start": v(91.25, 0) * mm, "end": v(91.25, -200) * mm});
            skLineSegment(sketch, "E804.MirrorCS", {"start": v(91.75, 0) * mm, "end": v(91.75, -200) * mm});
            skLineSegment(sketch, "E805.MirrorCS", {"start": v(136.38, 0) * mm, "end": v(136.38, -200) * mm});
            skLineSegment(sketch, "E806.MirrorCS", {"start": v(136.88, 0) * mm, "end": v(136.88, -200) * mm});
            skLineSegment(sketch, "E807.MirrorCS", {"start": v(137.38, 0) * mm, "end": v(137.37, -200) * mm});
            skLineSegment(sketch, "E808.MirrorCS", {"start": v(172, 0) * mm, "end": v(172, -200) * mm});
            skLineSegment(sketch, "E809.MirrorCS", {"start": v(172.5, 0) * mm, "end": v(172.5, -200) * mm});
            skLineSegment(sketch, "E810.MirrorCS", {"start": v(173, 0) * mm, "end": v(173, -200) * mm});
            skLineSegment(sketch, "E811.MirrorCS", {"start": v(182, 0) * mm, "end": v(182, -200) * mm});
            skLineSegment(sketch, "E812.MirrorCS", {"start": v(183, 0) * mm, "end": v(183, -200) * mm});
            skLineSegment(sketch, "E813.MirrorCS", {"start": v(192, 0) * mm, "end": v(192, -200) * mm});
            skLineSegment(sketch, "E814.MirrorCS", {"start": v(192.5, 0) * mm, "end": v(192.5, -200) * mm});
            skLineSegment(sketch, "E815.MirrorCS", {"start": v(193, 0) * mm, "end": v(193, -200) * mm});
            skLineSegment(sketch, "E816.MirrorCS", {"start": v(319.87, 0) * mm, "end": v(319.87, -200) * mm});
            skLineSegment(sketch, "E817.MirrorCS", {"start": v(319.37, 0) * mm, "end": v(319.37, -200) * mm});
            skLineSegment(sketch, "E818.MirrorCS", {"start": v(318.87, 0) * mm, "end": v(318.87, -200) * mm});
            skLineSegment(sketch, "E819.MirrorCS", {"start": v(274.25, 0) * mm, "end": v(274.25, -200) * mm});
            skLineSegment(sketch, "E820.MirrorCS", {"start": v(273.75, 0) * mm, "end": v(273.75, -200) * mm});
            skLineSegment(sketch, "E821.MirrorCS", {"start": v(273.25, 0) * mm, "end": v(273.25, -200) * mm});
            skLineSegment(sketch, "E822.MirrorCS", {"start": v(228.62, 0) * mm, "end": v(228.62, -200) * mm});
            skLineSegment(sketch, "E823.MirrorCS", {"start": v(228.12, 0) * mm, "end": v(228.12, -200) * mm});
            skLineSegment(sketch, "E824.MirrorCS", {"start": v(227.62, 0) * mm, "end": v(227.62, -200) * mm});
            skLineSegment(sketch, "E825.MirrorCS", {"start": v(-365, 0.5) * mm, "end": v(0, 0.5) * mm});
            skLineSegment(sketch, "E826.MirrorCS", {"start": v(365, 0.5) * mm, "end": v(0, 0.5) * mm});
            skLineSegment(sketch, "E827.MirrorCS", {"start": v(-365, 39.5) * mm, "end": v(0, 39.5) * mm});
            skLineSegment(sketch, "E828.MirrorCS", {"start": v(-365, 40.5) * mm, "end": v(0, 40.5) * mm});
            skLineSegment(sketch, "E829.MirrorCS", {"start": v(-365, 49.5) * mm, "end": v(0, 49.5) * mm});
            skLineSegment(sketch, "E830.MirrorCS", {"start": v(-365, 50.5) * mm, "end": v(0, 50.5) * mm});
            skLineSegment(sketch, "E831.MirrorCS", {"start": v(-365, 59.5) * mm, "end": v(0, 59.5) * mm});
            skLineSegment(sketch, "E832.MirrorCS", {"start": v(-365, 60.5) * mm, "end": v(0, 60.5) * mm});
            skLineSegment(sketch, "E833.MirrorCS", {"start": v(-365, 19.5) * mm, "end": v(0, 19.5) * mm});
            skLineSegment(sketch, "E834.MirrorCS", {"start": v(-365, 20.5) * mm, "end": v(0, 20.5) * mm});
            skLineSegment(sketch, "E835.MirrorCS", {"start": v(-319.87, 0) * mm, "end": v(-319.87, 200) * mm});
            skLineSegment(sketch, "E836.MirrorCS", {"start": v(-318.87, 0) * mm, "end": v(-318.87, 200) * mm});
            skLineSegment(sketch, "E837.MirrorCS", {"start": v(-274.25, 0) * mm, "end": v(-274.25, 200) * mm});
            skLineSegment(sketch, "E838.MirrorCS", {"start": v(-273.25, 0) * mm, "end": v(-273.25, 200) * mm});
            skLineSegment(sketch, "E839.MirrorCS", {"start": v(-228.62, 0) * mm, "end": v(-228.62, 200) * mm});
            skLineSegment(sketch, "E840.MirrorCS", {"start": v(-227.62, 0) * mm, "end": v(-227.62, 200) * mm});
            skLineSegment(sketch, "E841.MirrorCS", {"start": v(-193, 0) * mm, "end": v(-193, 200) * mm});
            skLineSegment(sketch, "E842.MirrorCS", {"start": v(-192, 0) * mm, "end": v(-192, 200) * mm});
            skLineSegment(sketch, "E843.MirrorCS", {"start": v(-183, 0) * mm, "end": v(-183, 200) * mm});
            skLineSegment(sketch, "E844.MirrorCS", {"start": v(-182, 0) * mm, "end": v(-182, 200) * mm});
            skLineSegment(sketch, "E845.MirrorCS", {"start": v(-173, 0) * mm, "end": v(-173, 200) * mm});
            skLineSegment(sketch, "E846.MirrorCS", {"start": v(-172, 0) * mm, "end": v(-172, 200) * mm});
            skLineSegment(sketch, "E847.MirrorCS", {"start": v(-137.38, 0) * mm, "end": v(-137.37, 200) * mm});
            skLineSegment(sketch, "E848.MirrorCS", {"start": v(-136.38, 0) * mm, "end": v(-136.38, 200) * mm});
            skLineSegment(sketch, "E849.MirrorCS", {"start": v(-91.75, 0) * mm, "end": v(-91.75, 200) * mm});
            skLineSegment(sketch, "E850.MirrorCS", {"start": v(-90.75, 0) * mm, "end": v(-90.75, 200) * mm});
            skLineSegment(sketch, "E851.MirrorCS", {"start": v(-46.12, 0) * mm, "end": v(-46.12, 200) * mm});
            skLineSegment(sketch, "E852.MirrorCS", {"start": v(-45.12, 0) * mm, "end": v(-45.12, 200) * mm});
            skLineSegment(sketch, "E853.MirrorCS", {"start": v(-10.5, 0) * mm, "end": v(-10.5, 200) * mm});
            skLineSegment(sketch, "E854.MirrorCS", {"start": v(-9.5, 0) * mm, "end": v(-9.5, 200) * mm});
            skLineSegment(sketch, "E855.MirrorCS", {"start": v(-0.5, 0) * mm, "end": v(-0.5, 200) * mm});
            skLineSegment(sketch, "E856.MirrorCS", {"start": v(0.5, 0) * mm, "end": v(0.5, 200) * mm});
            skLineSegment(sketch, "E857.MirrorCS", {"start": v(9.5, 0) * mm, "end": v(9.5, 200) * mm});
            skLineSegment(sketch, "E858.MirrorCS", {"start": v(10.5, 0) * mm, "end": v(10.5, 200) * mm});
            skLineSegment(sketch, "E859.MirrorCS", {"start": v(365, 19.5) * mm, "end": v(0, 19.5) * mm});
            skLineSegment(sketch, "E860.MirrorCS", {"start": v(365, 20.5) * mm, "end": v(0, 20.5) * mm});
            skLineSegment(sketch, "E861.MirrorCS", {"start": v(365, 39.5) * mm, "end": v(0, 39.5) * mm});
            skLineSegment(sketch, "E862.MirrorCS", {"start": v(365, 40.5) * mm, "end": v(0, 40.5) * mm});
            skLineSegment(sketch, "E863.MirrorCS", {"start": v(365, 49.5) * mm, "end": v(0, 49.5) * mm});
            skLineSegment(sketch, "E864.MirrorCS", {"start": v(365, 50.5) * mm, "end": v(0, 50.5) * mm});
            skLineSegment(sketch, "E865.MirrorCS", {"start": v(365, 59.5) * mm, "end": v(0, 59.5) * mm});
            skLineSegment(sketch, "E866.MirrorCS", {"start": v(365, 60.5) * mm, "end": v(0, 60.5) * mm});
            skSolve(sketch);
        }
        {
            var Q0;
            {var subQ0=sQuery(id+"F36.wireOp",EDGE,"E757.right");var subQ1=sQuery(id+"F36.wireOp",EDGE,"E747.bottom");var subQ2=makeQuery(id+"F36.imprint","INTERSECT",VERTEX,{"derivedFrom":[subQ1,subQ0]});Q0=makeQuery(id+"F36.imprint","IMPRINT",FACE,{"disambiguationData":[TD([[makeQuery(id+"F36.imprint","IMPRINT",EDGE,{"disambiguationData":[TD([[subQ2,-1.0]])],"derivedFrom":subQ1}),-1.0]])]});}
            var Q1;
            {var subQ0=sQuery(id+"F36.wireOp",EDGE,"E757.left");var subQ1=sQuery(id+"F36.wireOp",EDGE,"E747.bottom");var subQ2=makeQuery(id+"F36.imprint","INTERSECT",VERTEX,{"derivedFrom":[subQ1,subQ0]});Q1=makeQuery(id+"F36.imprint","IMPRINT",FACE,{"disambiguationData":[TD([[makeQuery(id+"F36.imprint","IMPRINT",EDGE,{"disambiguationData":[TD([[subQ2,-1.0]])],"derivedFrom":subQ1}),-1.0]])]});}
            var Q2;
            {var subQ0=sQuery(id+"F36.wireOp",EDGE,"E758.right");var subQ1=sQuery(id+"F36.wireOp",EDGE,"E747.bottom");var subQ2=makeQuery(id+"F36.imprint","INTERSECT",VERTEX,{"derivedFrom":[subQ1,subQ0]});Q2=makeQuery(id+"F36.imprint","IMPRINT",FACE,{"disambiguationData":[TD([[makeQuery(id+"F36.imprint","IMPRINT",EDGE,{"disambiguationData":[TD([[subQ2,-1.0]])],"derivedFrom":subQ1}),-1.0]])]});}
            var Q3;
            {var subQ0=sQuery(id+"F36.wireOp",EDGE,"E759.right");var subQ1=sQuery(id+"F36.wireOp",EDGE,"E747.bottom");var subQ2=makeQuery(id+"F36.imprint","INTERSECT",VERTEX,{"derivedFrom":[subQ1,subQ0]});Q3=makeQuery(id+"F36.imprint","IMPRINT",FACE,{"disambiguationData":[TD([[makeQuery(id+"F36.imprint","IMPRINT",EDGE,{"disambiguationData":[TD([[subQ2,-1.0]])],"derivedFrom":subQ1}),-1.0]])]});}
            var Q4;
            {var subQ0=sQuery(id+"F36.wireOp",EDGE,"E757.right");var subQ1=sQuery(id+"F36.wireOp",EDGE,"E748.top");var subQ2=makeQuery(id+"F36.imprint","INTERSECT",VERTEX,{"derivedFrom":[subQ1,subQ0]});Q4=makeQuery(id+"F36.imprint","IMPRINT",FACE,{"disambiguationData":[TD([[makeQuery(id+"F36.imprint","IMPRINT",EDGE,{"disambiguationData":[TD([[subQ2,-1.0]])],"derivedFrom":subQ1}),-1.0]])]});}
            var Q5;
            {var subQ0=sQuery(id+"F36.wireOp",EDGE,"E757.left");var subQ1=sQuery(id+"F36.wireOp",EDGE,"E748.top");var subQ2=makeQuery(id+"F36.imprint","INTERSECT",VERTEX,{"derivedFrom":[subQ1,subQ0]});Q5=makeQuery(id+"F36.imprint","IMPRINT",FACE,{"disambiguationData":[TD([[makeQuery(id+"F36.imprint","IMPRINT",EDGE,{"disambiguationData":[TD([[subQ2,-1.0]])],"derivedFrom":subQ1}),-1.0]])]});}
            var Q6;
            {var subQ0=sQuery(id+"F36.wireOp",EDGE,"E757.right");var subQ1=sQuery(id+"F36.wireOp",EDGE,"E749.top");var subQ2=makeQuery(id+"F36.imprint","INTERSECT",VERTEX,{"derivedFrom":[subQ1,subQ0]});Q6=makeQuery(id+"F36.imprint","IMPRINT",FACE,{"disambiguationData":[TD([[makeQuery(id+"F36.imprint","IMPRINT",EDGE,{"disambiguationData":[TD([[subQ2,-1.0]])],"derivedFrom":subQ1}),-1.0]])]});}
            var Q7;
            {var subQ0=sQuery(id+"F36.wireOp",EDGE,"E757.left");var subQ1=sQuery(id+"F36.wireOp",EDGE,"E749.top");var subQ2=makeQuery(id+"F36.imprint","INTERSECT",VERTEX,{"derivedFrom":[subQ1,subQ0]});Q7=makeQuery(id+"F36.imprint","IMPRINT",FACE,{"disambiguationData":[TD([[makeQuery(id+"F36.imprint","IMPRINT",EDGE,{"disambiguationData":[TD([[subQ2,-1.0]])],"derivedFrom":subQ1}),-1.0]])]});}
            var Q8;
            {var subQ0=sQuery(id+"F36.wireOp",EDGE,"E758.right");var subQ1=sQuery(id+"F36.wireOp",EDGE,"E749.top");var subQ2=makeQuery(id+"F36.imprint","INTERSECT",VERTEX,{"derivedFrom":[subQ1,subQ0]});Q8=makeQuery(id+"F36.imprint","IMPRINT",FACE,{"disambiguationData":[TD([[makeQuery(id+"F36.imprint","IMPRINT",EDGE,{"disambiguationData":[TD([[subQ2,-1.0]])],"derivedFrom":subQ1}),-1.0]])]});}
            var Q9;
            {var subQ0=sQuery(id+"F36.wireOp",EDGE,"E759.right");var subQ1=sQuery(id+"F36.wireOp",EDGE,"E749.top");var subQ2=makeQuery(id+"F36.imprint","INTERSECT",VERTEX,{"derivedFrom":[subQ1,subQ0]});Q9=makeQuery(id+"F36.imprint","IMPRINT",FACE,{"disambiguationData":[TD([[makeQuery(id+"F36.imprint","IMPRINT",EDGE,{"disambiguationData":[TD([[subQ2,-1.0]])],"derivedFrom":subQ1}),-1.0]])]});}
            var Q10;
            {var subQ0=sQuery(id+"F36.wireOp",EDGE,"E759.left");var subQ1=sQuery(id+"F36.wireOp",EDGE,"E749.top");var subQ2=makeQuery(id+"F36.imprint","INTERSECT",VERTEX,{"derivedFrom":[subQ1,subQ0]});Q10=makeQuery(id+"F36.imprint","IMPRINT",FACE,{"disambiguationData":[TD([[makeQuery(id+"F36.imprint","IMPRINT",EDGE,{"disambiguationData":[TD([[subQ2,-1.0]])],"derivedFrom":subQ1}),-1.0]])]});}
            var Q11;
            {var subQ0=sQuery(id+"F36.wireOp",EDGE,"E760.right");var subQ1=sQuery(id+"F36.wireOp",EDGE,"E747.bottom");var subQ2=makeQuery(id+"F36.imprint","INTERSECT",VERTEX,{"derivedFrom":[subQ1,subQ0]});Q11=makeQuery(id+"F36.imprint","IMPRINT",FACE,{"disambiguationData":[TD([[makeQuery(id+"F36.imprint","IMPRINT",EDGE,{"disambiguationData":[TD([[subQ2,-1.0]])],"derivedFrom":subQ1}),-1.0]])]});}
            var Q12;
            {var subQ0=sQuery(id+"F36.wireOp",EDGE,"E759.left");var subQ1=sQuery(id+"F36.wireOp",EDGE,"E747.bottom");var subQ2=makeQuery(id+"F36.imprint","INTERSECT",VERTEX,{"derivedFrom":[subQ1,subQ0]});Q12=makeQuery(id+"F36.imprint","IMPRINT",FACE,{"disambiguationData":[TD([[makeQuery(id+"F36.imprint","IMPRINT",EDGE,{"disambiguationData":[TD([[subQ2,-1.0]])],"derivedFrom":subQ1}),-1.0]])]});}
            var Q13;
            {var subQ0=sQuery(id+"F36.wireOp",EDGE,"E753.left");var subQ1=sQuery(id+"F36.wireOp",EDGE,"E740.top");var subQ2=makeQuery(id+"F36.imprint","INTERSECT",VERTEX,{"derivedFrom":[subQ1,subQ0]});Q13=makeQuery(id+"F36.imprint","IMPRINT",FACE,{"disambiguationData":[TD([[makeQuery(id+"F36.imprint","IMPRINT",EDGE,{"disambiguationData":[TD([[subQ2,-1.0]])],"derivedFrom":subQ1}),-1.0]])]});}
            var Q14;
            {var subQ0=sQuery(id+"F36.wireOp",EDGE,"E754.right");var subQ1=sQuery(id+"F36.wireOp",EDGE,"E740.top");var subQ2=makeQuery(id+"F36.imprint","INTERSECT",VERTEX,{"derivedFrom":[subQ1,subQ0]});Q14=makeQuery(id+"F36.imprint","IMPRINT",FACE,{"disambiguationData":[TD([[makeQuery(id+"F36.imprint","IMPRINT",EDGE,{"disambiguationData":[TD([[subQ2,-1.0]])],"derivedFrom":subQ1}),-1.0]])]});}
            var Q15;
            {var subQ0=sQuery(id+"F36.wireOp",EDGE,"E753.left");var subQ1=sQuery(id+"F36.wireOp",EDGE,"E741.top");var subQ2=makeQuery(id+"F36.imprint","INTERSECT",VERTEX,{"derivedFrom":[subQ1,subQ0]});Q15=makeQuery(id+"F36.imprint","IMPRINT",FACE,{"disambiguationData":[TD([[makeQuery(id+"F36.imprint","IMPRINT",EDGE,{"disambiguationData":[TD([[subQ2,-1.0]])],"derivedFrom":subQ1}),-1.0]])]});}
            var Q16;
            {var subQ0=sQuery(id+"F36.wireOp",EDGE,"E753.left");var subQ1=sQuery(id+"F36.wireOp",EDGE,"E741.bottom");var subQ2=makeQuery(id+"F36.imprint","INTERSECT",VERTEX,{"derivedFrom":[subQ1,subQ0]});Q16=makeQuery(id+"F36.imprint","IMPRINT",FACE,{"disambiguationData":[TD([[makeQuery(id+"F36.imprint","IMPRINT",EDGE,{"disambiguationData":[TD([[subQ2,-1.0]])],"derivedFrom":subQ1}),-1.0]])]});}
            var Q17;
            {var subQ0=sQuery(id+"F36.wireOp",EDGE,"E754.right");var subQ1=sQuery(id+"F36.wireOp",EDGE,"E741.top");var subQ2=makeQuery(id+"F36.imprint","INTERSECT",VERTEX,{"derivedFrom":[subQ1,subQ0]});Q17=makeQuery(id+"F36.imprint","IMPRINT",FACE,{"disambiguationData":[TD([[makeQuery(id+"F36.imprint","IMPRINT",EDGE,{"disambiguationData":[TD([[subQ2,-1.0]])],"derivedFrom":subQ1}),-1.0]])]});}
            var Q18;
            {var subQ0=sQuery(id+"F36.wireOp",EDGE,"E754.right");var subQ1=sQuery(id+"F36.wireOp",EDGE,"E741.bottom");var subQ2=makeQuery(id+"F36.imprint","INTERSECT",VERTEX,{"derivedFrom":[subQ1,subQ0]});Q18=makeQuery(id+"F36.imprint","IMPRINT",FACE,{"disambiguationData":[TD([[makeQuery(id+"F36.imprint","IMPRINT",EDGE,{"disambiguationData":[TD([[subQ2,-1.0]])],"derivedFrom":subQ1}),-1.0]])]});}
            var Q19;
            {var subQ0=sQuery(id+"F36.wireOp",EDGE,"E753.left");var subQ1=sQuery(id+"F36.wireOp",EDGE,"E742.top");var subQ2=makeQuery(id+"F36.imprint","INTERSECT",VERTEX,{"derivedFrom":[subQ1,subQ0]});Q19=makeQuery(id+"F36.imprint","IMPRINT",FACE,{"disambiguationData":[TD([[makeQuery(id+"F36.imprint","IMPRINT",EDGE,{"disambiguationData":[TD([[subQ2,-1.0]])],"derivedFrom":subQ1}),-1.0]])]});}
            var Q20;
            {var subQ0=sQuery(id+"F36.wireOp",EDGE,"E754.right");var subQ1=sQuery(id+"F36.wireOp",EDGE,"E742.top");var subQ2=makeQuery(id+"F36.imprint","INTERSECT",VERTEX,{"derivedFrom":[subQ1,subQ0]});Q20=makeQuery(id+"F36.imprint","IMPRINT",FACE,{"disambiguationData":[TD([[makeQuery(id+"F36.imprint","IMPRINT",EDGE,{"disambiguationData":[TD([[subQ2,-1.0]])],"derivedFrom":subQ1}),-1.0]])]});}
            var Q21;
            {var subQ0=sQuery(id+"F36.wireOp",EDGE,"E753.left");var subQ1=sQuery(id+"F36.wireOp",EDGE,"E743.top");var subQ2=makeQuery(id+"F36.imprint","INTERSECT",VERTEX,{"derivedFrom":[subQ1,subQ0]});Q21=makeQuery(id+"F36.imprint","IMPRINT",FACE,{"disambiguationData":[TD([[makeQuery(id+"F36.imprint","IMPRINT",EDGE,{"disambiguationData":[TD([[subQ2,-1.0]])],"derivedFrom":subQ1}),-1.0]])]});}
            var Q22;
            {var subQ0=sQuery(id+"F36.wireOp",EDGE,"E753.left");var subQ1=sQuery(id+"F36.wireOp",EDGE,"E743.bottom");var subQ2=makeQuery(id+"F36.imprint","INTERSECT",VERTEX,{"derivedFrom":[subQ1,subQ0]});Q22=makeQuery(id+"F36.imprint","IMPRINT",FACE,{"disambiguationData":[TD([[makeQuery(id+"F36.imprint","IMPRINT",EDGE,{"disambiguationData":[TD([[subQ2,-1.0]])],"derivedFrom":subQ1}),-1.0]])]});}
            var Q23;
            {var subQ0=sQuery(id+"F36.wireOp",EDGE,"E754.right");var subQ1=sQuery(id+"F36.wireOp",EDGE,"E743.top");var subQ2=makeQuery(id+"F36.imprint","INTERSECT",VERTEX,{"derivedFrom":[subQ1,subQ0]});Q23=makeQuery(id+"F36.imprint","IMPRINT",FACE,{"disambiguationData":[TD([[makeQuery(id+"F36.imprint","IMPRINT",EDGE,{"disambiguationData":[TD([[subQ2,-1.0]])],"derivedFrom":subQ1}),-1.0]])]});}
            var Q24;
            {var subQ0=sQuery(id+"F36.wireOp",EDGE,"E754.right");var subQ1=sQuery(id+"F36.wireOp",EDGE,"E743.bottom");var subQ2=makeQuery(id+"F36.imprint","INTERSECT",VERTEX,{"derivedFrom":[subQ1,subQ0]});Q24=makeQuery(id+"F36.imprint","IMPRINT",FACE,{"disambiguationData":[TD([[makeQuery(id+"F36.imprint","IMPRINT",EDGE,{"disambiguationData":[TD([[subQ2,-1.0]])],"derivedFrom":subQ1}),-1.0]])]});}
            var Q25;
            {var subQ0=sQuery(id+"F36.wireOp",EDGE,"E755.right");var subQ1=sQuery(id+"F36.wireOp",EDGE,"E740.top");var subQ2=makeQuery(id+"F36.imprint","INTERSECT",VERTEX,{"derivedFrom":[subQ1,subQ0]});Q25=makeQuery(id+"F36.imprint","IMPRINT",FACE,{"disambiguationData":[TD([[makeQuery(id+"F36.imprint","IMPRINT",EDGE,{"disambiguationData":[TD([[subQ2,-1.0]])],"derivedFrom":subQ1}),-1.0]])]});}
            var Q26;
            {var subQ0=sQuery(id+"F36.wireOp",EDGE,"E755.right");var subQ1=sQuery(id+"F36.wireOp",EDGE,"E741.top");var subQ2=makeQuery(id+"F36.imprint","INTERSECT",VERTEX,{"derivedFrom":[subQ1,subQ0]});Q26=makeQuery(id+"F36.imprint","IMPRINT",FACE,{"disambiguationData":[TD([[makeQuery(id+"F36.imprint","IMPRINT",EDGE,{"disambiguationData":[TD([[subQ2,-1.0]])],"derivedFrom":subQ1}),-1.0]])]});}
            var Q27;
            {var subQ0=sQuery(id+"F36.wireOp",EDGE,"E755.right");var subQ1=sQuery(id+"F36.wireOp",EDGE,"E741.bottom");var subQ2=makeQuery(id+"F36.imprint","INTERSECT",VERTEX,{"derivedFrom":[subQ1,subQ0]});Q27=makeQuery(id+"F36.imprint","IMPRINT",FACE,{"disambiguationData":[TD([[makeQuery(id+"F36.imprint","IMPRINT",EDGE,{"disambiguationData":[TD([[subQ2,-1.0]])],"derivedFrom":subQ1}),-1.0]])]});}
            var Q28;
            {var subQ0=sQuery(id+"F36.wireOp",EDGE,"E755.right");var subQ1=sQuery(id+"F36.wireOp",EDGE,"E742.top");var subQ2=makeQuery(id+"F36.imprint","INTERSECT",VERTEX,{"derivedFrom":[subQ1,subQ0]});Q28=makeQuery(id+"F36.imprint","IMPRINT",FACE,{"disambiguationData":[TD([[makeQuery(id+"F36.imprint","IMPRINT",EDGE,{"disambiguationData":[TD([[subQ2,-1.0]])],"derivedFrom":subQ1}),-1.0]])]});}
            var Q29;
            {var subQ0=sQuery(id+"F36.wireOp",EDGE,"E755.right");var subQ1=sQuery(id+"F36.wireOp",EDGE,"E743.top");var subQ2=makeQuery(id+"F36.imprint","INTERSECT",VERTEX,{"derivedFrom":[subQ1,subQ0]});Q29=makeQuery(id+"F36.imprint","IMPRINT",FACE,{"disambiguationData":[TD([[makeQuery(id+"F36.imprint","IMPRINT",EDGE,{"disambiguationData":[TD([[subQ2,-1.0]])],"derivedFrom":subQ1}),-1.0]])]});}
            var Q30;
            {var subQ0=sQuery(id+"F36.wireOp",EDGE,"E755.right");var subQ1=sQuery(id+"F36.wireOp",EDGE,"E743.bottom");var subQ2=makeQuery(id+"F36.imprint","INTERSECT",VERTEX,{"derivedFrom":[subQ1,subQ0]});Q30=makeQuery(id+"F36.imprint","IMPRINT",FACE,{"disambiguationData":[TD([[makeQuery(id+"F36.imprint","IMPRINT",EDGE,{"disambiguationData":[TD([[subQ2,-1.0]])],"derivedFrom":subQ1}),-1.0]])]});}
            var Q31;
            {var subQ0=sQuery(id+"F36.wireOp",EDGE,"E753.right");var subQ1=sQuery(id+"F36.wireOp",EDGE,"E740.top");var subQ2=makeQuery(id+"F36.imprint","INTERSECT",VERTEX,{"derivedFrom":[subQ1,subQ0]});Q31=makeQuery(id+"F36.imprint","IMPRINT",FACE,{"disambiguationData":[TD([[makeQuery(id+"F36.imprint","IMPRINT",EDGE,{"disambiguationData":[TD([[subQ2,-1.0]])],"derivedFrom":subQ1}),-1.0]])]});}
            var Q32;
            {var subQ0=sQuery(id+"F36.wireOp",EDGE,"E753.right");var subQ1=sQuery(id+"F36.wireOp",EDGE,"E741.top");var subQ2=makeQuery(id+"F36.imprint","INTERSECT",VERTEX,{"derivedFrom":[subQ1,subQ0]});Q32=makeQuery(id+"F36.imprint","IMPRINT",FACE,{"disambiguationData":[TD([[makeQuery(id+"F36.imprint","IMPRINT",EDGE,{"disambiguationData":[TD([[subQ2,-1.0]])],"derivedFrom":subQ1}),-1.0]])]});}
            var Q33;
            {var subQ0=sQuery(id+"F36.wireOp",EDGE,"E753.right");var subQ1=sQuery(id+"F36.wireOp",EDGE,"E741.bottom");var subQ2=makeQuery(id+"F36.imprint","INTERSECT",VERTEX,{"derivedFrom":[subQ1,subQ0]});Q33=makeQuery(id+"F36.imprint","IMPRINT",FACE,{"disambiguationData":[TD([[makeQuery(id+"F36.imprint","IMPRINT",EDGE,{"disambiguationData":[TD([[subQ2,-1.0]])],"derivedFrom":subQ1}),-1.0]])]});}
            var Q34;
            {var subQ0=sQuery(id+"F36.wireOp",EDGE,"E753.right");var subQ1=sQuery(id+"F36.wireOp",EDGE,"E742.top");var subQ2=makeQuery(id+"F36.imprint","INTERSECT",VERTEX,{"derivedFrom":[subQ1,subQ0]});Q34=makeQuery(id+"F36.imprint","IMPRINT",FACE,{"disambiguationData":[TD([[makeQuery(id+"F36.imprint","IMPRINT",EDGE,{"disambiguationData":[TD([[subQ2,-1.0]])],"derivedFrom":subQ1}),-1.0]])]});}
            var Q35;
            {var subQ0=sQuery(id+"F36.wireOp",EDGE,"E753.right");var subQ1=sQuery(id+"F36.wireOp",EDGE,"E743.top");var subQ2=makeQuery(id+"F36.imprint","INTERSECT",VERTEX,{"derivedFrom":[subQ1,subQ0]});Q35=makeQuery(id+"F36.imprint","IMPRINT",FACE,{"disambiguationData":[TD([[makeQuery(id+"F36.imprint","IMPRINT",EDGE,{"disambiguationData":[TD([[subQ2,-1.0]])],"derivedFrom":subQ1}),-1.0]])]});}
            var Q36;
            {var subQ0=sQuery(id+"F36.wireOp",EDGE,"E753.right");var subQ1=sQuery(id+"F36.wireOp",EDGE,"E743.bottom");var subQ2=makeQuery(id+"F36.imprint","INTERSECT",VERTEX,{"derivedFrom":[subQ1,subQ0]});Q36=makeQuery(id+"F36.imprint","IMPRINT",FACE,{"disambiguationData":[TD([[makeQuery(id+"F36.imprint","IMPRINT",EDGE,{"disambiguationData":[TD([[subQ2,-1.0]])],"derivedFrom":subQ1}),-1.0]])]});}
            var Q37;
            {var subQ0=sQuery(id+"F36.wireOp",EDGE,"E757.right");var subQ1=sQuery(id+"F36.wireOp",EDGE,"E747.top");var subQ2=makeQuery(id+"F36.imprint","INTERSECT",VERTEX,{"derivedFrom":[subQ1,subQ0]});Q37=makeQuery(id+"F36.imprint","IMPRINT",FACE,{"disambiguationData":[TD([[makeQuery(id+"F36.imprint","IMPRINT",EDGE,{"disambiguationData":[TD([[subQ2,-1.0]])],"derivedFrom":subQ1}),-1.0]])]});}
            var Q38;
            {var subQ0=sQuery(id+"F36.wireOp",EDGE,"E757.left");var subQ1=sQuery(id+"F36.wireOp",EDGE,"E747.top");var subQ2=makeQuery(id+"F36.imprint","INTERSECT",VERTEX,{"derivedFrom":[subQ1,subQ0]});Q38=makeQuery(id+"F36.imprint","IMPRINT",FACE,{"disambiguationData":[TD([[makeQuery(id+"F36.imprint","IMPRINT",EDGE,{"disambiguationData":[TD([[subQ2,-1.0]])],"derivedFrom":subQ1}),-1.0]])]});}
            var Q39;
            {var subQ0=sQuery(id+"F36.wireOp",EDGE,"E758.right");var subQ1=sQuery(id+"F36.wireOp",EDGE,"E747.top");var subQ2=makeQuery(id+"F36.imprint","INTERSECT",VERTEX,{"derivedFrom":[subQ1,subQ0]});Q39=makeQuery(id+"F36.imprint","IMPRINT",FACE,{"disambiguationData":[TD([[makeQuery(id+"F36.imprint","IMPRINT",EDGE,{"disambiguationData":[TD([[subQ2,-1.0]])],"derivedFrom":subQ1}),-1.0]])]});}
            var Q40;
            {var subQ0=sQuery(id+"F36.wireOp",EDGE,"E759.right");var subQ1=sQuery(id+"F36.wireOp",EDGE,"E747.top");var subQ2=makeQuery(id+"F36.imprint","INTERSECT",VERTEX,{"derivedFrom":[subQ1,subQ0]});Q40=makeQuery(id+"F36.imprint","IMPRINT",FACE,{"disambiguationData":[TD([[makeQuery(id+"F36.imprint","IMPRINT",EDGE,{"disambiguationData":[TD([[subQ2,-1.0]])],"derivedFrom":subQ1}),-1.0]])]});}
            var Q41;
            {var subQ0=sQuery(id+"F36.wireOp",EDGE,"E759.left");var subQ1=sQuery(id+"F36.wireOp",EDGE,"E747.top");var subQ2=makeQuery(id+"F36.imprint","INTERSECT",VERTEX,{"derivedFrom":[subQ1,subQ0]});Q41=makeQuery(id+"F36.imprint","IMPRINT",FACE,{"disambiguationData":[TD([[makeQuery(id+"F36.imprint","IMPRINT",EDGE,{"disambiguationData":[TD([[subQ2,-1.0]])],"derivedFrom":subQ1}),-1.0]])]});}
            var Q42;
            {var subQ0=sQuery(id+"F36.wireOp",EDGE,"E760.right");var subQ1=sQuery(id+"F36.wireOp",EDGE,"E747.top");var subQ2=makeQuery(id+"F36.imprint","INTERSECT",VERTEX,{"derivedFrom":[subQ1,subQ0]});Q42=makeQuery(id+"F36.imprint","IMPRINT",FACE,{"disambiguationData":[TD([[makeQuery(id+"F36.imprint","IMPRINT",EDGE,{"disambiguationData":[TD([[subQ2,-1.0]])],"derivedFrom":subQ1}),-1.0]])]});}
            var Q43;
            {var subQ0=sQuery(id+"F36.wireOp",EDGE,"E757.right");var subQ1=sQuery(id+"F36.wireOp",EDGE,"E749.bottom");var subQ2=makeQuery(id+"F36.imprint","INTERSECT",VERTEX,{"derivedFrom":[subQ1,subQ0]});Q43=makeQuery(id+"F36.imprint","IMPRINT",FACE,{"disambiguationData":[TD([[makeQuery(id+"F36.imprint","IMPRINT",EDGE,{"disambiguationData":[TD([[subQ2,-1.0]])],"derivedFrom":subQ1}),-1.0]])]});}
            var Q44;
            {var subQ0=sQuery(id+"F36.wireOp",EDGE,"E757.left");var subQ1=sQuery(id+"F36.wireOp",EDGE,"E749.bottom");var subQ2=makeQuery(id+"F36.imprint","INTERSECT",VERTEX,{"derivedFrom":[subQ1,subQ0]});Q44=makeQuery(id+"F36.imprint","IMPRINT",FACE,{"disambiguationData":[TD([[makeQuery(id+"F36.imprint","IMPRINT",EDGE,{"disambiguationData":[TD([[subQ2,-1.0]])],"derivedFrom":subQ1}),-1.0]])]});}
            var Q45;
            {var subQ0=sQuery(id+"F36.wireOp",EDGE,"E758.right");var subQ1=sQuery(id+"F36.wireOp",EDGE,"E749.bottom");var subQ2=makeQuery(id+"F36.imprint","INTERSECT",VERTEX,{"derivedFrom":[subQ1,subQ0]});Q45=makeQuery(id+"F36.imprint","IMPRINT",FACE,{"disambiguationData":[TD([[makeQuery(id+"F36.imprint","IMPRINT",EDGE,{"disambiguationData":[TD([[subQ2,-1.0]])],"derivedFrom":subQ1}),-1.0]])]});}
            var Q46;
            {var subQ0=sQuery(id+"F36.wireOp",EDGE,"E759.right");var subQ1=sQuery(id+"F36.wireOp",EDGE,"E749.bottom");var subQ2=makeQuery(id+"F36.imprint","INTERSECT",VERTEX,{"derivedFrom":[subQ1,subQ0]});Q46=makeQuery(id+"F36.imprint","IMPRINT",FACE,{"disambiguationData":[TD([[makeQuery(id+"F36.imprint","IMPRINT",EDGE,{"disambiguationData":[TD([[subQ2,-1.0]])],"derivedFrom":subQ1}),-1.0]])]});}
            var Q47;
            {var subQ0=sQuery(id+"F36.wireOp",EDGE,"E759.left");var subQ1=sQuery(id+"F36.wireOp",EDGE,"E749.bottom");var subQ2=makeQuery(id+"F36.imprint","INTERSECT",VERTEX,{"derivedFrom":[subQ1,subQ0]});Q47=makeQuery(id+"F36.imprint","IMPRINT",FACE,{"disambiguationData":[TD([[makeQuery(id+"F36.imprint","IMPRINT",EDGE,{"disambiguationData":[TD([[subQ2,-1.0]])],"derivedFrom":subQ1}),-1.0]])]});}
            var Q48;
            {var subQ0=sQuery(id+"F36.wireOp",EDGE,"E760.right");var subQ1=sQuery(id+"F36.wireOp",EDGE,"E749.bottom");var subQ2=makeQuery(id+"F36.imprint","INTERSECT",VERTEX,{"derivedFrom":[subQ1,subQ0]});Q48=makeQuery(id+"F36.imprint","IMPRINT",FACE,{"disambiguationData":[TD([[makeQuery(id+"F36.imprint","IMPRINT",EDGE,{"disambiguationData":[TD([[subQ2,-1.0]])],"derivedFrom":subQ1}),-1.0]])]});}
            var Q49;
            {var subQ0=sQuery(id+"F36.wireOp",EDGE,"E755.left");var subQ1=sQuery(id+"F36.wireOp",EDGE,"E743.bottom");var subQ2=makeQuery(id+"F36.imprint","INTERSECT",VERTEX,{"derivedFrom":[subQ1,subQ0]});Q49=makeQuery(id+"F36.imprint","IMPRINT",FACE,{"disambiguationData":[TD([[makeQuery(id+"F36.imprint","IMPRINT",EDGE,{"disambiguationData":[TD([[subQ2,-1.0]])],"derivedFrom":subQ1}),-1.0]])]});}
            var Q50;
            {var subQ0=sQuery(id+"F36.wireOp",EDGE,"E755.left");var subQ1=sQuery(id+"F36.wireOp",EDGE,"E743.top");var subQ2=makeQuery(id+"F36.imprint","INTERSECT",VERTEX,{"derivedFrom":[subQ1,subQ0]});Q50=makeQuery(id+"F36.imprint","IMPRINT",FACE,{"disambiguationData":[TD([[makeQuery(id+"F36.imprint","IMPRINT",EDGE,{"disambiguationData":[TD([[subQ2,-1.0]])],"derivedFrom":subQ1}),-1.0]])]});}
            var Q51;
            {var subQ0=sQuery(id+"F36.wireOp",EDGE,"E755.left");var subQ1=sQuery(id+"F36.wireOp",EDGE,"E742.top");var subQ2=makeQuery(id+"F36.imprint","INTERSECT",VERTEX,{"derivedFrom":[subQ1,subQ0]});Q51=makeQuery(id+"F36.imprint","IMPRINT",FACE,{"disambiguationData":[TD([[makeQuery(id+"F36.imprint","IMPRINT",EDGE,{"disambiguationData":[TD([[subQ2,-1.0]])],"derivedFrom":subQ1}),-1.0]])]});}
            var Q52;
            {var subQ0=sQuery(id+"F36.wireOp",EDGE,"E755.left");var subQ1=sQuery(id+"F36.wireOp",EDGE,"E741.bottom");var subQ2=makeQuery(id+"F36.imprint","INTERSECT",VERTEX,{"derivedFrom":[subQ1,subQ0]});Q52=makeQuery(id+"F36.imprint","IMPRINT",FACE,{"disambiguationData":[TD([[makeQuery(id+"F36.imprint","IMPRINT",EDGE,{"disambiguationData":[TD([[subQ2,-1.0]])],"derivedFrom":subQ1}),-1.0]])]});}
            var Q53;
            {var subQ0=sQuery(id+"F36.wireOp",EDGE,"E755.left");var subQ1=sQuery(id+"F36.wireOp",EDGE,"E741.top");var subQ2=makeQuery(id+"F36.imprint","INTERSECT",VERTEX,{"derivedFrom":[subQ1,subQ0]});Q53=makeQuery(id+"F36.imprint","IMPRINT",FACE,{"disambiguationData":[TD([[makeQuery(id+"F36.imprint","IMPRINT",EDGE,{"disambiguationData":[TD([[subQ2,-1.0]])],"derivedFrom":subQ1}),-1.0]])]});}
            var Q54;
            {var subQ0=sQuery(id+"F36.wireOp",EDGE,"E755.left");var subQ1=sQuery(id+"F36.wireOp",EDGE,"E740.top");var subQ2=makeQuery(id+"F36.imprint","INTERSECT",VERTEX,{"derivedFrom":[subQ1,subQ0]});Q54=makeQuery(id+"F36.imprint","IMPRINT",FACE,{"disambiguationData":[TD([[makeQuery(id+"F36.imprint","IMPRINT",EDGE,{"disambiguationData":[TD([[subQ2,-1.0]])],"derivedFrom":subQ1}),-1.0]])]});}
            var Q55;
            {var subQ0=sQuery(id+"F36.wireOp",EDGE,"E758.right");var subQ1=sQuery(id+"F36.wireOp",EDGE,"E746.top");var subQ2=makeQuery(id+"F36.imprint","INTERSECT",VERTEX,{"derivedFrom":[subQ1,subQ0]});Q55=makeQuery(id+"F36.imprint","IMPRINT",FACE,{"disambiguationData":[TD([[makeQuery(id+"F36.imprint","IMPRINT",EDGE,{"disambiguationData":[TD([[subQ2,-1.0]])],"derivedFrom":subQ1}),-1.0]])]});}
            var Q56;
            {var subQ0=sQuery(id+"F36.wireOp",EDGE,"E759.right");var subQ1=sQuery(id+"F36.wireOp",EDGE,"E746.top");var subQ2=makeQuery(id+"F36.imprint","INTERSECT",VERTEX,{"derivedFrom":[subQ1,subQ0]});Q56=makeQuery(id+"F36.imprint","IMPRINT",FACE,{"disambiguationData":[TD([[makeQuery(id+"F36.imprint","IMPRINT",EDGE,{"disambiguationData":[TD([[subQ2,-1.0]])],"derivedFrom":subQ1}),-1.0]])]});}
            var Q57;
            {var subQ0=sQuery(id+"F36.wireOp",EDGE,"E759.left");var subQ1=sQuery(id+"F36.wireOp",EDGE,"E746.top");var subQ2=makeQuery(id+"F36.imprint","INTERSECT",VERTEX,{"derivedFrom":[subQ1,subQ0]});Q57=makeQuery(id+"F36.imprint","IMPRINT",FACE,{"disambiguationData":[TD([[makeQuery(id+"F36.imprint","IMPRINT",EDGE,{"disambiguationData":[TD([[subQ2,-1.0]])],"derivedFrom":subQ1}),-1.0]])]});}
            var Q58;
            {var subQ0=sQuery(id+"F36.wireOp",EDGE,"E760.right");var subQ1=sQuery(id+"F36.wireOp",EDGE,"E746.top");var subQ2=makeQuery(id+"F36.imprint","INTERSECT",VERTEX,{"derivedFrom":[subQ1,subQ0]});Q58=makeQuery(id+"F36.imprint","IMPRINT",FACE,{"disambiguationData":[TD([[makeQuery(id+"F36.imprint","IMPRINT",EDGE,{"disambiguationData":[TD([[subQ2,-1.0]])],"derivedFrom":subQ1}),-1.0]])]});}
            var Q59;
            {var subQ0=sQuery(id+"F36.wireOp",EDGE,"E761.right");var subQ1=sQuery(id+"F36.wireOp",EDGE,"E746.top");var subQ2=makeQuery(id+"F36.imprint","INTERSECT",VERTEX,{"derivedFrom":[subQ1,subQ0]});Q59=makeQuery(id+"F36.imprint","IMPRINT",FACE,{"disambiguationData":[TD([[makeQuery(id+"F36.imprint","IMPRINT",EDGE,{"disambiguationData":[TD([[subQ2,-1.0]])],"derivedFrom":subQ1}),-1.0]])]});}
            var Q60;
            {var subQ0=sQuery(id+"F36.wireOp",EDGE,"E761.left");var subQ1=sQuery(id+"F36.wireOp",EDGE,"E746.top");var subQ2=makeQuery(id+"F36.imprint","INTERSECT",VERTEX,{"derivedFrom":[subQ1,subQ0]});Q60=makeQuery(id+"F36.imprint","IMPRINT",FACE,{"disambiguationData":[TD([[makeQuery(id+"F36.imprint","IMPRINT",EDGE,{"disambiguationData":[TD([[subQ2,-1.0]])],"derivedFrom":subQ1}),-1.0]])]});}
            var Q61;
            {var subQ0=sQuery(id+"F36.wireOp",EDGE,"E766.right");var subQ1=sQuery(id+"F36.wireOp",EDGE,"E740.top");var subQ2=makeQuery(id+"F36.imprint","INTERSECT",VERTEX,{"derivedFrom":[subQ1,subQ0]});Q61=makeQuery(id+"F36.imprint","IMPRINT",FACE,{"disambiguationData":[TD([[makeQuery(id+"F36.imprint","IMPRINT",EDGE,{"disambiguationData":[TD([[subQ2,-1.0]])],"derivedFrom":subQ1}),-1.0]])]});}
            var Q62;
            {var subQ0=sQuery(id+"F36.wireOp",EDGE,"E766.right");var subQ1=sQuery(id+"F36.wireOp",EDGE,"E741.top");var subQ2=makeQuery(id+"F36.imprint","INTERSECT",VERTEX,{"derivedFrom":[subQ1,subQ0]});Q62=makeQuery(id+"F36.imprint","IMPRINT",FACE,{"disambiguationData":[TD([[makeQuery(id+"F36.imprint","IMPRINT",EDGE,{"disambiguationData":[TD([[subQ2,-1.0]])],"derivedFrom":subQ1}),-1.0]])]});}
            var Q63;
            {var subQ0=sQuery(id+"F36.wireOp",EDGE,"E766.right");var subQ1=sQuery(id+"F36.wireOp",EDGE,"E742.top");var subQ2=makeQuery(id+"F36.imprint","INTERSECT",VERTEX,{"derivedFrom":[subQ1,subQ0]});Q63=makeQuery(id+"F36.imprint","IMPRINT",FACE,{"disambiguationData":[TD([[makeQuery(id+"F36.imprint","IMPRINT",EDGE,{"disambiguationData":[TD([[subQ2,-1.0]])],"derivedFrom":subQ1}),-1.0]])]});}
            var Q64;
            {var subQ0=sQuery(id+"F36.wireOp",EDGE,"E766.right");var subQ1=sQuery(id+"F36.wireOp",EDGE,"E741.bottom");var subQ2=makeQuery(id+"F36.imprint","INTERSECT",VERTEX,{"derivedFrom":[subQ1,subQ0]});Q64=makeQuery(id+"F36.imprint","IMPRINT",FACE,{"disambiguationData":[TD([[makeQuery(id+"F36.imprint","IMPRINT",EDGE,{"disambiguationData":[TD([[subQ2,-1.0]])],"derivedFrom":subQ1}),-1.0]])]});}
            var Q65;
            {var subQ0=sQuery(id+"F36.wireOp",EDGE,"E766.right");var subQ1=sQuery(id+"F36.wireOp",EDGE,"E743.top");var subQ2=makeQuery(id+"F36.imprint","INTERSECT",VERTEX,{"derivedFrom":[subQ1,subQ0]});Q65=makeQuery(id+"F36.imprint","IMPRINT",FACE,{"disambiguationData":[TD([[makeQuery(id+"F36.imprint","IMPRINT",EDGE,{"disambiguationData":[TD([[subQ2,-1.0]])],"derivedFrom":subQ1}),-1.0]])]});}
            var Q66;
            {var subQ0=sQuery(id+"F36.wireOp",EDGE,"E766.right");var subQ1=sQuery(id+"F36.wireOp",EDGE,"E743.bottom");var subQ2=makeQuery(id+"F36.imprint","INTERSECT",VERTEX,{"derivedFrom":[subQ1,subQ0]});Q66=makeQuery(id+"F36.imprint","IMPRINT",FACE,{"disambiguationData":[TD([[makeQuery(id+"F36.imprint","IMPRINT",EDGE,{"disambiguationData":[TD([[subQ2,-1.0]])],"derivedFrom":subQ1}),-1.0]])]});}
            var Q67;
            {var subQ0=sQuery(id+"F36.wireOp",EDGE,"E792.MirrorCS");var subQ1=sQuery(id+"F36.wireOp",EDGE,"E777.MirrorCS");var subQ2=makeQuery(id+"F36.imprint","INTERSECT",VERTEX,{"derivedFrom":[subQ1,subQ0]});Q67=makeQuery(id+"F36.imprint","IMPRINT",FACE,{"disambiguationData":[TD([[makeQuery(id+"F36.imprint","IMPRINT",EDGE,{"disambiguationData":[TD([[subQ2,-1.0]])],"derivedFrom":subQ1}),1.0]])]});}
            var Q68;
            {var subQ0=sQuery(id+"F36.wireOp",EDGE,"E771.right");var subQ1=sQuery(id+"F36.wireOp",EDGE,"E748.top");var subQ2=makeQuery(id+"F36.imprint","INTERSECT",VERTEX,{"derivedFrom":[subQ1,subQ0]});Q68=makeQuery(id+"F36.imprint","IMPRINT",FACE,{"disambiguationData":[TD([[makeQuery(id+"F36.imprint","IMPRINT",EDGE,{"disambiguationData":[TD([[subQ2,-1.0]])],"derivedFrom":subQ1}),-1.0]])]});}
            var Q69;
            {var subQ0=sQuery(id+"F36.wireOp",EDGE,"E770.left");var subQ1=sQuery(id+"F36.wireOp",EDGE,"E748.top");var subQ2=makeQuery(id+"F36.imprint","INTERSECT",VERTEX,{"derivedFrom":[subQ1,subQ0]});Q69=makeQuery(id+"F36.imprint","IMPRINT",FACE,{"disambiguationData":[TD([[makeQuery(id+"F36.imprint","IMPRINT",EDGE,{"disambiguationData":[TD([[subQ2,-1.0]])],"derivedFrom":subQ1}),-1.0]])]});}
            var Q70;
            {var subQ0=sQuery(id+"F36.wireOp",EDGE,"E792.MirrorCS");var subQ5=sQuery(id+"F36.wireOp",EDGE,"E777.MirrorCS");var subQ6=makeQuery(id+"F36.imprint","INTERSECT",VERTEX,{"derivedFrom":[subQ5,subQ0]});Q70=makeQuery(id+"F36.imprint","IMPRINT",FACE,{"disambiguationData":[TD([[makeQuery(id+"F36.imprint","IMPRINT",EDGE,{"disambiguationData":[TD([[subQ6,-1.0]])],"derivedFrom":subQ5}),-1.0]])]});}
            var Q71;
            {var subQ1=sQuery(id+"F36.wireOp",EDGE,"E748.top");var subQ3=sQuery(id+"F36.wireOp",EDGE,"E769.right");var subQ4=makeQuery(id+"F36.imprint","INTERSECT",VERTEX,{"derivedFrom":[subQ1,subQ3]});Q71=makeQuery(id+"F36.imprint","IMPRINT",FACE,{"disambiguationData":[TD([[makeQuery(id+"F36.imprint","IMPRINT",EDGE,{"disambiguationData":[TD([[subQ4,-1.0]])],"derivedFrom":subQ3}),1.0]])]});}
            var Q72;
            {var subQ0=sQuery(id+"F36.wireOp",EDGE,"E770.right");var subQ1=sQuery(id+"F36.wireOp",EDGE,"E748.top");var subQ2=makeQuery(id+"F36.imprint","INTERSECT",VERTEX,{"derivedFrom":[subQ1,subQ0]});Q72=makeQuery(id+"F36.imprint","IMPRINT",FACE,{"disambiguationData":[TD([[makeQuery(id+"F36.imprint","IMPRINT",EDGE,{"disambiguationData":[TD([[subQ2,-1.0]])],"derivedFrom":subQ1}),-1.0]])]});}
            extrude(context, id + "F37", {"entities" : qUnion([Q0, Q1, Q2, Q3, Q4, Q5, Q6, Q7, Q8, Q9, Q10, Q11, Q12, Q13, Q14, Q15, Q16, Q17, Q18, Q19, Q20, Q21, Q22, Q23, Q24, Q25, Q26, Q27, Q28, Q29, Q30, Q31, Q32, Q33, Q34, Q35, Q36, Q37, Q38, Q39, Q40, Q41, Q42, Q43, Q44, Q45, Q46, Q47, Q48, Q49, Q50, Q51, Q52, Q53, Q54, Q55, Q56, Q57, Q58, Q59, Q60, Q61, Q62, Q63, Q64, Q65, Q66, Q67, Q68, Q69, Q70, Q71, Q72]), "operationType" : NewBodyOperationType.REMOVE, "oppositeDirection" : true, "depth" : 1.5 * mm, "offsetDistance" : 25 * mm});
        }
    });
